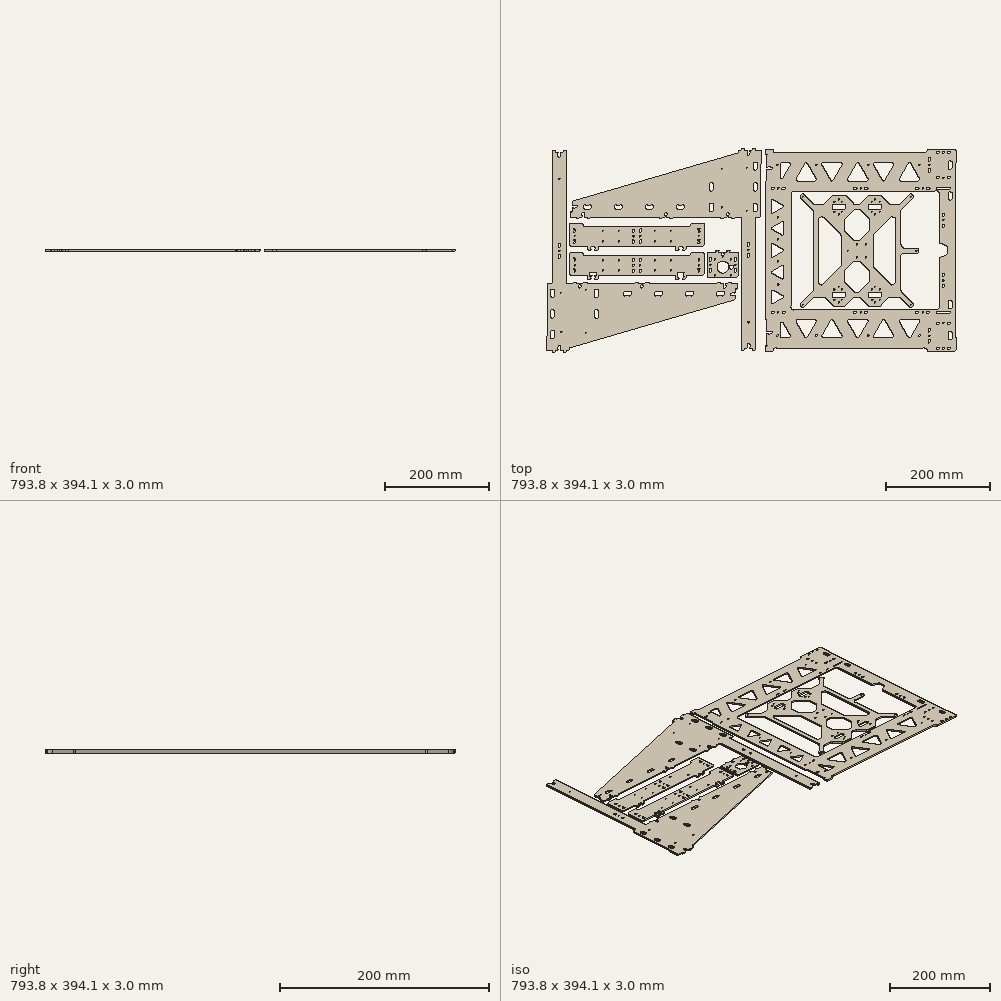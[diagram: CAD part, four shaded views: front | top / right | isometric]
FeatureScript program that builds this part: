
annotation { "Feature Type Name" : "Feature", "Feature Type Description" : "" }
export const myFeature = defineFeature(function(context is Context, id is Id, definition is map)
    precondition{}
    {
        {
            var Q0;
            Q0=qCreatedBy(makeId("Top.planeOp"),FACE);
            var sketch = newSketch(context, id + "F0", { "sketchPlane" : qUnion([Q0])});
            skFitSpline(sketch, "E0", {"points": [v(-205.76, 143.1) * mm, v(-205.54, 143.1) * mm, v(-205.33, 143.16) * mm, v(-205.16, 143.3) * mm]});
            skFitSpline(sketch, "E1", {"points": [v(-211.3, 181.1) * mm, v(-211.08, 181.1) * mm, v(-210.87, 181.16) * mm, v(-210.7, 181.3) * mm]});
            skFitSpline(sketch, "E2", {"points": [v(-203.99, 186.1) * mm, v(-204.2, 186.1) * mm, v(-204.41, 186.02) * mm, v(-204.59, 185.89) * mm]});
            skLineSegment(sketch, "E3", {"start": v(-205.16, 143.3) * mm, "end": v(-198.78, 148.1) * mm});
            skLineSegment(sketch, "E4", {"start": v(-210.7, 181.3) * mm, "end": v(-204.59, 185.89) * mm});
            skLineSegment(sketch, "E5", {"start": v(-213.3, 181.1) * mm, "end": v(-211.3, 181.1) * mm});
            skFitSpline(sketch, "E6", {"points": [v(-141.15, -185.58) * mm, v(-140.94, -185.58) * mm, v(-140.72, -185.5) * mm, v(-140.55, -185.38) * mm]});
            skFitSpline(sketch, "E7", {"points": [v(-146.69, -147.58) * mm, v(-146.47, -147.58) * mm, v(-146.26, -147.5) * mm, v(-146.09, -147.38) * mm]});
            skFitSpline(sketch, "E8", {"points": [v(-139.38, -142.58) * mm, v(-139.6, -142.58) * mm, v(-139.8, -142.65) * mm, v(-139.98, -142.78) * mm]});
            skLineSegment(sketch, "E9", {"start": v(-207.76, 143.1) * mm, "end": v(-205.9, 143.1) * mm});
            skLineSegment(sketch, "E10", {"start": v(-205.9, 143.1) * mm, "end": v(-205.76, 143.1) * mm});
            skLineSegment(sketch, "E11", {"start": v(-205.76, 143.1) * mm, "end": v(-205.76, 143.1) * mm});
            skLineSegment(sketch, "E12", {"start": v(-140.55, -185.38) * mm, "end": v(-134.18, -180.58) * mm});
            skLineSegment(sketch, "E13", {"start": v(-146.09, -147.38) * mm, "end": v(-139.98, -142.78) * mm});
            skLineSegment(sketch, "E14", {"start": v(-148.69, -147.58) * mm, "end": v(-146.68, -147.58) * mm});
            skFitSpline(sketch, "E15", {"points": [v(-352, -188.94) * mm, v(-352.22, -189) * mm, v(-352.36, -189.2) * mm, v(-352.36, -189.42) * mm]});
            skLineSegment(sketch, "E16", {"start": v(-143.15, -185.58) * mm, "end": v(-141.3, -185.58) * mm});
            skLineSegment(sketch, "E17", {"start": v(-141.3, -185.58) * mm, "end": v(-141.16, -185.58) * mm});
            skLineSegment(sketch, "E18", {"start": v(-141.16, -185.58) * mm, "end": v(-141.15, -185.58) * mm});
            skLineSegment(sketch, "E19", {"start": v(-396.81, -189.04) * mm, "end": v(-396.81, -194.04) * mm});
            skFitSpline(sketch, "E20", {"points": [v(-25.17, 188.94) * mm, v(-24.96, 189) * mm, v(-24.81, 189.2) * mm, v(-24.81, 189.42) * mm]});
            skLineSegment(sketch, "E21", {"start": v(-352.36, -189.42) * mm, "end": v(-352.36, -194.04) * mm});
            skFitSpline(sketch, "E22", {"points": [v(396.81, 190.1) * mm, v(396.81, 192.86) * mm, v(394.57, 195.1) * mm, v(391.81, 195.1) * mm]});
            skLineSegment(sketch, "E23", {"start": v(19.64, 194.04) * mm, "end": v(19.64, 189.04) * mm});
            skFitSpline(sketch, "E24", {"points": [v(332.72, 189.1) * mm, v(336.37, 189.1) * mm, v(339.55, 191.56) * mm, v(340.46, 195.1) * mm]});
            skLineSegment(sketch, "E25", {"start": v(-24.81, 194.04) * mm, "end": v(-24.81, 189.42) * mm});
            skFitSpline(sketch, "E26", {"points": [v(41.82, 195.1) * mm, v(42.73, 191.56) * mm, v(45.91, 189.1) * mm, v(49.56, 189.1) * mm]});
            skLineSegment(sketch, "E27", {"start": v(394.81, 168.1) * mm, "end": v(396.81, 170.1) * mm});
            skLineSegment(sketch, "E28", {"start": v(396.81, 170.1) * mm, "end": v(396.81, 190.1) * mm});
            skFitSpline(sketch, "E29", {"points": [v(29.05, 185.1) * mm, v(29.23, 185.1) * mm, v(29.4, 185.2) * mm, v(29.48, 185.35) * mm]});
            skFitSpline(sketch, "E30", {"points": [v(30.17, 184.66) * mm, v(30.35, 184.77) * mm, v(30.45, 184.98) * mm, v(30.4, 185.18) * mm]});
            skFitSpline(sketch, "E31", {"points": [v(30.4, 185.18) * mm, v(30.37, 185.4) * mm, v(30.21, 185.55) * mm, v(30, 185.59) * mm]});
            skFitSpline(sketch, "E32", {"points": [v(30, 185.59) * mm, v(29.8, 185.63) * mm, v(29.59, 185.53) * mm, v(29.48, 185.35) * mm]});
            skFitSpline(sketch, "E33", {"points": [v(30.17, 184.66) * mm, v(30.01, 184.57) * mm, v(29.92, 184.4) * mm, v(29.92, 184.23) * mm]});
            skLineSegment(sketch, "E34", {"start": v(391.81, 195.1) * mm, "end": v(340.46, 195.1) * mm});
            skFitSpline(sketch, "E35", {"points": [v(29.92, 134.31) * mm, v(29.92, 134.13) * mm, v(30.01, 133.97) * mm, v(30.17, 133.88) * mm]});
            skFitSpline(sketch, "E36", {"points": [v(29.48, 133.2) * mm, v(29.59, 133.01) * mm, v(29.8, 132.92) * mm, v(30, 132.95) * mm]});
            skFitSpline(sketch, "E37", {"points": [v(30, 132.95) * mm, v(30.21, 133) * mm, v(30.37, 133.15) * mm, v(30.4, 133.36) * mm]});
            skFitSpline(sketch, "E38", {"points": [v(30.4, 133.36) * mm, v(30.45, 133.57) * mm, v(30.35, 133.77) * mm, v(30.17, 133.88) * mm]});
            skFitSpline(sketch, "E39", {"points": [v(29.48, 133.2) * mm, v(29.4, 133.35) * mm, v(29.23, 133.45) * mm, v(29.05, 133.45) * mm]});
            skLineSegment(sketch, "E40", {"start": v(332.72, 189.1) * mm, "end": v(49.56, 189.1) * mm});
            skFitSpline(sketch, "E41", {"points": [v(29.05, -133.25) * mm, v(29.23, -133.25) * mm, v(29.4, -133.16) * mm, v(29.48, -133) * mm]});
            skFitSpline(sketch, "E42", {"points": [v(30.17, -133.68) * mm, v(30.35, -133.58) * mm, v(30.45, -133.37) * mm, v(30.4, -133.16) * mm]});
            skFitSpline(sketch, "E43", {"points": [v(30.4, -133.16) * mm, v(30.37, -132.96) * mm, v(30.21, -132.8) * mm, v(30, -132.76) * mm]});
            skFitSpline(sketch, "E44", {"points": [v(30, -132.76) * mm, v(29.8, -132.72) * mm, v(29.59, -132.82) * mm, v(29.48, -133) * mm]});
            skFitSpline(sketch, "E45", {"points": [v(30.17, -133.68) * mm, v(30.01, -133.77) * mm, v(29.92, -133.94) * mm, v(29.92, -134.12) * mm]});
            skLineSegment(sketch, "E46", {"start": v(41.82, 195.1) * mm, "end": v(26.82, 195.1) * mm});
            skLineSegment(sketch, "E47", {"start": v(26.82, 195.1) * mm, "end": v(26.82, 185.1) * mm});
            skLineSegment(sketch, "E48", {"start": v(26.82, 185.1) * mm, "end": v(29.05, 185.1) * mm});
            skFitSpline(sketch, "E49", {"points": [v(29.92, -184.03) * mm, v(29.92, -184.21) * mm, v(30.01, -184.38) * mm, v(30.17, -184.47) * mm]});
            skFitSpline(sketch, "E50", {"points": [v(29.48, -185.15) * mm, v(29.59, -185.33) * mm, v(29.8, -185.43) * mm, v(30, -185.4) * mm]});
            skFitSpline(sketch, "E51", {"points": [v(30, -185.4) * mm, v(30.21, -185.36) * mm, v(30.37, -185.2) * mm, v(30.4, -184.99) * mm]});
            skFitSpline(sketch, "E52", {"points": [v(30.4, -184.99) * mm, v(30.45, -184.78) * mm, v(30.35, -184.57) * mm, v(30.17, -184.47) * mm]});
            skFitSpline(sketch, "E53", {"points": [v(29.48, -185.15) * mm, v(29.4, -185) * mm, v(29.23, -184.9) * mm, v(29.05, -184.9) * mm]});
            skLineSegment(sketch, "E54", {"start": v(29.92, 184.23) * mm, "end": v(29.92, 160.87) * mm});
            skLineSegment(sketch, "E55", {"start": v(29.92, 160.87) * mm, "end": v(32.92, 160.87) * mm});
            skLineSegment(sketch, "E56", {"start": v(32.92, 160.87) * mm, "end": v(32.92, 162.15) * mm});
            skLineSegment(sketch, "E57", {"start": v(32.92, 162.15) * mm, "end": v(36.92, 162.15) * mm});
            skLineSegment(sketch, "E58", {"start": v(36.92, 162.15) * mm, "end": v(36.92, 160.87) * mm});
            skLineSegment(sketch, "E59", {"start": v(36.92, 160.87) * mm, "end": v(39.92, 160.87) * mm});
            skLineSegment(sketch, "E60", {"start": v(39.92, 160.87) * mm, "end": v(39.92, 157.67) * mm});
            skLineSegment(sketch, "E61", {"start": v(39.92, 157.67) * mm, "end": v(36.92, 157.67) * mm});
            skLineSegment(sketch, "E62", {"start": v(36.92, 157.67) * mm, "end": v(36.92, 156.4) * mm});
            skLineSegment(sketch, "E63", {"start": v(36.92, 156.4) * mm, "end": v(32.92, 156.4) * mm});
            skLineSegment(sketch, "E64", {"start": v(32.92, 156.4) * mm, "end": v(32.92, 157.67) * mm});
            skLineSegment(sketch, "E65", {"start": v(32.92, 157.67) * mm, "end": v(29.92, 157.67) * mm});
            skLineSegment(sketch, "E66", {"start": v(29.92, 157.67) * mm, "end": v(29.92, 134.31) * mm});
            skFitSpline(sketch, "E67", {"points": [v(49.56, -188.9) * mm, v(45.91, -188.9) * mm, v(42.73, -191.37) * mm, v(41.82, -194.9) * mm]});
            skLineSegment(sketch, "E68", {"start": v(29.05, 133.45) * mm, "end": v(26.82, 133.45) * mm});
            skLineSegment(sketch, "E69", {"start": v(26.82, 133.45) * mm, "end": v(26.82, -133.25) * mm});
            skLineSegment(sketch, "E70", {"start": v(26.82, -133.25) * mm, "end": v(29.05, -133.25) * mm});
            skFitSpline(sketch, "E71", {"points": [v(340.46, -194.9) * mm, v(339.55, -191.37) * mm, v(336.37, -188.9) * mm, v(332.72, -188.9) * mm]});
            skLineSegment(sketch, "E72", {"start": v(29.92, -134.12) * mm, "end": v(29.92, -157.48) * mm});
            skLineSegment(sketch, "E73", {"start": v(29.92, -157.48) * mm, "end": v(32.92, -157.48) * mm});
            skLineSegment(sketch, "E74", {"start": v(32.92, -157.48) * mm, "end": v(32.92, -156.2) * mm});
            skLineSegment(sketch, "E75", {"start": v(32.92, -156.2) * mm, "end": v(36.92, -156.2) * mm});
            skLineSegment(sketch, "E76", {"start": v(36.92, -156.2) * mm, "end": v(36.92, -157.48) * mm});
            skLineSegment(sketch, "E77", {"start": v(36.92, -157.48) * mm, "end": v(39.92, -157.48) * mm});
            skLineSegment(sketch, "E78", {"start": v(39.92, -157.48) * mm, "end": v(39.92, -160.68) * mm});
            skLineSegment(sketch, "E79", {"start": v(39.92, -160.68) * mm, "end": v(36.92, -160.68) * mm});
            skLineSegment(sketch, "E80", {"start": v(36.92, -160.68) * mm, "end": v(36.92, -161.95) * mm});
            skLineSegment(sketch, "E81", {"start": v(36.92, -161.95) * mm, "end": v(32.92, -161.95) * mm});
            skLineSegment(sketch, "E82", {"start": v(32.92, -161.95) * mm, "end": v(32.92, -160.68) * mm});
            skLineSegment(sketch, "E83", {"start": v(32.92, -160.68) * mm, "end": v(29.92, -160.68) * mm});
            skLineSegment(sketch, "E84", {"start": v(29.92, -160.68) * mm, "end": v(29.92, -184.03) * mm});
            skFitSpline(sketch, "E85", {"points": [v(391.81, -194.9) * mm, v(394.58, -194.9) * mm, v(396.81, -192.66) * mm, v(396.81, -189.9) * mm]});
            skLineSegment(sketch, "E86", {"start": v(29.05, -184.9) * mm, "end": v(26.82, -184.9) * mm});
            skLineSegment(sketch, "E87", {"start": v(26.82, -184.9) * mm, "end": v(26.82, -194.9) * mm});
            skLineSegment(sketch, "E88", {"start": v(26.82, -194.9) * mm, "end": v(41.82, -194.9) * mm});
            skLineSegment(sketch, "E89", {"start": v(49.56, -188.9) * mm, "end": v(332.72, -188.9) * mm});
            skFitSpline(sketch, "E90", {"points": [v(378.81, 6.82) * mm, v(378.81, 7.6) * mm, v(378.36, 8.3) * mm, v(377.66, 8.64) * mm]});
            skLineSegment(sketch, "E91", {"start": v(340.46, -194.9) * mm, "end": v(391.81, -194.9) * mm});
            skFitSpline(sketch, "E92", {"points": [v(363.69, 16.43) * mm, v(363.69, 15.65) * mm, v(364.14, 14.94) * mm, v(364.84, 14.61) * mm]});
            skLineSegment(sketch, "E93", {"start": v(396.81, -189.9) * mm, "end": v(396.81, -169.9) * mm});
            skLineSegment(sketch, "E94", {"start": v(396.81, -169.9) * mm, "end": v(394.81, -167.9) * mm});
            skLineSegment(sketch, "E95", {"start": v(394.81, -167.9) * mm, "end": v(394.81, 168.1) * mm});
            skFitSpline(sketch, "E96", {"points": [v(363.69, 107.1) * mm, v(363.69, 111.5) * mm, v(360.12, 115.09) * mm, v(355.7, 115.1) * mm]});
            skLineSegment(sketch, "E97", {"start": v(378.81, -6.62) * mm, "end": v(378.81, 6.82) * mm});
            skFitSpline(sketch, "E98", {"points": [v(84.82, 115.1) * mm, v(82.7, 115.1) * mm, v(80.66, 114.25) * mm, v(79.16, 112.75) * mm]});
            skFitSpline(sketch, "E99", {"points": [v(79.16, 112.75) * mm, v(77.66, 111.25) * mm, v(76.82, 109.22) * mm, v(76.82, 107.1) * mm]});
            skLineSegment(sketch, "E100", {"start": v(377.66, 8.64) * mm, "end": v(364.84, 14.61) * mm});
            skFitSpline(sketch, "E101", {"points": [v(76.82, -106.9) * mm, v(76.82, -111.32) * mm, v(80.4, -114.9) * mm, v(84.82, -114.9) * mm]});
            skLineSegment(sketch, "E102", {"start": v(363.69, 16.43) * mm, "end": v(363.69, 107.1) * mm});
            skFitSpline(sketch, "E103", {"points": [v(355.7, -114.9) * mm, v(360.12, -114.9) * mm, v(363.69, -111.31) * mm, v(363.69, -106.9) * mm]});
            skLineSegment(sketch, "E104", {"start": v(355.7, 115.1) * mm, "end": v(84.82, 115.1) * mm});
            skFitSpline(sketch, "E105", {"points": [v(364.85, -14.31) * mm, v(364.14, -14.64) * mm, v(363.69, -15.35) * mm, v(363.69, -16.13) * mm]});
            skLineSegment(sketch, "E106", {"start": v(76.82, 107.1) * mm, "end": v(76.82, -106.9) * mm});
            skFitSpline(sketch, "E107", {"points": [v(377.65, -8.44) * mm, v(378.36, -8.11) * mm, v(378.81, -7.4) * mm, v(378.81, -6.62) * mm]});
            skLineSegment(sketch, "E108", {"start": v(84.82, -114.9) * mm, "end": v(355.7, -114.9) * mm});
            skFitSpline(sketch, "E109", {"points": [v(289.45, -134.33) * mm, v(288.38, -134.33) * mm, v(287.39, -134.9) * mm, v(286.85, -135.83) * mm]});
            skFitSpline(sketch, "E110", {"points": [v(286.85, -135.83) * mm, v(286.32, -136.76) * mm, v(286.32, -137.9) * mm, v(286.85, -138.83) * mm]});
            skLineSegment(sketch, "E111", {"start": v(363.69, -106.9) * mm, "end": v(363.69, -16.13) * mm});
            skFitSpline(sketch, "E112", {"points": [v(303.55, -167.76) * mm, v(304.1, -168.68) * mm, v(305.08, -169.26) * mm, v(306.15, -169.26) * mm]});
            skFitSpline(sketch, "E113", {"points": [v(306.15, -169.26) * mm, v(307.22, -169.26) * mm, v(308.21, -168.68) * mm, v(308.75, -167.76) * mm]});
            skLineSegment(sketch, "E114", {"start": v(364.85, -14.31) * mm, "end": v(377.65, -8.44) * mm});
            skFitSpline(sketch, "E115", {"points": [v(325.45, -138.83) * mm, v(325.99, -137.9) * mm, v(325.99, -136.76) * mm, v(325.45, -135.83) * mm]});
            skFitSpline(sketch, "E116", {"points": [v(325.45, -135.83) * mm, v(324.92, -134.9) * mm, v(323.92, -134.33) * mm, v(322.85, -134.33) * mm]});
            skLineSegment(sketch, "E117", {"start": v(322.85, -134.33) * mm, "end": v(289.45, -134.33) * mm});
            skFitSpline(sketch, "E118", {"points": [v(236.85, -164.76) * mm, v(236.32, -165.68) * mm, v(236.32, -166.83) * mm, v(236.85, -167.76) * mm]});
            skFitSpline(sketch, "E119", {"points": [v(236.85, -167.76) * mm, v(237.4, -168.68) * mm, v(238.38, -169.26) * mm, v(239.45, -169.26) * mm]});
            skLineSegment(sketch, "E120", {"start": v(286.85, -138.83) * mm, "end": v(303.55, -167.76) * mm});
            skFitSpline(sketch, "E121", {"points": [v(258.75, -135.83) * mm, v(258.22, -134.9) * mm, v(257.23, -134.33) * mm, v(256.15, -134.33) * mm]});
            skFitSpline(sketch, "E122", {"points": [v(256.15, -134.33) * mm, v(255.08, -134.33) * mm, v(254.1, -134.9) * mm, v(253.56, -135.83) * mm]});
            skLineSegment(sketch, "E123", {"start": v(308.75, -167.76) * mm, "end": v(325.45, -138.83) * mm});
            skFitSpline(sketch, "E124", {"points": [v(272.85, -169.26) * mm, v(273.93, -169.26) * mm, v(274.92, -168.68) * mm, v(275.45, -167.76) * mm]});
            skFitSpline(sketch, "E125", {"points": [v(275.45, -167.76) * mm, v(275.99, -166.83) * mm, v(275.99, -165.68) * mm, v(275.45, -164.76) * mm]});
            skLineSegment(sketch, "E126", {"start": v(272.85, -169.26) * mm, "end": v(239.45, -169.26) * mm});
            skFitSpline(sketch, "E127", {"points": [v(189.45, -134.33) * mm, v(188.38, -134.33) * mm, v(187.4, -134.9) * mm, v(186.85, -135.83) * mm]});
            skFitSpline(sketch, "E128", {"points": [v(186.85, -135.83) * mm, v(186.32, -136.76) * mm, v(186.32, -137.9) * mm, v(186.85, -138.83) * mm]});
            skLineSegment(sketch, "E129", {"start": v(236.85, -164.76) * mm, "end": v(253.56, -135.83) * mm});
            skFitSpline(sketch, "E130", {"points": [v(203.56, -167.76) * mm, v(204.1, -168.68) * mm, v(205.08, -169.26) * mm, v(206.15, -169.26) * mm]});
            skFitSpline(sketch, "E131", {"points": [v(206.15, -169.26) * mm, v(207.23, -169.26) * mm, v(208.22, -168.68) * mm, v(208.75, -167.76) * mm]});
            skLineSegment(sketch, "E132", {"start": v(258.75, -135.83) * mm, "end": v(275.45, -164.76) * mm});
            skFitSpline(sketch, "E133", {"points": [v(225.45, -138.83) * mm, v(225.99, -137.9) * mm, v(225.99, -136.76) * mm, v(225.45, -135.83) * mm]});
            skFitSpline(sketch, "E134", {"points": [v(225.45, -135.83) * mm, v(224.92, -134.9) * mm, v(223.93, -134.33) * mm, v(222.85, -134.33) * mm]});
            skLineSegment(sketch, "E135", {"start": v(222.85, -134.33) * mm, "end": v(189.45, -134.33) * mm});
            skFitSpline(sketch, "E136", {"points": [v(136.86, -164.76) * mm, v(136.32, -165.68) * mm, v(136.32, -166.83) * mm, v(136.86, -167.76) * mm]});
            skFitSpline(sketch, "E137", {"points": [v(136.86, -167.76) * mm, v(137.4, -168.68) * mm, v(138.38, -169.26) * mm, v(139.45, -169.26) * mm]});
            skLineSegment(sketch, "E138", {"start": v(186.85, -138.83) * mm, "end": v(203.56, -167.76) * mm});
            skFitSpline(sketch, "E139", {"points": [v(158.75, -135.83) * mm, v(158.22, -134.9) * mm, v(157.23, -134.33) * mm, v(156.15, -134.33) * mm]});
            skFitSpline(sketch, "E140", {"points": [v(156.15, -134.33) * mm, v(155.08, -134.33) * mm, v(154.1, -134.9) * mm, v(153.56, -135.83) * mm]});
            skLineSegment(sketch, "E141", {"start": v(208.75, -167.76) * mm, "end": v(225.45, -138.83) * mm});
            skFitSpline(sketch, "E142", {"points": [v(172.86, -169.26) * mm, v(173.93, -169.26) * mm, v(174.92, -168.68) * mm, v(175.45, -167.76) * mm]});
            skFitSpline(sketch, "E143", {"points": [v(175.45, -167.76) * mm, v(175.99, -166.83) * mm, v(175.99, -165.68) * mm, v(175.45, -164.76) * mm]});
            skLineSegment(sketch, "E144", {"start": v(172.86, -169.26) * mm, "end": v(139.45, -169.26) * mm});
            skFitSpline(sketch, "E145", {"points": [v(89.45, -134.33) * mm, v(88.38, -134.33) * mm, v(87.4, -134.9) * mm, v(86.86, -135.83) * mm]});
            skFitSpline(sketch, "E146", {"points": [v(86.86, -135.83) * mm, v(86.32, -136.76) * mm, v(86.32, -137.9) * mm, v(86.86, -138.83) * mm]});
            skLineSegment(sketch, "E147", {"start": v(136.86, -164.76) * mm, "end": v(153.56, -135.83) * mm});
            skFitSpline(sketch, "E148", {"points": [v(103.56, -167.76) * mm, v(104.1, -168.68) * mm, v(105.08, -169.26) * mm, v(106.15, -169.26) * mm]});
            skFitSpline(sketch, "E149", {"points": [v(106.15, -169.26) * mm, v(107.23, -169.26) * mm, v(108.22, -168.68) * mm, v(108.75, -167.76) * mm]});
            skLineSegment(sketch, "E150", {"start": v(158.75, -135.83) * mm, "end": v(175.45, -164.76) * mm});
            skFitSpline(sketch, "E151", {"points": [v(125.45, -138.83) * mm, v(125.99, -137.9) * mm, v(125.99, -136.76) * mm, v(125.45, -135.83) * mm]});
            skFitSpline(sketch, "E152", {"points": [v(125.45, -135.83) * mm, v(124.92, -134.9) * mm, v(123.93, -134.33) * mm, v(122.86, -134.33) * mm]});
            skLineSegment(sketch, "E153", {"start": v(122.86, -134.33) * mm, "end": v(89.45, -134.33) * mm});
            skFitSpline(sketch, "E154", {"points": [v(286.85, 139.02) * mm, v(286.32, 138.1) * mm, v(286.32, 136.95) * mm, v(286.85, 136.02) * mm]});
            skFitSpline(sketch, "E155", {"points": [v(286.85, 136.02) * mm, v(287.39, 135.1) * mm, v(288.38, 134.52) * mm, v(289.45, 134.52) * mm]});
            skLineSegment(sketch, "E156", {"start": v(86.86, -138.83) * mm, "end": v(103.56, -167.76) * mm});
            skFitSpline(sketch, "E157", {"points": [v(308.75, 167.95) * mm, v(308.21, 168.88) * mm, v(307.22, 169.45) * mm, v(306.15, 169.45) * mm]});
            skFitSpline(sketch, "E158", {"points": [v(306.15, 169.45) * mm, v(305.08, 169.45) * mm, v(304.1, 168.88) * mm, v(303.55, 167.95) * mm]});
            skLineSegment(sketch, "E159", {"start": v(108.75, -167.76) * mm, "end": v(125.45, -138.83) * mm});
            skFitSpline(sketch, "E160", {"points": [v(322.85, 134.52) * mm, v(323.92, 134.52) * mm, v(324.92, 135.1) * mm, v(325.45, 136.02) * mm]});
            skFitSpline(sketch, "E161", {"points": [v(325.45, 136.02) * mm, v(325.99, 136.95) * mm, v(325.99, 138.1) * mm, v(325.45, 139.02) * mm]});
            skLineSegment(sketch, "E162", {"start": v(322.85, 134.52) * mm, "end": v(289.45, 134.52) * mm});
            skFitSpline(sketch, "E163", {"points": [v(239.45, 169.45) * mm, v(238.38, 169.45) * mm, v(237.4, 168.88) * mm, v(236.85, 167.95) * mm]});
            skFitSpline(sketch, "E164", {"points": [v(236.85, 167.95) * mm, v(236.32, 167.02) * mm, v(236.32, 165.88) * mm, v(236.85, 164.95) * mm]});
            skLineSegment(sketch, "E165", {"start": v(286.85, 139.02) * mm, "end": v(303.55, 167.95) * mm});
            skFitSpline(sketch, "E166", {"points": [v(253.56, 136.02) * mm, v(254.1, 135.1) * mm, v(255.08, 134.52) * mm, v(256.15, 134.52) * mm]});
            skFitSpline(sketch, "E167", {"points": [v(256.15, 134.52) * mm, v(257.23, 134.52) * mm, v(258.22, 135.1) * mm, v(258.75, 136.02) * mm]});
            skLineSegment(sketch, "E168", {"start": v(308.75, 167.95) * mm, "end": v(325.45, 139.02) * mm});
            skFitSpline(sketch, "E169", {"points": [v(275.45, 164.95) * mm, v(275.99, 165.88) * mm, v(275.99, 167.02) * mm, v(275.45, 167.95) * mm]});
            skFitSpline(sketch, "E170", {"points": [v(275.45, 167.95) * mm, v(274.92, 168.88) * mm, v(273.93, 169.45) * mm, v(272.85, 169.45) * mm]});
            skLineSegment(sketch, "E171", {"start": v(272.85, 169.45) * mm, "end": v(239.45, 169.45) * mm});
            skFitSpline(sketch, "E172", {"points": [v(186.85, 139.02) * mm, v(186.32, 138.1) * mm, v(186.32, 136.95) * mm, v(186.85, 136.02) * mm]});
            skFitSpline(sketch, "E173", {"points": [v(186.85, 136.02) * mm, v(187.4, 135.1) * mm, v(188.38, 134.52) * mm, v(189.45, 134.52) * mm]});
            skLineSegment(sketch, "E174", {"start": v(236.85, 164.95) * mm, "end": v(253.56, 136.02) * mm});
            skFitSpline(sketch, "E175", {"points": [v(208.75, 167.95) * mm, v(208.22, 168.88) * mm, v(207.23, 169.45) * mm, v(206.15, 169.45) * mm]});
            skFitSpline(sketch, "E176", {"points": [v(206.15, 169.45) * mm, v(205.08, 169.45) * mm, v(204.1, 168.88) * mm, v(203.56, 167.95) * mm]});
            skLineSegment(sketch, "E177", {"start": v(258.75, 136.02) * mm, "end": v(275.45, 164.95) * mm});
            skFitSpline(sketch, "E178", {"points": [v(222.85, 134.52) * mm, v(223.93, 134.52) * mm, v(224.92, 135.1) * mm, v(225.45, 136.02) * mm]});
            skFitSpline(sketch, "E179", {"points": [v(225.45, 136.02) * mm, v(225.99, 136.95) * mm, v(225.99, 138.1) * mm, v(225.45, 139.02) * mm]});
            skLineSegment(sketch, "E180", {"start": v(222.85, 134.52) * mm, "end": v(189.45, 134.52) * mm});
            skFitSpline(sketch, "E181", {"points": [v(139.45, 169.45) * mm, v(138.38, 169.45) * mm, v(137.4, 168.88) * mm, v(136.86, 167.95) * mm]});
            skFitSpline(sketch, "E182", {"points": [v(136.86, 167.95) * mm, v(136.32, 167.02) * mm, v(136.32, 165.88) * mm, v(136.86, 164.95) * mm]});
            skLineSegment(sketch, "E183", {"start": v(186.85, 139.02) * mm, "end": v(203.56, 167.95) * mm});
            skFitSpline(sketch, "E184", {"points": [v(153.56, 136.02) * mm, v(154.1, 135.1) * mm, v(155.08, 134.52) * mm, v(156.15, 134.52) * mm]});
            skFitSpline(sketch, "E185", {"points": [v(156.15, 134.52) * mm, v(157.23, 134.52) * mm, v(158.22, 135.1) * mm, v(158.75, 136.02) * mm]});
            skLineSegment(sketch, "E186", {"start": v(208.75, 167.95) * mm, "end": v(225.45, 139.02) * mm});
            skFitSpline(sketch, "E187", {"points": [v(175.45, 164.95) * mm, v(175.99, 165.88) * mm, v(175.99, 167.02) * mm, v(175.45, 167.95) * mm]});
            skFitSpline(sketch, "E188", {"points": [v(175.45, 167.95) * mm, v(174.92, 168.88) * mm, v(173.93, 169.45) * mm, v(172.86, 169.45) * mm]});
            skLineSegment(sketch, "E189", {"start": v(172.86, 169.45) * mm, "end": v(139.45, 169.45) * mm});
            skFitSpline(sketch, "E190", {"points": [v(86.86, 139.02) * mm, v(86.32, 138.1) * mm, v(86.32, 136.95) * mm, v(86.86, 136.02) * mm]});
            skFitSpline(sketch, "E191", {"points": [v(86.86, 136.02) * mm, v(87.4, 135.1) * mm, v(88.38, 134.52) * mm, v(89.45, 134.52) * mm]});
            skLineSegment(sketch, "E192", {"start": v(136.86, 164.95) * mm, "end": v(153.56, 136.02) * mm});
            skFitSpline(sketch, "E193", {"points": [v(108.75, 167.95) * mm, v(108.22, 168.88) * mm, v(107.23, 169.45) * mm, v(106.15, 169.45) * mm]});
            skFitSpline(sketch, "E194", {"points": [v(106.15, 169.45) * mm, v(105.08, 169.45) * mm, v(104.1, 168.88) * mm, v(103.56, 167.95) * mm]});
            skLineSegment(sketch, "E195", {"start": v(158.75, 136.02) * mm, "end": v(175.45, 164.95) * mm});
            skFitSpline(sketch, "E196", {"points": [v(122.86, 134.52) * mm, v(123.93, 134.52) * mm, v(124.92, 135.1) * mm, v(125.45, 136.02) * mm]});
            skFitSpline(sketch, "E197", {"points": [v(125.45, 136.02) * mm, v(125.99, 136.95) * mm, v(125.99, 138.1) * mm, v(125.45, 139.02) * mm]});
            skLineSegment(sketch, "E198", {"start": v(122.86, 134.52) * mm, "end": v(89.45, 134.52) * mm});
            skFitSpline(sketch, "E199", {"points": [v(39.12, -101.23) * mm, v(39.12, -101.95) * mm, v(39.51, -102.62) * mm, v(40.14, -102.98) * mm]});
            skFitSpline(sketch, "E200", {"points": [v(40.14, -102.98) * mm, v(40.76, -103.34) * mm, v(41.54, -103.34) * mm, v(42.16, -102.98) * mm]});
            skLineSegment(sketch, "E201", {"start": v(86.86, 139.02) * mm, "end": v(103.56, 167.95) * mm});
            skFitSpline(sketch, "E202", {"points": [v(61.69, -91.7) * mm, v(62.31, -91.35) * mm, v(62.7, -90.68) * mm, v(62.7, -89.96) * mm]});
            skFitSpline(sketch, "E203", {"points": [v(62.7, -89.96) * mm, v(62.7, -89.23) * mm, v(62.31, -88.56) * mm, v(61.69, -88.2) * mm]});
            skLineSegment(sketch, "E204", {"start": v(108.75, 167.95) * mm, "end": v(125.45, 139.02) * mm});
            skFitSpline(sketch, "E205", {"points": [v(42.16, -76.93) * mm, v(41.54, -76.57) * mm, v(40.76, -76.57) * mm, v(40.14, -76.93) * mm]});
            skFitSpline(sketch, "E206", {"points": [v(40.14, -76.93) * mm, v(39.51, -77.3) * mm, v(39.12, -77.96) * mm, v(39.12, -78.68) * mm]});
            skLineSegment(sketch, "E207", {"start": v(39.12, -78.68) * mm, "end": v(39.12, -101.23) * mm});
            skFitSpline(sketch, "E208", {"points": [v(59.66, -55.44) * mm, v(60.29, -55.8) * mm, v(61.06, -55.8) * mm, v(61.69, -55.44) * mm]});
            skFitSpline(sketch, "E209", {"points": [v(61.69, -55.44) * mm, v(62.31, -55.08) * mm, v(62.7, -54.4) * mm, v(62.7, -53.68) * mm]});
            skLineSegment(sketch, "E210", {"start": v(42.16, -102.98) * mm, "end": v(61.69, -91.7) * mm});
            skFitSpline(sketch, "E211", {"points": [v(40.14, -40.66) * mm, v(39.51, -41.02) * mm, v(39.12, -41.69) * mm, v(39.12, -42.41) * mm]});
            skFitSpline(sketch, "E212", {"points": [v(39.12, -42.41) * mm, v(39.12, -43.13) * mm, v(39.51, -43.8) * mm, v(40.14, -44.16) * mm]});
            skLineSegment(sketch, "E213", {"start": v(61.69, -88.2) * mm, "end": v(42.16, -76.93) * mm});
            skFitSpline(sketch, "E214", {"points": [v(62.7, -31.14) * mm, v(62.7, -30.41) * mm, v(62.31, -29.75) * mm, v(61.69, -29.38) * mm]});
            skFitSpline(sketch, "E215", {"points": [v(61.69, -29.38) * mm, v(61.06, -29.02) * mm, v(60.29, -29.02) * mm, v(59.66, -29.38) * mm]});
            skLineSegment(sketch, "E216", {"start": v(62.7, -31.14) * mm, "end": v(62.7, -53.68) * mm});
            skFitSpline(sketch, "E217", {"points": [v(39.12, -11.18) * mm, v(39.12, -11.9) * mm, v(39.51, -12.58) * mm, v(40.14, -12.94) * mm]});
            skFitSpline(sketch, "E218", {"points": [v(40.14, -12.94) * mm, v(40.76, -13.3) * mm, v(41.54, -13.3) * mm, v(42.16, -12.94) * mm]});
            skLineSegment(sketch, "E219", {"start": v(59.66, -55.44) * mm, "end": v(40.14, -44.16) * mm});
            skFitSpline(sketch, "E220", {"points": [v(61.69, -1.66) * mm, v(62.31, -1.3) * mm, v(62.7, -0.63) * mm, v(62.7, 0.09) * mm]});
            skFitSpline(sketch, "E221", {"points": [v(62.7, 0.09) * mm, v(62.7, 0.81) * mm, v(62.31, 1.48) * mm, v(61.69, 1.84) * mm]});
            skLineSegment(sketch, "E222", {"start": v(40.14, -40.66) * mm, "end": v(59.66, -29.38) * mm});
            skFitSpline(sketch, "E223", {"points": [v(42.16, 13.12) * mm, v(41.54, 13.48) * mm, v(40.76, 13.48) * mm, v(40.14, 13.12) * mm]});
            skFitSpline(sketch, "E224", {"points": [v(40.14, 13.12) * mm, v(39.51, 12.75) * mm, v(39.12, 12.09) * mm, v(39.12, 11.36) * mm]});
            skLineSegment(sketch, "E225", {"start": v(39.12, 11.36) * mm, "end": v(39.12, -11.18) * mm});
            skFitSpline(sketch, "E226", {"points": [v(59.66, 29.57) * mm, v(60.29, 29.2) * mm, v(61.06, 29.2) * mm, v(61.69, 29.57) * mm]});
            skFitSpline(sketch, "E227", {"points": [v(61.69, 29.57) * mm, v(62.31, 29.93) * mm, v(62.7, 30.6) * mm, v(62.7, 31.32) * mm]});
            skLineSegment(sketch, "E228", {"start": v(42.16, -12.94) * mm, "end": v(61.69, -1.66) * mm});
            skFitSpline(sketch, "E229", {"points": [v(40.14, 44.35) * mm, v(39.51, 43.99) * mm, v(39.12, 43.32) * mm, v(39.12, 42.6) * mm]});
            skFitSpline(sketch, "E230", {"points": [v(39.12, 42.6) * mm, v(39.12, 41.87) * mm, v(39.51, 41.2) * mm, v(40.14, 40.84) * mm]});
            skLineSegment(sketch, "E231", {"start": v(61.69, 1.84) * mm, "end": v(42.16, 13.12) * mm});
            skFitSpline(sketch, "E232", {"points": [v(62.7, 53.87) * mm, v(62.7, 54.6) * mm, v(62.31, 55.26) * mm, v(61.69, 55.62) * mm]});
            skFitSpline(sketch, "E233", {"points": [v(61.69, 55.62) * mm, v(61.06, 55.99) * mm, v(60.29, 55.99) * mm, v(59.66, 55.62) * mm]});
            skLineSegment(sketch, "E234", {"start": v(62.7, 53.87) * mm, "end": v(62.7, 31.32) * mm});
            skFitSpline(sketch, "E235", {"points": [v(39.12, 73.82) * mm, v(39.12, 73.1) * mm, v(39.51, 72.43) * mm, v(40.14, 72.07) * mm]});
            skFitSpline(sketch, "E236", {"points": [v(40.14, 72.07) * mm, v(40.76, 71.7) * mm, v(41.54, 71.7) * mm, v(42.16, 72.07) * mm]});
            skLineSegment(sketch, "E237", {"start": v(59.66, 29.57) * mm, "end": v(40.14, 40.84) * mm});
            skFitSpline(sketch, "E238", {"points": [v(61.69, 83.34) * mm, v(62.31, 83.7) * mm, v(62.7, 84.37) * mm, v(62.7, 85.1) * mm]});
            skFitSpline(sketch, "E239", {"points": [v(62.7, 85.1) * mm, v(62.7, 85.82) * mm, v(62.31, 86.49) * mm, v(61.69, 86.85) * mm]});
            skLineSegment(sketch, "E240", {"start": v(40.14, 44.35) * mm, "end": v(59.66, 55.62) * mm});
            skFitSpline(sketch, "E241", {"points": [v(42.16, 98.12) * mm, v(41.54, 98.49) * mm, v(40.76, 98.49) * mm, v(40.14, 98.12) * mm]});
            skFitSpline(sketch, "E242", {"points": [v(40.14, 98.12) * mm, v(39.51, 97.76) * mm, v(39.12, 97.1) * mm, v(39.12, 96.37) * mm]});
            skLineSegment(sketch, "E243", {"start": v(39.12, 96.37) * mm, "end": v(39.12, 73.82) * mm});
            skFitSpline(sketch, "E244", {"points": [v(388.81, -160.9) * mm, v(388.81, -159.47) * mm, v(388.05, -158.15) * mm, v(386.81, -157.44) * mm]});
            skFitSpline(sketch, "E245", {"points": [v(386.81, -157.44) * mm, v(385.58, -156.72) * mm, v(384.05, -156.72) * mm, v(382.81, -157.44) * mm]});
            skFitSpline(sketch, "E246", {"points": [v(382.81, -157.44) * mm, v(381.58, -158.15) * mm, v(380.81, -159.47) * mm, v(380.81, -160.9) * mm]});
            skLineSegment(sketch, "E247", {"start": v(42.16, 72.07) * mm, "end": v(61.69, 83.34) * mm});
            skFitSpline(sketch, "E248", {"points": [v(380.81, -168.9) * mm, v(380.81, -170.33) * mm, v(381.58, -171.65) * mm, v(382.81, -172.36) * mm]});
            skFitSpline(sketch, "E249", {"points": [v(382.81, -172.36) * mm, v(384.05, -173.08) * mm, v(385.58, -173.08) * mm, v(386.81, -172.36) * mm]});
            skFitSpline(sketch, "E250", {"points": [v(386.81, -172.36) * mm, v(388.05, -171.65) * mm, v(388.81, -170.33) * mm, v(388.81, -168.9) * mm]});
            skLineSegment(sketch, "E251", {"start": v(61.69, 86.85) * mm, "end": v(42.16, 98.12) * mm});
            skFitSpline(sketch, "E252", {"points": [v(388.81, -100.9) * mm, v(388.81, -99.47) * mm, v(388.05, -98.15) * mm, v(386.81, -97.44) * mm]});
            skFitSpline(sketch, "E253", {"points": [v(386.81, -97.44) * mm, v(385.58, -96.72) * mm, v(384.05, -96.72) * mm, v(382.81, -97.44) * mm]});
            skFitSpline(sketch, "E254", {"points": [v(382.81, -97.44) * mm, v(381.58, -98.15) * mm, v(380.81, -99.47) * mm, v(380.81, -100.9) * mm]});
            skLineSegment(sketch, "E255", {"start": v(388.81, -168.9) * mm, "end": v(388.81, -160.9) * mm});
            skFitSpline(sketch, "E256", {"points": [v(380.81, -108.9) * mm, v(380.81, -110.33) * mm, v(381.58, -111.65) * mm, v(382.81, -112.37) * mm]});
            skFitSpline(sketch, "E257", {"points": [v(382.81, -112.37) * mm, v(384.05, -113.08) * mm, v(385.58, -113.08) * mm, v(386.81, -112.37) * mm]});
            skFitSpline(sketch, "E258", {"points": [v(386.81, -112.37) * mm, v(388.05, -111.65) * mm, v(388.81, -110.33) * mm, v(388.81, -108.9) * mm]});
            skLineSegment(sketch, "E259", {"start": v(380.81, -160.9) * mm, "end": v(380.81, -168.9) * mm});
            skFitSpline(sketch, "E260", {"points": [v(388.81, 109.1) * mm, v(388.81, 110.53) * mm, v(388.05, 111.85) * mm, v(386.81, 112.56) * mm]});
            skFitSpline(sketch, "E261", {"points": [v(386.81, 112.56) * mm, v(385.58, 113.28) * mm, v(384.05, 113.28) * mm, v(382.81, 112.56) * mm]});
            skFitSpline(sketch, "E262", {"points": [v(382.81, 112.56) * mm, v(381.58, 111.85) * mm, v(380.81, 110.53) * mm, v(380.81, 109.1) * mm]});
            skLineSegment(sketch, "E263", {"start": v(388.81, -108.9) * mm, "end": v(388.81, -100.9) * mm});
            skFitSpline(sketch, "E264", {"points": [v(380.81, 101.1) * mm, v(380.81, 99.67) * mm, v(381.58, 98.35) * mm, v(382.81, 97.63) * mm]});
            skFitSpline(sketch, "E265", {"points": [v(382.81, 97.63) * mm, v(384.05, 96.92) * mm, v(385.58, 96.92) * mm, v(386.81, 97.63) * mm]});
            skFitSpline(sketch, "E266", {"points": [v(386.81, 97.63) * mm, v(388.05, 98.35) * mm, v(388.81, 99.67) * mm, v(388.81, 101.1) * mm]});
            skLineSegment(sketch, "E267", {"start": v(380.81, -100.9) * mm, "end": v(380.81, -108.9) * mm});
            skFitSpline(sketch, "E268", {"points": [v(388.81, 169.1) * mm, v(388.81, 170.53) * mm, v(388.05, 171.85) * mm, v(386.81, 172.56) * mm]});
            skFitSpline(sketch, "E269", {"points": [v(386.81, 172.56) * mm, v(385.58, 173.27) * mm, v(384.05, 173.27) * mm, v(382.81, 172.56) * mm]});
            skFitSpline(sketch, "E270", {"points": [v(382.81, 172.56) * mm, v(381.58, 171.85) * mm, v(380.81, 170.53) * mm, v(380.81, 169.1) * mm]});
            skLineSegment(sketch, "E271", {"start": v(388.81, 101.1) * mm, "end": v(388.81, 109.1) * mm});
            skFitSpline(sketch, "E272", {"points": [v(380.81, 161.1) * mm, v(380.81, 159.67) * mm, v(381.58, 158.35) * mm, v(382.81, 157.63) * mm]});
            skFitSpline(sketch, "E273", {"points": [v(382.81, 157.63) * mm, v(384.05, 156.92) * mm, v(385.58, 156.92) * mm, v(386.81, 157.63) * mm]});
            skFitSpline(sketch, "E274", {"points": [v(386.81, 157.63) * mm, v(388.05, 158.35) * mm, v(388.81, 159.67) * mm, v(388.81, 161.1) * mm]});
            skFitSpline(sketch, "E275", {"points": [v(358.11, -119.3) * mm, v(358.11, -119.11) * mm, v(358.02, -118.95) * mm, v(357.86, -118.86) * mm]});
            skFitSpline(sketch, "E276", {"points": [v(358.55, -118.18) * mm, v(358.44, -118) * mm, v(358.23, -117.9) * mm, v(358.03, -117.93) * mm]});
            skFitSpline(sketch, "E277", {"points": [v(358.03, -117.93) * mm, v(357.82, -117.97) * mm, v(357.66, -118.13) * mm, v(357.62, -118.34) * mm]});
            skFitSpline(sketch, "E278", {"points": [v(357.62, -118.34) * mm, v(357.58, -118.55) * mm, v(357.68, -118.75) * mm, v(357.86, -118.86) * mm]});
            skFitSpline(sketch, "E279", {"points": [v(358.55, -118.18) * mm, v(358.64, -118.33) * mm, v(358.8, -118.43) * mm, v(358.98, -118.43) * mm]});
            skLineSegment(sketch, "E280", {"start": v(380.81, 109.1) * mm, "end": v(380.81, 101.1) * mm});
            skFitSpline(sketch, "E281", {"points": [v(384.65, -118.43) * mm, v(384.83, -118.43) * mm, v(385, -118.33) * mm, v(385.08, -118.18) * mm]});
            skFitSpline(sketch, "E282", {"points": [v(385.76, -118.86) * mm, v(385.95, -118.75) * mm, v(386.04, -118.55) * mm, v(386, -118.34) * mm]});
            skFitSpline(sketch, "E283", {"points": [v(386, -118.34) * mm, v(385.97, -118.13) * mm, v(385.8, -117.97) * mm, v(385.6, -117.93) * mm]});
            skFitSpline(sketch, "E284", {"points": [v(385.6, -117.93) * mm, v(385.4, -117.9) * mm, v(385.19, -118) * mm, v(385.08, -118.18) * mm]});
            skFitSpline(sketch, "E285", {"points": [v(385.76, -118.86) * mm, v(385.6, -118.95) * mm, v(385.51, -119.11) * mm, v(385.51, -119.3) * mm]});
            skLineSegment(sketch, "E286", {"start": v(388.81, 161.1) * mm, "end": v(388.81, 169.1) * mm});
            skFitSpline(sketch, "E287", {"points": [v(385.51, -120.86) * mm, v(385.51, -121.04) * mm, v(385.6, -121.2) * mm, v(385.76, -121.3) * mm]});
            skFitSpline(sketch, "E288", {"points": [v(385.08, -121.98) * mm, v(385.19, -122.16) * mm, v(385.4, -122.25) * mm, v(385.6, -122.22) * mm]});
            skFitSpline(sketch, "E289", {"points": [v(385.6, -122.22) * mm, v(385.8, -122.18) * mm, v(385.97, -122.02) * mm, v(386, -121.81) * mm]});
            skFitSpline(sketch, "E290", {"points": [v(386, -121.81) * mm, v(386.04, -121.6) * mm, v(385.95, -121.4) * mm, v(385.76, -121.3) * mm]});
            skFitSpline(sketch, "E291", {"points": [v(385.08, -121.98) * mm, v(385, -121.82) * mm, v(384.83, -121.73) * mm, v(384.65, -121.73) * mm]});
            skLineSegment(sketch, "E292", {"start": v(380.81, 169.1) * mm, "end": v(380.81, 161.1) * mm});
            skFitSpline(sketch, "E293", {"points": [v(358.98, -121.73) * mm, v(358.8, -121.73) * mm, v(358.64, -121.82) * mm, v(358.55, -121.98) * mm]});
            skFitSpline(sketch, "E294", {"points": [v(357.86, -121.3) * mm, v(357.68, -121.4) * mm, v(357.58, -121.6) * mm, v(357.62, -121.81) * mm]});
            skFitSpline(sketch, "E295", {"points": [v(357.62, -121.81) * mm, v(357.66, -122.02) * mm, v(357.82, -122.18) * mm, v(358.03, -122.22) * mm]});
            skFitSpline(sketch, "E296", {"points": [v(358.03, -122.22) * mm, v(358.23, -122.25) * mm, v(358.44, -122.16) * mm, v(358.55, -121.98) * mm]});
            skFitSpline(sketch, "E297", {"points": [v(357.86, -121.3) * mm, v(358.02, -121.2) * mm, v(358.11, -121.04) * mm, v(358.11, -120.86) * mm]});
            skLineSegment(sketch, "E298", {"start": v(358.98, -118.43) * mm, "end": v(384.65, -118.43) * mm});
            skFitSpline(sketch, "E299", {"points": [v(358.11, 121.06) * mm, v(358.11, 121.23) * mm, v(358.02, 121.4) * mm, v(357.86, 121.49) * mm]});
            skFitSpline(sketch, "E300", {"points": [v(358.55, 122.17) * mm, v(358.44, 122.35) * mm, v(358.23, 122.45) * mm, v(358.03, 122.41) * mm]});
            skFitSpline(sketch, "E301", {"points": [v(358.03, 122.41) * mm, v(357.82, 122.38) * mm, v(357.66, 122.22) * mm, v(357.62, 122) * mm]});
            skFitSpline(sketch, "E302", {"points": [v(357.62, 122) * mm, v(357.58, 121.8) * mm, v(357.68, 121.6) * mm, v(357.86, 121.49) * mm]});
            skFitSpline(sketch, "E303", {"points": [v(358.55, 122.17) * mm, v(358.64, 122.02) * mm, v(358.8, 121.92) * mm, v(358.98, 121.92) * mm]});
            skLineSegment(sketch, "E304", {"start": v(385.51, -119.3) * mm, "end": v(385.51, -120.86) * mm});
            skFitSpline(sketch, "E305", {"points": [v(384.65, 121.92) * mm, v(384.83, 121.92) * mm, v(385, 122.02) * mm, v(385.08, 122.17) * mm]});
            skFitSpline(sketch, "E306", {"points": [v(385.76, 121.49) * mm, v(385.95, 121.6) * mm, v(386.04, 121.8) * mm, v(386, 122) * mm]});
            skFitSpline(sketch, "E307", {"points": [v(386, 122) * mm, v(385.97, 122.22) * mm, v(385.8, 122.38) * mm, v(385.6, 122.41) * mm]});
            skFitSpline(sketch, "E308", {"points": [v(385.6, 122.41) * mm, v(385.4, 122.45) * mm, v(385.19, 122.35) * mm, v(385.08, 122.17) * mm]});
            skFitSpline(sketch, "E309", {"points": [v(385.76, 121.49) * mm, v(385.6, 121.4) * mm, v(385.51, 121.23) * mm, v(385.51, 121.06) * mm]});
            skLineSegment(sketch, "E310", {"start": v(384.65, -121.73) * mm, "end": v(358.98, -121.73) * mm});
            skFitSpline(sketch, "E311", {"points": [v(385.51, 119.49) * mm, v(385.51, 119.3) * mm, v(385.6, 119.14) * mm, v(385.76, 119.05) * mm]});
            skFitSpline(sketch, "E312", {"points": [v(385.08, 118.37) * mm, v(385.19, 118.19) * mm, v(385.4, 118.1) * mm, v(385.6, 118.13) * mm]});
            skFitSpline(sketch, "E313", {"points": [v(385.6, 118.13) * mm, v(385.8, 118.17) * mm, v(385.97, 118.33) * mm, v(386, 118.53) * mm]});
            skFitSpline(sketch, "E314", {"points": [v(386, 118.53) * mm, v(386.04, 118.74) * mm, v(385.95, 118.95) * mm, v(385.76, 119.05) * mm]});
            skFitSpline(sketch, "E315", {"points": [v(385.08, 118.37) * mm, v(385, 118.53) * mm, v(384.83, 118.62) * mm, v(384.65, 118.62) * mm]});
            skLineSegment(sketch, "E316", {"start": v(358.11, -120.86) * mm, "end": v(358.11, -119.3) * mm});
            skFitSpline(sketch, "E317", {"points": [v(358.98, 118.62) * mm, v(358.8, 118.62) * mm, v(358.64, 118.53) * mm, v(358.55, 118.37) * mm]});
            skFitSpline(sketch, "E318", {"points": [v(357.86, 119.05) * mm, v(357.68, 118.95) * mm, v(357.58, 118.74) * mm, v(357.62, 118.53) * mm]});
            skFitSpline(sketch, "E319", {"points": [v(357.62, 118.53) * mm, v(357.66, 118.33) * mm, v(357.82, 118.17) * mm, v(358.03, 118.13) * mm]});
            skFitSpline(sketch, "E320", {"points": [v(358.03, 118.13) * mm, v(358.23, 118.1) * mm, v(358.44, 118.19) * mm, v(358.55, 118.37) * mm]});
            skFitSpline(sketch, "E321", {"points": [v(357.86, 119.05) * mm, v(358.02, 119.14) * mm, v(358.11, 119.3) * mm, v(358.11, 119.49) * mm]});
            skLineSegment(sketch, "E322", {"start": v(358.98, 121.92) * mm, "end": v(384.65, 121.92) * mm});
            skFitSpline(sketch, "E323", {"points": [v(379.31, -188.94) * mm, v(379.31, -188.76) * mm, v(379.22, -188.6) * mm, v(379.06, -188.5) * mm]});
            skFitSpline(sketch, "E324", {"points": [v(379.75, -187.82) * mm, v(379.64, -187.64) * mm, v(379.43, -187.54) * mm, v(379.23, -187.58) * mm]});
            skFitSpline(sketch, "E325", {"points": [v(379.23, -187.58) * mm, v(379.02, -187.61) * mm, v(378.86, -187.78) * mm, v(378.82, -187.98) * mm]});
            skFitSpline(sketch, "E326", {"points": [v(378.82, -187.98) * mm, v(378.78, -188.2) * mm, v(378.88, -188.4) * mm, v(379.06, -188.5) * mm]});
            skFitSpline(sketch, "E327", {"points": [v(379.75, -187.82) * mm, v(379.84, -187.98) * mm, v(380, -188.07) * mm, v(380.18, -188.07) * mm]});
            skLineSegment(sketch, "E328", {"start": v(385.51, 121.06) * mm, "end": v(385.51, 119.49) * mm});
            skFitSpline(sketch, "E329", {"points": [v(384.65, -188.07) * mm, v(384.83, -188.07) * mm, v(385, -187.98) * mm, v(385.08, -187.82) * mm]});
            skFitSpline(sketch, "E330", {"points": [v(385.76, -188.5) * mm, v(385.95, -188.4) * mm, v(386.04, -188.2) * mm, v(386, -187.98) * mm]});
            skFitSpline(sketch, "E331", {"points": [v(386, -187.98) * mm, v(385.97, -187.78) * mm, v(385.8, -187.61) * mm, v(385.6, -187.58) * mm]});
            skFitSpline(sketch, "E332", {"points": [v(385.6, -187.58) * mm, v(385.4, -187.54) * mm, v(385.19, -187.64) * mm, v(385.08, -187.82) * mm]});
            skFitSpline(sketch, "E333", {"points": [v(385.76, -188.5) * mm, v(385.6, -188.6) * mm, v(385.51, -188.76) * mm, v(385.51, -188.94) * mm]});
            skLineSegment(sketch, "E334", {"start": v(384.65, 118.62) * mm, "end": v(358.98, 118.62) * mm});
            skFitSpline(sketch, "E335", {"points": [v(385.51, -190.5) * mm, v(385.51, -190.68) * mm, v(385.6, -190.85) * mm, v(385.76, -190.94) * mm]});
            skFitSpline(sketch, "E336", {"points": [v(385.08, -191.62) * mm, v(385.19, -191.8) * mm, v(385.4, -191.9) * mm, v(385.6, -191.86) * mm]});
            skFitSpline(sketch, "E337", {"points": [v(385.6, -191.86) * mm, v(385.8, -191.83) * mm, v(385.97, -191.66) * mm, v(386, -191.46) * mm]});
            skFitSpline(sketch, "E338", {"points": [v(386, -191.46) * mm, v(386.04, -191.25) * mm, v(385.95, -191.04) * mm, v(385.76, -190.94) * mm]});
            skFitSpline(sketch, "E339", {"points": [v(385.08, -191.62) * mm, v(385, -191.47) * mm, v(384.83, -191.37) * mm, v(384.65, -191.37) * mm]});
            skLineSegment(sketch, "E340", {"start": v(358.11, 119.49) * mm, "end": v(358.11, 121.06) * mm});
            skFitSpline(sketch, "E341", {"points": [v(380.18, -191.37) * mm, v(380, -191.37) * mm, v(379.84, -191.47) * mm, v(379.75, -191.62) * mm]});
            skFitSpline(sketch, "E342", {"points": [v(379.06, -190.94) * mm, v(378.88, -191.04) * mm, v(378.78, -191.25) * mm, v(378.82, -191.46) * mm]});
            skFitSpline(sketch, "E343", {"points": [v(378.82, -191.46) * mm, v(378.86, -191.66) * mm, v(379.02, -191.83) * mm, v(379.23, -191.86) * mm]});
            skFitSpline(sketch, "E344", {"points": [v(379.23, -191.86) * mm, v(379.43, -191.9) * mm, v(379.64, -191.8) * mm, v(379.75, -191.62) * mm]});
            skFitSpline(sketch, "E345", {"points": [v(379.06, -190.94) * mm, v(379.22, -190.85) * mm, v(379.31, -190.68) * mm, v(379.31, -190.5) * mm]});
            skLineSegment(sketch, "E346", {"start": v(380.18, -188.07) * mm, "end": v(384.65, -188.07) * mm});
            skFitSpline(sketch, "E347", {"points": [v(358.11, -188.94) * mm, v(358.11, -188.76) * mm, v(358.02, -188.6) * mm, v(357.86, -188.5) * mm]});
            skFitSpline(sketch, "E348", {"points": [v(358.55, -187.82) * mm, v(358.44, -187.64) * mm, v(358.23, -187.54) * mm, v(358.03, -187.58) * mm]});
            skFitSpline(sketch, "E349", {"points": [v(358.03, -187.58) * mm, v(357.82, -187.61) * mm, v(357.66, -187.78) * mm, v(357.62, -187.98) * mm]});
            skFitSpline(sketch, "E350", {"points": [v(357.62, -187.98) * mm, v(357.58, -188.2) * mm, v(357.68, -188.4) * mm, v(357.86, -188.5) * mm]});
            skFitSpline(sketch, "E351", {"points": [v(358.55, -187.82) * mm, v(358.64, -187.98) * mm, v(358.8, -188.07) * mm, v(358.98, -188.07) * mm]});
            skLineSegment(sketch, "E352", {"start": v(385.51, -188.94) * mm, "end": v(385.51, -190.5) * mm});
            skFitSpline(sketch, "E353", {"points": [v(363.45, -188.07) * mm, v(363.63, -188.07) * mm, v(363.8, -187.98) * mm, v(363.88, -187.82) * mm]});
            skFitSpline(sketch, "E354", {"points": [v(364.56, -188.5) * mm, v(364.75, -188.4) * mm, v(364.84, -188.2) * mm, v(364.8, -187.98) * mm]});
            skFitSpline(sketch, "E355", {"points": [v(364.8, -187.98) * mm, v(364.77, -187.78) * mm, v(364.6, -187.61) * mm, v(364.4, -187.58) * mm]});
            skFitSpline(sketch, "E356", {"points": [v(364.4, -187.58) * mm, v(364.2, -187.54) * mm, v(363.99, -187.64) * mm, v(363.88, -187.82) * mm]});
            skFitSpline(sketch, "E357", {"points": [v(364.56, -188.5) * mm, v(364.4, -188.6) * mm, v(364.31, -188.76) * mm, v(364.31, -188.94) * mm]});
            skLineSegment(sketch, "E358", {"start": v(384.65, -191.37) * mm, "end": v(380.18, -191.37) * mm});
            skFitSpline(sketch, "E359", {"points": [v(364.31, -190.5) * mm, v(364.31, -190.68) * mm, v(364.4, -190.85) * mm, v(364.56, -190.94) * mm]});
            skFitSpline(sketch, "E360", {"points": [v(363.88, -191.62) * mm, v(363.99, -191.8) * mm, v(364.2, -191.9) * mm, v(364.4, -191.86) * mm]});
            skFitSpline(sketch, "E361", {"points": [v(364.4, -191.86) * mm, v(364.6, -191.83) * mm, v(364.77, -191.66) * mm, v(364.8, -191.46) * mm]});
            skFitSpline(sketch, "E362", {"points": [v(364.8, -191.46) * mm, v(364.84, -191.25) * mm, v(364.75, -191.04) * mm, v(364.56, -190.94) * mm]});
            skFitSpline(sketch, "E363", {"points": [v(363.88, -191.62) * mm, v(363.8, -191.47) * mm, v(363.63, -191.37) * mm, v(363.45, -191.37) * mm]});
            skLineSegment(sketch, "E364", {"start": v(379.31, -190.5) * mm, "end": v(379.31, -188.94) * mm});
            skFitSpline(sketch, "E365", {"points": [v(358.98, -191.37) * mm, v(358.8, -191.37) * mm, v(358.64, -191.47) * mm, v(358.55, -191.62) * mm]});
            skFitSpline(sketch, "E366", {"points": [v(357.86, -190.94) * mm, v(357.68, -191.04) * mm, v(357.58, -191.25) * mm, v(357.62, -191.46) * mm]});
            skFitSpline(sketch, "E367", {"points": [v(357.62, -191.46) * mm, v(357.66, -191.66) * mm, v(357.82, -191.83) * mm, v(358.03, -191.86) * mm]});
            skFitSpline(sketch, "E368", {"points": [v(358.03, -191.86) * mm, v(358.23, -191.9) * mm, v(358.44, -191.8) * mm, v(358.55, -191.62) * mm]});
            skFitSpline(sketch, "E369", {"points": [v(357.86, -190.94) * mm, v(358.02, -190.85) * mm, v(358.11, -190.68) * mm, v(358.11, -190.5) * mm]});
            skLineSegment(sketch, "E370", {"start": v(358.98, -188.07) * mm, "end": v(363.45, -188.07) * mm});
            skFitSpline(sketch, "E371", {"points": [v(344.39, -178.9) * mm, v(344.2, -178.9) * mm, v(344.04, -179) * mm, v(343.95, -179.15) * mm]});
            skFitSpline(sketch, "E372", {"points": [v(343.27, -178.47) * mm, v(343.09, -178.57) * mm, v(343, -178.78) * mm, v(343.03, -178.99) * mm]});
            skFitSpline(sketch, "E373", {"points": [v(343.03, -178.99) * mm, v(343.06, -179.2) * mm, v(343.23, -179.36) * mm, v(343.43, -179.4) * mm]});
            skFitSpline(sketch, "E374", {"points": [v(343.43, -179.4) * mm, v(343.64, -179.43) * mm, v(343.85, -179.33) * mm, v(343.95, -179.15) * mm]});
            skFitSpline(sketch, "E375", {"points": [v(343.27, -178.47) * mm, v(343.42, -178.38) * mm, v(343.52, -178.21) * mm, v(343.52, -178.03) * mm]});
            skLineSegment(sketch, "E376", {"start": v(364.31, -188.94) * mm, "end": v(364.31, -190.5) * mm});
            skFitSpline(sketch, "E377", {"points": [v(343.52, -173.57) * mm, v(343.52, -173.39) * mm, v(343.42, -173.22) * mm, v(343.27, -173.13) * mm]});
            skFitSpline(sketch, "E378", {"points": [v(343.95, -172.45) * mm, v(343.85, -172.27) * mm, v(343.64, -172.17) * mm, v(343.43, -172.2) * mm]});
            skFitSpline(sketch, "E379", {"points": [v(343.43, -172.2) * mm, v(343.23, -172.24) * mm, v(343.06, -172.4) * mm, v(343.03, -172.61) * mm]});
            skFitSpline(sketch, "E380", {"points": [v(343.03, -172.61) * mm, v(343, -172.82) * mm, v(343.09, -173.03) * mm, v(343.27, -173.13) * mm]});
            skFitSpline(sketch, "E381", {"points": [v(343.95, -172.45) * mm, v(344.04, -172.6) * mm, v(344.2, -172.7) * mm, v(344.39, -172.7) * mm]});
            skLineSegment(sketch, "E382", {"start": v(363.45, -191.37) * mm, "end": v(358.98, -191.37) * mm});
            skFitSpline(sketch, "E383", {"points": [v(345.95, -172.7) * mm, v(346.13, -172.7) * mm, v(346.3, -172.6) * mm, v(346.39, -172.45) * mm]});
            skFitSpline(sketch, "E384", {"points": [v(347.07, -173.13) * mm, v(347.25, -173.03) * mm, v(347.35, -172.82) * mm, v(347.31, -172.61) * mm]});
            skFitSpline(sketch, "E385", {"points": [v(347.31, -172.61) * mm, v(347.27, -172.4) * mm, v(347.11, -172.24) * mm, v(346.9, -172.2) * mm]});
            skFitSpline(sketch, "E386", {"points": [v(346.9, -172.2) * mm, v(346.7, -172.17) * mm, v(346.5, -172.27) * mm, v(346.39, -172.45) * mm]});
            skFitSpline(sketch, "E387", {"points": [v(347.07, -173.13) * mm, v(346.91, -173.22) * mm, v(346.82, -173.39) * mm, v(346.82, -173.57) * mm]});
            skLineSegment(sketch, "E388", {"start": v(358.11, -190.5) * mm, "end": v(358.11, -188.94) * mm});
            skFitSpline(sketch, "E389", {"points": [v(346.82, -178.03) * mm, v(346.82, -178.21) * mm, v(346.91, -178.38) * mm, v(347.07, -178.47) * mm]});
            skFitSpline(sketch, "E390", {"points": [v(346.39, -179.15) * mm, v(346.5, -179.33) * mm, v(346.7, -179.43) * mm, v(346.9, -179.4) * mm]});
            skFitSpline(sketch, "E391", {"points": [v(346.9, -179.4) * mm, v(347.11, -179.36) * mm, v(347.27, -179.2) * mm, v(347.31, -178.99) * mm]});
            skFitSpline(sketch, "E392", {"points": [v(347.31, -178.99) * mm, v(347.35, -178.78) * mm, v(347.25, -178.57) * mm, v(347.07, -178.47) * mm]});
            skFitSpline(sketch, "E393", {"points": [v(346.39, -179.15) * mm, v(346.3, -179) * mm, v(346.13, -178.9) * mm, v(345.95, -178.9) * mm]});
            skLineSegment(sketch, "E394", {"start": v(343.52, -178.03) * mm, "end": v(343.52, -173.57) * mm});
            skFitSpline(sketch, "E395", {"points": [v(344.39, -157.7) * mm, v(344.2, -157.7) * mm, v(344.04, -157.8) * mm, v(343.95, -157.95) * mm]});
            skFitSpline(sketch, "E396", {"points": [v(343.27, -157.27) * mm, v(343.09, -157.37) * mm, v(343, -157.58) * mm, v(343.03, -157.79) * mm]});
            skFitSpline(sketch, "E397", {"points": [v(343.03, -157.79) * mm, v(343.06, -158) * mm, v(343.23, -158.16) * mm, v(343.43, -158.2) * mm]});
            skFitSpline(sketch, "E398", {"points": [v(343.43, -158.2) * mm, v(343.64, -158.23) * mm, v(343.85, -158.13) * mm, v(343.95, -157.95) * mm]});
            skFitSpline(sketch, "E399", {"points": [v(343.27, -157.27) * mm, v(343.42, -157.18) * mm, v(343.52, -157.01) * mm, v(343.52, -156.83) * mm]});
            skLineSegment(sketch, "E400", {"start": v(344.39, -172.7) * mm, "end": v(345.95, -172.7) * mm});
            skFitSpline(sketch, "E401", {"points": [v(343.52, -152.37) * mm, v(343.52, -152.19) * mm, v(343.42, -152.02) * mm, v(343.27, -151.93) * mm]});
            skFitSpline(sketch, "E402", {"points": [v(343.95, -151.25) * mm, v(343.85, -151.07) * mm, v(343.64, -150.97) * mm, v(343.43, -151) * mm]});
            skFitSpline(sketch, "E403", {"points": [v(343.43, -151) * mm, v(343.23, -151.04) * mm, v(343.06, -151.2) * mm, v(343.03, -151.41) * mm]});
            skFitSpline(sketch, "E404", {"points": [v(343.03, -151.41) * mm, v(343, -151.62) * mm, v(343.09, -151.83) * mm, v(343.27, -151.93) * mm]});
            skFitSpline(sketch, "E405", {"points": [v(343.95, -151.25) * mm, v(344.04, -151.4) * mm, v(344.2, -151.5) * mm, v(344.39, -151.5) * mm]});
            skLineSegment(sketch, "E406", {"start": v(346.82, -173.57) * mm, "end": v(346.82, -178.03) * mm});
            skFitSpline(sketch, "E407", {"points": [v(345.95, -151.5) * mm, v(346.13, -151.5) * mm, v(346.3, -151.4) * mm, v(346.39, -151.25) * mm]});
            skFitSpline(sketch, "E408", {"points": [v(347.07, -151.93) * mm, v(347.25, -151.83) * mm, v(347.35, -151.62) * mm, v(347.31, -151.41) * mm]});
            skFitSpline(sketch, "E409", {"points": [v(347.31, -151.41) * mm, v(347.27, -151.2) * mm, v(347.11, -151.04) * mm, v(346.9, -151) * mm]});
            skFitSpline(sketch, "E410", {"points": [v(346.9, -151) * mm, v(346.7, -150.97) * mm, v(346.5, -151.07) * mm, v(346.39, -151.25) * mm]});
            skFitSpline(sketch, "E411", {"points": [v(347.07, -151.93) * mm, v(346.91, -152.02) * mm, v(346.82, -152.19) * mm, v(346.82, -152.37) * mm]});
            skLineSegment(sketch, "E412", {"start": v(345.95, -178.9) * mm, "end": v(344.39, -178.9) * mm});
            skFitSpline(sketch, "E413", {"points": [v(346.82, -156.83) * mm, v(346.82, -157.01) * mm, v(346.91, -157.18) * mm, v(347.07, -157.27) * mm]});
            skFitSpline(sketch, "E414", {"points": [v(346.39, -157.95) * mm, v(346.5, -158.13) * mm, v(346.7, -158.23) * mm, v(346.9, -158.2) * mm]});
            skFitSpline(sketch, "E415", {"points": [v(346.9, -158.2) * mm, v(347.11, -158.16) * mm, v(347.27, -158) * mm, v(347.31, -157.79) * mm]});
            skFitSpline(sketch, "E416", {"points": [v(347.31, -157.79) * mm, v(347.35, -157.58) * mm, v(347.25, -157.37) * mm, v(347.07, -157.27) * mm]});
            skFitSpline(sketch, "E417", {"points": [v(346.39, -157.95) * mm, v(346.3, -157.8) * mm, v(346.13, -157.7) * mm, v(345.95, -157.7) * mm]});
            skLineSegment(sketch, "E418", {"start": v(343.52, -156.83) * mm, "end": v(343.52, -152.37) * mm});
            skFitSpline(sketch, "E419", {"points": [v(379.31, -139.9) * mm, v(379.31, -139.72) * mm, v(379.22, -139.55) * mm, v(379.06, -139.46) * mm]});
            skFitSpline(sketch, "E420", {"points": [v(379.75, -138.78) * mm, v(379.64, -138.6) * mm, v(379.43, -138.5) * mm, v(379.23, -138.54) * mm]});
            skFitSpline(sketch, "E421", {"points": [v(379.23, -138.54) * mm, v(379.02, -138.57) * mm, v(378.86, -138.74) * mm, v(378.82, -138.94) * mm]});
            skFitSpline(sketch, "E422", {"points": [v(378.82, -138.94) * mm, v(378.78, -139.15) * mm, v(378.88, -139.36) * mm, v(379.06, -139.46) * mm]});
            skFitSpline(sketch, "E423", {"points": [v(379.75, -138.78) * mm, v(379.84, -138.94) * mm, v(380, -139.03) * mm, v(380.18, -139.03) * mm]});
            skLineSegment(sketch, "E424", {"start": v(344.39, -151.5) * mm, "end": v(345.95, -151.5) * mm});
            skFitSpline(sketch, "E425", {"points": [v(384.65, -139.03) * mm, v(384.83, -139.03) * mm, v(385, -138.94) * mm, v(385.08, -138.78) * mm]});
            skFitSpline(sketch, "E426", {"points": [v(385.76, -139.46) * mm, v(385.95, -139.36) * mm, v(386.04, -139.15) * mm, v(386, -138.94) * mm]});
            skFitSpline(sketch, "E427", {"points": [v(386, -138.94) * mm, v(385.97, -138.74) * mm, v(385.8, -138.57) * mm, v(385.6, -138.54) * mm]});
            skFitSpline(sketch, "E428", {"points": [v(385.6, -138.54) * mm, v(385.4, -138.5) * mm, v(385.19, -138.6) * mm, v(385.08, -138.78) * mm]});
            skFitSpline(sketch, "E429", {"points": [v(385.76, -139.46) * mm, v(385.6, -139.55) * mm, v(385.51, -139.72) * mm, v(385.51, -139.9) * mm]});
            skLineSegment(sketch, "E430", {"start": v(346.82, -152.37) * mm, "end": v(346.82, -156.83) * mm});
            skFitSpline(sketch, "E431", {"points": [v(385.51, -141.46) * mm, v(385.51, -141.64) * mm, v(385.6, -141.8) * mm, v(385.76, -141.9) * mm]});
            skFitSpline(sketch, "E432", {"points": [v(385.08, -142.58) * mm, v(385.19, -142.76) * mm, v(385.4, -142.86) * mm, v(385.6, -142.82) * mm]});
            skFitSpline(sketch, "E433", {"points": [v(385.6, -142.82) * mm, v(385.8, -142.79) * mm, v(385.97, -142.62) * mm, v(386, -142.42) * mm]});
            skFitSpline(sketch, "E434", {"points": [v(386, -142.42) * mm, v(386.04, -142.21) * mm, v(385.95, -142) * mm, v(385.76, -141.9) * mm]});
            skFitSpline(sketch, "E435", {"points": [v(385.08, -142.58) * mm, v(385, -142.43) * mm, v(384.83, -142.33) * mm, v(384.65, -142.33) * mm]});
            skLineSegment(sketch, "E436", {"start": v(345.95, -157.7) * mm, "end": v(344.39, -157.7) * mm});
            skFitSpline(sketch, "E437", {"points": [v(380.18, -142.33) * mm, v(380, -142.33) * mm, v(379.84, -142.43) * mm, v(379.75, -142.58) * mm]});
            skFitSpline(sketch, "E438", {"points": [v(379.06, -141.9) * mm, v(378.88, -142) * mm, v(378.78, -142.21) * mm, v(378.82, -142.42) * mm]});
            skFitSpline(sketch, "E439", {"points": [v(378.82, -142.42) * mm, v(378.86, -142.62) * mm, v(379.02, -142.79) * mm, v(379.23, -142.82) * mm]});
            skFitSpline(sketch, "E440", {"points": [v(379.23, -142.82) * mm, v(379.43, -142.86) * mm, v(379.64, -142.76) * mm, v(379.75, -142.58) * mm]});
            skFitSpline(sketch, "E441", {"points": [v(379.06, -141.9) * mm, v(379.22, -141.8) * mm, v(379.31, -141.64) * mm, v(379.31, -141.46) * mm]});
            skLineSegment(sketch, "E442", {"start": v(380.18, -139.03) * mm, "end": v(384.65, -139.03) * mm});
            skFitSpline(sketch, "E443", {"points": [v(358.11, -139.9) * mm, v(358.11, -139.72) * mm, v(358.02, -139.55) * mm, v(357.86, -139.46) * mm]});
            skFitSpline(sketch, "E444", {"points": [v(358.55, -138.78) * mm, v(358.44, -138.6) * mm, v(358.23, -138.5) * mm, v(358.03, -138.54) * mm]});
            skFitSpline(sketch, "E445", {"points": [v(358.03, -138.54) * mm, v(357.82, -138.57) * mm, v(357.66, -138.74) * mm, v(357.62, -138.94) * mm]});
            skFitSpline(sketch, "E446", {"points": [v(357.62, -138.94) * mm, v(357.58, -139.15) * mm, v(357.68, -139.36) * mm, v(357.86, -139.46) * mm]});
            skFitSpline(sketch, "E447", {"points": [v(358.55, -138.78) * mm, v(358.64, -138.94) * mm, v(358.8, -139.03) * mm, v(358.98, -139.03) * mm]});
            skLineSegment(sketch, "E448", {"start": v(385.51, -139.9) * mm, "end": v(385.51, -141.46) * mm});
            skFitSpline(sketch, "E449", {"points": [v(363.45, -139.03) * mm, v(363.63, -139.03) * mm, v(363.8, -138.94) * mm, v(363.88, -138.78) * mm]});
            skFitSpline(sketch, "E450", {"points": [v(364.56, -139.46) * mm, v(364.75, -139.36) * mm, v(364.84, -139.15) * mm, v(364.8, -138.94) * mm]});
            skFitSpline(sketch, "E451", {"points": [v(364.8, -138.94) * mm, v(364.77, -138.74) * mm, v(364.6, -138.57) * mm, v(364.4, -138.54) * mm]});
            skFitSpline(sketch, "E452", {"points": [v(364.4, -138.54) * mm, v(364.2, -138.5) * mm, v(363.99, -138.6) * mm, v(363.88, -138.78) * mm]});
            skFitSpline(sketch, "E453", {"points": [v(364.56, -139.46) * mm, v(364.4, -139.55) * mm, v(364.31, -139.72) * mm, v(364.31, -139.9) * mm]});
            skLineSegment(sketch, "E454", {"start": v(384.65, -142.33) * mm, "end": v(380.18, -142.33) * mm});
            skFitSpline(sketch, "E455", {"points": [v(364.31, -141.46) * mm, v(364.31, -141.64) * mm, v(364.4, -141.8) * mm, v(364.56, -141.9) * mm]});
            skFitSpline(sketch, "E456", {"points": [v(363.88, -142.58) * mm, v(363.99, -142.76) * mm, v(364.2, -142.86) * mm, v(364.4, -142.82) * mm]});
            skFitSpline(sketch, "E457", {"points": [v(364.4, -142.82) * mm, v(364.6, -142.79) * mm, v(364.77, -142.62) * mm, v(364.8, -142.42) * mm]});
            skFitSpline(sketch, "E458", {"points": [v(364.8, -142.42) * mm, v(364.84, -142.21) * mm, v(364.75, -142) * mm, v(364.56, -141.9) * mm]});
            skFitSpline(sketch, "E459", {"points": [v(363.88, -142.58) * mm, v(363.8, -142.43) * mm, v(363.63, -142.33) * mm, v(363.45, -142.33) * mm]});
            skLineSegment(sketch, "E460", {"start": v(379.31, -141.46) * mm, "end": v(379.31, -139.9) * mm});
            skFitSpline(sketch, "E461", {"points": [v(358.98, -142.33) * mm, v(358.8, -142.33) * mm, v(358.64, -142.43) * mm, v(358.55, -142.58) * mm]});
            skFitSpline(sketch, "E462", {"points": [v(357.86, -141.9) * mm, v(357.68, -142) * mm, v(357.58, -142.21) * mm, v(357.62, -142.42) * mm]});
            skFitSpline(sketch, "E463", {"points": [v(357.62, -142.42) * mm, v(357.66, -142.62) * mm, v(357.82, -142.79) * mm, v(358.03, -142.82) * mm]});
            skFitSpline(sketch, "E464", {"points": [v(358.03, -142.82) * mm, v(358.23, -142.86) * mm, v(358.44, -142.76) * mm, v(358.55, -142.58) * mm]});
            skFitSpline(sketch, "E465", {"points": [v(357.86, -141.9) * mm, v(358.02, -141.8) * mm, v(358.11, -141.64) * mm, v(358.11, -141.46) * mm]});
            skLineSegment(sketch, "E466", {"start": v(358.98, -139.03) * mm, "end": v(363.45, -139.03) * mm});
            skFitSpline(sketch, "E467", {"points": [v(339.06, -121.3) * mm, v(339.22, -121.2) * mm, v(339.31, -121.04) * mm, v(339.31, -120.86) * mm]});
            skFitSpline(sketch, "E468", {"points": [v(339.06, -121.3) * mm, v(338.88, -121.4) * mm, v(338.79, -121.6) * mm, v(338.82, -121.81) * mm]});
            skFitSpline(sketch, "E469", {"points": [v(338.82, -121.81) * mm, v(338.86, -122.02) * mm, v(339.02, -122.18) * mm, v(339.23, -122.22) * mm]});
            skFitSpline(sketch, "E470", {"points": [v(339.23, -122.22) * mm, v(339.43, -122.25) * mm, v(339.64, -122.16) * mm, v(339.75, -121.98) * mm]});
            skFitSpline(sketch, "E471", {"points": [v(340.18, -121.73) * mm, v(340, -121.73) * mm, v(339.84, -121.82) * mm, v(339.75, -121.98) * mm]});
            skLineSegment(sketch, "E472", {"start": v(364.31, -139.9) * mm, "end": v(364.31, -141.46) * mm});
            skFitSpline(sketch, "E473", {"points": [v(345.08, -121.98) * mm, v(345, -121.82) * mm, v(344.83, -121.73) * mm, v(344.65, -121.73) * mm]});
            skFitSpline(sketch, "E474", {"points": [v(345.08, -121.98) * mm, v(345.19, -122.16) * mm, v(345.4, -122.25) * mm, v(345.6, -122.22) * mm]});
            skFitSpline(sketch, "E475", {"points": [v(345.6, -122.22) * mm, v(345.8, -122.18) * mm, v(345.97, -122.02) * mm, v(346, -121.81) * mm]});
            skFitSpline(sketch, "E476", {"points": [v(346, -121.81) * mm, v(346.04, -121.6) * mm, v(345.95, -121.4) * mm, v(345.76, -121.3) * mm]});
            skFitSpline(sketch, "E477", {"points": [v(345.51, -120.86) * mm, v(345.51, -121.04) * mm, v(345.6, -121.2) * mm, v(345.76, -121.3) * mm]});
            skLineSegment(sketch, "E478", {"start": v(363.45, -142.33) * mm, "end": v(358.98, -142.33) * mm});
            skFitSpline(sketch, "E479", {"points": [v(345.76, -118.86) * mm, v(345.6, -118.95) * mm, v(345.51, -119.11) * mm, v(345.51, -119.3) * mm]});
            skFitSpline(sketch, "E480", {"points": [v(345.76, -118.86) * mm, v(345.95, -118.75) * mm, v(346.04, -118.55) * mm, v(346, -118.34) * mm]});
            skFitSpline(sketch, "E481", {"points": [v(346, -118.34) * mm, v(345.97, -118.13) * mm, v(345.8, -117.97) * mm, v(345.6, -117.93) * mm]});
            skFitSpline(sketch, "E482", {"points": [v(345.6, -117.93) * mm, v(345.4, -117.9) * mm, v(345.19, -118) * mm, v(345.08, -118.18) * mm]});
            skFitSpline(sketch, "E483", {"points": [v(344.65, -118.43) * mm, v(344.83, -118.43) * mm, v(345, -118.33) * mm, v(345.08, -118.18) * mm]});
            skLineSegment(sketch, "E484", {"start": v(358.11, -141.46) * mm, "end": v(358.11, -139.9) * mm});
            skFitSpline(sketch, "E485", {"points": [v(339.75, -118.18) * mm, v(339.84, -118.33) * mm, v(340, -118.43) * mm, v(340.18, -118.43) * mm]});
            skFitSpline(sketch, "E486", {"points": [v(339.75, -118.18) * mm, v(339.64, -118) * mm, v(339.43, -117.9) * mm, v(339.23, -117.93) * mm]});
            skFitSpline(sketch, "E487", {"points": [v(339.23, -117.93) * mm, v(339.02, -117.97) * mm, v(338.86, -118.13) * mm, v(338.82, -118.34) * mm]});
            skFitSpline(sketch, "E488", {"points": [v(338.82, -118.34) * mm, v(338.79, -118.55) * mm, v(338.88, -118.75) * mm, v(339.06, -118.86) * mm]});
            skFitSpline(sketch, "E489", {"points": [v(339.31, -119.3) * mm, v(339.31, -119.11) * mm, v(339.22, -118.95) * mm, v(339.06, -118.86) * mm]});
            skLineSegment(sketch, "E490", {"start": v(340.18, -121.73) * mm, "end": v(344.65, -121.73) * mm});
            skFitSpline(sketch, "E491", {"points": [v(317.86, -121.3) * mm, v(318.02, -121.2) * mm, v(318.11, -121.04) * mm, v(318.11, -120.86) * mm]});
            skFitSpline(sketch, "E492", {"points": [v(317.86, -121.3) * mm, v(317.68, -121.4) * mm, v(317.59, -121.6) * mm, v(317.62, -121.81) * mm]});
            skFitSpline(sketch, "E493", {"points": [v(317.62, -121.81) * mm, v(317.66, -122.02) * mm, v(317.82, -122.18) * mm, v(318.03, -122.22) * mm]});
            skFitSpline(sketch, "E494", {"points": [v(318.03, -122.22) * mm, v(318.23, -122.25) * mm, v(318.44, -122.16) * mm, v(318.55, -121.98) * mm]});
            skFitSpline(sketch, "E495", {"points": [v(318.98, -121.73) * mm, v(318.8, -121.73) * mm, v(318.64, -121.82) * mm, v(318.55, -121.98) * mm]});
            skLineSegment(sketch, "E496", {"start": v(345.51, -120.86) * mm, "end": v(345.51, -119.3) * mm});
            skFitSpline(sketch, "E497", {"points": [v(323.88, -121.98) * mm, v(323.8, -121.82) * mm, v(323.63, -121.73) * mm, v(323.45, -121.73) * mm]});
            skFitSpline(sketch, "E498", {"points": [v(323.88, -121.98) * mm, v(323.99, -122.16) * mm, v(324.2, -122.25) * mm, v(324.4, -122.22) * mm]});
            skFitSpline(sketch, "E499", {"points": [v(324.4, -122.22) * mm, v(324.6, -122.18) * mm, v(324.77, -122.02) * mm, v(324.8, -121.81) * mm]});
            skFitSpline(sketch, "E500", {"points": [v(324.8, -121.81) * mm, v(324.84, -121.6) * mm, v(324.75, -121.4) * mm, v(324.56, -121.3) * mm]});
            skFitSpline(sketch, "E501", {"points": [v(324.31, -120.86) * mm, v(324.31, -121.04) * mm, v(324.4, -121.2) * mm, v(324.56, -121.3) * mm]});
            skLineSegment(sketch, "E502", {"start": v(344.65, -118.43) * mm, "end": v(340.18, -118.43) * mm});
            skFitSpline(sketch, "E503", {"points": [v(324.56, -118.86) * mm, v(324.4, -118.95) * mm, v(324.31, -119.11) * mm, v(324.31, -119.3) * mm]});
            skFitSpline(sketch, "E504", {"points": [v(324.56, -118.86) * mm, v(324.75, -118.75) * mm, v(324.84, -118.55) * mm, v(324.8, -118.34) * mm]});
            skFitSpline(sketch, "E505", {"points": [v(324.8, -118.34) * mm, v(324.77, -118.13) * mm, v(324.6, -117.97) * mm, v(324.4, -117.93) * mm]});
            skFitSpline(sketch, "E506", {"points": [v(324.4, -117.93) * mm, v(324.2, -117.9) * mm, v(323.99, -118) * mm, v(323.88, -118.18) * mm]});
            skFitSpline(sketch, "E507", {"points": [v(323.45, -118.43) * mm, v(323.63, -118.43) * mm, v(323.8, -118.33) * mm, v(323.88, -118.18) * mm]});
            skLineSegment(sketch, "E508", {"start": v(339.31, -119.3) * mm, "end": v(339.31, -120.86) * mm});
            skFitSpline(sketch, "E509", {"points": [v(318.55, -118.18) * mm, v(318.64, -118.33) * mm, v(318.8, -118.43) * mm, v(318.98, -118.43) * mm]});
            skFitSpline(sketch, "E510", {"points": [v(318.55, -118.18) * mm, v(318.44, -118) * mm, v(318.23, -117.9) * mm, v(318.03, -117.93) * mm]});
            skFitSpline(sketch, "E511", {"points": [v(318.03, -117.93) * mm, v(317.82, -117.97) * mm, v(317.66, -118.13) * mm, v(317.62, -118.34) * mm]});
            skFitSpline(sketch, "E512", {"points": [v(317.62, -118.34) * mm, v(317.59, -118.55) * mm, v(317.68, -118.75) * mm, v(317.86, -118.86) * mm]});
            skFitSpline(sketch, "E513", {"points": [v(318.11, -119.3) * mm, v(318.11, -119.11) * mm, v(318.02, -118.95) * mm, v(317.86, -118.86) * mm]});
            skLineSegment(sketch, "E514", {"start": v(318.98, -121.73) * mm, "end": v(323.45, -121.73) * mm});
            skFitSpline(sketch, "E515", {"points": [v(219.32, -119.3) * mm, v(219.32, -119.11) * mm, v(219.22, -118.95) * mm, v(219.07, -118.86) * mm]});
            skFitSpline(sketch, "E516", {"points": [v(219.75, -118.18) * mm, v(219.64, -118) * mm, v(219.44, -117.9) * mm, v(219.23, -117.93) * mm]});
            skFitSpline(sketch, "E517", {"points": [v(219.23, -117.93) * mm, v(219.02, -117.97) * mm, v(218.86, -118.13) * mm, v(218.82, -118.34) * mm]});
            skFitSpline(sketch, "E518", {"points": [v(218.82, -118.34) * mm, v(218.79, -118.55) * mm, v(218.88, -118.75) * mm, v(219.07, -118.86) * mm]});
            skFitSpline(sketch, "E519", {"points": [v(219.75, -118.18) * mm, v(219.84, -118.33) * mm, v(220, -118.43) * mm, v(220.18, -118.43) * mm]});
            skLineSegment(sketch, "E520", {"start": v(324.31, -120.86) * mm, "end": v(324.31, -119.3) * mm});
            skFitSpline(sketch, "E521", {"points": [v(224.65, -118.43) * mm, v(224.83, -118.43) * mm, v(225, -118.33) * mm, v(225.08, -118.18) * mm]});
            skFitSpline(sketch, "E522", {"points": [v(225.77, -118.86) * mm, v(225.95, -118.75) * mm, v(226.04, -118.55) * mm, v(226, -118.34) * mm]});
            skFitSpline(sketch, "E523", {"points": [v(226, -118.34) * mm, v(225.97, -118.13) * mm, v(225.8, -117.97) * mm, v(225.6, -117.93) * mm]});
            skFitSpline(sketch, "E524", {"points": [v(225.6, -117.93) * mm, v(225.4, -117.9) * mm, v(225.19, -118) * mm, v(225.08, -118.18) * mm]});
            skFitSpline(sketch, "E525", {"points": [v(225.77, -118.86) * mm, v(225.61, -118.95) * mm, v(225.52, -119.11) * mm, v(225.52, -119.3) * mm]});
            skLineSegment(sketch, "E526", {"start": v(323.45, -118.43) * mm, "end": v(318.98, -118.43) * mm});
            skFitSpline(sketch, "E527", {"points": [v(225.52, -120.86) * mm, v(225.52, -121.04) * mm, v(225.61, -121.2) * mm, v(225.77, -121.3) * mm]});
            skFitSpline(sketch, "E528", {"points": [v(225.08, -121.98) * mm, v(225.19, -122.16) * mm, v(225.4, -122.25) * mm, v(225.6, -122.22) * mm]});
            skFitSpline(sketch, "E529", {"points": [v(225.6, -122.22) * mm, v(225.8, -122.18) * mm, v(225.97, -122.02) * mm, v(226, -121.81) * mm]});
            skFitSpline(sketch, "E530", {"points": [v(226, -121.81) * mm, v(226.04, -121.6) * mm, v(225.95, -121.4) * mm, v(225.77, -121.3) * mm]});
            skFitSpline(sketch, "E531", {"points": [v(225.08, -121.98) * mm, v(225, -121.82) * mm, v(224.83, -121.73) * mm, v(224.65, -121.73) * mm]});
            skLineSegment(sketch, "E532", {"start": v(318.11, -119.3) * mm, "end": v(318.11, -120.86) * mm});
            skFitSpline(sketch, "E533", {"points": [v(220.18, -121.73) * mm, v(220, -121.73) * mm, v(219.84, -121.82) * mm, v(219.75, -121.98) * mm]});
            skFitSpline(sketch, "E534", {"points": [v(219.07, -121.3) * mm, v(218.88, -121.4) * mm, v(218.79, -121.6) * mm, v(218.82, -121.81) * mm]});
            skFitSpline(sketch, "E535", {"points": [v(218.82, -121.81) * mm, v(218.86, -122.02) * mm, v(219.02, -122.18) * mm, v(219.23, -122.22) * mm]});
            skFitSpline(sketch, "E536", {"points": [v(219.23, -122.22) * mm, v(219.44, -122.25) * mm, v(219.64, -122.16) * mm, v(219.75, -121.98) * mm]});
            skFitSpline(sketch, "E537", {"points": [v(219.07, -121.3) * mm, v(219.22, -121.2) * mm, v(219.32, -121.04) * mm, v(219.32, -120.86) * mm]});
            skLineSegment(sketch, "E538", {"start": v(220.18, -118.43) * mm, "end": v(224.65, -118.43) * mm});
            skFitSpline(sketch, "E539", {"points": [v(198.12, -119.3) * mm, v(198.12, -119.11) * mm, v(198.02, -118.95) * mm, v(197.87, -118.86) * mm]});
            skFitSpline(sketch, "E540", {"points": [v(198.55, -118.18) * mm, v(198.44, -118) * mm, v(198.24, -117.9) * mm, v(198.03, -117.93) * mm]});
            skFitSpline(sketch, "E541", {"points": [v(198.03, -117.93) * mm, v(197.82, -117.97) * mm, v(197.66, -118.13) * mm, v(197.62, -118.34) * mm]});
            skFitSpline(sketch, "E542", {"points": [v(197.62, -118.34) * mm, v(197.59, -118.55) * mm, v(197.68, -118.75) * mm, v(197.87, -118.86) * mm]});
            skFitSpline(sketch, "E543", {"points": [v(198.55, -118.18) * mm, v(198.64, -118.33) * mm, v(198.8, -118.43) * mm, v(198.98, -118.43) * mm]});
            skLineSegment(sketch, "E544", {"start": v(225.52, -119.3) * mm, "end": v(225.52, -120.86) * mm});
            skFitSpline(sketch, "E545", {"points": [v(203.45, -118.43) * mm, v(203.63, -118.43) * mm, v(203.8, -118.33) * mm, v(203.88, -118.18) * mm]});
            skFitSpline(sketch, "E546", {"points": [v(204.57, -118.86) * mm, v(204.75, -118.75) * mm, v(204.84, -118.55) * mm, v(204.8, -118.34) * mm]});
            skFitSpline(sketch, "E547", {"points": [v(204.8, -118.34) * mm, v(204.77, -118.13) * mm, v(204.6, -117.97) * mm, v(204.4, -117.93) * mm]});
            skFitSpline(sketch, "E548", {"points": [v(204.4, -117.93) * mm, v(204.2, -117.9) * mm, v(203.99, -118) * mm, v(203.88, -118.18) * mm]});
            skFitSpline(sketch, "E549", {"points": [v(204.57, -118.86) * mm, v(204.41, -118.95) * mm, v(204.32, -119.11) * mm, v(204.32, -119.3) * mm]});
            skLineSegment(sketch, "E550", {"start": v(224.65, -121.73) * mm, "end": v(220.18, -121.73) * mm});
            skFitSpline(sketch, "E551", {"points": [v(204.32, -120.86) * mm, v(204.32, -121.04) * mm, v(204.41, -121.2) * mm, v(204.57, -121.3) * mm]});
            skFitSpline(sketch, "E552", {"points": [v(203.88, -121.98) * mm, v(203.99, -122.16) * mm, v(204.2, -122.25) * mm, v(204.4, -122.22) * mm]});
            skFitSpline(sketch, "E553", {"points": [v(204.4, -122.22) * mm, v(204.6, -122.18) * mm, v(204.77, -122.02) * mm, v(204.8, -121.81) * mm]});
            skFitSpline(sketch, "E554", {"points": [v(204.8, -121.81) * mm, v(204.84, -121.6) * mm, v(204.75, -121.4) * mm, v(204.57, -121.3) * mm]});
            skFitSpline(sketch, "E555", {"points": [v(203.88, -121.98) * mm, v(203.8, -121.82) * mm, v(203.63, -121.73) * mm, v(203.45, -121.73) * mm]});
            skLineSegment(sketch, "E556", {"start": v(219.32, -120.86) * mm, "end": v(219.32, -119.3) * mm});
            skFitSpline(sketch, "E557", {"points": [v(198.98, -121.73) * mm, v(198.8, -121.73) * mm, v(198.64, -121.82) * mm, v(198.55, -121.98) * mm]});
            skFitSpline(sketch, "E558", {"points": [v(197.87, -121.3) * mm, v(197.68, -121.4) * mm, v(197.59, -121.6) * mm, v(197.62, -121.81) * mm]});
            skFitSpline(sketch, "E559", {"points": [v(197.62, -121.81) * mm, v(197.66, -122.02) * mm, v(197.82, -122.18) * mm, v(198.03, -122.22) * mm]});
            skFitSpline(sketch, "E560", {"points": [v(198.03, -122.22) * mm, v(198.24, -122.25) * mm, v(198.44, -122.16) * mm, v(198.55, -121.98) * mm]});
            skFitSpline(sketch, "E561", {"points": [v(197.87, -121.3) * mm, v(198.02, -121.2) * mm, v(198.12, -121.04) * mm, v(198.12, -120.86) * mm]});
            skLineSegment(sketch, "E562", {"start": v(198.98, -118.43) * mm, "end": v(203.45, -118.43) * mm});
            skFitSpline(sketch, "E563", {"points": [v(59.32, -119.3) * mm, v(59.32, -119.11) * mm, v(59.22, -118.95) * mm, v(59.07, -118.86) * mm]});
            skFitSpline(sketch, "E564", {"points": [v(59.75, -118.18) * mm, v(59.64, -118) * mm, v(59.44, -117.9) * mm, v(59.23, -117.93) * mm]});
            skFitSpline(sketch, "E565", {"points": [v(59.23, -117.93) * mm, v(59.02, -117.97) * mm, v(58.86, -118.13) * mm, v(58.82, -118.34) * mm]});
            skFitSpline(sketch, "E566", {"points": [v(58.82, -118.34) * mm, v(58.79, -118.55) * mm, v(58.88, -118.75) * mm, v(59.07, -118.86) * mm]});
            skFitSpline(sketch, "E567", {"points": [v(59.75, -118.18) * mm, v(59.84, -118.33) * mm, v(60, -118.43) * mm, v(60.18, -118.43) * mm]});
            skLineSegment(sketch, "E568", {"start": v(204.32, -119.3) * mm, "end": v(204.32, -120.86) * mm});
            skFitSpline(sketch, "E569", {"points": [v(64.65, -118.43) * mm, v(64.83, -118.43) * mm, v(65, -118.33) * mm, v(65.08, -118.18) * mm]});
            skFitSpline(sketch, "E570", {"points": [v(65.77, -118.86) * mm, v(65.95, -118.75) * mm, v(66.05, -118.55) * mm, v(66, -118.34) * mm]});
            skFitSpline(sketch, "E571", {"points": [v(66, -118.34) * mm, v(65.97, -118.13) * mm, v(65.81, -117.97) * mm, v(65.6, -117.93) * mm]});
            skFitSpline(sketch, "E572", {"points": [v(65.6, -117.93) * mm, v(65.4, -117.9) * mm, v(65.19, -118) * mm, v(65.08, -118.18) * mm]});
            skFitSpline(sketch, "E573", {"points": [v(65.77, -118.86) * mm, v(65.61, -118.95) * mm, v(65.52, -119.11) * mm, v(65.52, -119.3) * mm]});
            skLineSegment(sketch, "E574", {"start": v(203.45, -121.73) * mm, "end": v(198.98, -121.73) * mm});
            skFitSpline(sketch, "E575", {"points": [v(65.52, -120.86) * mm, v(65.52, -121.04) * mm, v(65.61, -121.2) * mm, v(65.77, -121.3) * mm]});
            skFitSpline(sketch, "E576", {"points": [v(65.08, -121.98) * mm, v(65.19, -122.16) * mm, v(65.4, -122.25) * mm, v(65.6, -122.22) * mm]});
            skFitSpline(sketch, "E577", {"points": [v(65.6, -122.22) * mm, v(65.81, -122.18) * mm, v(65.97, -122.02) * mm, v(66, -121.81) * mm]});
            skFitSpline(sketch, "E578", {"points": [v(66, -121.81) * mm, v(66.05, -121.6) * mm, v(65.95, -121.4) * mm, v(65.77, -121.3) * mm]});
            skFitSpline(sketch, "E579", {"points": [v(65.08, -121.98) * mm, v(65, -121.82) * mm, v(64.83, -121.73) * mm, v(64.65, -121.73) * mm]});
            skLineSegment(sketch, "E580", {"start": v(198.12, -120.86) * mm, "end": v(198.12, -119.3) * mm});
            skFitSpline(sketch, "E581", {"points": [v(60.18, -121.73) * mm, v(60, -121.73) * mm, v(59.84, -121.82) * mm, v(59.75, -121.98) * mm]});
            skFitSpline(sketch, "E582", {"points": [v(59.07, -121.3) * mm, v(58.88, -121.4) * mm, v(58.79, -121.6) * mm, v(58.82, -121.81) * mm]});
            skFitSpline(sketch, "E583", {"points": [v(58.82, -121.81) * mm, v(58.86, -122.02) * mm, v(59.02, -122.18) * mm, v(59.23, -122.22) * mm]});
            skFitSpline(sketch, "E584", {"points": [v(59.23, -122.22) * mm, v(59.44, -122.25) * mm, v(59.64, -122.16) * mm, v(59.75, -121.98) * mm]});
            skFitSpline(sketch, "E585", {"points": [v(59.07, -121.3) * mm, v(59.22, -121.2) * mm, v(59.32, -121.04) * mm, v(59.32, -120.86) * mm]});
            skLineSegment(sketch, "E586", {"start": v(60.18, -118.43) * mm, "end": v(64.65, -118.43) * mm});
            skFitSpline(sketch, "E587", {"points": [v(38.12, -119.3) * mm, v(38.12, -119.11) * mm, v(38.02, -118.95) * mm, v(37.87, -118.86) * mm]});
            skFitSpline(sketch, "E588", {"points": [v(38.55, -118.18) * mm, v(38.44, -118) * mm, v(38.24, -117.9) * mm, v(38.03, -117.93) * mm]});
            skFitSpline(sketch, "E589", {"points": [v(38.03, -117.93) * mm, v(37.82, -117.97) * mm, v(37.66, -118.13) * mm, v(37.62, -118.34) * mm]});
            skFitSpline(sketch, "E590", {"points": [v(37.62, -118.34) * mm, v(37.59, -118.55) * mm, v(37.68, -118.75) * mm, v(37.87, -118.86) * mm]});
            skFitSpline(sketch, "E591", {"points": [v(38.55, -118.18) * mm, v(38.64, -118.33) * mm, v(38.8, -118.43) * mm, v(38.98, -118.43) * mm]});
            skLineSegment(sketch, "E592", {"start": v(65.52, -119.3) * mm, "end": v(65.52, -120.86) * mm});
            skFitSpline(sketch, "E593", {"points": [v(43.45, -118.43) * mm, v(43.63, -118.43) * mm, v(43.8, -118.33) * mm, v(43.88, -118.18) * mm]});
            skFitSpline(sketch, "E594", {"points": [v(44.57, -118.86) * mm, v(44.75, -118.75) * mm, v(44.85, -118.55) * mm, v(44.8, -118.34) * mm]});
            skFitSpline(sketch, "E595", {"points": [v(44.8, -118.34) * mm, v(44.77, -118.13) * mm, v(44.61, -117.97) * mm, v(44.4, -117.93) * mm]});
            skFitSpline(sketch, "E596", {"points": [v(44.4, -117.93) * mm, v(44.2, -117.9) * mm, v(43.99, -118) * mm, v(43.88, -118.18) * mm]});
            skFitSpline(sketch, "E597", {"points": [v(44.57, -118.86) * mm, v(44.41, -118.95) * mm, v(44.32, -119.11) * mm, v(44.32, -119.3) * mm]});
            skLineSegment(sketch, "E598", {"start": v(64.65, -121.73) * mm, "end": v(60.18, -121.73) * mm});
            skFitSpline(sketch, "E599", {"points": [v(44.32, -120.86) * mm, v(44.32, -121.04) * mm, v(44.41, -121.2) * mm, v(44.57, -121.3) * mm]});
            skFitSpline(sketch, "E600", {"points": [v(43.88, -121.98) * mm, v(43.99, -122.16) * mm, v(44.2, -122.25) * mm, v(44.4, -122.22) * mm]});
            skFitSpline(sketch, "E601", {"points": [v(44.4, -122.22) * mm, v(44.61, -122.18) * mm, v(44.77, -122.02) * mm, v(44.8, -121.81) * mm]});
            skFitSpline(sketch, "E602", {"points": [v(44.8, -121.81) * mm, v(44.85, -121.6) * mm, v(44.75, -121.4) * mm, v(44.57, -121.3) * mm]});
            skFitSpline(sketch, "E603", {"points": [v(43.88, -121.98) * mm, v(43.8, -121.82) * mm, v(43.63, -121.73) * mm, v(43.45, -121.73) * mm]});
            skLineSegment(sketch, "E604", {"start": v(59.32, -120.86) * mm, "end": v(59.32, -119.3) * mm});
            skFitSpline(sketch, "E605", {"points": [v(38.98, -121.73) * mm, v(38.8, -121.73) * mm, v(38.64, -121.82) * mm, v(38.55, -121.98) * mm]});
            skFitSpline(sketch, "E606", {"points": [v(37.87, -121.3) * mm, v(37.68, -121.4) * mm, v(37.59, -121.6) * mm, v(37.62, -121.81) * mm]});
            skFitSpline(sketch, "E607", {"points": [v(37.62, -121.81) * mm, v(37.66, -122.02) * mm, v(37.82, -122.18) * mm, v(38.03, -122.22) * mm]});
            skFitSpline(sketch, "E608", {"points": [v(38.03, -122.22) * mm, v(38.24, -122.25) * mm, v(38.44, -122.16) * mm, v(38.55, -121.98) * mm]});
            skFitSpline(sketch, "E609", {"points": [v(37.87, -121.3) * mm, v(38.02, -121.2) * mm, v(38.12, -121.04) * mm, v(38.12, -120.86) * mm]});
            skLineSegment(sketch, "E610", {"start": v(38.98, -118.43) * mm, "end": v(43.45, -118.43) * mm});
            skFitSpline(sketch, "E611", {"points": [v(339.06, 119.05) * mm, v(339.22, 119.14) * mm, v(339.31, 119.3) * mm, v(339.31, 119.49) * mm]});
            skFitSpline(sketch, "E612", {"points": [v(339.06, 119.05) * mm, v(338.88, 118.95) * mm, v(338.79, 118.74) * mm, v(338.82, 118.54) * mm]});
            skFitSpline(sketch, "E613", {"points": [v(338.82, 118.54) * mm, v(338.86, 118.33) * mm, v(339.02, 118.17) * mm, v(339.23, 118.13) * mm]});
            skFitSpline(sketch, "E614", {"points": [v(339.23, 118.13) * mm, v(339.43, 118.1) * mm, v(339.64, 118.19) * mm, v(339.75, 118.37) * mm]});
            skFitSpline(sketch, "E615", {"points": [v(340.18, 118.62) * mm, v(340, 118.62) * mm, v(339.84, 118.53) * mm, v(339.75, 118.37) * mm]});
            skLineSegment(sketch, "E616", {"start": v(44.32, -119.3) * mm, "end": v(44.32, -120.86) * mm});
            skFitSpline(sketch, "E617", {"points": [v(345.08, 118.37) * mm, v(345, 118.53) * mm, v(344.83, 118.62) * mm, v(344.65, 118.62) * mm]});
            skFitSpline(sketch, "E618", {"points": [v(345.08, 118.37) * mm, v(345.19, 118.19) * mm, v(345.4, 118.1) * mm, v(345.6, 118.13) * mm]});
            skFitSpline(sketch, "E619", {"points": [v(345.6, 118.13) * mm, v(345.8, 118.17) * mm, v(345.97, 118.33) * mm, v(346, 118.54) * mm]});
            skFitSpline(sketch, "E620", {"points": [v(346, 118.54) * mm, v(346.04, 118.74) * mm, v(345.95, 118.95) * mm, v(345.76, 119.05) * mm]});
            skFitSpline(sketch, "E621", {"points": [v(345.51, 119.49) * mm, v(345.51, 119.3) * mm, v(345.6, 119.14) * mm, v(345.76, 119.05) * mm]});
            skLineSegment(sketch, "E622", {"start": v(43.45, -121.73) * mm, "end": v(38.98, -121.73) * mm});
            skFitSpline(sketch, "E623", {"points": [v(345.76, 121.49) * mm, v(345.6, 121.4) * mm, v(345.51, 121.23) * mm, v(345.51, 121.06) * mm]});
            skFitSpline(sketch, "E624", {"points": [v(345.76, 121.49) * mm, v(345.95, 121.6) * mm, v(346.04, 121.8) * mm, v(346, 122) * mm]});
            skFitSpline(sketch, "E625", {"points": [v(346, 122) * mm, v(345.97, 122.22) * mm, v(345.8, 122.38) * mm, v(345.6, 122.41) * mm]});
            skFitSpline(sketch, "E626", {"points": [v(345.6, 122.41) * mm, v(345.4, 122.45) * mm, v(345.19, 122.35) * mm, v(345.08, 122.17) * mm]});
            skFitSpline(sketch, "E627", {"points": [v(344.65, 121.92) * mm, v(344.83, 121.92) * mm, v(345, 122.02) * mm, v(345.08, 122.17) * mm]});
            skLineSegment(sketch, "E628", {"start": v(38.12, -120.86) * mm, "end": v(38.12, -119.3) * mm});
            skFitSpline(sketch, "E629", {"points": [v(339.75, 122.17) * mm, v(339.84, 122.02) * mm, v(340, 121.92) * mm, v(340.18, 121.92) * mm]});
            skFitSpline(sketch, "E630", {"points": [v(339.75, 122.17) * mm, v(339.64, 122.35) * mm, v(339.43, 122.45) * mm, v(339.23, 122.41) * mm]});
            skFitSpline(sketch, "E631", {"points": [v(339.23, 122.41) * mm, v(339.02, 122.38) * mm, v(338.86, 122.22) * mm, v(338.82, 122) * mm]});
            skFitSpline(sketch, "E632", {"points": [v(338.82, 122) * mm, v(338.79, 121.8) * mm, v(338.88, 121.6) * mm, v(339.06, 121.49) * mm]});
            skFitSpline(sketch, "E633", {"points": [v(339.31, 121.06) * mm, v(339.31, 121.23) * mm, v(339.22, 121.4) * mm, v(339.06, 121.49) * mm]});
            skLineSegment(sketch, "E634", {"start": v(340.18, 118.62) * mm, "end": v(344.65, 118.62) * mm});
            skFitSpline(sketch, "E635", {"points": [v(317.86, 119.05) * mm, v(318.02, 119.14) * mm, v(318.11, 119.3) * mm, v(318.11, 119.49) * mm]});
            skFitSpline(sketch, "E636", {"points": [v(317.86, 119.05) * mm, v(317.68, 118.95) * mm, v(317.59, 118.74) * mm, v(317.62, 118.54) * mm]});
            skFitSpline(sketch, "E637", {"points": [v(317.62, 118.54) * mm, v(317.66, 118.33) * mm, v(317.82, 118.17) * mm, v(318.03, 118.13) * mm]});
            skFitSpline(sketch, "E638", {"points": [v(318.03, 118.13) * mm, v(318.23, 118.1) * mm, v(318.44, 118.19) * mm, v(318.55, 118.37) * mm]});
            skFitSpline(sketch, "E639", {"points": [v(318.98, 118.62) * mm, v(318.8, 118.62) * mm, v(318.64, 118.53) * mm, v(318.55, 118.37) * mm]});
            skLineSegment(sketch, "E640", {"start": v(345.51, 119.49) * mm, "end": v(345.51, 121.06) * mm});
            skFitSpline(sketch, "E641", {"points": [v(323.88, 118.37) * mm, v(323.8, 118.53) * mm, v(323.63, 118.62) * mm, v(323.45, 118.62) * mm]});
            skFitSpline(sketch, "E642", {"points": [v(323.88, 118.37) * mm, v(323.99, 118.19) * mm, v(324.2, 118.1) * mm, v(324.4, 118.13) * mm]});
            skFitSpline(sketch, "E643", {"points": [v(324.4, 118.13) * mm, v(324.6, 118.17) * mm, v(324.77, 118.33) * mm, v(324.8, 118.54) * mm]});
            skFitSpline(sketch, "E644", {"points": [v(324.8, 118.54) * mm, v(324.84, 118.74) * mm, v(324.75, 118.95) * mm, v(324.56, 119.05) * mm]});
            skFitSpline(sketch, "E645", {"points": [v(324.31, 119.49) * mm, v(324.31, 119.3) * mm, v(324.4, 119.14) * mm, v(324.56, 119.05) * mm]});
            skLineSegment(sketch, "E646", {"start": v(344.65, 121.92) * mm, "end": v(340.18, 121.92) * mm});
            skFitSpline(sketch, "E647", {"points": [v(324.56, 121.49) * mm, v(324.4, 121.4) * mm, v(324.31, 121.23) * mm, v(324.31, 121.06) * mm]});
            skFitSpline(sketch, "E648", {"points": [v(324.56, 121.49) * mm, v(324.75, 121.6) * mm, v(324.84, 121.8) * mm, v(324.8, 122) * mm]});
            skFitSpline(sketch, "E649", {"points": [v(324.8, 122) * mm, v(324.77, 122.22) * mm, v(324.6, 122.38) * mm, v(324.4, 122.41) * mm]});
            skFitSpline(sketch, "E650", {"points": [v(324.4, 122.41) * mm, v(324.2, 122.45) * mm, v(323.99, 122.35) * mm, v(323.88, 122.17) * mm]});
            skFitSpline(sketch, "E651", {"points": [v(323.45, 121.92) * mm, v(323.63, 121.92) * mm, v(323.8, 122.02) * mm, v(323.88, 122.17) * mm]});
            skLineSegment(sketch, "E652", {"start": v(339.31, 121.06) * mm, "end": v(339.31, 119.49) * mm});
            skFitSpline(sketch, "E653", {"points": [v(318.55, 122.17) * mm, v(318.64, 122.02) * mm, v(318.8, 121.92) * mm, v(318.98, 121.92) * mm]});
            skFitSpline(sketch, "E654", {"points": [v(318.55, 122.17) * mm, v(318.44, 122.35) * mm, v(318.23, 122.45) * mm, v(318.03, 122.41) * mm]});
            skFitSpline(sketch, "E655", {"points": [v(318.03, 122.41) * mm, v(317.82, 122.38) * mm, v(317.66, 122.22) * mm, v(317.62, 122) * mm]});
            skFitSpline(sketch, "E656", {"points": [v(317.62, 122) * mm, v(317.59, 121.8) * mm, v(317.68, 121.6) * mm, v(317.86, 121.49) * mm]});
            skFitSpline(sketch, "E657", {"points": [v(318.11, 121.06) * mm, v(318.11, 121.23) * mm, v(318.02, 121.4) * mm, v(317.86, 121.49) * mm]});
            skLineSegment(sketch, "E658", {"start": v(318.98, 118.62) * mm, "end": v(323.45, 118.62) * mm});
            skFitSpline(sketch, "E659", {"points": [v(219.32, 121.06) * mm, v(219.32, 121.23) * mm, v(219.22, 121.4) * mm, v(219.07, 121.49) * mm]});
            skFitSpline(sketch, "E660", {"points": [v(219.75, 122.17) * mm, v(219.64, 122.35) * mm, v(219.44, 122.45) * mm, v(219.23, 122.41) * mm]});
            skFitSpline(sketch, "E661", {"points": [v(219.23, 122.41) * mm, v(219.02, 122.38) * mm, v(218.86, 122.22) * mm, v(218.82, 122) * mm]});
            skFitSpline(sketch, "E662", {"points": [v(218.82, 122) * mm, v(218.79, 121.8) * mm, v(218.88, 121.6) * mm, v(219.07, 121.49) * mm]});
            skFitSpline(sketch, "E663", {"points": [v(219.75, 122.17) * mm, v(219.84, 122.02) * mm, v(220, 121.92) * mm, v(220.18, 121.92) * mm]});
            skLineSegment(sketch, "E664", {"start": v(324.31, 119.49) * mm, "end": v(324.31, 121.06) * mm});
            skFitSpline(sketch, "E665", {"points": [v(224.65, 121.92) * mm, v(224.83, 121.92) * mm, v(225, 122.02) * mm, v(225.08, 122.17) * mm]});
            skFitSpline(sketch, "E666", {"points": [v(225.77, 121.49) * mm, v(225.95, 121.6) * mm, v(226.04, 121.8) * mm, v(226, 122) * mm]});
            skFitSpline(sketch, "E667", {"points": [v(226, 122) * mm, v(225.97, 122.22) * mm, v(225.8, 122.38) * mm, v(225.6, 122.41) * mm]});
            skFitSpline(sketch, "E668", {"points": [v(225.6, 122.41) * mm, v(225.4, 122.45) * mm, v(225.19, 122.35) * mm, v(225.08, 122.17) * mm]});
            skFitSpline(sketch, "E669", {"points": [v(225.77, 121.49) * mm, v(225.61, 121.4) * mm, v(225.52, 121.23) * mm, v(225.52, 121.06) * mm]});
            skLineSegment(sketch, "E670", {"start": v(323.45, 121.92) * mm, "end": v(318.98, 121.92) * mm});
            skFitSpline(sketch, "E671", {"points": [v(225.52, 119.49) * mm, v(225.52, 119.3) * mm, v(225.61, 119.14) * mm, v(225.77, 119.05) * mm]});
            skFitSpline(sketch, "E672", {"points": [v(225.08, 118.37) * mm, v(225.19, 118.19) * mm, v(225.4, 118.1) * mm, v(225.6, 118.13) * mm]});
            skFitSpline(sketch, "E673", {"points": [v(225.6, 118.13) * mm, v(225.8, 118.17) * mm, v(225.97, 118.33) * mm, v(226, 118.54) * mm]});
            skFitSpline(sketch, "E674", {"points": [v(226, 118.54) * mm, v(226.04, 118.74) * mm, v(225.95, 118.95) * mm, v(225.77, 119.05) * mm]});
            skFitSpline(sketch, "E675", {"points": [v(225.08, 118.37) * mm, v(225, 118.53) * mm, v(224.83, 118.62) * mm, v(224.65, 118.62) * mm]});
            skLineSegment(sketch, "E676", {"start": v(318.11, 121.06) * mm, "end": v(318.11, 119.49) * mm});
            skFitSpline(sketch, "E677", {"points": [v(220.18, 118.62) * mm, v(220, 118.62) * mm, v(219.84, 118.53) * mm, v(219.75, 118.37) * mm]});
            skFitSpline(sketch, "E678", {"points": [v(219.07, 119.05) * mm, v(218.88, 118.95) * mm, v(218.79, 118.74) * mm, v(218.82, 118.54) * mm]});
            skFitSpline(sketch, "E679", {"points": [v(218.82, 118.54) * mm, v(218.86, 118.33) * mm, v(219.02, 118.17) * mm, v(219.23, 118.13) * mm]});
            skFitSpline(sketch, "E680", {"points": [v(219.23, 118.13) * mm, v(219.44, 118.1) * mm, v(219.64, 118.19) * mm, v(219.75, 118.37) * mm]});
            skFitSpline(sketch, "E681", {"points": [v(219.07, 119.05) * mm, v(219.22, 119.14) * mm, v(219.32, 119.3) * mm, v(219.32, 119.49) * mm]});
            skLineSegment(sketch, "E682", {"start": v(220.18, 121.92) * mm, "end": v(224.65, 121.92) * mm});
            skFitSpline(sketch, "E683", {"points": [v(198.12, 121.06) * mm, v(198.12, 121.23) * mm, v(198.02, 121.4) * mm, v(197.87, 121.49) * mm]});
            skFitSpline(sketch, "E684", {"points": [v(198.55, 122.17) * mm, v(198.44, 122.35) * mm, v(198.24, 122.45) * mm, v(198.03, 122.41) * mm]});
            skFitSpline(sketch, "E685", {"points": [v(198.03, 122.41) * mm, v(197.82, 122.38) * mm, v(197.66, 122.22) * mm, v(197.62, 122) * mm]});
            skFitSpline(sketch, "E686", {"points": [v(197.62, 122) * mm, v(197.59, 121.8) * mm, v(197.68, 121.6) * mm, v(197.87, 121.49) * mm]});
            skFitSpline(sketch, "E687", {"points": [v(198.55, 122.17) * mm, v(198.64, 122.02) * mm, v(198.8, 121.92) * mm, v(198.98, 121.92) * mm]});
            skLineSegment(sketch, "E688", {"start": v(225.52, 121.06) * mm, "end": v(225.52, 119.49) * mm});
            skFitSpline(sketch, "E689", {"points": [v(203.45, 121.92) * mm, v(203.63, 121.92) * mm, v(203.8, 122.02) * mm, v(203.88, 122.17) * mm]});
            skFitSpline(sketch, "E690", {"points": [v(204.57, 121.49) * mm, v(204.75, 121.6) * mm, v(204.84, 121.8) * mm, v(204.8, 122) * mm]});
            skFitSpline(sketch, "E691", {"points": [v(204.8, 122) * mm, v(204.77, 122.22) * mm, v(204.6, 122.38) * mm, v(204.4, 122.41) * mm]});
            skFitSpline(sketch, "E692", {"points": [v(204.4, 122.41) * mm, v(204.2, 122.45) * mm, v(203.99, 122.35) * mm, v(203.88, 122.17) * mm]});
            skFitSpline(sketch, "E693", {"points": [v(204.57, 121.49) * mm, v(204.41, 121.4) * mm, v(204.32, 121.23) * mm, v(204.32, 121.06) * mm]});
            skLineSegment(sketch, "E694", {"start": v(224.65, 118.62) * mm, "end": v(220.18, 118.62) * mm});
            skFitSpline(sketch, "E695", {"points": [v(204.32, 119.49) * mm, v(204.32, 119.3) * mm, v(204.41, 119.14) * mm, v(204.57, 119.05) * mm]});
            skFitSpline(sketch, "E696", {"points": [v(203.88, 118.37) * mm, v(203.99, 118.19) * mm, v(204.2, 118.1) * mm, v(204.4, 118.13) * mm]});
            skFitSpline(sketch, "E697", {"points": [v(204.4, 118.13) * mm, v(204.6, 118.17) * mm, v(204.77, 118.33) * mm, v(204.8, 118.54) * mm]});
            skFitSpline(sketch, "E698", {"points": [v(204.8, 118.54) * mm, v(204.84, 118.74) * mm, v(204.75, 118.95) * mm, v(204.57, 119.05) * mm]});
            skFitSpline(sketch, "E699", {"points": [v(203.88, 118.37) * mm, v(203.8, 118.53) * mm, v(203.63, 118.62) * mm, v(203.45, 118.62) * mm]});
            skLineSegment(sketch, "E700", {"start": v(219.32, 119.49) * mm, "end": v(219.32, 121.06) * mm});
            skFitSpline(sketch, "E701", {"points": [v(198.98, 118.62) * mm, v(198.8, 118.62) * mm, v(198.64, 118.53) * mm, v(198.55, 118.37) * mm]});
            skFitSpline(sketch, "E702", {"points": [v(197.87, 119.05) * mm, v(197.68, 118.95) * mm, v(197.59, 118.74) * mm, v(197.62, 118.54) * mm]});
            skFitSpline(sketch, "E703", {"points": [v(197.62, 118.54) * mm, v(197.66, 118.33) * mm, v(197.82, 118.17) * mm, v(198.03, 118.13) * mm]});
            skFitSpline(sketch, "E704", {"points": [v(198.03, 118.13) * mm, v(198.24, 118.1) * mm, v(198.44, 118.19) * mm, v(198.55, 118.37) * mm]});
            skFitSpline(sketch, "E705", {"points": [v(197.87, 119.05) * mm, v(198.02, 119.14) * mm, v(198.12, 119.3) * mm, v(198.12, 119.49) * mm]});
            skLineSegment(sketch, "E706", {"start": v(198.98, 121.92) * mm, "end": v(203.45, 121.92) * mm});
            skFitSpline(sketch, "E707", {"points": [v(59.32, 121.06) * mm, v(59.32, 121.23) * mm, v(59.22, 121.4) * mm, v(59.07, 121.49) * mm]});
            skFitSpline(sketch, "E708", {"points": [v(59.75, 122.17) * mm, v(59.64, 122.35) * mm, v(59.44, 122.45) * mm, v(59.23, 122.41) * mm]});
            skFitSpline(sketch, "E709", {"points": [v(59.23, 122.41) * mm, v(59.02, 122.38) * mm, v(58.86, 122.22) * mm, v(58.82, 122) * mm]});
            skFitSpline(sketch, "E710", {"points": [v(58.82, 122) * mm, v(58.79, 121.8) * mm, v(58.88, 121.6) * mm, v(59.07, 121.49) * mm]});
            skFitSpline(sketch, "E711", {"points": [v(59.75, 122.17) * mm, v(59.84, 122.02) * mm, v(60, 121.92) * mm, v(60.18, 121.92) * mm]});
            skLineSegment(sketch, "E712", {"start": v(204.32, 121.06) * mm, "end": v(204.32, 119.49) * mm});
            skFitSpline(sketch, "E713", {"points": [v(64.65, 121.92) * mm, v(64.83, 121.92) * mm, v(65, 122.02) * mm, v(65.08, 122.17) * mm]});
            skFitSpline(sketch, "E714", {"points": [v(65.77, 121.49) * mm, v(65.95, 121.6) * mm, v(66.05, 121.8) * mm, v(66, 122) * mm]});
            skFitSpline(sketch, "E715", {"points": [v(66, 122) * mm, v(65.97, 122.22) * mm, v(65.81, 122.38) * mm, v(65.6, 122.41) * mm]});
            skFitSpline(sketch, "E716", {"points": [v(65.6, 122.41) * mm, v(65.4, 122.45) * mm, v(65.19, 122.35) * mm, v(65.08, 122.17) * mm]});
            skFitSpline(sketch, "E717", {"points": [v(65.77, 121.49) * mm, v(65.61, 121.4) * mm, v(65.52, 121.23) * mm, v(65.52, 121.06) * mm]});
            skLineSegment(sketch, "E718", {"start": v(203.45, 118.62) * mm, "end": v(198.98, 118.62) * mm});
            skFitSpline(sketch, "E719", {"points": [v(65.52, 119.49) * mm, v(65.52, 119.3) * mm, v(65.61, 119.14) * mm, v(65.77, 119.05) * mm]});
            skFitSpline(sketch, "E720", {"points": [v(65.08, 118.37) * mm, v(65.19, 118.19) * mm, v(65.4, 118.1) * mm, v(65.6, 118.13) * mm]});
            skFitSpline(sketch, "E721", {"points": [v(65.6, 118.13) * mm, v(65.81, 118.17) * mm, v(65.97, 118.33) * mm, v(66, 118.54) * mm]});
            skFitSpline(sketch, "E722", {"points": [v(66, 118.54) * mm, v(66.05, 118.74) * mm, v(65.95, 118.95) * mm, v(65.77, 119.05) * mm]});
            skFitSpline(sketch, "E723", {"points": [v(65.08, 118.37) * mm, v(65, 118.53) * mm, v(64.83, 118.62) * mm, v(64.65, 118.62) * mm]});
            skLineSegment(sketch, "E724", {"start": v(198.12, 119.49) * mm, "end": v(198.12, 121.06) * mm});
            skFitSpline(sketch, "E725", {"points": [v(60.18, 118.62) * mm, v(60, 118.62) * mm, v(59.84, 118.53) * mm, v(59.75, 118.37) * mm]});
            skFitSpline(sketch, "E726", {"points": [v(59.07, 119.05) * mm, v(58.88, 118.95) * mm, v(58.79, 118.74) * mm, v(58.82, 118.54) * mm]});
            skFitSpline(sketch, "E727", {"points": [v(58.82, 118.54) * mm, v(58.86, 118.33) * mm, v(59.02, 118.17) * mm, v(59.23, 118.13) * mm]});
            skFitSpline(sketch, "E728", {"points": [v(59.23, 118.13) * mm, v(59.44, 118.1) * mm, v(59.64, 118.19) * mm, v(59.75, 118.37) * mm]});
            skFitSpline(sketch, "E729", {"points": [v(59.07, 119.05) * mm, v(59.22, 119.14) * mm, v(59.32, 119.3) * mm, v(59.32, 119.49) * mm]});
            skLineSegment(sketch, "E730", {"start": v(60.18, 121.92) * mm, "end": v(64.65, 121.92) * mm});
            skFitSpline(sketch, "E731", {"points": [v(38.12, 121.06) * mm, v(38.12, 121.23) * mm, v(38.02, 121.4) * mm, v(37.87, 121.49) * mm]});
            skFitSpline(sketch, "E732", {"points": [v(38.55, 122.17) * mm, v(38.44, 122.35) * mm, v(38.24, 122.45) * mm, v(38.03, 122.41) * mm]});
            skFitSpline(sketch, "E733", {"points": [v(38.03, 122.41) * mm, v(37.82, 122.38) * mm, v(37.66, 122.22) * mm, v(37.62, 122) * mm]});
            skFitSpline(sketch, "E734", {"points": [v(37.62, 122) * mm, v(37.59, 121.8) * mm, v(37.68, 121.6) * mm, v(37.87, 121.49) * mm]});
            skFitSpline(sketch, "E735", {"points": [v(38.55, 122.17) * mm, v(38.64, 122.02) * mm, v(38.8, 121.92) * mm, v(38.98, 121.92) * mm]});
            skLineSegment(sketch, "E736", {"start": v(65.52, 121.06) * mm, "end": v(65.52, 119.49) * mm});
            skFitSpline(sketch, "E737", {"points": [v(43.45, 121.92) * mm, v(43.63, 121.92) * mm, v(43.8, 122.02) * mm, v(43.88, 122.17) * mm]});
            skFitSpline(sketch, "E738", {"points": [v(44.57, 121.49) * mm, v(44.75, 121.6) * mm, v(44.85, 121.8) * mm, v(44.8, 122) * mm]});
            skFitSpline(sketch, "E739", {"points": [v(44.8, 122) * mm, v(44.77, 122.22) * mm, v(44.61, 122.38) * mm, v(44.4, 122.41) * mm]});
            skFitSpline(sketch, "E740", {"points": [v(44.4, 122.41) * mm, v(44.2, 122.45) * mm, v(43.99, 122.35) * mm, v(43.88, 122.17) * mm]});
            skFitSpline(sketch, "E741", {"points": [v(44.57, 121.49) * mm, v(44.41, 121.4) * mm, v(44.32, 121.23) * mm, v(44.32, 121.06) * mm]});
            skLineSegment(sketch, "E742", {"start": v(64.65, 118.62) * mm, "end": v(60.18, 118.62) * mm});
            skFitSpline(sketch, "E743", {"points": [v(44.32, 119.49) * mm, v(44.32, 119.3) * mm, v(44.41, 119.14) * mm, v(44.57, 119.05) * mm]});
            skFitSpline(sketch, "E744", {"points": [v(43.88, 118.37) * mm, v(43.99, 118.19) * mm, v(44.2, 118.1) * mm, v(44.4, 118.13) * mm]});
            skFitSpline(sketch, "E745", {"points": [v(44.4, 118.13) * mm, v(44.61, 118.17) * mm, v(44.77, 118.33) * mm, v(44.8, 118.54) * mm]});
            skFitSpline(sketch, "E746", {"points": [v(44.8, 118.54) * mm, v(44.85, 118.74) * mm, v(44.75, 118.95) * mm, v(44.57, 119.05) * mm]});
            skFitSpline(sketch, "E747", {"points": [v(43.88, 118.37) * mm, v(43.8, 118.53) * mm, v(43.63, 118.62) * mm, v(43.45, 118.62) * mm]});
            skLineSegment(sketch, "E748", {"start": v(59.32, 119.49) * mm, "end": v(59.32, 121.06) * mm});
            skFitSpline(sketch, "E749", {"points": [v(38.98, 118.62) * mm, v(38.8, 118.62) * mm, v(38.64, 118.53) * mm, v(38.55, 118.37) * mm]});
            skFitSpline(sketch, "E750", {"points": [v(37.87, 119.05) * mm, v(37.68, 118.95) * mm, v(37.59, 118.74) * mm, v(37.62, 118.54) * mm]});
            skFitSpline(sketch, "E751", {"points": [v(37.62, 118.54) * mm, v(37.66, 118.33) * mm, v(37.82, 118.17) * mm, v(38.03, 118.13) * mm]});
            skFitSpline(sketch, "E752", {"points": [v(38.03, 118.13) * mm, v(38.24, 118.1) * mm, v(38.44, 118.19) * mm, v(38.55, 118.37) * mm]});
            skFitSpline(sketch, "E753", {"points": [v(37.87, 119.05) * mm, v(38.02, 119.14) * mm, v(38.12, 119.3) * mm, v(38.12, 119.49) * mm]});
            skLineSegment(sketch, "E754", {"start": v(38.98, 121.92) * mm, "end": v(43.45, 121.92) * mm});
            skFitSpline(sketch, "E755", {"points": [v(379.06, 139.66) * mm, v(379.22, 139.75) * mm, v(379.31, 139.91) * mm, v(379.31, 140.1) * mm]});
            skFitSpline(sketch, "E756", {"points": [v(379.06, 139.66) * mm, v(378.88, 139.55) * mm, v(378.78, 139.35) * mm, v(378.82, 139.14) * mm]});
            skFitSpline(sketch, "E757", {"points": [v(378.82, 139.14) * mm, v(378.86, 138.93) * mm, v(379.02, 138.77) * mm, v(379.23, 138.73) * mm]});
            skFitSpline(sketch, "E758", {"points": [v(379.23, 138.73) * mm, v(379.43, 138.7) * mm, v(379.64, 138.8) * mm, v(379.75, 138.98) * mm]});
            skFitSpline(sketch, "E759", {"points": [v(380.18, 139.23) * mm, v(380, 139.23) * mm, v(379.84, 139.13) * mm, v(379.75, 138.98) * mm]});
            skLineSegment(sketch, "E760", {"start": v(44.32, 121.06) * mm, "end": v(44.32, 119.49) * mm});
            skFitSpline(sketch, "E761", {"points": [v(385.08, 138.98) * mm, v(385, 139.13) * mm, v(384.83, 139.23) * mm, v(384.65, 139.23) * mm]});
            skFitSpline(sketch, "E762", {"points": [v(385.08, 138.98) * mm, v(385.19, 138.8) * mm, v(385.4, 138.7) * mm, v(385.6, 138.73) * mm]});
            skFitSpline(sketch, "E763", {"points": [v(385.6, 138.73) * mm, v(385.8, 138.77) * mm, v(385.97, 138.93) * mm, v(386, 139.14) * mm]});
            skFitSpline(sketch, "E764", {"points": [v(386, 139.14) * mm, v(386.04, 139.35) * mm, v(385.95, 139.55) * mm, v(385.76, 139.66) * mm]});
            skFitSpline(sketch, "E765", {"points": [v(385.51, 140.1) * mm, v(385.51, 139.91) * mm, v(385.6, 139.75) * mm, v(385.76, 139.66) * mm]});
            skLineSegment(sketch, "E766", {"start": v(43.45, 118.62) * mm, "end": v(38.98, 118.62) * mm});
            skFitSpline(sketch, "E767", {"points": [v(385.76, 142.1) * mm, v(385.6, 142) * mm, v(385.51, 141.84) * mm, v(385.51, 141.66) * mm]});
            skFitSpline(sketch, "E768", {"points": [v(385.76, 142.1) * mm, v(385.95, 142.2) * mm, v(386.04, 142.4) * mm, v(386, 142.61) * mm]});
            skFitSpline(sketch, "E769", {"points": [v(386, 142.61) * mm, v(385.97, 142.82) * mm, v(385.8, 142.98) * mm, v(385.6, 143.02) * mm]});
            skFitSpline(sketch, "E770", {"points": [v(385.6, 143.02) * mm, v(385.4, 143.06) * mm, v(385.19, 142.96) * mm, v(385.08, 142.78) * mm]});
            skFitSpline(sketch, "E771", {"points": [v(384.65, 142.53) * mm, v(384.83, 142.53) * mm, v(385, 142.62) * mm, v(385.08, 142.78) * mm]});
            skLineSegment(sketch, "E772", {"start": v(38.12, 119.49) * mm, "end": v(38.12, 121.06) * mm});
            skFitSpline(sketch, "E773", {"points": [v(379.75, 142.78) * mm, v(379.84, 142.62) * mm, v(380, 142.53) * mm, v(380.18, 142.53) * mm]});
            skFitSpline(sketch, "E774", {"points": [v(379.75, 142.78) * mm, v(379.64, 142.96) * mm, v(379.43, 143.06) * mm, v(379.23, 143.02) * mm]});
            skFitSpline(sketch, "E775", {"points": [v(379.23, 143.02) * mm, v(379.02, 142.98) * mm, v(378.86, 142.82) * mm, v(378.82, 142.61) * mm]});
            skFitSpline(sketch, "E776", {"points": [v(378.82, 142.61) * mm, v(378.78, 142.4) * mm, v(378.88, 142.2) * mm, v(379.06, 142.1) * mm]});
            skFitSpline(sketch, "E777", {"points": [v(379.31, 141.66) * mm, v(379.31, 141.84) * mm, v(379.22, 142) * mm, v(379.06, 142.1) * mm]});
            skLineSegment(sketch, "E778", {"start": v(380.18, 139.23) * mm, "end": v(384.65, 139.23) * mm});
            skFitSpline(sketch, "E779", {"points": [v(357.86, 139.66) * mm, v(358.02, 139.75) * mm, v(358.11, 139.91) * mm, v(358.11, 140.1) * mm]});
            skFitSpline(sketch, "E780", {"points": [v(357.86, 139.66) * mm, v(357.68, 139.55) * mm, v(357.58, 139.35) * mm, v(357.62, 139.14) * mm]});
            skFitSpline(sketch, "E781", {"points": [v(357.62, 139.14) * mm, v(357.66, 138.93) * mm, v(357.82, 138.77) * mm, v(358.03, 138.73) * mm]});
            skFitSpline(sketch, "E782", {"points": [v(358.03, 138.73) * mm, v(358.23, 138.7) * mm, v(358.44, 138.8) * mm, v(358.55, 138.98) * mm]});
            skFitSpline(sketch, "E783", {"points": [v(358.98, 139.23) * mm, v(358.8, 139.23) * mm, v(358.64, 139.13) * mm, v(358.55, 138.98) * mm]});
            skLineSegment(sketch, "E784", {"start": v(385.51, 140.1) * mm, "end": v(385.51, 141.66) * mm});
            skFitSpline(sketch, "E785", {"points": [v(363.88, 138.98) * mm, v(363.8, 139.13) * mm, v(363.63, 139.23) * mm, v(363.45, 139.23) * mm]});
            skFitSpline(sketch, "E786", {"points": [v(363.88, 138.98) * mm, v(363.99, 138.8) * mm, v(364.2, 138.7) * mm, v(364.4, 138.73) * mm]});
            skFitSpline(sketch, "E787", {"points": [v(364.4, 138.73) * mm, v(364.6, 138.77) * mm, v(364.77, 138.93) * mm, v(364.8, 139.14) * mm]});
            skFitSpline(sketch, "E788", {"points": [v(364.8, 139.14) * mm, v(364.84, 139.35) * mm, v(364.75, 139.55) * mm, v(364.56, 139.66) * mm]});
            skFitSpline(sketch, "E789", {"points": [v(364.31, 140.1) * mm, v(364.31, 139.91) * mm, v(364.4, 139.75) * mm, v(364.56, 139.66) * mm]});
            skLineSegment(sketch, "E790", {"start": v(384.65, 142.53) * mm, "end": v(380.18, 142.53) * mm});
            skFitSpline(sketch, "E791", {"points": [v(364.56, 142.1) * mm, v(364.4, 142) * mm, v(364.31, 141.84) * mm, v(364.31, 141.66) * mm]});
            skFitSpline(sketch, "E792", {"points": [v(364.56, 142.1) * mm, v(364.75, 142.2) * mm, v(364.84, 142.4) * mm, v(364.8, 142.61) * mm]});
            skFitSpline(sketch, "E793", {"points": [v(364.8, 142.61) * mm, v(364.77, 142.82) * mm, v(364.6, 142.98) * mm, v(364.4, 143.02) * mm]});
            skFitSpline(sketch, "E794", {"points": [v(364.4, 143.02) * mm, v(364.2, 143.06) * mm, v(363.99, 142.96) * mm, v(363.88, 142.78) * mm]});
            skFitSpline(sketch, "E795", {"points": [v(363.45, 142.53) * mm, v(363.63, 142.53) * mm, v(363.8, 142.62) * mm, v(363.88, 142.78) * mm]});
            skLineSegment(sketch, "E796", {"start": v(379.31, 141.66) * mm, "end": v(379.31, 140.1) * mm});
            skFitSpline(sketch, "E797", {"points": [v(358.55, 142.78) * mm, v(358.64, 142.62) * mm, v(358.8, 142.53) * mm, v(358.98, 142.53) * mm]});
            skFitSpline(sketch, "E798", {"points": [v(358.55, 142.78) * mm, v(358.44, 142.96) * mm, v(358.23, 143.06) * mm, v(358.03, 143.02) * mm]});
            skFitSpline(sketch, "E799", {"points": [v(358.03, 143.02) * mm, v(357.82, 142.98) * mm, v(357.66, 142.82) * mm, v(357.62, 142.61) * mm]});
            skFitSpline(sketch, "E800", {"points": [v(357.62, 142.61) * mm, v(357.58, 142.4) * mm, v(357.68, 142.2) * mm, v(357.86, 142.1) * mm]});
            skFitSpline(sketch, "E801", {"points": [v(358.11, 141.66) * mm, v(358.11, 141.84) * mm, v(358.02, 142) * mm, v(357.86, 142.1) * mm]});
            skLineSegment(sketch, "E802", {"start": v(358.98, 139.23) * mm, "end": v(363.45, 139.23) * mm});
            skFitSpline(sketch, "E803", {"points": [v(343.95, 158.15) * mm, v(344.04, 158) * mm, v(344.2, 157.9) * mm, v(344.39, 157.9) * mm]});
            skFitSpline(sketch, "E804", {"points": [v(343.95, 158.15) * mm, v(343.85, 158.33) * mm, v(343.64, 158.43) * mm, v(343.43, 158.39) * mm]});
            skFitSpline(sketch, "E805", {"points": [v(343.43, 158.39) * mm, v(343.23, 158.35) * mm, v(343.06, 158.2) * mm, v(343.03, 157.98) * mm]});
            skFitSpline(sketch, "E806", {"points": [v(343.03, 157.98) * mm, v(343, 157.78) * mm, v(343.09, 157.57) * mm, v(343.27, 157.46) * mm]});
            skFitSpline(sketch, "E807", {"points": [v(343.52, 157.03) * mm, v(343.52, 157.2) * mm, v(343.42, 157.37) * mm, v(343.27, 157.46) * mm]});
            skLineSegment(sketch, "E808", {"start": v(364.31, 140.1) * mm, "end": v(364.31, 141.66) * mm});
            skFitSpline(sketch, "E809", {"points": [v(343.27, 152.13) * mm, v(343.42, 152.22) * mm, v(343.52, 152.38) * mm, v(343.52, 152.56) * mm]});
            skFitSpline(sketch, "E810", {"points": [v(343.27, 152.13) * mm, v(343.09, 152.02) * mm, v(343, 151.82) * mm, v(343.03, 151.6) * mm]});
            skFitSpline(sketch, "E811", {"points": [v(343.03, 151.6) * mm, v(343.06, 151.4) * mm, v(343.23, 151.24) * mm, v(343.43, 151.2) * mm]});
            skFitSpline(sketch, "E812", {"points": [v(343.43, 151.2) * mm, v(343.64, 151.17) * mm, v(343.85, 151.26) * mm, v(343.95, 151.45) * mm]});
            skFitSpline(sketch, "E813", {"points": [v(344.39, 151.7) * mm, v(344.2, 151.7) * mm, v(344.04, 151.6) * mm, v(343.95, 151.45) * mm]});
            skLineSegment(sketch, "E814", {"start": v(363.45, 142.53) * mm, "end": v(358.98, 142.53) * mm});
            skFitSpline(sketch, "E815", {"points": [v(346.39, 151.45) * mm, v(346.3, 151.6) * mm, v(346.13, 151.7) * mm, v(345.95, 151.7) * mm]});
            skFitSpline(sketch, "E816", {"points": [v(346.39, 151.45) * mm, v(346.5, 151.26) * mm, v(346.7, 151.17) * mm, v(346.9, 151.2) * mm]});
            skFitSpline(sketch, "E817", {"points": [v(346.9, 151.2) * mm, v(347.11, 151.24) * mm, v(347.27, 151.4) * mm, v(347.31, 151.6) * mm]});
            skFitSpline(sketch, "E818", {"points": [v(347.31, 151.6) * mm, v(347.35, 151.82) * mm, v(347.25, 152.02) * mm, v(347.07, 152.13) * mm]});
            skFitSpline(sketch, "E819", {"points": [v(346.82, 152.56) * mm, v(346.82, 152.38) * mm, v(346.91, 152.22) * mm, v(347.07, 152.13) * mm]});
            skLineSegment(sketch, "E820", {"start": v(358.11, 141.66) * mm, "end": v(358.11, 140.1) * mm});
            skFitSpline(sketch, "E821", {"points": [v(347.07, 157.46) * mm, v(346.91, 157.37) * mm, v(346.82, 157.2) * mm, v(346.82, 157.03) * mm]});
            skFitSpline(sketch, "E822", {"points": [v(347.07, 157.46) * mm, v(347.25, 157.57) * mm, v(347.35, 157.78) * mm, v(347.31, 157.98) * mm]});
            skFitSpline(sketch, "E823", {"points": [v(347.31, 157.98) * mm, v(347.27, 158.2) * mm, v(347.11, 158.35) * mm, v(346.9, 158.39) * mm]});
            skFitSpline(sketch, "E824", {"points": [v(346.9, 158.39) * mm, v(346.7, 158.43) * mm, v(346.5, 158.33) * mm, v(346.39, 158.15) * mm]});
            skFitSpline(sketch, "E825", {"points": [v(345.95, 157.9) * mm, v(346.13, 157.9) * mm, v(346.3, 158) * mm, v(346.39, 158.15) * mm]});
            skLineSegment(sketch, "E826", {"start": v(343.52, 157.03) * mm, "end": v(343.52, 152.56) * mm});
            skFitSpline(sketch, "E827", {"points": [v(343.95, 179.35) * mm, v(344.04, 179.2) * mm, v(344.2, 179.1) * mm, v(344.39, 179.1) * mm]});
            skFitSpline(sketch, "E828", {"points": [v(343.95, 179.35) * mm, v(343.85, 179.53) * mm, v(343.64, 179.63) * mm, v(343.43, 179.59) * mm]});
            skFitSpline(sketch, "E829", {"points": [v(343.43, 179.59) * mm, v(343.23, 179.55) * mm, v(343.06, 179.4) * mm, v(343.03, 179.18) * mm]});
            skFitSpline(sketch, "E830", {"points": [v(343.03, 179.18) * mm, v(343, 178.98) * mm, v(343.09, 178.77) * mm, v(343.27, 178.66) * mm]});
            skFitSpline(sketch, "E831", {"points": [v(343.52, 178.23) * mm, v(343.52, 178.4) * mm, v(343.42, 178.57) * mm, v(343.27, 178.66) * mm]});
            skLineSegment(sketch, "E832", {"start": v(344.39, 151.7) * mm, "end": v(345.95, 151.7) * mm});
            skFitSpline(sketch, "E833", {"points": [v(343.27, 173.33) * mm, v(343.42, 173.42) * mm, v(343.52, 173.58) * mm, v(343.52, 173.76) * mm]});
            skFitSpline(sketch, "E834", {"points": [v(343.27, 173.33) * mm, v(343.09, 173.22) * mm, v(343, 173.02) * mm, v(343.03, 172.8) * mm]});
            skFitSpline(sketch, "E835", {"points": [v(343.03, 172.8) * mm, v(343.06, 172.6) * mm, v(343.23, 172.44) * mm, v(343.43, 172.4) * mm]});
            skFitSpline(sketch, "E836", {"points": [v(343.43, 172.4) * mm, v(343.64, 172.37) * mm, v(343.85, 172.46) * mm, v(343.95, 172.65) * mm]});
            skFitSpline(sketch, "E837", {"points": [v(344.39, 172.9) * mm, v(344.2, 172.9) * mm, v(344.04, 172.8) * mm, v(343.95, 172.65) * mm]});
            skLineSegment(sketch, "E838", {"start": v(346.82, 152.56) * mm, "end": v(346.82, 157.03) * mm});
            skFitSpline(sketch, "E839", {"points": [v(346.39, 172.65) * mm, v(346.3, 172.8) * mm, v(346.13, 172.9) * mm, v(345.95, 172.9) * mm]});
            skFitSpline(sketch, "E840", {"points": [v(346.39, 172.65) * mm, v(346.5, 172.46) * mm, v(346.7, 172.37) * mm, v(346.9, 172.4) * mm]});
            skFitSpline(sketch, "E841", {"points": [v(346.9, 172.4) * mm, v(347.11, 172.44) * mm, v(347.27, 172.6) * mm, v(347.31, 172.8) * mm]});
            skFitSpline(sketch, "E842", {"points": [v(347.31, 172.8) * mm, v(347.35, 173.02) * mm, v(347.25, 173.22) * mm, v(347.07, 173.33) * mm]});
            skFitSpline(sketch, "E843", {"points": [v(346.82, 173.76) * mm, v(346.82, 173.58) * mm, v(346.91, 173.42) * mm, v(347.07, 173.33) * mm]});
            skLineSegment(sketch, "E844", {"start": v(345.95, 157.9) * mm, "end": v(344.39, 157.9) * mm});
            skFitSpline(sketch, "E845", {"points": [v(347.07, 178.66) * mm, v(346.91, 178.57) * mm, v(346.82, 178.4) * mm, v(346.82, 178.23) * mm]});
            skFitSpline(sketch, "E846", {"points": [v(347.07, 178.66) * mm, v(347.25, 178.77) * mm, v(347.35, 178.98) * mm, v(347.31, 179.18) * mm]});
            skFitSpline(sketch, "E847", {"points": [v(347.31, 179.18) * mm, v(347.27, 179.4) * mm, v(347.11, 179.55) * mm, v(346.9, 179.59) * mm]});
            skFitSpline(sketch, "E848", {"points": [v(346.9, 179.59) * mm, v(346.7, 179.63) * mm, v(346.5, 179.53) * mm, v(346.39, 179.35) * mm]});
            skFitSpline(sketch, "E849", {"points": [v(345.95, 179.1) * mm, v(346.13, 179.1) * mm, v(346.3, 179.2) * mm, v(346.39, 179.35) * mm]});
            skLineSegment(sketch, "E850", {"start": v(343.52, 178.23) * mm, "end": v(343.52, 173.76) * mm});
            skFitSpline(sketch, "E851", {"points": [v(379.06, 188.7) * mm, v(379.22, 188.79) * mm, v(379.31, 188.95) * mm, v(379.31, 189.13) * mm]});
            skFitSpline(sketch, "E852", {"points": [v(379.06, 188.7) * mm, v(378.88, 188.6) * mm, v(378.78, 188.39) * mm, v(378.82, 188.18) * mm]});
            skFitSpline(sketch, "E853", {"points": [v(378.82, 188.18) * mm, v(378.86, 187.97) * mm, v(379.02, 187.81) * mm, v(379.23, 187.77) * mm]});
            skFitSpline(sketch, "E854", {"points": [v(379.23, 187.77) * mm, v(379.43, 187.74) * mm, v(379.64, 187.83) * mm, v(379.75, 188.02) * mm]});
            skFitSpline(sketch, "E855", {"points": [v(380.18, 188.27) * mm, v(380, 188.27) * mm, v(379.84, 188.17) * mm, v(379.75, 188.02) * mm]});
            skLineSegment(sketch, "E856", {"start": v(344.39, 172.9) * mm, "end": v(345.95, 172.9) * mm});
            skFitSpline(sketch, "E857", {"points": [v(385.08, 188.02) * mm, v(385, 188.17) * mm, v(384.83, 188.27) * mm, v(384.65, 188.27) * mm]});
            skFitSpline(sketch, "E858", {"points": [v(385.08, 188.02) * mm, v(385.19, 187.83) * mm, v(385.4, 187.74) * mm, v(385.6, 187.77) * mm]});
            skFitSpline(sketch, "E859", {"points": [v(385.6, 187.77) * mm, v(385.8, 187.81) * mm, v(385.97, 187.97) * mm, v(386, 188.18) * mm]});
            skFitSpline(sketch, "E860", {"points": [v(386, 188.18) * mm, v(386.04, 188.39) * mm, v(385.95, 188.6) * mm, v(385.76, 188.7) * mm]});
            skFitSpline(sketch, "E861", {"points": [v(385.51, 189.13) * mm, v(385.51, 188.95) * mm, v(385.6, 188.79) * mm, v(385.76, 188.7) * mm]});
            skLineSegment(sketch, "E862", {"start": v(346.82, 173.76) * mm, "end": v(346.82, 178.23) * mm});
            skFitSpline(sketch, "E863", {"points": [v(385.76, 191.13) * mm, v(385.6, 191.04) * mm, v(385.51, 190.88) * mm, v(385.51, 190.7) * mm]});
            skFitSpline(sketch, "E864", {"points": [v(385.76, 191.13) * mm, v(385.95, 191.24) * mm, v(386.04, 191.45) * mm, v(386, 191.65) * mm]});
            skFitSpline(sketch, "E865", {"points": [v(386, 191.65) * mm, v(385.97, 191.86) * mm, v(385.8, 192.02) * mm, v(385.6, 192.06) * mm]});
            skFitSpline(sketch, "E866", {"points": [v(385.6, 192.06) * mm, v(385.4, 192.1) * mm, v(385.19, 192) * mm, v(385.08, 191.82) * mm]});
            skFitSpline(sketch, "E867", {"points": [v(384.65, 191.57) * mm, v(384.83, 191.57) * mm, v(385, 191.66) * mm, v(385.08, 191.82) * mm]});
            skLineSegment(sketch, "E868", {"start": v(345.95, 179.1) * mm, "end": v(344.39, 179.1) * mm});
            skFitSpline(sketch, "E869", {"points": [v(379.75, 191.82) * mm, v(379.84, 191.66) * mm, v(380, 191.57) * mm, v(380.18, 191.57) * mm]});
            skFitSpline(sketch, "E870", {"points": [v(379.75, 191.82) * mm, v(379.64, 192) * mm, v(379.43, 192.1) * mm, v(379.23, 192.06) * mm]});
            skFitSpline(sketch, "E871", {"points": [v(379.23, 192.06) * mm, v(379.02, 192.02) * mm, v(378.86, 191.86) * mm, v(378.82, 191.65) * mm]});
            skFitSpline(sketch, "E872", {"points": [v(378.82, 191.65) * mm, v(378.78, 191.45) * mm, v(378.88, 191.24) * mm, v(379.06, 191.13) * mm]});
            skFitSpline(sketch, "E873", {"points": [v(379.31, 190.7) * mm, v(379.31, 190.88) * mm, v(379.22, 191.04) * mm, v(379.06, 191.13) * mm]});
            skLineSegment(sketch, "E874", {"start": v(380.18, 188.27) * mm, "end": v(384.65, 188.27) * mm});
            skFitSpline(sketch, "E875", {"points": [v(357.86, 188.7) * mm, v(358.02, 188.79) * mm, v(358.11, 188.95) * mm, v(358.11, 189.13) * mm]});
            skFitSpline(sketch, "E876", {"points": [v(357.86, 188.7) * mm, v(357.68, 188.6) * mm, v(357.58, 188.39) * mm, v(357.62, 188.18) * mm]});
            skFitSpline(sketch, "E877", {"points": [v(357.62, 188.18) * mm, v(357.66, 187.97) * mm, v(357.82, 187.81) * mm, v(358.03, 187.77) * mm]});
            skFitSpline(sketch, "E878", {"points": [v(358.03, 187.77) * mm, v(358.23, 187.74) * mm, v(358.44, 187.83) * mm, v(358.55, 188.02) * mm]});
            skFitSpline(sketch, "E879", {"points": [v(358.98, 188.27) * mm, v(358.8, 188.27) * mm, v(358.64, 188.17) * mm, v(358.55, 188.02) * mm]});
            skLineSegment(sketch, "E880", {"start": v(385.51, 189.13) * mm, "end": v(385.51, 190.7) * mm});
            skFitSpline(sketch, "E881", {"points": [v(363.88, 188.02) * mm, v(363.8, 188.17) * mm, v(363.63, 188.27) * mm, v(363.45, 188.27) * mm]});
            skFitSpline(sketch, "E882", {"points": [v(363.88, 188.02) * mm, v(363.99, 187.83) * mm, v(364.2, 187.74) * mm, v(364.4, 187.77) * mm]});
            skFitSpline(sketch, "E883", {"points": [v(364.4, 187.77) * mm, v(364.6, 187.81) * mm, v(364.77, 187.97) * mm, v(364.8, 188.18) * mm]});
            skFitSpline(sketch, "E884", {"points": [v(364.8, 188.18) * mm, v(364.84, 188.39) * mm, v(364.75, 188.6) * mm, v(364.56, 188.7) * mm]});
            skFitSpline(sketch, "E885", {"points": [v(364.31, 189.13) * mm, v(364.31, 188.95) * mm, v(364.4, 188.79) * mm, v(364.56, 188.7) * mm]});
            skLineSegment(sketch, "E886", {"start": v(384.65, 191.57) * mm, "end": v(380.18, 191.57) * mm});
            skFitSpline(sketch, "E887", {"points": [v(364.56, 191.13) * mm, v(364.4, 191.04) * mm, v(364.31, 190.88) * mm, v(364.31, 190.7) * mm]});
            skFitSpline(sketch, "E888", {"points": [v(364.56, 191.13) * mm, v(364.75, 191.24) * mm, v(364.84, 191.45) * mm, v(364.8, 191.65) * mm]});
            skFitSpline(sketch, "E889", {"points": [v(364.8, 191.65) * mm, v(364.77, 191.86) * mm, v(364.6, 192.02) * mm, v(364.4, 192.06) * mm]});
            skFitSpline(sketch, "E890", {"points": [v(364.4, 192.06) * mm, v(364.2, 192.1) * mm, v(363.99, 192) * mm, v(363.88, 191.82) * mm]});
            skFitSpline(sketch, "E891", {"points": [v(363.45, 191.57) * mm, v(363.63, 191.57) * mm, v(363.8, 191.66) * mm, v(363.88, 191.82) * mm]});
            skLineSegment(sketch, "E892", {"start": v(379.31, 190.7) * mm, "end": v(379.31, 189.13) * mm});
            skFitSpline(sketch, "E893", {"points": [v(358.55, 191.82) * mm, v(358.64, 191.66) * mm, v(358.8, 191.57) * mm, v(358.98, 191.57) * mm]});
            skFitSpline(sketch, "E894", {"points": [v(358.55, 191.82) * mm, v(358.44, 192) * mm, v(358.23, 192.1) * mm, v(358.03, 192.06) * mm]});
            skFitSpline(sketch, "E895", {"points": [v(358.03, 192.06) * mm, v(357.82, 192.02) * mm, v(357.66, 191.86) * mm, v(357.62, 191.65) * mm]});
            skFitSpline(sketch, "E896", {"points": [v(357.62, 191.65) * mm, v(357.58, 191.45) * mm, v(357.68, 191.24) * mm, v(357.86, 191.13) * mm]});
            skFitSpline(sketch, "E897", {"points": [v(358.11, 190.7) * mm, v(358.11, 190.88) * mm, v(358.02, 191.04) * mm, v(357.86, 191.13) * mm]});
            skLineSegment(sketch, "E898", {"start": v(358.98, 188.27) * mm, "end": v(363.45, 188.27) * mm});
            skFitSpline(sketch, "E899", {"points": [v(373.41, -189.72) * mm, v(373.41, -189.15) * mm, v(373.1, -188.62) * mm, v(372.61, -188.33) * mm]});
            skFitSpline(sketch, "E900", {"points": [v(372.61, -188.33) * mm, v(372.12, -188.05) * mm, v(371.5, -188.05) * mm, v(371.01, -188.33) * mm]});
            skFitSpline(sketch, "E901", {"points": [v(371.01, -188.33) * mm, v(370.52, -188.62) * mm, v(370.21, -189.15) * mm, v(370.21, -189.72) * mm]});
            skFitSpline(sketch, "E902", {"points": [v(370.21, -189.72) * mm, v(370.21, -190.3) * mm, v(370.52, -190.82) * mm, v(371.01, -191.1) * mm]});
            skFitSpline(sketch, "E903", {"points": [v(371.01, -191.1) * mm, v(371.5, -191.4) * mm, v(372.12, -191.4) * mm, v(372.61, -191.1) * mm]});
            skFitSpline(sketch, "E904", {"points": [v(372.61, -191.1) * mm, v(373.1, -190.82) * mm, v(373.41, -190.3) * mm, v(373.41, -189.72) * mm]});
            skLineSegment(sketch, "E905", {"start": v(364.31, 189.13) * mm, "end": v(364.31, 190.7) * mm});
            skFitSpline(sketch, "E906", {"points": [v(346.77, -165.2) * mm, v(346.77, -164.63) * mm, v(346.46, -164.1) * mm, v(345.97, -163.81) * mm]});
            skFitSpline(sketch, "E907", {"points": [v(345.97, -163.81) * mm, v(345.47, -163.53) * mm, v(344.86, -163.53) * mm, v(344.37, -163.81) * mm]});
            skFitSpline(sketch, "E908", {"points": [v(344.37, -163.81) * mm, v(343.87, -164.1) * mm, v(343.57, -164.63) * mm, v(343.57, -165.2) * mm]});
            skFitSpline(sketch, "E909", {"points": [v(343.57, -165.2) * mm, v(343.57, -165.77) * mm, v(343.87, -166.3) * mm, v(344.37, -166.59) * mm]});
            skFitSpline(sketch, "E910", {"points": [v(344.37, -166.59) * mm, v(344.86, -166.87) * mm, v(345.47, -166.87) * mm, v(345.97, -166.59) * mm]});
            skFitSpline(sketch, "E911", {"points": [v(345.97, -166.59) * mm, v(346.46, -166.3) * mm, v(346.77, -165.77) * mm, v(346.77, -165.2) * mm]});
            skLineSegment(sketch, "E912", {"start": v(363.45, 191.57) * mm, "end": v(358.98, 191.57) * mm});
            skFitSpline(sketch, "E913", {"points": [v(373.41, -140.68) * mm, v(373.41, -140.1) * mm, v(373.1, -139.58) * mm, v(372.61, -139.3) * mm]});
            skFitSpline(sketch, "E914", {"points": [v(372.61, -139.3) * mm, v(372.12, -139) * mm, v(371.5, -139) * mm, v(371.01, -139.3) * mm]});
            skFitSpline(sketch, "E915", {"points": [v(371.01, -139.3) * mm, v(370.52, -139.58) * mm, v(370.21, -140.1) * mm, v(370.21, -140.68) * mm]});
            skFitSpline(sketch, "E916", {"points": [v(370.21, -140.68) * mm, v(370.21, -141.25) * mm, v(370.52, -141.78) * mm, v(371.01, -142.07) * mm]});
            skFitSpline(sketch, "E917", {"points": [v(371.01, -142.07) * mm, v(371.5, -142.35) * mm, v(372.12, -142.35) * mm, v(372.61, -142.07) * mm]});
            skFitSpline(sketch, "E918", {"points": [v(372.61, -142.07) * mm, v(373.1, -141.78) * mm, v(373.41, -141.25) * mm, v(373.41, -140.68) * mm]});
            skLineSegment(sketch, "E919", {"start": v(358.11, 190.7) * mm, "end": v(358.11, 189.13) * mm});
            skFitSpline(sketch, "E920", {"points": [v(333.41, -120.08) * mm, v(333.41, -119.5) * mm, v(333.1, -118.98) * mm, v(332.61, -118.7) * mm]});
            skFitSpline(sketch, "E921", {"points": [v(332.61, -118.7) * mm, v(332.12, -118.4) * mm, v(331.5, -118.4) * mm, v(331.01, -118.7) * mm]});
            skFitSpline(sketch, "E922", {"points": [v(331.01, -118.7) * mm, v(330.52, -118.98) * mm, v(330.21, -119.5) * mm, v(330.21, -120.08) * mm]});
            skFitSpline(sketch, "E923", {"points": [v(330.21, -120.08) * mm, v(330.21, -120.96) * mm, v(330.93, -121.68) * mm, v(331.81, -121.68) * mm]});
            skFitSpline(sketch, "E924", {"points": [v(331.81, -121.68) * mm, v(332.7, -121.68) * mm, v(333.41, -120.96) * mm, v(333.41, -120.08) * mm]});
            skFitSpline(sketch, "E925", {"points": [v(213.42, -120.08) * mm, v(213.42, -119.5) * mm, v(213.11, -118.98) * mm, v(212.62, -118.7) * mm]});
            skFitSpline(sketch, "E926", {"points": [v(212.62, -118.7) * mm, v(212.12, -118.4) * mm, v(211.51, -118.4) * mm, v(211.02, -118.7) * mm]});
            skFitSpline(sketch, "E927", {"points": [v(211.02, -118.7) * mm, v(210.52, -118.98) * mm, v(210.22, -119.5) * mm, v(210.22, -120.08) * mm]});
            skFitSpline(sketch, "E928", {"points": [v(210.22, -120.08) * mm, v(210.22, -120.65) * mm, v(210.52, -121.18) * mm, v(211.02, -121.46) * mm]});
            skFitSpline(sketch, "E929", {"points": [v(211.02, -121.46) * mm, v(211.51, -121.75) * mm, v(212.12, -121.75) * mm, v(212.62, -121.46) * mm]});
            skFitSpline(sketch, "E930", {"points": [v(212.62, -121.46) * mm, v(213.11, -121.18) * mm, v(213.42, -120.65) * mm, v(213.42, -120.08) * mm]});
            skFitSpline(sketch, "E931", {"points": [v(53.42, -120.08) * mm, v(53.42, -119.5) * mm, v(53.11, -118.97) * mm, v(52.62, -118.69) * mm]});
            skFitSpline(sketch, "E932", {"points": [v(52.62, -118.69) * mm, v(52.12, -118.4) * mm, v(51.51, -118.4) * mm, v(51.02, -118.69) * mm]});
            skFitSpline(sketch, "E933", {"points": [v(51.02, -118.69) * mm, v(50.52, -118.97) * mm, v(50.21, -119.5) * mm, v(50.22, -120.08) * mm]});
            skFitSpline(sketch, "E934", {"points": [v(50.22, -120.08) * mm, v(50.21, -120.65) * mm, v(50.52, -121.18) * mm, v(51.02, -121.47) * mm]});
            skFitSpline(sketch, "E935", {"points": [v(51.02, -121.47) * mm, v(51.51, -121.75) * mm, v(52.12, -121.75) * mm, v(52.62, -121.47) * mm]});
            skFitSpline(sketch, "E936", {"points": [v(52.62, -121.47) * mm, v(53.11, -121.18) * mm, v(53.42, -120.65) * mm, v(53.42, -120.08) * mm]});
            skFitSpline(sketch, "E937", {"points": [v(333.41, 120.27) * mm, v(333.41, 120.84) * mm, v(333.1, 121.37) * mm, v(332.61, 121.66) * mm]});
            skFitSpline(sketch, "E938", {"points": [v(332.61, 121.66) * mm, v(332.12, 121.94) * mm, v(331.5, 121.94) * mm, v(331.01, 121.66) * mm]});
            skFitSpline(sketch, "E939", {"points": [v(331.01, 121.66) * mm, v(330.52, 121.37) * mm, v(330.21, 120.84) * mm, v(330.21, 120.27) * mm]});
            skFitSpline(sketch, "E940", {"points": [v(330.21, 120.27) * mm, v(330.21, 119.39) * mm, v(330.93, 118.67) * mm, v(331.81, 118.67) * mm]});
            skFitSpline(sketch, "E941", {"points": [v(331.81, 118.67) * mm, v(332.7, 118.67) * mm, v(333.41, 119.39) * mm, v(333.41, 120.27) * mm]});
            skFitSpline(sketch, "E942", {"points": [v(213.42, 120.27) * mm, v(213.42, 120.84) * mm, v(213.11, 121.37) * mm, v(212.62, 121.66) * mm]});
            skFitSpline(sketch, "E943", {"points": [v(212.62, 121.66) * mm, v(212.12, 121.94) * mm, v(211.51, 121.94) * mm, v(211.02, 121.66) * mm]});
            skFitSpline(sketch, "E944", {"points": [v(211.02, 121.66) * mm, v(210.52, 121.37) * mm, v(210.22, 120.84) * mm, v(210.22, 120.27) * mm]});
            skFitSpline(sketch, "E945", {"points": [v(210.22, 120.27) * mm, v(210.22, 119.7) * mm, v(210.52, 119.17) * mm, v(211.02, 118.89) * mm]});
            skFitSpline(sketch, "E946", {"points": [v(211.02, 118.89) * mm, v(211.51, 118.6) * mm, v(212.12, 118.6) * mm, v(212.62, 118.89) * mm]});
            skFitSpline(sketch, "E947", {"points": [v(212.62, 118.89) * mm, v(213.11, 119.17) * mm, v(213.42, 119.7) * mm, v(213.42, 120.27) * mm]});
            skFitSpline(sketch, "E948", {"points": [v(53.42, 120.27) * mm, v(53.42, 120.84) * mm, v(53.11, 121.38) * mm, v(52.62, 121.66) * mm]});
            skFitSpline(sketch, "E949", {"points": [v(52.62, 121.66) * mm, v(52.12, 121.95) * mm, v(51.51, 121.95) * mm, v(51.02, 121.66) * mm]});
            skFitSpline(sketch, "E950", {"points": [v(51.02, 121.66) * mm, v(50.52, 121.38) * mm, v(50.21, 120.84) * mm, v(50.22, 120.27) * mm]});
            skFitSpline(sketch, "E951", {"points": [v(50.22, 120.27) * mm, v(50.21, 119.7) * mm, v(50.52, 119.17) * mm, v(51.02, 118.88) * mm]});
            skFitSpline(sketch, "E952", {"points": [v(51.02, 118.88) * mm, v(51.51, 118.6) * mm, v(52.12, 118.6) * mm, v(52.62, 118.88) * mm]});
            skFitSpline(sketch, "E953", {"points": [v(52.62, 118.88) * mm, v(53.11, 119.17) * mm, v(53.42, 119.7) * mm, v(53.42, 120.27) * mm]});
            skFitSpline(sketch, "E954", {"points": [v(373.41, 140.88) * mm, v(373.41, 141.45) * mm, v(373.1, 141.98) * mm, v(372.61, 142.26) * mm]});
            skFitSpline(sketch, "E955", {"points": [v(372.61, 142.26) * mm, v(372.12, 142.55) * mm, v(371.5, 142.55) * mm, v(371.01, 142.26) * mm]});
            skFitSpline(sketch, "E956", {"points": [v(371.01, 142.26) * mm, v(370.52, 141.98) * mm, v(370.21, 141.45) * mm, v(370.21, 140.88) * mm]});
            skFitSpline(sketch, "E957", {"points": [v(370.21, 140.88) * mm, v(370.21, 140.3) * mm, v(370.52, 139.78) * mm, v(371.01, 139.5) * mm]});
            skFitSpline(sketch, "E958", {"points": [v(371.01, 139.5) * mm, v(371.5, 139.2) * mm, v(372.12, 139.2) * mm, v(372.61, 139.5) * mm]});
            skFitSpline(sketch, "E959", {"points": [v(372.61, 139.5) * mm, v(373.1, 139.78) * mm, v(373.41, 140.3) * mm, v(373.41, 140.88) * mm]});
            skFitSpline(sketch, "E960", {"points": [v(346.77, 165.4) * mm, v(346.77, 165.97) * mm, v(346.46, 166.5) * mm, v(345.97, 166.78) * mm]});
            skFitSpline(sketch, "E961", {"points": [v(345.97, 166.78) * mm, v(345.47, 167.07) * mm, v(344.86, 167.07) * mm, v(344.37, 166.78) * mm]});
            skFitSpline(sketch, "E962", {"points": [v(344.37, 166.78) * mm, v(343.87, 166.5) * mm, v(343.57, 165.97) * mm, v(343.57, 165.4) * mm]});
            skFitSpline(sketch, "E963", {"points": [v(343.57, 165.4) * mm, v(343.57, 164.82) * mm, v(343.87, 164.3) * mm, v(344.37, 164.01) * mm]});
            skFitSpline(sketch, "E964", {"points": [v(344.37, 164.01) * mm, v(344.86, 163.72) * mm, v(345.47, 163.72) * mm, v(345.97, 164.01) * mm]});
            skFitSpline(sketch, "E965", {"points": [v(345.97, 164.01) * mm, v(346.46, 164.3) * mm, v(346.77, 164.82) * mm, v(346.77, 165.4) * mm]});
            skFitSpline(sketch, "E966", {"points": [v(373.41, 189.92) * mm, v(373.41, 190.49) * mm, v(373.1, 191.02) * mm, v(372.61, 191.3) * mm]});
            skFitSpline(sketch, "E967", {"points": [v(372.61, 191.3) * mm, v(372.12, 191.59) * mm, v(371.5, 191.59) * mm, v(371.01, 191.3) * mm]});
            skFitSpline(sketch, "E968", {"points": [v(371.01, 191.3) * mm, v(370.52, 191.02) * mm, v(370.21, 190.49) * mm, v(370.21, 189.92) * mm]});
            skFitSpline(sketch, "E969", {"points": [v(370.21, 189.92) * mm, v(370.21, 189.34) * mm, v(370.52, 188.82) * mm, v(371.01, 188.53) * mm]});
            skFitSpline(sketch, "E970", {"points": [v(371.01, 188.53) * mm, v(371.5, 188.24) * mm, v(372.12, 188.24) * mm, v(372.61, 188.53) * mm]});
            skFitSpline(sketch, "E971", {"points": [v(372.61, 188.53) * mm, v(373.1, 188.82) * mm, v(373.41, 189.34) * mm, v(373.41, 189.92) * mm]});
            skFitSpline(sketch, "E972", {"points": [v(-357.78, -193.8) * mm, v(-357.7, -193.95) * mm, v(-357.53, -194.04) * mm, v(-357.35, -194.04) * mm]});
            skFitSpline(sketch, "E973", {"points": [v(-357.78, -193.8) * mm, v(-357.89, -193.61) * mm, v(-358.1, -193.52) * mm, v(-358.3, -193.55) * mm]});
            skFitSpline(sketch, "E974", {"points": [v(-358.3, -193.55) * mm, v(-358.5, -193.59) * mm, v(-358.67, -193.75) * mm, v(-358.7, -193.96) * mm]});
            skFitSpline(sketch, "E975", {"points": [v(-358.7, -193.96) * mm, v(-358.74, -194.16) * mm, v(-358.65, -194.37) * mm, v(-358.46, -194.48) * mm]});
            skFitSpline(sketch, "E976", {"points": [v(-358.21, -194.91) * mm, v(-358.21, -194.73) * mm, v(-358.3, -194.57) * mm, v(-358.46, -194.48) * mm]});
            skFitSpline(sketch, "E977", {"points": [v(-358.71, -197.04) * mm, v(-358.44, -197.04) * mm, v(-358.21, -196.82) * mm, v(-358.21, -196.54) * mm]});
            skFitSpline(sketch, "E978", {"points": [v(-364.21, -196.54) * mm, v(-364.21, -196.82) * mm, v(-363.99, -197.04) * mm, v(-363.71, -197.04) * mm]});
            skFitSpline(sketch, "E979", {"points": [v(-363.96, -194.48) * mm, v(-364.12, -194.57) * mm, v(-364.21, -194.73) * mm, v(-364.21, -194.91) * mm]});
            skFitSpline(sketch, "E980", {"points": [v(-363.96, -194.48) * mm, v(-363.78, -194.37) * mm, v(-363.68, -194.16) * mm, v(-363.72, -193.96) * mm]});
            skFitSpline(sketch, "E981", {"points": [v(-363.72, -193.96) * mm, v(-363.76, -193.75) * mm, v(-363.92, -193.59) * mm, v(-364.13, -193.55) * mm]});
            skFitSpline(sketch, "E982", {"points": [v(-364.13, -193.55) * mm, v(-364.33, -193.52) * mm, v(-364.54, -193.61) * mm, v(-364.65, -193.8) * mm]});
            skFitSpline(sketch, "E983", {"points": [v(-365.08, -194.04) * mm, v(-364.9, -194.04) * mm, v(-364.74, -193.95) * mm, v(-364.65, -193.8) * mm]});
            skLineSegment(sketch, "E984", {"start": v(-358.21, -194.91) * mm, "end": v(-358.21, -196.54) * mm});
            skFitSpline(sketch, "E985", {"points": [v(-378.98, -193.8) * mm, v(-378.9, -193.95) * mm, v(-378.73, -194.04) * mm, v(-378.55, -194.04) * mm]});
            skFitSpline(sketch, "E986", {"points": [v(-378.98, -193.8) * mm, v(-379.09, -193.61) * mm, v(-379.3, -193.52) * mm, v(-379.5, -193.55) * mm]});
            skFitSpline(sketch, "E987", {"points": [v(-379.5, -193.55) * mm, v(-379.7, -193.59) * mm, v(-379.87, -193.75) * mm, v(-379.9, -193.96) * mm]});
            skFitSpline(sketch, "E988", {"points": [v(-379.9, -193.96) * mm, v(-379.94, -194.16) * mm, v(-379.85, -194.37) * mm, v(-379.66, -194.48) * mm]});
            skFitSpline(sketch, "E989", {"points": [v(-379.41, -194.91) * mm, v(-379.41, -194.73) * mm, v(-379.5, -194.57) * mm, v(-379.66, -194.48) * mm]});
            skLineSegment(sketch, "E990", {"start": v(-358.71, -197.04) * mm, "end": v(-363.71, -197.04) * mm});
            skFitSpline(sketch, "E991", {"points": [v(-379.91, -197.04) * mm, v(-379.78, -197.04) * mm, v(-379.65, -197) * mm, v(-379.56, -196.9) * mm]});
            skFitSpline(sketch, "E992", {"points": [v(-379.56, -196.9) * mm, v(-379.47, -196.8) * mm, v(-379.41, -196.68) * mm, v(-379.41, -196.54) * mm]});
            skLineSegment(sketch, "E993", {"start": v(-364.21, -196.54) * mm, "end": v(-364.21, -194.91) * mm});
            skFitSpline(sketch, "E994", {"points": [v(-385.41, -196.54) * mm, v(-385.41, -196.82) * mm, v(-385.19, -197.04) * mm, v(-384.91, -197.04) * mm]});
            skLineSegment(sketch, "E995", {"start": v(-365.08, -194.04) * mm, "end": v(-370.21, -194.04) * mm});
            skLineSegment(sketch, "E996", {"start": v(-370.21, -194.04) * mm, "end": v(-370.21, -191.04) * mm});
            skLineSegment(sketch, "E997", {"start": v(-370.21, -191.04) * mm, "end": v(-368.94, -191.04) * mm});
            skLineSegment(sketch, "E998", {"start": v(-368.94, -191.04) * mm, "end": v(-368.94, -187.04) * mm});
            skLineSegment(sketch, "E999", {"start": v(-368.94, -187.04) * mm, "end": v(-370.21, -187.04) * mm});
            skLineSegment(sketch, "E1000", {"start": v(-370.21, -187.04) * mm, "end": v(-370.21, -184.04) * mm});
            skLineSegment(sketch, "E1001", {"start": v(-370.21, -184.04) * mm, "end": v(-373.41, -184.04) * mm});
            skLineSegment(sketch, "E1002", {"start": v(-373.41, -184.04) * mm, "end": v(-373.41, -187.04) * mm});
            skLineSegment(sketch, "E1003", {"start": v(-373.41, -187.04) * mm, "end": v(-374.69, -187.04) * mm});
            skLineSegment(sketch, "E1004", {"start": v(-374.69, -187.04) * mm, "end": v(-374.69, -191.04) * mm});
            skLineSegment(sketch, "E1005", {"start": v(-374.69, -191.04) * mm, "end": v(-373.41, -191.04) * mm});
            skLineSegment(sketch, "E1006", {"start": v(-373.41, -191.04) * mm, "end": v(-373.41, -194.04) * mm});
            skLineSegment(sketch, "E1007", {"start": v(-373.41, -194.04) * mm, "end": v(-378.55, -194.04) * mm});
            skFitSpline(sketch, "E1008", {"points": [v(-385.16, -194.48) * mm, v(-385.32, -194.57) * mm, v(-385.41, -194.73) * mm, v(-385.41, -194.91) * mm]});
            skFitSpline(sketch, "E1009", {"points": [v(-385.16, -194.48) * mm, v(-384.98, -194.37) * mm, v(-384.88, -194.16) * mm, v(-384.92, -193.96) * mm]});
            skFitSpline(sketch, "E1010", {"points": [v(-384.92, -193.96) * mm, v(-384.96, -193.75) * mm, v(-385.12, -193.59) * mm, v(-385.33, -193.55) * mm]});
            skFitSpline(sketch, "E1011", {"points": [v(-385.33, -193.55) * mm, v(-385.53, -193.52) * mm, v(-385.74, -193.61) * mm, v(-385.85, -193.8) * mm]});
            skFitSpline(sketch, "E1012", {"points": [v(-386.28, -194.04) * mm, v(-386.1, -194.04) * mm, v(-385.94, -193.95) * mm, v(-385.85, -193.8) * mm]});
            skLineSegment(sketch, "E1013", {"start": v(-379.41, -194.91) * mm, "end": v(-379.41, -196.54) * mm});
            skLineSegment(sketch, "E1014", {"start": v(-379.91, -197.04) * mm, "end": v(-384.91, -197.04) * mm});
            skFitSpline(sketch, "E1015", {"points": [v(-385.85, -64.3) * mm, v(-385.94, -64.14) * mm, v(-386.1, -64.05) * mm, v(-386.28, -64.05) * mm]});
            skFitSpline(sketch, "E1016", {"points": [v(-385.85, -64.3) * mm, v(-385.74, -64.48) * mm, v(-385.53, -64.57) * mm, v(-385.33, -64.54) * mm]});
            skFitSpline(sketch, "E1017", {"points": [v(-385.33, -64.54) * mm, v(-385.12, -64.5) * mm, v(-384.96, -64.34) * mm, v(-384.92, -64.13) * mm]});
            skFitSpline(sketch, "E1018", {"points": [v(-384.92, -64.13) * mm, v(-384.88, -63.93) * mm, v(-384.98, -63.72) * mm, v(-385.16, -63.61) * mm]});
            skFitSpline(sketch, "E1019", {"points": [v(-385.41, -63.18) * mm, v(-385.41, -63.36) * mm, v(-385.32, -63.52) * mm, v(-385.16, -63.61) * mm]});
            skLineSegment(sketch, "E1020", {"start": v(-385.41, -196.54) * mm, "end": v(-385.41, -194.91) * mm});
            skLineSegment(sketch, "E1021", {"start": v(-386.28, -194.04) * mm, "end": v(-396.81, -194.04) * mm});
            skFitSpline(sketch, "E1022", {"points": [v(-358.46, -63.61) * mm, v(-358.3, -63.52) * mm, v(-358.21, -63.36) * mm, v(-358.21, -63.18) * mm]});
            skFitSpline(sketch, "E1023", {"points": [v(-358.46, -63.61) * mm, v(-358.65, -63.72) * mm, v(-358.74, -63.93) * mm, v(-358.7, -64.13) * mm]});
            skFitSpline(sketch, "E1024", {"points": [v(-358.7, -64.13) * mm, v(-358.67, -64.34) * mm, v(-358.5, -64.5) * mm, v(-358.3, -64.54) * mm]});
            skFitSpline(sketch, "E1025", {"points": [v(-358.3, -64.54) * mm, v(-358.1, -64.57) * mm, v(-357.89, -64.48) * mm, v(-357.78, -64.3) * mm]});
            skFitSpline(sketch, "E1026", {"points": [v(-357.35, -64.05) * mm, v(-357.53, -64.05) * mm, v(-357.7, -64.14) * mm, v(-357.78, -64.3) * mm]});
            skLineSegment(sketch, "E1027", {"start": v(-396.81, -189.04) * mm, "end": v(-396.81, -168.04) * mm});
            skLineSegment(sketch, "E1028", {"start": v(-396.81, -168.04) * mm, "end": v(-394.81, -166.04) * mm});
            skLineSegment(sketch, "E1029", {"start": v(-394.81, -166.04) * mm, "end": v(-394.81, -64.05) * mm});
            skLineSegment(sketch, "E1030", {"start": v(-394.81, -64.05) * mm, "end": v(-386.28, -64.05) * mm});
            skFitSpline(sketch, "E1031", {"points": [v(-345.85, -64.3) * mm, v(-345.94, -64.14) * mm, v(-346.1, -64.05) * mm, v(-346.28, -64.05) * mm]});
            skFitSpline(sketch, "E1032", {"points": [v(-345.85, -64.3) * mm, v(-345.74, -64.48) * mm, v(-345.53, -64.57) * mm, v(-345.33, -64.54) * mm]});
            skFitSpline(sketch, "E1033", {"points": [v(-345.33, -64.54) * mm, v(-345.12, -64.5) * mm, v(-344.96, -64.34) * mm, v(-344.92, -64.13) * mm]});
            skFitSpline(sketch, "E1034", {"points": [v(-344.92, -64.13) * mm, v(-344.89, -63.93) * mm, v(-344.98, -63.72) * mm, v(-345.16, -63.61) * mm]});
            skFitSpline(sketch, "E1035", {"points": [v(-345.41, -63.18) * mm, v(-345.41, -63.36) * mm, v(-345.32, -63.52) * mm, v(-345.16, -63.61) * mm]});
            skFitSpline(sketch, "E1036", {"points": [v(-344.91, -61.05) * mm, v(-345.2, -61.05) * mm, v(-345.41, -61.27) * mm, v(-345.41, -61.55) * mm]});
            skLineSegment(sketch, "E1037", {"start": v(-385.41, -63.18) * mm, "end": v(-385.41, 188.45) * mm});
            skLineSegment(sketch, "E1038", {"start": v(-385.41, 188.45) * mm, "end": v(-385.41, 192.46) * mm});
            skFitSpline(sketch, "E1039", {"points": [v(-339.41, -61.55) * mm, v(-339.41, -61.27) * mm, v(-339.64, -61.05) * mm, v(-339.91, -61.05) * mm]});
            skLineSegment(sketch, "E1040", {"start": v(-357.35, -64.05) * mm, "end": v(-346.28, -64.05) * mm});
            skFitSpline(sketch, "E1041", {"points": [v(-339.66, -63.61) * mm, v(-339.5, -63.52) * mm, v(-339.41, -63.36) * mm, v(-339.41, -63.18) * mm]});
            skFitSpline(sketch, "E1042", {"points": [v(-339.66, -63.61) * mm, v(-339.85, -63.72) * mm, v(-339.94, -63.93) * mm, v(-339.9, -64.13) * mm]});
            skFitSpline(sketch, "E1043", {"points": [v(-339.9, -64.13) * mm, v(-339.87, -64.34) * mm, v(-339.7, -64.5) * mm, v(-339.5, -64.54) * mm]});
            skFitSpline(sketch, "E1044", {"points": [v(-339.5, -64.54) * mm, v(-339.3, -64.57) * mm, v(-339.09, -64.48) * mm, v(-338.98, -64.3) * mm]});
            skFitSpline(sketch, "E1045", {"points": [v(-338.55, -64.05) * mm, v(-338.73, -64.05) * mm, v(-338.9, -64.14) * mm, v(-338.98, -64.3) * mm]});
            skLineSegment(sketch, "E1046", {"start": v(-345.41, -63.18) * mm, "end": v(-345.41, -61.55) * mm});
            skFitSpline(sketch, "E1047", {"points": [v(-324.65, -64.3) * mm, v(-324.74, -64.14) * mm, v(-324.9, -64.05) * mm, v(-325.08, -64.05) * mm]});
            skFitSpline(sketch, "E1048", {"points": [v(-324.65, -64.3) * mm, v(-324.54, -64.48) * mm, v(-324.33, -64.57) * mm, v(-324.13, -64.54) * mm]});
            skFitSpline(sketch, "E1049", {"points": [v(-324.13, -64.54) * mm, v(-323.92, -64.5) * mm, v(-323.76, -64.34) * mm, v(-323.72, -64.13) * mm]});
            skFitSpline(sketch, "E1050", {"points": [v(-323.72, -64.13) * mm, v(-323.69, -63.93) * mm, v(-323.78, -63.72) * mm, v(-323.96, -63.61) * mm]});
            skFitSpline(sketch, "E1051", {"points": [v(-324.21, -63.18) * mm, v(-324.21, -63.36) * mm, v(-324.12, -63.52) * mm, v(-323.96, -63.61) * mm]});
            skLineSegment(sketch, "E1052", {"start": v(-344.91, -61.05) * mm, "end": v(-339.91, -61.05) * mm});
            skFitSpline(sketch, "E1053", {"points": [v(-323.71, -61.05) * mm, v(-324, -61.05) * mm, v(-324.21, -61.27) * mm, v(-324.21, -61.55) * mm]});
            skLineSegment(sketch, "E1054", {"start": v(-339.41, -61.55) * mm, "end": v(-339.41, -63.18) * mm});
            skFitSpline(sketch, "E1055", {"points": [v(-318.21, -61.55) * mm, v(-318.21, -61.27) * mm, v(-318.44, -61.05) * mm, v(-318.71, -61.05) * mm]});
            skLineSegment(sketch, "E1056", {"start": v(-338.55, -64.05) * mm, "end": v(-333.41, -64.05) * mm});
            skLineSegment(sketch, "E1057", {"start": v(-333.41, -64.05) * mm, "end": v(-333.41, -67.05) * mm});
            skLineSegment(sketch, "E1058", {"start": v(-333.41, -67.05) * mm, "end": v(-334.69, -67.05) * mm});
            skLineSegment(sketch, "E1059", {"start": v(-334.69, -67.05) * mm, "end": v(-334.69, -71.05) * mm});
            skLineSegment(sketch, "E1060", {"start": v(-334.69, -71.05) * mm, "end": v(-333.41, -71.05) * mm});
            skLineSegment(sketch, "E1061", {"start": v(-333.41, -71.05) * mm, "end": v(-333.41, -74.05) * mm});
            skLineSegment(sketch, "E1062", {"start": v(-333.41, -74.05) * mm, "end": v(-330.21, -74.05) * mm});
            skLineSegment(sketch, "E1063", {"start": v(-330.21, -74.05) * mm, "end": v(-330.21, -71.05) * mm});
            skLineSegment(sketch, "E1064", {"start": v(-330.21, -71.05) * mm, "end": v(-328.94, -71.05) * mm});
            skLineSegment(sketch, "E1065", {"start": v(-328.94, -71.05) * mm, "end": v(-328.94, -67.05) * mm});
            skLineSegment(sketch, "E1066", {"start": v(-328.94, -67.05) * mm, "end": v(-330.21, -67.05) * mm});
            skLineSegment(sketch, "E1067", {"start": v(-330.21, -67.05) * mm, "end": v(-330.21, -64.05) * mm});
            skLineSegment(sketch, "E1068", {"start": v(-330.21, -64.05) * mm, "end": v(-325.08, -64.05) * mm});
            skFitSpline(sketch, "E1069", {"points": [v(-318.46, -63.61) * mm, v(-318.3, -63.52) * mm, v(-318.21, -63.36) * mm, v(-318.21, -63.18) * mm]});
            skFitSpline(sketch, "E1070", {"points": [v(-318.46, -63.61) * mm, v(-318.65, -63.72) * mm, v(-318.74, -63.93) * mm, v(-318.7, -64.13) * mm]});
            skFitSpline(sketch, "E1071", {"points": [v(-318.7, -64.13) * mm, v(-318.67, -64.34) * mm, v(-318.5, -64.5) * mm, v(-318.3, -64.54) * mm]});
            skFitSpline(sketch, "E1072", {"points": [v(-318.3, -64.54) * mm, v(-318.1, -64.57) * mm, v(-317.89, -64.48) * mm, v(-317.78, -64.3) * mm]});
            skFitSpline(sketch, "E1073", {"points": [v(-317.35, -64.05) * mm, v(-317.53, -64.05) * mm, v(-317.7, -64.14) * mm, v(-317.78, -64.3) * mm]});
            skLineSegment(sketch, "E1074", {"start": v(-324.21, -63.18) * mm, "end": v(-324.21, -61.55) * mm});
            skFitSpline(sketch, "E1075", {"points": [v(-225.85, -64.3) * mm, v(-225.94, -64.14) * mm, v(-226.1, -64.05) * mm, v(-226.28, -64.05) * mm]});
            skFitSpline(sketch, "E1076", {"points": [v(-225.85, -64.3) * mm, v(-225.74, -64.48) * mm, v(-225.54, -64.57) * mm, v(-225.33, -64.54) * mm]});
            skFitSpline(sketch, "E1077", {"points": [v(-225.33, -64.54) * mm, v(-225.12, -64.5) * mm, v(-224.96, -64.34) * mm, v(-224.92, -64.13) * mm]});
            skFitSpline(sketch, "E1078", {"points": [v(-224.92, -64.13) * mm, v(-224.89, -63.93) * mm, v(-224.98, -63.72) * mm, v(-225.17, -63.61) * mm]});
            skFitSpline(sketch, "E1079", {"points": [v(-225.42, -63.18) * mm, v(-225.42, -63.36) * mm, v(-225.32, -63.52) * mm, v(-225.17, -63.61) * mm]});
            skLineSegment(sketch, "E1080", {"start": v(-323.71, -61.05) * mm, "end": v(-318.71, -61.05) * mm});
            skFitSpline(sketch, "E1081", {"points": [v(-224.92, -61.05) * mm, v(-225.2, -61.05) * mm, v(-225.42, -61.27) * mm, v(-225.42, -61.55) * mm]});
            skLineSegment(sketch, "E1082", {"start": v(-318.21, -61.55) * mm, "end": v(-318.21, -63.18) * mm});
            skFitSpline(sketch, "E1083", {"points": [v(-219.42, -61.55) * mm, v(-219.42, -61.27) * mm, v(-219.64, -61.05) * mm, v(-219.92, -61.05) * mm]});
            skLineSegment(sketch, "E1084", {"start": v(-317.35, -64.05) * mm, "end": v(-226.28, -64.05) * mm});
            skFitSpline(sketch, "E1085", {"points": [v(-219.67, -63.61) * mm, v(-219.51, -63.52) * mm, v(-219.42, -63.36) * mm, v(-219.42, -63.18) * mm]});
            skFitSpline(sketch, "E1086", {"points": [v(-219.67, -63.61) * mm, v(-219.85, -63.72) * mm, v(-219.94, -63.93) * mm, v(-219.9, -64.13) * mm]});
            skFitSpline(sketch, "E1087", {"points": [v(-219.9, -64.13) * mm, v(-219.87, -64.34) * mm, v(-219.7, -64.5) * mm, v(-219.5, -64.54) * mm]});
            skFitSpline(sketch, "E1088", {"points": [v(-219.5, -64.54) * mm, v(-219.3, -64.57) * mm, v(-219.09, -64.48) * mm, v(-218.98, -64.3) * mm]});
            skFitSpline(sketch, "E1089", {"points": [v(-218.55, -64.05) * mm, v(-218.73, -64.05) * mm, v(-218.9, -64.14) * mm, v(-218.98, -64.3) * mm]});
            skLineSegment(sketch, "E1090", {"start": v(-225.42, -63.18) * mm, "end": v(-225.42, -61.55) * mm});
            skFitSpline(sketch, "E1091", {"points": [v(-204.65, -64.3) * mm, v(-204.74, -64.14) * mm, v(-204.9, -64.05) * mm, v(-205.08, -64.05) * mm]});
            skFitSpline(sketch, "E1092", {"points": [v(-204.65, -64.3) * mm, v(-204.54, -64.48) * mm, v(-204.34, -64.57) * mm, v(-204.13, -64.54) * mm]});
            skFitSpline(sketch, "E1093", {"points": [v(-204.13, -64.54) * mm, v(-203.92, -64.5) * mm, v(-203.76, -64.34) * mm, v(-203.72, -64.13) * mm]});
            skFitSpline(sketch, "E1094", {"points": [v(-203.72, -64.13) * mm, v(-203.69, -63.93) * mm, v(-203.78, -63.72) * mm, v(-203.97, -63.61) * mm]});
            skFitSpline(sketch, "E1095", {"points": [v(-204.22, -63.18) * mm, v(-204.22, -63.36) * mm, v(-204.12, -63.52) * mm, v(-203.97, -63.61) * mm]});
            skLineSegment(sketch, "E1096", {"start": v(-224.92, -61.05) * mm, "end": v(-219.92, -61.05) * mm});
            skFitSpline(sketch, "E1097", {"points": [v(-203.72, -61.05) * mm, v(-204, -61.05) * mm, v(-204.22, -61.27) * mm, v(-204.22, -61.55) * mm]});
            skLineSegment(sketch, "E1098", {"start": v(-219.42, -61.55) * mm, "end": v(-219.42, -63.18) * mm});
            skFitSpline(sketch, "E1099", {"points": [v(-198.22, -61.55) * mm, v(-198.22, -61.41) * mm, v(-198.27, -61.29) * mm, v(-198.36, -61.2) * mm]});
            skFitSpline(sketch, "E1100", {"points": [v(-198.36, -61.2) * mm, v(-198.46, -61.1) * mm, v(-198.58, -61.05) * mm, v(-198.72, -61.05) * mm]});
            skLineSegment(sketch, "E1101", {"start": v(-218.55, -64.05) * mm, "end": v(-213.42, -64.05) * mm});
            skLineSegment(sketch, "E1102", {"start": v(-213.42, -64.05) * mm, "end": v(-213.42, -67.05) * mm});
            skLineSegment(sketch, "E1103", {"start": v(-213.42, -67.05) * mm, "end": v(-214.7, -67.05) * mm});
            skLineSegment(sketch, "E1104", {"start": v(-214.7, -67.05) * mm, "end": v(-214.7, -71.05) * mm});
            skLineSegment(sketch, "E1105", {"start": v(-214.7, -71.05) * mm, "end": v(-213.42, -71.05) * mm});
            skLineSegment(sketch, "E1106", {"start": v(-213.42, -71.05) * mm, "end": v(-213.42, -74.05) * mm});
            skLineSegment(sketch, "E1107", {"start": v(-213.42, -74.05) * mm, "end": v(-210.22, -74.05) * mm});
            skLineSegment(sketch, "E1108", {"start": v(-210.22, -74.05) * mm, "end": v(-210.22, -71.05) * mm});
            skLineSegment(sketch, "E1109", {"start": v(-210.22, -71.05) * mm, "end": v(-208.94, -71.05) * mm});
            skLineSegment(sketch, "E1110", {"start": v(-208.94, -71.05) * mm, "end": v(-208.94, -67.05) * mm});
            skLineSegment(sketch, "E1111", {"start": v(-208.94, -67.05) * mm, "end": v(-210.22, -67.05) * mm});
            skLineSegment(sketch, "E1112", {"start": v(-210.22, -67.05) * mm, "end": v(-210.22, -64.05) * mm});
            skLineSegment(sketch, "E1113", {"start": v(-210.22, -64.05) * mm, "end": v(-205.08, -64.05) * mm});
            skFitSpline(sketch, "E1114", {"points": [v(-198.47, -63.61) * mm, v(-198.31, -63.52) * mm, v(-198.22, -63.36) * mm, v(-198.22, -63.18) * mm]});
            skFitSpline(sketch, "E1115", {"points": [v(-198.47, -63.61) * mm, v(-198.65, -63.72) * mm, v(-198.74, -63.93) * mm, v(-198.7, -64.13) * mm]});
            skFitSpline(sketch, "E1116", {"points": [v(-198.7, -64.13) * mm, v(-198.67, -64.34) * mm, v(-198.5, -64.5) * mm, v(-198.3, -64.54) * mm]});
            skFitSpline(sketch, "E1117", {"points": [v(-198.3, -64.54) * mm, v(-198.1, -64.57) * mm, v(-197.89, -64.48) * mm, v(-197.78, -64.3) * mm]});
            skFitSpline(sketch, "E1118", {"points": [v(-197.35, -64.05) * mm, v(-197.53, -64.05) * mm, v(-197.7, -64.14) * mm, v(-197.78, -64.3) * mm]});
            skLineSegment(sketch, "E1119", {"start": v(-204.22, -63.18) * mm, "end": v(-204.22, -61.55) * mm});
            skFitSpline(sketch, "E1120", {"points": [v(-65.85, -64.3) * mm, v(-65.94, -64.14) * mm, v(-66.1, -64.05) * mm, v(-66.28, -64.05) * mm]});
            skFitSpline(sketch, "E1121", {"points": [v(-65.85, -64.3) * mm, v(-65.74, -64.48) * mm, v(-65.54, -64.57) * mm, v(-65.33, -64.54) * mm]});
            skFitSpline(sketch, "E1122", {"points": [v(-65.33, -64.54) * mm, v(-65.12, -64.5) * mm, v(-64.96, -64.34) * mm, v(-64.92, -64.13) * mm]});
            skFitSpline(sketch, "E1123", {"points": [v(-64.92, -64.13) * mm, v(-64.89, -63.93) * mm, v(-64.98, -63.72) * mm, v(-65.17, -63.61) * mm]});
            skFitSpline(sketch, "E1124", {"points": [v(-65.42, -63.18) * mm, v(-65.42, -63.36) * mm, v(-65.32, -63.52) * mm, v(-65.17, -63.61) * mm]});
            skLineSegment(sketch, "E1125", {"start": v(-203.72, -61.05) * mm, "end": v(-198.72, -61.05) * mm});
            skFitSpline(sketch, "E1126", {"points": [v(-64.92, -61.05) * mm, v(-65.05, -61.05) * mm, v(-65.18, -61.1) * mm, v(-65.27, -61.2) * mm]});
            skFitSpline(sketch, "E1127", {"points": [v(-65.27, -61.2) * mm, v(-65.36, -61.29) * mm, v(-65.42, -61.41) * mm, v(-65.42, -61.55) * mm]});
            skLineSegment(sketch, "E1128", {"start": v(-198.22, -61.55) * mm, "end": v(-198.22, -63.18) * mm});
            skFitSpline(sketch, "E1129", {"points": [v(-59.42, -61.55) * mm, v(-59.42, -61.27) * mm, v(-59.64, -61.05) * mm, v(-59.92, -61.05) * mm]});
            skLineSegment(sketch, "E1130", {"start": v(-197.35, -64.05) * mm, "end": v(-66.28, -64.05) * mm});
            skFitSpline(sketch, "E1131", {"points": [v(-59.67, -63.61) * mm, v(-59.51, -63.52) * mm, v(-59.42, -63.36) * mm, v(-59.42, -63.18) * mm]});
            skFitSpline(sketch, "E1132", {"points": [v(-59.67, -63.61) * mm, v(-59.85, -63.72) * mm, v(-59.95, -63.93) * mm, v(-59.9, -64.13) * mm]});
            skFitSpline(sketch, "E1133", {"points": [v(-59.9, -64.13) * mm, v(-59.87, -64.34) * mm, v(-59.71, -64.5) * mm, v(-59.5, -64.54) * mm]});
            skFitSpline(sketch, "E1134", {"points": [v(-59.5, -64.54) * mm, v(-59.3, -64.57) * mm, v(-59.09, -64.48) * mm, v(-58.98, -64.3) * mm]});
            skFitSpline(sketch, "E1135", {"points": [v(-58.55, -64.05) * mm, v(-58.73, -64.05) * mm, v(-58.9, -64.14) * mm, v(-58.98, -64.3) * mm]});
            skLineSegment(sketch, "E1136", {"start": v(-65.42, -63.18) * mm, "end": v(-65.42, -61.55) * mm});
            skFitSpline(sketch, "E1137", {"points": [v(-44.65, -64.3) * mm, v(-44.74, -64.14) * mm, v(-44.9, -64.05) * mm, v(-45.08, -64.05) * mm]});
            skFitSpline(sketch, "E1138", {"points": [v(-44.65, -64.3) * mm, v(-44.54, -64.48) * mm, v(-44.34, -64.57) * mm, v(-44.13, -64.54) * mm]});
            skFitSpline(sketch, "E1139", {"points": [v(-44.13, -64.54) * mm, v(-43.92, -64.5) * mm, v(-43.76, -64.34) * mm, v(-43.72, -64.13) * mm]});
            skFitSpline(sketch, "E1140", {"points": [v(-43.72, -64.13) * mm, v(-43.69, -63.93) * mm, v(-43.78, -63.72) * mm, v(-43.97, -63.61) * mm]});
            skFitSpline(sketch, "E1141", {"points": [v(-44.22, -63.18) * mm, v(-44.22, -63.36) * mm, v(-44.12, -63.52) * mm, v(-43.97, -63.61) * mm]});
            skLineSegment(sketch, "E1142", {"start": v(-64.92, -61.05) * mm, "end": v(-59.92, -61.05) * mm});
            skFitSpline(sketch, "E1143", {"points": [v(-43.72, -61.05) * mm, v(-44, -61.05) * mm, v(-44.22, -61.27) * mm, v(-44.22, -61.55) * mm]});
            skLineSegment(sketch, "E1144", {"start": v(-59.42, -61.55) * mm, "end": v(-59.42, -63.18) * mm});
            skFitSpline(sketch, "E1145", {"points": [v(-38.22, -61.55) * mm, v(-38.22, -61.27) * mm, v(-38.44, -61.05) * mm, v(-38.72, -61.05) * mm]});
            skLineSegment(sketch, "E1146", {"start": v(-58.55, -64.05) * mm, "end": v(-53.42, -64.05) * mm});
            skLineSegment(sketch, "E1147", {"start": v(-53.42, -64.05) * mm, "end": v(-53.42, -67.05) * mm});
            skLineSegment(sketch, "E1148", {"start": v(-53.42, -67.05) * mm, "end": v(-54.7, -67.05) * mm});
            skLineSegment(sketch, "E1149", {"start": v(-54.7, -67.05) * mm, "end": v(-54.7, -71.05) * mm});
            skLineSegment(sketch, "E1150", {"start": v(-54.7, -71.05) * mm, "end": v(-53.42, -71.05) * mm});
            skLineSegment(sketch, "E1151", {"start": v(-53.42, -71.05) * mm, "end": v(-53.42, -74.05) * mm});
            skLineSegment(sketch, "E1152", {"start": v(-53.42, -74.05) * mm, "end": v(-50.22, -74.05) * mm});
            skLineSegment(sketch, "E1153", {"start": v(-50.22, -74.05) * mm, "end": v(-50.22, -71.05) * mm});
            skLineSegment(sketch, "E1154", {"start": v(-50.22, -71.05) * mm, "end": v(-48.94, -71.05) * mm});
            skLineSegment(sketch, "E1155", {"start": v(-48.94, -71.05) * mm, "end": v(-48.94, -67.05) * mm});
            skLineSegment(sketch, "E1156", {"start": v(-48.94, -67.05) * mm, "end": v(-50.22, -67.05) * mm});
            skLineSegment(sketch, "E1157", {"start": v(-50.22, -67.05) * mm, "end": v(-50.22, -64.05) * mm});
            skLineSegment(sketch, "E1158", {"start": v(-50.22, -64.05) * mm, "end": v(-45.08, -64.05) * mm});
            skFitSpline(sketch, "E1159", {"points": [v(-38.47, -63.61) * mm, v(-38.31, -63.52) * mm, v(-38.22, -63.36) * mm, v(-38.22, -63.18) * mm]});
            skFitSpline(sketch, "E1160", {"points": [v(-38.47, -63.61) * mm, v(-38.65, -63.72) * mm, v(-38.75, -63.93) * mm, v(-38.7, -64.13) * mm]});
            skFitSpline(sketch, "E1161", {"points": [v(-38.7, -64.13) * mm, v(-38.67, -64.34) * mm, v(-38.51, -64.5) * mm, v(-38.3, -64.54) * mm]});
            skFitSpline(sketch, "E1162", {"points": [v(-38.3, -64.54) * mm, v(-38.1, -64.57) * mm, v(-37.89, -64.48) * mm, v(-37.78, -64.3) * mm]});
            skFitSpline(sketch, "E1163", {"points": [v(-37.35, -64.05) * mm, v(-37.53, -64.05) * mm, v(-37.7, -64.14) * mm, v(-37.78, -64.3) * mm]});
            skLineSegment(sketch, "E1164", {"start": v(-44.22, -63.18) * mm, "end": v(-44.22, -61.55) * mm});
            skFitSpline(sketch, "E1165", {"points": [v(-29.48, -74.45) * mm, v(-29.4, -74.6) * mm, v(-29.23, -74.7) * mm, v(-29.05, -74.7) * mm]});
            skFitSpline(sketch, "E1166", {"points": [v(-29.48, -74.45) * mm, v(-29.59, -74.26) * mm, v(-29.8, -74.17) * mm, v(-30, -74.2) * mm]});
            skFitSpline(sketch, "E1167", {"points": [v(-30, -74.2) * mm, v(-30.21, -74.24) * mm, v(-30.37, -74.4) * mm, v(-30.4, -74.6) * mm]});
            skFitSpline(sketch, "E1168", {"points": [v(-30.4, -74.6) * mm, v(-30.45, -74.82) * mm, v(-30.35, -75.02) * mm, v(-30.17, -75.13) * mm]});
            skFitSpline(sketch, "E1169", {"points": [v(-29.92, -75.56) * mm, v(-29.92, -75.38) * mm, v(-30.01, -75.22) * mm, v(-30.17, -75.13) * mm]});
            skLineSegment(sketch, "E1170", {"start": v(-43.72, -61.05) * mm, "end": v(-38.72, -61.05) * mm});
            skLineSegment(sketch, "E1171", {"start": v(-38.22, -61.55) * mm, "end": v(-38.22, -63.18) * mm});
            skLineSegment(sketch, "E1172", {"start": v(-37.35, -64.05) * mm, "end": v(-26.82, -64.05) * mm});
            skLineSegment(sketch, "E1173", {"start": v(-26.82, -64.05) * mm, "end": v(-26.82, -74.7) * mm});
            skLineSegment(sketch, "E1174", {"start": v(-26.82, -74.7) * mm, "end": v(-29.05, -74.7) * mm});
            skFitSpline(sketch, "E1175", {"points": [v(-55.82, -88.05) * mm, v(-53.6, -88.05) * mm, v(-51.82, -86.25) * mm, v(-51.82, -84.05) * mm]});
            skFitSpline(sketch, "E1176", {"points": [v(-51.82, -84.05) * mm, v(-51.82, -81.84) * mm, v(-53.6, -80.05) * mm, v(-55.82, -80.05) * mm]});
            skLineSegment(sketch, "E1177", {"start": v(-29.92, -75.56) * mm, "end": v(-29.92, -83.1) * mm});
            skLineSegment(sketch, "E1178", {"start": v(-29.92, -83.1) * mm, "end": v(-32.92, -83.1) * mm});
            skLineSegment(sketch, "E1179", {"start": v(-32.92, -83.1) * mm, "end": v(-32.92, -81.82) * mm});
            skLineSegment(sketch, "E1180", {"start": v(-32.92, -81.82) * mm, "end": v(-36.92, -81.82) * mm});
            skLineSegment(sketch, "E1181", {"start": v(-36.92, -81.82) * mm, "end": v(-36.92, -83.1) * mm});
            skLineSegment(sketch, "E1182", {"start": v(-36.92, -83.1) * mm, "end": v(-39.92, -83.1) * mm});
            skLineSegment(sketch, "E1183", {"start": v(-39.92, -83.1) * mm, "end": v(-39.92, -86.3) * mm});
            skLineSegment(sketch, "E1184", {"start": v(-39.92, -86.3) * mm, "end": v(-36.92, -86.3) * mm});
            skLineSegment(sketch, "E1185", {"start": v(-36.92, -86.3) * mm, "end": v(-36.92, -87.57) * mm});
            skLineSegment(sketch, "E1186", {"start": v(-36.92, -87.57) * mm, "end": v(-32.92, -87.57) * mm});
            skLineSegment(sketch, "E1187", {"start": v(-32.92, -87.57) * mm, "end": v(-32.92, -86.3) * mm});
            skLineSegment(sketch, "E1188", {"start": v(-32.92, -86.3) * mm, "end": v(-29.92, -86.3) * mm});
            skLineSegment(sketch, "E1189", {"start": v(-29.92, -86.3) * mm, "end": v(-29.92, -95.04) * mm});
            skLineSegment(sketch, "E1190", {"start": v(-29.92, -95.04) * mm, "end": v(-352, -188.94) * mm});
            skFitSpline(sketch, "E1191", {"points": [v(-63.82, -80.05) * mm, v(-66.03, -80.05) * mm, v(-67.82, -81.84) * mm, v(-67.82, -84.05) * mm]});
            skFitSpline(sketch, "E1192", {"points": [v(-67.82, -84.05) * mm, v(-67.82, -86.25) * mm, v(-66.03, -88.05) * mm, v(-63.82, -88.05) * mm]});
            skLineSegment(sketch, "E1193", {"start": v(-352.36, -194.04) * mm, "end": v(-357.35, -194.04) * mm});
            skFitSpline(sketch, "E1194", {"points": [v(-115.82, -88.05) * mm, v(-113.6, -88.05) * mm, v(-111.82, -86.25) * mm, v(-111.82, -84.05) * mm]});
            skFitSpline(sketch, "E1195", {"points": [v(-111.82, -84.05) * mm, v(-111.82, -81.84) * mm, v(-113.6, -80.05) * mm, v(-115.82, -80.05) * mm]});
            skLineSegment(sketch, "E1196", {"start": v(-63.82, -88.05) * mm, "end": v(-55.82, -88.05) * mm});
            skFitSpline(sketch, "E1197", {"points": [v(-123.82, -80.05) * mm, v(-126.03, -80.05) * mm, v(-127.82, -81.84) * mm, v(-127.82, -84.05) * mm]});
            skFitSpline(sketch, "E1198", {"points": [v(-127.82, -84.05) * mm, v(-127.82, -86.25) * mm, v(-126.03, -88.05) * mm, v(-123.82, -88.05) * mm]});
            skLineSegment(sketch, "E1199", {"start": v(-55.82, -80.05) * mm, "end": v(-63.82, -80.05) * mm});
            skFitSpline(sketch, "E1200", {"points": [v(-175.82, -88.05) * mm, v(-173.6, -88.05) * mm, v(-171.82, -86.25) * mm, v(-171.82, -84.05) * mm]});
            skFitSpline(sketch, "E1201", {"points": [v(-171.82, -84.05) * mm, v(-171.82, -81.84) * mm, v(-173.6, -80.05) * mm, v(-175.82, -80.05) * mm]});
            skLineSegment(sketch, "E1202", {"start": v(-123.82, -88.05) * mm, "end": v(-115.82, -88.05) * mm});
            skFitSpline(sketch, "E1203", {"points": [v(-183.82, -80.05) * mm, v(-186.02, -80.05) * mm, v(-187.82, -81.84) * mm, v(-187.82, -84.05) * mm]});
            skFitSpline(sketch, "E1204", {"points": [v(-187.82, -84.05) * mm, v(-187.82, -86.25) * mm, v(-186.02, -88.05) * mm, v(-183.82, -88.05) * mm]});
            skLineSegment(sketch, "E1205", {"start": v(-115.82, -80.05) * mm, "end": v(-123.82, -80.05) * mm});
            skFitSpline(sketch, "E1206", {"points": [v(-235.82, -88.05) * mm, v(-233.6, -88.05) * mm, v(-231.82, -86.25) * mm, v(-231.82, -84.05) * mm]});
            skFitSpline(sketch, "E1207", {"points": [v(-231.82, -84.05) * mm, v(-231.82, -81.84) * mm, v(-233.6, -80.05) * mm, v(-235.82, -80.05) * mm]});
            skLineSegment(sketch, "E1208", {"start": v(-183.82, -88.05) * mm, "end": v(-175.82, -88.05) * mm});
            skFitSpline(sketch, "E1209", {"points": [v(-243.82, -80.05) * mm, v(-246.02, -80.05) * mm, v(-247.81, -81.84) * mm, v(-247.81, -84.05) * mm]});
            skFitSpline(sketch, "E1210", {"points": [v(-247.81, -84.05) * mm, v(-247.81, -86.25) * mm, v(-246.02, -88.05) * mm, v(-243.82, -88.05) * mm]});
            skLineSegment(sketch, "E1211", {"start": v(-175.82, -80.05) * mm, "end": v(-183.82, -80.05) * mm});
            skFitSpline(sketch, "E1212", {"points": [v(-303.81, -87.05) * mm, v(-303.81, -89.25) * mm, v(-302.02, -91.04) * mm, v(-299.81, -91.04) * mm]});
            skFitSpline(sketch, "E1213", {"points": [v(-299.81, -91.04) * mm, v(-297.6, -91.04) * mm, v(-295.82, -89.25) * mm, v(-295.81, -87.05) * mm]});
            skLineSegment(sketch, "E1214", {"start": v(-243.82, -88.05) * mm, "end": v(-235.82, -88.05) * mm});
            skFitSpline(sketch, "E1215", {"points": [v(-295.81, -79.05) * mm, v(-295.82, -76.84) * mm, v(-297.6, -75.05) * mm, v(-299.81, -75.05) * mm]});
            skFitSpline(sketch, "E1216", {"points": [v(-299.81, -75.05) * mm, v(-302.02, -75.05) * mm, v(-303.81, -76.84) * mm, v(-303.81, -79.05) * mm]});
            skLineSegment(sketch, "E1217", {"start": v(-235.82, -80.05) * mm, "end": v(-243.82, -80.05) * mm});
            skFitSpline(sketch, "E1218", {"points": [v(-303.81, -127.05) * mm, v(-303.81, -129.25) * mm, v(-302.02, -131.04) * mm, v(-299.81, -131.04) * mm]});
            skFitSpline(sketch, "E1219", {"points": [v(-299.81, -131.04) * mm, v(-297.6, -131.04) * mm, v(-295.82, -129.25) * mm, v(-295.81, -127.05) * mm]});
            skLineSegment(sketch, "E1220", {"start": v(-303.81, -79.05) * mm, "end": v(-303.81, -87.05) * mm});
            skFitSpline(sketch, "E1221", {"points": [v(-295.81, -119.05) * mm, v(-295.82, -116.84) * mm, v(-297.6, -115.05) * mm, v(-299.81, -115.05) * mm]});
            skFitSpline(sketch, "E1222", {"points": [v(-299.81, -115.05) * mm, v(-302.02, -115.05) * mm, v(-303.81, -116.84) * mm, v(-303.81, -119.05) * mm]});
            skLineSegment(sketch, "E1223", {"start": v(-295.81, -87.05) * mm, "end": v(-295.81, -79.05) * mm});
            skFitSpline(sketch, "E1224", {"points": [v(-388.81, -87.05) * mm, v(-388.81, -88.47) * mm, v(-388.05, -89.8) * mm, v(-386.81, -90.5) * mm]});
            skFitSpline(sketch, "E1225", {"points": [v(-386.81, -90.5) * mm, v(-385.58, -91.22) * mm, v(-384.05, -91.22) * mm, v(-382.81, -90.5) * mm]});
            skFitSpline(sketch, "E1226", {"points": [v(-382.81, -90.5) * mm, v(-381.58, -89.8) * mm, v(-380.81, -88.47) * mm, v(-380.81, -87.05) * mm]});
            skLineSegment(sketch, "E1227", {"start": v(-303.81, -119.05) * mm, "end": v(-303.81, -127.05) * mm});
            skFitSpline(sketch, "E1228", {"points": [v(-380.81, -79.05) * mm, v(-380.81, -77.62) * mm, v(-381.58, -76.3) * mm, v(-382.81, -75.58) * mm]});
            skFitSpline(sketch, "E1229", {"points": [v(-382.81, -75.58) * mm, v(-384.05, -74.87) * mm, v(-385.58, -74.87) * mm, v(-386.81, -75.58) * mm]});
            skFitSpline(sketch, "E1230", {"points": [v(-386.81, -75.58) * mm, v(-388.05, -76.3) * mm, v(-388.81, -77.62) * mm, v(-388.81, -79.05) * mm]});
            skLineSegment(sketch, "E1231", {"start": v(-295.81, -127.05) * mm, "end": v(-295.81, -119.05) * mm});
            skFitSpline(sketch, "E1232", {"points": [v(-388.81, -127.05) * mm, v(-388.81, -128.47) * mm, v(-388.05, -129.8) * mm, v(-386.81, -130.5) * mm]});
            skFitSpline(sketch, "E1233", {"points": [v(-386.81, -130.5) * mm, v(-385.58, -131.22) * mm, v(-384.05, -131.22) * mm, v(-382.81, -130.5) * mm]});
            skFitSpline(sketch, "E1234", {"points": [v(-382.81, -130.5) * mm, v(-381.58, -129.8) * mm, v(-380.81, -128.47) * mm, v(-380.81, -127.05) * mm]});
            skLineSegment(sketch, "E1235", {"start": v(-388.81, -79.05) * mm, "end": v(-388.81, -87.05) * mm});
            skFitSpline(sketch, "E1236", {"points": [v(-380.81, -119.05) * mm, v(-380.81, -117.62) * mm, v(-381.58, -116.3) * mm, v(-382.81, -115.58) * mm]});
            skFitSpline(sketch, "E1237", {"points": [v(-382.81, -115.58) * mm, v(-384.05, -114.87) * mm, v(-385.58, -114.87) * mm, v(-386.81, -115.58) * mm]});
            skFitSpline(sketch, "E1238", {"points": [v(-386.81, -115.58) * mm, v(-388.05, -116.3) * mm, v(-388.81, -117.62) * mm, v(-388.81, -119.05) * mm]});
            skLineSegment(sketch, "E1239", {"start": v(-380.81, -87.05) * mm, "end": v(-380.81, -79.05) * mm});
            skFitSpline(sketch, "E1240", {"points": [v(-388.81, -167.04) * mm, v(-388.81, -168.47) * mm, v(-388.05, -169.8) * mm, v(-386.81, -170.5) * mm]});
            skFitSpline(sketch, "E1241", {"points": [v(-386.81, -170.5) * mm, v(-385.58, -171.22) * mm, v(-384.05, -171.22) * mm, v(-382.81, -170.5) * mm]});
            skFitSpline(sketch, "E1242", {"points": [v(-382.81, -170.5) * mm, v(-381.58, -169.8) * mm, v(-380.81, -168.47) * mm, v(-380.81, -167.04) * mm]});
            skLineSegment(sketch, "E1243", {"start": v(-388.81, -119.05) * mm, "end": v(-388.81, -127.05) * mm});
            skFitSpline(sketch, "E1244", {"points": [v(-380.81, -159.04) * mm, v(-380.81, -157.62) * mm, v(-381.58, -156.3) * mm, v(-382.81, -155.58) * mm]});
            skFitSpline(sketch, "E1245", {"points": [v(-382.81, -155.58) * mm, v(-384.05, -154.87) * mm, v(-385.58, -154.87) * mm, v(-386.81, -155.58) * mm]});
            skFitSpline(sketch, "E1246", {"points": [v(-386.81, -155.58) * mm, v(-388.05, -156.3) * mm, v(-388.81, -157.62) * mm, v(-388.81, -159.04) * mm]});
            skFitSpline(sketch, "E1247", {"points": [v(-318.48, -76.85) * mm, v(-318.48, -76.38) * mm, v(-318.73, -75.95) * mm, v(-319.13, -75.72) * mm]});
            skFitSpline(sketch, "E1248", {"points": [v(-319.13, -75.72) * mm, v(-319.53, -75.49) * mm, v(-320.03, -75.49) * mm, v(-320.43, -75.72) * mm]});
            skFitSpline(sketch, "E1249", {"points": [v(-320.43, -75.72) * mm, v(-320.83, -75.95) * mm, v(-321.08, -76.38) * mm, v(-321.08, -76.85) * mm]});
            skFitSpline(sketch, "E1250", {"points": [v(-321.08, -76.85) * mm, v(-321.08, -77.31) * mm, v(-320.83, -77.74) * mm, v(-320.43, -77.97) * mm]});
            skFitSpline(sketch, "E1251", {"points": [v(-320.43, -77.97) * mm, v(-320.03, -78.2) * mm, v(-319.53, -78.2) * mm, v(-319.13, -77.97) * mm]});
            skFitSpline(sketch, "E1252", {"points": [v(-319.13, -77.97) * mm, v(-318.73, -77.74) * mm, v(-318.48, -77.31) * mm, v(-318.48, -76.85) * mm]});
            skLineSegment(sketch, "E1253", {"start": v(-380.81, -127.05) * mm, "end": v(-380.81, -119.05) * mm});
            skFitSpline(sketch, "E1254", {"points": [v(-318.5, -160.04) * mm, v(-318.5, -159.58) * mm, v(-318.75, -159.15) * mm, v(-319.15, -158.92) * mm]});
            skFitSpline(sketch, "E1255", {"points": [v(-319.15, -158.92) * mm, v(-319.55, -158.69) * mm, v(-320.05, -158.69) * mm, v(-320.45, -158.92) * mm]});
            skFitSpline(sketch, "E1256", {"points": [v(-320.45, -158.92) * mm, v(-320.85, -159.15) * mm, v(-321.1, -159.58) * mm, v(-321.1, -160.04) * mm]});
            skFitSpline(sketch, "E1257", {"points": [v(-321.1, -160.04) * mm, v(-321.1, -160.5) * mm, v(-320.85, -160.94) * mm, v(-320.45, -161.17) * mm]});
            skFitSpline(sketch, "E1258", {"points": [v(-320.45, -161.17) * mm, v(-320.05, -161.4) * mm, v(-319.55, -161.4) * mm, v(-319.15, -161.17) * mm]});
            skFitSpline(sketch, "E1259", {"points": [v(-319.15, -161.17) * mm, v(-318.75, -160.94) * mm, v(-318.5, -160.5) * mm, v(-318.5, -160.04) * mm]});
            skLineSegment(sketch, "E1260", {"start": v(-388.81, -159.04) * mm, "end": v(-388.81, -167.04) * mm});
            skFitSpline(sketch, "E1261", {"points": [v(-366.68, -83.05) * mm, v(-366.68, -82.58) * mm, v(-366.92, -82.15) * mm, v(-367.33, -81.92) * mm]});
            skFitSpline(sketch, "E1262", {"points": [v(-367.33, -81.92) * mm, v(-367.73, -81.69) * mm, v(-368.22, -81.69) * mm, v(-368.63, -81.92) * mm]});
            skFitSpline(sketch, "E1263", {"points": [v(-368.63, -81.92) * mm, v(-369.03, -82.15) * mm, v(-369.28, -82.58) * mm, v(-369.28, -83.05) * mm]});
            skFitSpline(sketch, "E1264", {"points": [v(-369.28, -83.05) * mm, v(-369.28, -83.51) * mm, v(-369.03, -83.94) * mm, v(-368.63, -84.17) * mm]});
            skFitSpline(sketch, "E1265", {"points": [v(-368.63, -84.17) * mm, v(-368.22, -84.4) * mm, v(-367.73, -84.4) * mm, v(-367.33, -84.17) * mm]});
            skFitSpline(sketch, "E1266", {"points": [v(-367.33, -84.17) * mm, v(-366.92, -83.94) * mm, v(-366.68, -83.51) * mm, v(-366.68, -83.05) * mm]});
            skLineSegment(sketch, "E1267", {"start": v(-380.81, -167.04) * mm, "end": v(-380.81, -159.04) * mm});
            skFitSpline(sketch, "E1268", {"points": [v(-366.7, -157.54) * mm, v(-366.7, -157.08) * mm, v(-366.94, -156.65) * mm, v(-367.35, -156.42) * mm]});
            skFitSpline(sketch, "E1269", {"points": [v(-367.35, -156.42) * mm, v(-367.75, -156.19) * mm, v(-368.24, -156.19) * mm, v(-368.65, -156.42) * mm]});
            skFitSpline(sketch, "E1270", {"points": [v(-368.65, -156.42) * mm, v(-369.05, -156.65) * mm, v(-369.3, -157.08) * mm, v(-369.3, -157.54) * mm]});
            skFitSpline(sketch, "E1271", {"points": [v(-369.3, -157.54) * mm, v(-369.3, -158) * mm, v(-369.05, -158.44) * mm, v(-368.65, -158.67) * mm]});
            skFitSpline(sketch, "E1272", {"points": [v(-368.65, -158.67) * mm, v(-368.24, -158.9) * mm, v(-367.75, -158.9) * mm, v(-367.35, -158.67) * mm]});
            skFitSpline(sketch, "E1273", {"points": [v(-367.35, -158.67) * mm, v(-366.94, -158.44) * mm, v(-366.7, -158) * mm, v(-366.7, -157.54) * mm]});
            skFitSpline(sketch, "E1274", {"points": [v(-221.98, -164.76) * mm, v(-222.16, -164.76) * mm, v(-222.32, -164.85) * mm, v(-222.4, -165) * mm]});
            skFitSpline(sketch, "E1275", {"points": [v(-223.1, -164.33) * mm, v(-223.27, -164.43) * mm, v(-223.37, -164.64) * mm, v(-223.33, -164.85) * mm]});
            skFitSpline(sketch, "E1276", {"points": [v(-223.33, -164.85) * mm, v(-223.3, -165.05) * mm, v(-223.14, -165.22) * mm, v(-222.93, -165.25) * mm]});
            skFitSpline(sketch, "E1277", {"points": [v(-222.93, -165.25) * mm, v(-222.72, -165.29) * mm, v(-222.51, -165.2) * mm, v(-222.4, -165) * mm]});
            skFitSpline(sketch, "E1278", {"points": [v(-223.1, -164.33) * mm, v(-222.94, -164.24) * mm, v(-222.84, -164.07) * mm, v(-222.84, -163.9) * mm]});
            skFitSpline(sketch, "E1279", {"points": [v(-222.84, -162.26) * mm, v(-222.84, -162.13) * mm, v(-222.9, -162) * mm, v(-222.99, -161.9) * mm]});
            skFitSpline(sketch, "E1280", {"points": [v(-222.99, -161.9) * mm, v(-223.08, -161.81) * mm, v(-223.2, -161.76) * mm, v(-223.34, -161.76) * mm]});
            skFitSpline(sketch, "E1281", {"points": [v(-228.34, -161.76) * mm, v(-228.47, -161.76) * mm, v(-228.6, -161.81) * mm, v(-228.7, -161.9) * mm]});
            skFitSpline(sketch, "E1282", {"points": [v(-228.7, -161.9) * mm, v(-228.79, -162) * mm, v(-228.84, -162.13) * mm, v(-228.84, -162.26) * mm]});
            skFitSpline(sketch, "E1283", {"points": [v(-228.84, -163.9) * mm, v(-228.84, -164.07) * mm, v(-228.75, -164.24) * mm, v(-228.6, -164.33) * mm]});
            skFitSpline(sketch, "E1284", {"points": [v(-229.28, -165) * mm, v(-229.17, -165.2) * mm, v(-228.96, -165.29) * mm, v(-228.76, -165.25) * mm]});
            skFitSpline(sketch, "E1285", {"points": [v(-228.76, -165.25) * mm, v(-228.55, -165.22) * mm, v(-228.39, -165.05) * mm, v(-228.35, -164.85) * mm]});
            skFitSpline(sketch, "E1286", {"points": [v(-228.35, -164.85) * mm, v(-228.31, -164.64) * mm, v(-228.41, -164.43) * mm, v(-228.6, -164.33) * mm]});
            skFitSpline(sketch, "E1287", {"points": [v(-229.28, -165) * mm, v(-229.36, -164.85) * mm, v(-229.53, -164.76) * mm, v(-229.7, -164.76) * mm]});
            skLineSegment(sketch, "E1288", {"start": v(-222.84, -163.9) * mm, "end": v(-222.84, -162.26) * mm});
            skFitSpline(sketch, "E1289", {"points": [v(-234.24, -178.17) * mm, v(-234.24, -179.1) * mm, v(-233.6, -179.9) * mm, v(-232.7, -180.12) * mm]});
            skLineSegment(sketch, "E1290", {"start": v(-223.34, -161.76) * mm, "end": v(-228.34, -161.76) * mm});
            skFitSpline(sketch, "E1291", {"points": [v(-204.82, -186.58) * mm, v(-202.74, -187.06) * mm, v(-200.56, -186.57) * mm, v(-198.89, -185.24) * mm]});
            skFitSpline(sketch, "E1292", {"points": [v(-198.89, -185.24) * mm, v(-197.22, -183.91) * mm, v(-196.24, -181.9) * mm, v(-196.24, -179.76) * mm]});
            skLineSegment(sketch, "E1293", {"start": v(-228.84, -162.26) * mm, "end": v(-228.84, -163.9) * mm});
            skFitSpline(sketch, "E1294", {"points": [v(-200.78, -164.76) * mm, v(-200.96, -164.76) * mm, v(-201.12, -164.85) * mm, v(-201.2, -165) * mm]});
            skFitSpline(sketch, "E1295", {"points": [v(-201.9, -164.33) * mm, v(-202.07, -164.43) * mm, v(-202.17, -164.64) * mm, v(-202.14, -164.85) * mm]});
            skFitSpline(sketch, "E1296", {"points": [v(-202.14, -164.85) * mm, v(-202.1, -165.05) * mm, v(-201.94, -165.22) * mm, v(-201.73, -165.25) * mm]});
            skFitSpline(sketch, "E1297", {"points": [v(-201.73, -165.25) * mm, v(-201.52, -165.29) * mm, v(-201.31, -165.2) * mm, v(-201.2, -165) * mm]});
            skFitSpline(sketch, "E1298", {"points": [v(-201.9, -164.33) * mm, v(-201.74, -164.24) * mm, v(-201.64, -164.07) * mm, v(-201.64, -163.9) * mm]});
            skLineSegment(sketch, "E1299", {"start": v(-229.7, -164.76) * mm, "end": v(-234.24, -164.76) * mm});
            skLineSegment(sketch, "E1300", {"start": v(-234.24, -164.76) * mm, "end": v(-234.24, -178.17) * mm});
            skFitSpline(sketch, "E1301", {"points": [v(-201.64, -162.26) * mm, v(-201.64, -162.13) * mm, v(-201.7, -162) * mm, v(-201.79, -161.9) * mm]});
            skFitSpline(sketch, "E1302", {"points": [v(-201.79, -161.9) * mm, v(-201.88, -161.81) * mm, v(-202.01, -161.76) * mm, v(-202.14, -161.76) * mm]});
            skLineSegment(sketch, "E1303", {"start": v(-232.7, -180.12) * mm, "end": v(-204.82, -186.58) * mm});
            skFitSpline(sketch, "E1304", {"points": [v(-207.14, -161.76) * mm, v(-207.42, -161.76) * mm, v(-207.64, -161.98) * mm, v(-207.64, -162.26) * mm]});
            skLineSegment(sketch, "E1305", {"start": v(-196.24, -179.76) * mm, "end": v(-196.24, -164.76) * mm});
            skLineSegment(sketch, "E1306", {"start": v(-196.24, -164.76) * mm, "end": v(-200.78, -164.76) * mm});
            skFitSpline(sketch, "E1307", {"points": [v(-207.64, -163.9) * mm, v(-207.64, -164.07) * mm, v(-207.55, -164.24) * mm, v(-207.4, -164.33) * mm]});
            skFitSpline(sketch, "E1308", {"points": [v(-208.08, -165) * mm, v(-207.97, -165.2) * mm, v(-207.76, -165.29) * mm, v(-207.56, -165.25) * mm]});
            skFitSpline(sketch, "E1309", {"points": [v(-207.56, -165.25) * mm, v(-207.35, -165.22) * mm, v(-207.19, -165.05) * mm, v(-207.15, -164.85) * mm]});
            skFitSpline(sketch, "E1310", {"points": [v(-207.15, -164.85) * mm, v(-207.11, -164.64) * mm, v(-207.21, -164.43) * mm, v(-207.4, -164.33) * mm]});
            skFitSpline(sketch, "E1311", {"points": [v(-208.08, -165) * mm, v(-208.16, -164.85) * mm, v(-208.33, -164.76) * mm, v(-208.5, -164.76) * mm]});
            skLineSegment(sketch, "E1312", {"start": v(-201.64, -163.9) * mm, "end": v(-201.64, -162.26) * mm});
            skFitSpline(sketch, "E1313", {"points": [v(-199.24, -179.76) * mm, v(-199.24, -178.33) * mm, v(-200, -177) * mm, v(-201.24, -176.29) * mm]});
            skFitSpline(sketch, "E1314", {"points": [v(-201.24, -176.29) * mm, v(-202.48, -175.57) * mm, v(-204, -175.57) * mm, v(-205.24, -176.29) * mm]});
            skFitSpline(sketch, "E1315", {"points": [v(-205.24, -176.29) * mm, v(-206.48, -177) * mm, v(-207.24, -178.33) * mm, v(-207.24, -179.76) * mm]});
            skFitSpline(sketch, "E1316", {"points": [v(-207.24, -179.76) * mm, v(-207.24, -181.2) * mm, v(-206.48, -182.51) * mm, v(-205.24, -183.23) * mm]});
            skFitSpline(sketch, "E1317", {"points": [v(-205.24, -183.23) * mm, v(-204, -183.95) * mm, v(-202.48, -183.95) * mm, v(-201.24, -183.23) * mm]});
            skFitSpline(sketch, "E1318", {"points": [v(-201.24, -183.23) * mm, v(-200, -182.51) * mm, v(-199.24, -181.2) * mm, v(-199.24, -179.76) * mm]});
            skLineSegment(sketch, "E1319", {"start": v(-202.14, -161.76) * mm, "end": v(-207.14, -161.76) * mm});
            skFitSpline(sketch, "E1320", {"points": [v(-174.3, 181.89) * mm, v(-174.49, 181.89) * mm, v(-174.65, 181.8) * mm, v(-174.74, 181.64) * mm]});
            skFitSpline(sketch, "E1321", {"points": [v(-175.42, 182.32) * mm, v(-175.6, 182.22) * mm, v(-175.7, 182) * mm, v(-175.67, 181.8) * mm]});
            skFitSpline(sketch, "E1322", {"points": [v(-175.67, 181.8) * mm, v(-175.63, 181.6) * mm, v(-175.47, 181.43) * mm, v(-175.26, 181.4) * mm]});
            skFitSpline(sketch, "E1323", {"points": [v(-175.26, 181.4) * mm, v(-175.05, 181.36) * mm, v(-174.85, 181.46) * mm, v(-174.74, 181.64) * mm]});
            skFitSpline(sketch, "E1324", {"points": [v(-175.42, 182.32) * mm, v(-175.27, 182.41) * mm, v(-175.17, 182.58) * mm, v(-175.17, 182.75) * mm]});
            skLineSegment(sketch, "E1325", {"start": v(-207.64, -162.26) * mm, "end": v(-207.64, -163.9) * mm});
            skFitSpline(sketch, "E1326", {"points": [v(-175.17, 184.39) * mm, v(-175.17, 184.52) * mm, v(-175.23, 184.65) * mm, v(-175.32, 184.74) * mm]});
            skFitSpline(sketch, "E1327", {"points": [v(-175.32, 184.74) * mm, v(-175.41, 184.84) * mm, v(-175.54, 184.89) * mm, v(-175.67, 184.89) * mm]});
            skLineSegment(sketch, "E1328", {"start": v(-208.5, -164.76) * mm, "end": v(-213.64, -164.76) * mm});
            skLineSegment(sketch, "E1329", {"start": v(-213.64, -164.76) * mm, "end": v(-213.64, -167.76) * mm});
            skLineSegment(sketch, "E1330", {"start": v(-213.64, -167.76) * mm, "end": v(-212.37, -167.76) * mm});
            skLineSegment(sketch, "E1331", {"start": v(-212.37, -167.76) * mm, "end": v(-212.37, -171.76) * mm});
            skLineSegment(sketch, "E1332", {"start": v(-212.37, -171.76) * mm, "end": v(-213.64, -171.76) * mm});
            skLineSegment(sketch, "E1333", {"start": v(-213.64, -171.76) * mm, "end": v(-213.64, -174.76) * mm});
            skLineSegment(sketch, "E1334", {"start": v(-213.64, -174.76) * mm, "end": v(-216.84, -174.76) * mm});
            skLineSegment(sketch, "E1335", {"start": v(-216.84, -174.76) * mm, "end": v(-216.84, -171.76) * mm});
            skLineSegment(sketch, "E1336", {"start": v(-216.84, -171.76) * mm, "end": v(-218.12, -171.76) * mm});
            skLineSegment(sketch, "E1337", {"start": v(-218.12, -171.76) * mm, "end": v(-218.12, -167.76) * mm});
            skLineSegment(sketch, "E1338", {"start": v(-218.12, -167.76) * mm, "end": v(-216.84, -167.76) * mm});
            skLineSegment(sketch, "E1339", {"start": v(-216.84, -167.76) * mm, "end": v(-216.84, -164.76) * mm});
            skLineSegment(sketch, "E1340", {"start": v(-216.84, -164.76) * mm, "end": v(-221.98, -164.76) * mm});
            skFitSpline(sketch, "E1341", {"points": [v(-180.67, 184.89) * mm, v(-180.8, 184.89) * mm, v(-180.93, 184.84) * mm, v(-181.03, 184.74) * mm]});
            skFitSpline(sketch, "E1342", {"points": [v(-181.03, 184.74) * mm, v(-181.12, 184.65) * mm, v(-181.17, 184.52) * mm, v(-181.17, 184.39) * mm]});
            skFitSpline(sketch, "E1343", {"points": [v(-181.17, 182.75) * mm, v(-181.17, 182.58) * mm, v(-181.08, 182.41) * mm, v(-180.92, 182.32) * mm]});
            skFitSpline(sketch, "E1344", {"points": [v(-181.6, 181.64) * mm, v(-181.5, 181.46) * mm, v(-181.3, 181.36) * mm, v(-181.09, 181.4) * mm]});
            skFitSpline(sketch, "E1345", {"points": [v(-181.09, 181.4) * mm, v(-180.88, 181.43) * mm, v(-180.72, 181.6) * mm, v(-180.68, 181.8) * mm]});
            skFitSpline(sketch, "E1346", {"points": [v(-180.68, 181.8) * mm, v(-180.64, 182) * mm, v(-180.74, 182.22) * mm, v(-180.92, 182.32) * mm]});
            skFitSpline(sketch, "E1347", {"points": [v(-181.6, 181.64) * mm, v(-181.7, 181.8) * mm, v(-181.86, 181.89) * mm, v(-182.04, 181.89) * mm]});
            skLineSegment(sketch, "E1348", {"start": v(-175.17, 182.75) * mm, "end": v(-175.17, 184.39) * mm});
            skFitSpline(sketch, "E1349", {"points": [v(-186.57, 168.48) * mm, v(-186.57, 167.55) * mm, v(-185.93, 166.74) * mm, v(-185.03, 166.53) * mm]});
            skLineSegment(sketch, "E1350", {"start": v(-175.67, 184.89) * mm, "end": v(-180.67, 184.89) * mm});
            skFitSpline(sketch, "E1351", {"points": [v(-157.15, 160.07) * mm, v(-155.07, 159.59) * mm, v(-152.89, 160.08) * mm, v(-151.22, 161.41) * mm]});
            skFitSpline(sketch, "E1352", {"points": [v(-151.22, 161.41) * mm, v(-149.55, 162.74) * mm, v(-148.57, 164.75) * mm, v(-148.57, 166.89) * mm]});
            skLineSegment(sketch, "E1353", {"start": v(-181.17, 184.39) * mm, "end": v(-181.17, 182.75) * mm});
            skFitSpline(sketch, "E1354", {"points": [v(-153.1, 181.89) * mm, v(-153.29, 181.89) * mm, v(-153.45, 181.8) * mm, v(-153.54, 181.64) * mm]});
            skFitSpline(sketch, "E1355", {"points": [v(-154.22, 182.32) * mm, v(-154.4, 182.22) * mm, v(-154.5, 182) * mm, v(-154.47, 181.8) * mm]});
            skFitSpline(sketch, "E1356", {"points": [v(-154.47, 181.8) * mm, v(-154.43, 181.6) * mm, v(-154.27, 181.43) * mm, v(-154.06, 181.4) * mm]});
            skFitSpline(sketch, "E1357", {"points": [v(-154.06, 181.4) * mm, v(-153.85, 181.36) * mm, v(-153.65, 181.46) * mm, v(-153.54, 181.64) * mm]});
            skFitSpline(sketch, "E1358", {"points": [v(-154.22, 182.32) * mm, v(-154.07, 182.41) * mm, v(-153.97, 182.58) * mm, v(-153.97, 182.75) * mm]});
            skLineSegment(sketch, "E1359", {"start": v(-182.04, 181.89) * mm, "end": v(-186.57, 181.89) * mm});
            skLineSegment(sketch, "E1360", {"start": v(-186.57, 181.89) * mm, "end": v(-186.57, 168.48) * mm});
            skFitSpline(sketch, "E1361", {"points": [v(-153.97, 184.39) * mm, v(-153.97, 184.52) * mm, v(-154.03, 184.65) * mm, v(-154.12, 184.74) * mm]});
            skFitSpline(sketch, "E1362", {"points": [v(-154.12, 184.74) * mm, v(-154.21, 184.84) * mm, v(-154.34, 184.89) * mm, v(-154.47, 184.89) * mm]});
            skLineSegment(sketch, "E1363", {"start": v(-185.03, 166.53) * mm, "end": v(-157.15, 160.07) * mm});
            skFitSpline(sketch, "E1364", {"points": [v(-159.47, 184.89) * mm, v(-159.75, 184.89) * mm, v(-159.97, 184.66) * mm, v(-159.97, 184.39) * mm]});
            skLineSegment(sketch, "E1365", {"start": v(-148.57, 166.89) * mm, "end": v(-148.57, 181.89) * mm});
            skLineSegment(sketch, "E1366", {"start": v(-148.57, 181.89) * mm, "end": v(-153.1, 181.89) * mm});
            skFitSpline(sketch, "E1367", {"points": [v(-159.97, 182.75) * mm, v(-159.97, 182.58) * mm, v(-159.88, 182.41) * mm, v(-159.72, 182.32) * mm]});
            skFitSpline(sketch, "E1368", {"points": [v(-160.4, 181.64) * mm, v(-160.3, 181.46) * mm, v(-160.1, 181.36) * mm, v(-159.89, 181.4) * mm]});
            skFitSpline(sketch, "E1369", {"points": [v(-159.89, 181.4) * mm, v(-159.68, 181.43) * mm, v(-159.52, 181.6) * mm, v(-159.48, 181.8) * mm]});
            skFitSpline(sketch, "E1370", {"points": [v(-159.48, 181.8) * mm, v(-159.45, 182) * mm, v(-159.54, 182.22) * mm, v(-159.72, 182.32) * mm]});
            skFitSpline(sketch, "E1371", {"points": [v(-160.4, 181.64) * mm, v(-160.5, 181.8) * mm, v(-160.66, 181.89) * mm, v(-160.84, 181.89) * mm]});
            skLineSegment(sketch, "E1372", {"start": v(-153.97, 182.75) * mm, "end": v(-153.97, 184.39) * mm});
            skFitSpline(sketch, "E1373", {"points": [v(-151.57, 166.89) * mm, v(-151.57, 168.32) * mm, v(-152.33, 169.64) * mm, v(-153.57, 170.36) * mm]});
            skFitSpline(sketch, "E1374", {"points": [v(-153.57, 170.36) * mm, v(-154.8, 171.08) * mm, v(-156.34, 171.08) * mm, v(-157.57, 170.36) * mm]});
            skFitSpline(sketch, "E1375", {"points": [v(-157.57, 170.36) * mm, v(-158.81, 169.64) * mm, v(-159.58, 168.32) * mm, v(-159.57, 166.89) * mm]});
            skFitSpline(sketch, "E1376", {"points": [v(-159.57, 166.89) * mm, v(-159.58, 165.46) * mm, v(-158.81, 164.13) * mm, v(-157.57, 163.42) * mm]});
            skFitSpline(sketch, "E1377", {"points": [v(-157.57, 163.42) * mm, v(-156.34, 162.7) * mm, v(-154.8, 162.7) * mm, v(-153.57, 163.42) * mm]});
            skFitSpline(sketch, "E1378", {"points": [v(-153.57, 163.42) * mm, v(-152.33, 164.13) * mm, v(-151.57, 165.46) * mm, v(-151.57, 166.89) * mm]});
            skLineSegment(sketch, "E1379", {"start": v(-154.47, 184.89) * mm, "end": v(-159.47, 184.89) * mm});
            skLineSegment(sketch, "E1380", {"start": v(-159.97, 184.39) * mm, "end": v(-159.97, 182.75) * mm});
            skFitSpline(sketch, "E1381", {"points": [v(61.75, -141.03) * mm, v(61.07, -139.85) * mm, v(59.7, -139.28) * mm, v(58.38, -139.63) * mm]});
            skFitSpline(sketch, "E1382", {"points": [v(58.38, -139.63) * mm, v(57.07, -139.98) * mm, v(56.16, -141.17) * mm, v(56.16, -142.53) * mm]});
            skLineSegment(sketch, "E1383", {"start": v(-160.84, 181.89) * mm, "end": v(-165.97, 181.89) * mm});
            skLineSegment(sketch, "E1384", {"start": v(-165.97, 181.89) * mm, "end": v(-165.97, 178.89) * mm});
            skLineSegment(sketch, "E1385", {"start": v(-165.97, 178.89) * mm, "end": v(-164.7, 178.89) * mm});
            skLineSegment(sketch, "E1386", {"start": v(-164.7, 178.89) * mm, "end": v(-164.7, 174.89) * mm});
            skLineSegment(sketch, "E1387", {"start": v(-164.7, 174.89) * mm, "end": v(-165.97, 174.89) * mm});
            skLineSegment(sketch, "E1388", {"start": v(-165.97, 174.89) * mm, "end": v(-165.97, 171.89) * mm});
            skLineSegment(sketch, "E1389", {"start": v(-165.97, 171.89) * mm, "end": v(-169.17, 171.89) * mm});
            skLineSegment(sketch, "E1390", {"start": v(-169.17, 171.89) * mm, "end": v(-169.17, 174.89) * mm});
            skLineSegment(sketch, "E1391", {"start": v(-169.17, 174.89) * mm, "end": v(-170.45, 174.89) * mm});
            skLineSegment(sketch, "E1392", {"start": v(-170.45, 174.89) * mm, "end": v(-170.45, 178.89) * mm});
            skLineSegment(sketch, "E1393", {"start": v(-170.45, 178.89) * mm, "end": v(-169.17, 178.89) * mm});
            skLineSegment(sketch, "E1394", {"start": v(-169.17, 178.89) * mm, "end": v(-169.17, 181.89) * mm});
            skLineSegment(sketch, "E1395", {"start": v(-169.17, 181.89) * mm, "end": v(-174.3, 181.89) * mm});
            skFitSpline(sketch, "E1396", {"points": [v(56.16, -166.26) * mm, v(56.16, -167.91) * mm, v(57.5, -169.26) * mm, v(59.16, -169.26) * mm]});
            skFitSpline(sketch, "E1397", {"points": [v(72.86, -169.26) * mm, v(73.93, -169.26) * mm, v(74.92, -168.68) * mm, v(75.45, -167.76) * mm]});
            skFitSpline(sketch, "E1398", {"points": [v(75.45, -167.76) * mm, v(76, -166.83) * mm, v(76, -165.68) * mm, v(75.45, -164.76) * mm]});
            skLineSegment(sketch, "E1399", {"start": v(56.16, -166.26) * mm, "end": v(56.16, -142.53) * mm});
            skFitSpline(sketch, "E1400", {"points": [v(56.16, 142.72) * mm, v(56.16, 141.36) * mm, v(57.07, 140.17) * mm, v(58.38, 139.82) * mm]});
            skFitSpline(sketch, "E1401", {"points": [v(58.38, 139.82) * mm, v(59.7, 139.47) * mm, v(61.07, 140.05) * mm, v(61.75, 141.22) * mm]});
            skLineSegment(sketch, "E1402", {"start": v(59.16, -169.26) * mm, "end": v(72.86, -169.26) * mm});
            skFitSpline(sketch, "E1403", {"points": [v(59.16, 169.45) * mm, v(57.5, 169.45) * mm, v(56.16, 168.1) * mm, v(56.16, 166.45) * mm]});
            skLineSegment(sketch, "E1404", {"start": v(61.75, -141.03) * mm, "end": v(75.45, -164.76) * mm});
            skFitSpline(sketch, "E1405", {"points": [v(75.45, 164.95) * mm, v(76, 165.88) * mm, v(76, 167.02) * mm, v(75.45, 167.95) * mm]});
            skFitSpline(sketch, "E1406", {"points": [v(75.45, 167.95) * mm, v(74.92, 168.88) * mm, v(73.93, 169.45) * mm, v(72.86, 169.45) * mm]});
            skFitSpline(sketch, "E1407", {"points": [v(53.42, -21.16) * mm, v(53.42, -20.59) * mm, v(53.11, -20.06) * mm, v(52.62, -19.77) * mm]});
            skFitSpline(sketch, "E1408", {"points": [v(52.62, -19.77) * mm, v(52.12, -19.48) * mm, v(51.51, -19.48) * mm, v(51.02, -19.77) * mm]});
            skFitSpline(sketch, "E1409", {"points": [v(51.02, -19.77) * mm, v(50.52, -20.06) * mm, v(50.21, -20.59) * mm, v(50.22, -21.16) * mm]});
            skFitSpline(sketch, "E1410", {"points": [v(50.22, -21.16) * mm, v(50.21, -21.73) * mm, v(50.52, -22.26) * mm, v(51.02, -22.55) * mm]});
            skFitSpline(sketch, "E1411", {"points": [v(51.02, -22.55) * mm, v(51.51, -22.84) * mm, v(52.12, -22.84) * mm, v(52.62, -22.55) * mm]});
            skFitSpline(sketch, "E1412", {"points": [v(52.62, -22.55) * mm, v(53.11, -22.26) * mm, v(53.42, -21.73) * mm, v(53.42, -21.16) * mm]});
            skLineSegment(sketch, "E1413", {"start": v(56.16, 166.45) * mm, "end": v(56.16, 142.72) * mm});
            skFitSpline(sketch, "E1414", {"points": [v(53.42, 21.34) * mm, v(53.42, 21.92) * mm, v(53.11, 22.45) * mm, v(52.62, 22.73) * mm]});
            skFitSpline(sketch, "E1415", {"points": [v(52.62, 22.73) * mm, v(52.12, 23.02) * mm, v(51.51, 23.02) * mm, v(51.02, 22.73) * mm]});
            skFitSpline(sketch, "E1416", {"points": [v(51.02, 22.73) * mm, v(50.52, 22.45) * mm, v(50.21, 21.92) * mm, v(50.22, 21.34) * mm]});
            skFitSpline(sketch, "E1417", {"points": [v(50.22, 21.34) * mm, v(50.21, 20.77) * mm, v(50.52, 20.24) * mm, v(51.02, 19.95) * mm]});
            skFitSpline(sketch, "E1418", {"points": [v(51.02, 19.95) * mm, v(51.51, 19.67) * mm, v(52.12, 19.67) * mm, v(52.62, 19.95) * mm]});
            skFitSpline(sketch, "E1419", {"points": [v(52.62, 19.95) * mm, v(53.11, 20.24) * mm, v(53.42, 20.77) * mm, v(53.42, 21.34) * mm]});
            skLineSegment(sketch, "E1420", {"start": v(59.16, 169.45) * mm, "end": v(72.86, 169.45) * mm});
            skFitSpline(sketch, "E1421", {"points": [v(53.42, 63.85) * mm, v(53.42, 64.42) * mm, v(53.11, 64.95) * mm, v(52.62, 65.24) * mm]});
            skFitSpline(sketch, "E1422", {"points": [v(52.62, 65.24) * mm, v(52.12, 65.53) * mm, v(51.51, 65.53) * mm, v(51.02, 65.24) * mm]});
            skFitSpline(sketch, "E1423", {"points": [v(51.02, 65.24) * mm, v(50.52, 64.95) * mm, v(50.21, 64.42) * mm, v(50.22, 63.85) * mm]});
            skFitSpline(sketch, "E1424", {"points": [v(50.22, 63.85) * mm, v(50.21, 63.27) * mm, v(50.52, 62.74) * mm, v(51.02, 62.46) * mm]});
            skFitSpline(sketch, "E1425", {"points": [v(51.02, 62.46) * mm, v(51.51, 62.17) * mm, v(52.12, 62.17) * mm, v(52.62, 62.46) * mm]});
            skFitSpline(sketch, "E1426", {"points": [v(52.62, 62.46) * mm, v(53.11, 62.74) * mm, v(53.42, 63.27) * mm, v(53.42, 63.85) * mm]});
            skLineSegment(sketch, "E1427", {"start": v(61.75, 141.22) * mm, "end": v(75.45, 164.95) * mm});
            skFitSpline(sketch, "E1428", {"points": [v(53.42, -21.16) * mm, v(53.42, -20.59) * mm, v(53.11, -20.06) * mm, v(52.62, -19.77) * mm]});
            skFitSpline(sketch, "E1429", {"points": [v(52.62, -19.77) * mm, v(52.12, -19.48) * mm, v(51.51, -19.48) * mm, v(51.02, -19.77) * mm]});
            skFitSpline(sketch, "E1430", {"points": [v(51.02, -19.77) * mm, v(50.52, -20.06) * mm, v(50.21, -20.59) * mm, v(50.22, -21.16) * mm]});
            skFitSpline(sketch, "E1431", {"points": [v(50.22, -21.16) * mm, v(50.21, -21.73) * mm, v(50.52, -22.26) * mm, v(51.02, -22.55) * mm]});
            skFitSpline(sketch, "E1432", {"points": [v(51.02, -22.55) * mm, v(51.51, -22.84) * mm, v(52.12, -22.84) * mm, v(52.62, -22.55) * mm]});
            skFitSpline(sketch, "E1433", {"points": [v(52.62, -22.55) * mm, v(53.11, -22.26) * mm, v(53.42, -21.73) * mm, v(53.42, -21.16) * mm]});
            skFitSpline(sketch, "E1434", {"points": [v(53.42, -21.16) * mm, v(53.42, -20.59) * mm, v(53.11, -20.06) * mm, v(52.62, -19.77) * mm]});
            skFitSpline(sketch, "E1435", {"points": [v(52.62, -19.77) * mm, v(52.12, -19.48) * mm, v(51.51, -19.48) * mm, v(51.02, -19.77) * mm]});
            skFitSpline(sketch, "E1436", {"points": [v(51.02, -19.77) * mm, v(50.52, -20.06) * mm, v(50.21, -20.59) * mm, v(50.22, -21.16) * mm]});
            skFitSpline(sketch, "E1437", {"points": [v(50.22, -21.16) * mm, v(50.21, -21.73) * mm, v(50.52, -22.26) * mm, v(51.02, -22.55) * mm]});
            skFitSpline(sketch, "E1438", {"points": [v(51.02, -22.55) * mm, v(51.51, -22.84) * mm, v(52.12, -22.84) * mm, v(52.62, -22.55) * mm]});
            skFitSpline(sketch, "E1439", {"points": [v(52.62, -22.55) * mm, v(53.11, -22.26) * mm, v(53.42, -21.73) * mm, v(53.42, -21.16) * mm]});
            skFitSpline(sketch, "E1440", {"points": [v(53.42, -66.18) * mm, v(53.42, -65.61) * mm, v(53.11, -65.08) * mm, v(52.62, -64.8) * mm]});
            skFitSpline(sketch, "E1441", {"points": [v(52.62, -64.8) * mm, v(52.12, -64.5) * mm, v(51.51, -64.5) * mm, v(51.02, -64.8) * mm]});
            skFitSpline(sketch, "E1442", {"points": [v(51.02, -64.8) * mm, v(50.52, -65.08) * mm, v(50.21, -65.61) * mm, v(50.22, -66.18) * mm]});
            skFitSpline(sketch, "E1443", {"points": [v(50.22, -66.18) * mm, v(50.21, -66.76) * mm, v(50.52, -67.29) * mm, v(51.02, -67.57) * mm]});
            skFitSpline(sketch, "E1444", {"points": [v(51.02, -67.57) * mm, v(51.51, -67.86) * mm, v(52.12, -67.86) * mm, v(52.62, -67.57) * mm]});
            skFitSpline(sketch, "E1445", {"points": [v(52.62, -67.57) * mm, v(53.11, -67.29) * mm, v(53.42, -66.76) * mm, v(53.42, -66.18) * mm]});
            skFitSpline(sketch, "E1446", {"points": [v(371.03, -72.13) * mm, v(370.85, -72.13) * mm, v(370.69, -72.22) * mm, v(370.6, -72.38) * mm]});
            skFitSpline(sketch, "E1447", {"points": [v(369.91, -71.7) * mm, v(369.73, -71.8) * mm, v(369.63, -72) * mm, v(369.67, -72.21) * mm]});
            skFitSpline(sketch, "E1448", {"points": [v(369.67, -72.21) * mm, v(369.7, -72.42) * mm, v(369.87, -72.58) * mm, v(370.08, -72.62) * mm]});
            skFitSpline(sketch, "E1449", {"points": [v(370.08, -72.62) * mm, v(370.28, -72.66) * mm, v(370.5, -72.56) * mm, v(370.6, -72.38) * mm]});
            skFitSpline(sketch, "E1450", {"points": [v(369.91, -71.7) * mm, v(370.07, -71.6) * mm, v(370.16, -71.44) * mm, v(370.16, -71.26) * mm]});
            skFitSpline(sketch, "E1451", {"points": [v(370.16, -66.8) * mm, v(370.16, -66.61) * mm, v(370.07, -66.45) * mm, v(369.91, -66.36) * mm]});
            skFitSpline(sketch, "E1452", {"points": [v(370.6, -65.68) * mm, v(370.5, -65.5) * mm, v(370.28, -65.4) * mm, v(370.08, -65.43) * mm]});
            skFitSpline(sketch, "E1453", {"points": [v(370.08, -65.43) * mm, v(369.87, -65.47) * mm, v(369.7, -65.63) * mm, v(369.67, -65.84) * mm]});
            skFitSpline(sketch, "E1454", {"points": [v(369.67, -65.84) * mm, v(369.63, -66.05) * mm, v(369.73, -66.25) * mm, v(369.91, -66.36) * mm]});
            skFitSpline(sketch, "E1455", {"points": [v(370.6, -65.68) * mm, v(370.69, -65.83) * mm, v(370.85, -65.93) * mm, v(371.03, -65.93) * mm]});
            skFitSpline(sketch, "E1456", {"points": [v(372.6, -65.93) * mm, v(372.78, -65.93) * mm, v(372.94, -65.83) * mm, v(373.03, -65.68) * mm]});
            skFitSpline(sketch, "E1457", {"points": [v(373.71, -66.36) * mm, v(373.9, -66.25) * mm, v(374, -66.05) * mm, v(373.96, -65.84) * mm]});
            skFitSpline(sketch, "E1458", {"points": [v(373.96, -65.84) * mm, v(373.92, -65.63) * mm, v(373.76, -65.47) * mm, v(373.55, -65.43) * mm]});
            skFitSpline(sketch, "E1459", {"points": [v(373.55, -65.43) * mm, v(373.34, -65.4) * mm, v(373.14, -65.5) * mm, v(373.03, -65.68) * mm]});
            skFitSpline(sketch, "E1460", {"points": [v(373.71, -66.36) * mm, v(373.56, -66.45) * mm, v(373.46, -66.61) * mm, v(373.46, -66.8) * mm]});
            skFitSpline(sketch, "E1461", {"points": [v(373.46, -71.26) * mm, v(373.46, -71.44) * mm, v(373.56, -71.6) * mm, v(373.71, -71.7) * mm]});
            skFitSpline(sketch, "E1462", {"points": [v(373.03, -72.38) * mm, v(373.14, -72.56) * mm, v(373.34, -72.66) * mm, v(373.55, -72.62) * mm]});
            skFitSpline(sketch, "E1463", {"points": [v(373.55, -72.62) * mm, v(373.76, -72.58) * mm, v(373.92, -72.42) * mm, v(373.96, -72.21) * mm]});
            skFitSpline(sketch, "E1464", {"points": [v(373.96, -72.21) * mm, v(374, -72) * mm, v(373.9, -71.8) * mm, v(373.71, -71.7) * mm]});
            skFitSpline(sketch, "E1465", {"points": [v(373.03, -72.38) * mm, v(372.94, -72.22) * mm, v(372.78, -72.13) * mm, v(372.6, -72.13) * mm]});
            skLineSegment(sketch, "E1466", {"start": v(370.16, -71.26) * mm, "end": v(370.16, -66.8) * mm});
            skFitSpline(sketch, "E1467", {"points": [v(371.03, -50.93) * mm, v(370.85, -50.93) * mm, v(370.69, -51.02) * mm, v(370.6, -51.18) * mm]});
            skFitSpline(sketch, "E1468", {"points": [v(369.91, -50.5) * mm, v(369.73, -50.6) * mm, v(369.63, -50.8) * mm, v(369.67, -51.01) * mm]});
            skFitSpline(sketch, "E1469", {"points": [v(369.67, -51.01) * mm, v(369.7, -51.22) * mm, v(369.87, -51.38) * mm, v(370.08, -51.42) * mm]});
            skFitSpline(sketch, "E1470", {"points": [v(370.08, -51.42) * mm, v(370.28, -51.46) * mm, v(370.5, -51.36) * mm, v(370.6, -51.18) * mm]});
            skFitSpline(sketch, "E1471", {"points": [v(369.91, -50.5) * mm, v(370.07, -50.4) * mm, v(370.16, -50.24) * mm, v(370.16, -50.06) * mm]});
            skLineSegment(sketch, "E1472", {"start": v(371.03, -65.93) * mm, "end": v(372.6, -65.93) * mm});
            skFitSpline(sketch, "E1473", {"points": [v(370.16, -45.6) * mm, v(370.16, -45.41) * mm, v(370.07, -45.25) * mm, v(369.91, -45.16) * mm]});
            skFitSpline(sketch, "E1474", {"points": [v(370.6, -44.48) * mm, v(370.5, -44.3) * mm, v(370.28, -44.2) * mm, v(370.08, -44.23) * mm]});
            skFitSpline(sketch, "E1475", {"points": [v(370.08, -44.23) * mm, v(369.87, -44.27) * mm, v(369.7, -44.43) * mm, v(369.67, -44.64) * mm]});
            skFitSpline(sketch, "E1476", {"points": [v(369.67, -44.64) * mm, v(369.63, -44.85) * mm, v(369.73, -45.05) * mm, v(369.91, -45.16) * mm]});
            skFitSpline(sketch, "E1477", {"points": [v(370.6, -44.48) * mm, v(370.69, -44.63) * mm, v(370.85, -44.73) * mm, v(371.03, -44.73) * mm]});
            skLineSegment(sketch, "E1478", {"start": v(373.46, -66.8) * mm, "end": v(373.46, -71.26) * mm});
            skFitSpline(sketch, "E1479", {"points": [v(372.6, -44.73) * mm, v(372.78, -44.73) * mm, v(372.94, -44.63) * mm, v(373.03, -44.48) * mm]});
            skFitSpline(sketch, "E1480", {"points": [v(373.71, -45.16) * mm, v(373.9, -45.05) * mm, v(374, -44.85) * mm, v(373.96, -44.64) * mm]});
            skFitSpline(sketch, "E1481", {"points": [v(373.96, -44.64) * mm, v(373.92, -44.43) * mm, v(373.76, -44.27) * mm, v(373.55, -44.23) * mm]});
            skFitSpline(sketch, "E1482", {"points": [v(373.55, -44.23) * mm, v(373.34, -44.2) * mm, v(373.14, -44.3) * mm, v(373.03, -44.48) * mm]});
            skFitSpline(sketch, "E1483", {"points": [v(373.71, -45.16) * mm, v(373.56, -45.25) * mm, v(373.46, -45.41) * mm, v(373.46, -45.6) * mm]});
            skLineSegment(sketch, "E1484", {"start": v(372.6, -72.13) * mm, "end": v(371.03, -72.13) * mm});
            skFitSpline(sketch, "E1485", {"points": [v(373.46, -50.06) * mm, v(373.46, -50.24) * mm, v(373.56, -50.4) * mm, v(373.71, -50.5) * mm]});
            skFitSpline(sketch, "E1486", {"points": [v(373.03, -51.18) * mm, v(373.14, -51.36) * mm, v(373.34, -51.46) * mm, v(373.55, -51.42) * mm]});
            skFitSpline(sketch, "E1487", {"points": [v(373.55, -51.42) * mm, v(373.76, -51.38) * mm, v(373.92, -51.22) * mm, v(373.96, -51.01) * mm]});
            skFitSpline(sketch, "E1488", {"points": [v(373.96, -51.01) * mm, v(374, -50.8) * mm, v(373.9, -50.6) * mm, v(373.71, -50.5) * mm]});
            skFitSpline(sketch, "E1489", {"points": [v(373.03, -51.18) * mm, v(372.94, -51.02) * mm, v(372.78, -50.93) * mm, v(372.6, -50.93) * mm]});
            skLineSegment(sketch, "E1490", {"start": v(370.16, -50.06) * mm, "end": v(370.16, -45.6) * mm});
            skFitSpline(sketch, "E1491", {"points": [v(373.41, -58.43) * mm, v(373.41, -57.85) * mm, v(373.1, -57.33) * mm, v(372.61, -57.04) * mm]});
            skFitSpline(sketch, "E1492", {"points": [v(372.61, -57.04) * mm, v(372.12, -56.76) * mm, v(371.5, -56.76) * mm, v(371.01, -57.04) * mm]});
            skFitSpline(sketch, "E1493", {"points": [v(371.01, -57.04) * mm, v(370.52, -57.33) * mm, v(370.21, -57.85) * mm, v(370.21, -58.43) * mm]});
            skFitSpline(sketch, "E1494", {"points": [v(370.21, -58.43) * mm, v(370.21, -59) * mm, v(370.52, -59.53) * mm, v(371.01, -59.81) * mm]});
            skFitSpline(sketch, "E1495", {"points": [v(371.01, -59.81) * mm, v(371.5, -60.1) * mm, v(372.12, -60.1) * mm, v(372.61, -59.81) * mm]});
            skFitSpline(sketch, "E1496", {"points": [v(372.61, -59.81) * mm, v(373.1, -59.53) * mm, v(373.41, -59) * mm, v(373.41, -58.43) * mm]});
            skLineSegment(sketch, "E1497", {"start": v(371.03, -44.73) * mm, "end": v(372.6, -44.73) * mm});
            skFitSpline(sketch, "E1498", {"points": [v(-372.6, 6.45) * mm, v(-372.78, 6.45) * mm, v(-372.94, 6.36) * mm, v(-373.03, 6.2) * mm]});
            skFitSpline(sketch, "E1499", {"points": [v(-373.71, 6.89) * mm, v(-373.9, 6.78) * mm, v(-374, 6.57) * mm, v(-373.96, 6.37) * mm]});
            skFitSpline(sketch, "E1500", {"points": [v(-373.96, 6.37) * mm, v(-373.92, 6.16) * mm, v(-373.76, 6) * mm, v(-373.55, 5.96) * mm]});
            skFitSpline(sketch, "E1501", {"points": [v(-373.55, 5.96) * mm, v(-373.34, 5.92) * mm, v(-373.14, 6.02) * mm, v(-373.03, 6.2) * mm]});
            skFitSpline(sketch, "E1502", {"points": [v(-373.71, 6.89) * mm, v(-373.56, 6.98) * mm, v(-373.46, 7.14) * mm, v(-373.46, 7.32) * mm]});
            skLineSegment(sketch, "E1503", {"start": v(373.46, -45.6) * mm, "end": v(373.46, -50.06) * mm});
            skFitSpline(sketch, "E1504", {"points": [v(-373.46, 11.79) * mm, v(-373.46, 11.97) * mm, v(-373.56, 12.13) * mm, v(-373.71, 12.22) * mm]});
            skFitSpline(sketch, "E1505", {"points": [v(-373.03, 12.9) * mm, v(-373.14, 13.09) * mm, v(-373.34, 13.18) * mm, v(-373.55, 13.15) * mm]});
            skFitSpline(sketch, "E1506", {"points": [v(-373.55, 13.15) * mm, v(-373.76, 13.1) * mm, v(-373.92, 12.95) * mm, v(-373.96, 12.74) * mm]});
            skFitSpline(sketch, "E1507", {"points": [v(-373.96, 12.74) * mm, v(-374, 12.53) * mm, v(-373.9, 12.33) * mm, v(-373.71, 12.22) * mm]});
            skFitSpline(sketch, "E1508", {"points": [v(-373.03, 12.9) * mm, v(-372.94, 12.75) * mm, v(-372.78, 12.65) * mm, v(-372.6, 12.65) * mm]});
            skLineSegment(sketch, "E1509", {"start": v(372.6, -50.93) * mm, "end": v(371.03, -50.93) * mm});
            skFitSpline(sketch, "E1510", {"points": [v(-371.03, 12.65) * mm, v(-370.85, 12.65) * mm, v(-370.69, 12.75) * mm, v(-370.6, 12.9) * mm]});
            skFitSpline(sketch, "E1511", {"points": [v(-369.91, 12.22) * mm, v(-369.73, 12.33) * mm, v(-369.63, 12.53) * mm, v(-369.67, 12.74) * mm]});
            skFitSpline(sketch, "E1512", {"points": [v(-369.67, 12.74) * mm, v(-369.7, 12.95) * mm, v(-369.87, 13.1) * mm, v(-370.08, 13.15) * mm]});
            skFitSpline(sketch, "E1513", {"points": [v(-370.08, 13.15) * mm, v(-370.28, 13.18) * mm, v(-370.5, 13.09) * mm, v(-370.6, 12.9) * mm]});
            skFitSpline(sketch, "E1514", {"points": [v(-369.91, 12.22) * mm, v(-370.07, 12.13) * mm, v(-370.16, 11.97) * mm, v(-370.16, 11.79) * mm]});
            skFitSpline(sketch, "E1515", {"points": [v(-370.16, 7.32) * mm, v(-370.16, 7.14) * mm, v(-370.07, 6.98) * mm, v(-369.91, 6.89) * mm]});
            skFitSpline(sketch, "E1516", {"points": [v(-370.6, 6.2) * mm, v(-370.5, 6.02) * mm, v(-370.28, 5.92) * mm, v(-370.08, 5.96) * mm]});
            skFitSpline(sketch, "E1517", {"points": [v(-370.08, 5.96) * mm, v(-369.87, 6) * mm, v(-369.7, 6.16) * mm, v(-369.67, 6.37) * mm]});
            skFitSpline(sketch, "E1518", {"points": [v(-369.67, 6.37) * mm, v(-369.63, 6.57) * mm, v(-369.73, 6.78) * mm, v(-369.91, 6.89) * mm]});
            skFitSpline(sketch, "E1519", {"points": [v(-370.6, 6.2) * mm, v(-370.69, 6.36) * mm, v(-370.85, 6.45) * mm, v(-371.03, 6.45) * mm]});
            skLineSegment(sketch, "E1520", {"start": v(-373.46, 7.32) * mm, "end": v(-373.46, 11.79) * mm});
            skFitSpline(sketch, "E1521", {"points": [v(-372.6, -14.75) * mm, v(-372.78, -14.75) * mm, v(-372.94, -14.84) * mm, v(-373.03, -15) * mm]});
            skFitSpline(sketch, "E1522", {"points": [v(-373.71, -14.31) * mm, v(-373.9, -14.42) * mm, v(-374, -14.63) * mm, v(-373.96, -14.83) * mm]});
            skFitSpline(sketch, "E1523", {"points": [v(-373.96, -14.83) * mm, v(-373.92, -15.04) * mm, v(-373.76, -15.2) * mm, v(-373.55, -15.24) * mm]});
            skFitSpline(sketch, "E1524", {"points": [v(-373.55, -15.24) * mm, v(-373.34, -15.28) * mm, v(-373.14, -15.18) * mm, v(-373.03, -15) * mm]});
            skFitSpline(sketch, "E1525", {"points": [v(-373.71, -14.31) * mm, v(-373.56, -14.22) * mm, v(-373.46, -14.06) * mm, v(-373.46, -13.88) * mm]});
            skLineSegment(sketch, "E1526", {"start": v(-372.6, 12.65) * mm, "end": v(-371.03, 12.65) * mm});
            skFitSpline(sketch, "E1527", {"points": [v(-373.46, -9.41) * mm, v(-373.46, -9.23) * mm, v(-373.56, -9.07) * mm, v(-373.71, -8.98) * mm]});
            skFitSpline(sketch, "E1528", {"points": [v(-373.03, -8.3) * mm, v(-373.14, -8.11) * mm, v(-373.34, -8.02) * mm, v(-373.55, -8.05) * mm]});
            skFitSpline(sketch, "E1529", {"points": [v(-373.55, -8.05) * mm, v(-373.76, -8.1) * mm, v(-373.92, -8.25) * mm, v(-373.96, -8.46) * mm]});
            skFitSpline(sketch, "E1530", {"points": [v(-373.96, -8.46) * mm, v(-374, -8.67) * mm, v(-373.9, -8.87) * mm, v(-373.71, -8.98) * mm]});
            skFitSpline(sketch, "E1531", {"points": [v(-373.03, -8.3) * mm, v(-372.94, -8.45) * mm, v(-372.78, -8.55) * mm, v(-372.6, -8.55) * mm]});
            skLineSegment(sketch, "E1532", {"start": v(-370.16, 11.79) * mm, "end": v(-370.16, 7.32) * mm});
            skFitSpline(sketch, "E1533", {"points": [v(-371.03, -8.55) * mm, v(-370.85, -8.55) * mm, v(-370.69, -8.45) * mm, v(-370.6, -8.3) * mm]});
            skFitSpline(sketch, "E1534", {"points": [v(-369.91, -8.98) * mm, v(-369.73, -8.87) * mm, v(-369.63, -8.67) * mm, v(-369.67, -8.46) * mm]});
            skFitSpline(sketch, "E1535", {"points": [v(-369.67, -8.46) * mm, v(-369.7, -8.25) * mm, v(-369.87, -8.1) * mm, v(-370.08, -8.05) * mm]});
            skFitSpline(sketch, "E1536", {"points": [v(-370.08, -8.05) * mm, v(-370.28, -8.02) * mm, v(-370.5, -8.11) * mm, v(-370.6, -8.3) * mm]});
            skFitSpline(sketch, "E1537", {"points": [v(-369.91, -8.98) * mm, v(-370.07, -9.07) * mm, v(-370.16, -9.23) * mm, v(-370.16, -9.41) * mm]});
            skLineSegment(sketch, "E1538", {"start": v(-371.03, 6.45) * mm, "end": v(-372.6, 6.45) * mm});
            skFitSpline(sketch, "E1539", {"points": [v(-370.16, -13.88) * mm, v(-370.16, -14.06) * mm, v(-370.07, -14.22) * mm, v(-369.91, -14.31) * mm]});
            skFitSpline(sketch, "E1540", {"points": [v(-370.6, -15) * mm, v(-370.5, -15.18) * mm, v(-370.28, -15.28) * mm, v(-370.08, -15.24) * mm]});
            skFitSpline(sketch, "E1541", {"points": [v(-370.08, -15.24) * mm, v(-369.87, -15.2) * mm, v(-369.7, -15.04) * mm, v(-369.67, -14.83) * mm]});
            skFitSpline(sketch, "E1542", {"points": [v(-369.67, -14.83) * mm, v(-369.63, -14.63) * mm, v(-369.73, -14.42) * mm, v(-369.91, -14.31) * mm]});
            skFitSpline(sketch, "E1543", {"points": [v(-370.6, -15) * mm, v(-370.69, -14.84) * mm, v(-370.85, -14.75) * mm, v(-371.03, -14.75) * mm]});
            skLineSegment(sketch, "E1544", {"start": v(-373.46, -13.88) * mm, "end": v(-373.46, -9.41) * mm});
            skFitSpline(sketch, "E1545", {"points": [v(-370.21, -1.05) * mm, v(-370.21, -0.47) * mm, v(-370.52, 0.05) * mm, v(-371.01, 0.34) * mm]});
            skFitSpline(sketch, "E1546", {"points": [v(-371.01, 0.34) * mm, v(-371.5, 0.63) * mm, v(-372.12, 0.63) * mm, v(-372.61, 0.34) * mm]});
            skFitSpline(sketch, "E1547", {"points": [v(-372.61, 0.34) * mm, v(-373.1, 0.05) * mm, v(-373.41, -0.47) * mm, v(-373.41, -1.05) * mm]});
            skFitSpline(sketch, "E1548", {"points": [v(-373.41, -1.05) * mm, v(-373.41, -1.62) * mm, v(-373.1, -2.15) * mm, v(-372.61, -2.43) * mm]});
            skFitSpline(sketch, "E1549", {"points": [v(-372.61, -2.43) * mm, v(-372.12, -2.72) * mm, v(-371.5, -2.72) * mm, v(-371.01, -2.43) * mm]});
            skFitSpline(sketch, "E1550", {"points": [v(-371.01, -2.43) * mm, v(-370.52, -2.15) * mm, v(-370.21, -1.62) * mm, v(-370.21, -1.05) * mm]});
            skLineSegment(sketch, "E1551", {"start": v(-372.6, -8.55) * mm, "end": v(-371.03, -8.55) * mm});
            skFitSpline(sketch, "E1552", {"points": [v(371.03, 44.92) * mm, v(370.85, 44.92) * mm, v(370.69, 44.83) * mm, v(370.6, 44.67) * mm]});
            skFitSpline(sketch, "E1553", {"points": [v(369.91, 45.36) * mm, v(369.73, 45.25) * mm, v(369.63, 45.04) * mm, v(369.67, 44.84) * mm]});
            skFitSpline(sketch, "E1554", {"points": [v(369.67, 44.84) * mm, v(369.7, 44.63) * mm, v(369.87, 44.47) * mm, v(370.08, 44.43) * mm]});
            skFitSpline(sketch, "E1555", {"points": [v(370.08, 44.43) * mm, v(370.28, 44.4) * mm, v(370.5, 44.5) * mm, v(370.6, 44.67) * mm]});
            skFitSpline(sketch, "E1556", {"points": [v(369.91, 45.36) * mm, v(370.07, 45.44) * mm, v(370.16, 45.6) * mm, v(370.16, 45.79) * mm]});
            skLineSegment(sketch, "E1557", {"start": v(-370.16, -9.41) * mm, "end": v(-370.16, -13.88) * mm});
            skFitSpline(sketch, "E1558", {"points": [v(370.16, 50.26) * mm, v(370.16, 50.44) * mm, v(370.07, 50.6) * mm, v(369.91, 50.69) * mm]});
            skFitSpline(sketch, "E1559", {"points": [v(370.6, 51.37) * mm, v(370.5, 51.55) * mm, v(370.28, 51.65) * mm, v(370.08, 51.61) * mm]});
            skFitSpline(sketch, "E1560", {"points": [v(370.08, 51.61) * mm, v(369.87, 51.58) * mm, v(369.7, 51.42) * mm, v(369.67, 51.2) * mm]});
            skFitSpline(sketch, "E1561", {"points": [v(369.67, 51.2) * mm, v(369.63, 51) * mm, v(369.73, 50.8) * mm, v(369.91, 50.69) * mm]});
            skFitSpline(sketch, "E1562", {"points": [v(370.6, 51.37) * mm, v(370.69, 51.22) * mm, v(370.85, 51.12) * mm, v(371.03, 51.12) * mm]});
            skLineSegment(sketch, "E1563", {"start": v(-371.03, -14.75) * mm, "end": v(-372.6, -14.75) * mm});
            skFitSpline(sketch, "E1564", {"points": [v(372.6, 51.12) * mm, v(372.78, 51.12) * mm, v(372.94, 51.22) * mm, v(373.03, 51.37) * mm]});
            skFitSpline(sketch, "E1565", {"points": [v(373.71, 50.69) * mm, v(373.9, 50.8) * mm, v(374, 51) * mm, v(373.96, 51.2) * mm]});
            skFitSpline(sketch, "E1566", {"points": [v(373.96, 51.2) * mm, v(373.92, 51.42) * mm, v(373.76, 51.58) * mm, v(373.55, 51.61) * mm]});
            skFitSpline(sketch, "E1567", {"points": [v(373.55, 51.61) * mm, v(373.34, 51.65) * mm, v(373.14, 51.55) * mm, v(373.03, 51.37) * mm]});
            skFitSpline(sketch, "E1568", {"points": [v(373.71, 50.69) * mm, v(373.56, 50.6) * mm, v(373.46, 50.44) * mm, v(373.46, 50.26) * mm]});
            skFitSpline(sketch, "E1569", {"points": [v(373.46, 45.79) * mm, v(373.46, 45.6) * mm, v(373.56, 45.44) * mm, v(373.71, 45.36) * mm]});
            skFitSpline(sketch, "E1570", {"points": [v(373.03, 44.67) * mm, v(373.14, 44.5) * mm, v(373.34, 44.4) * mm, v(373.55, 44.43) * mm]});
            skFitSpline(sketch, "E1571", {"points": [v(373.55, 44.43) * mm, v(373.76, 44.47) * mm, v(373.92, 44.63) * mm, v(373.96, 44.84) * mm]});
            skFitSpline(sketch, "E1572", {"points": [v(373.96, 44.84) * mm, v(374, 45.04) * mm, v(373.9, 45.25) * mm, v(373.71, 45.36) * mm]});
            skFitSpline(sketch, "E1573", {"points": [v(373.03, 44.67) * mm, v(372.94, 44.83) * mm, v(372.78, 44.92) * mm, v(372.6, 44.92) * mm]});
            skLineSegment(sketch, "E1574", {"start": v(370.16, 45.79) * mm, "end": v(370.16, 50.26) * mm});
            skFitSpline(sketch, "E1575", {"points": [v(371.03, 66.12) * mm, v(370.85, 66.12) * mm, v(370.69, 66.03) * mm, v(370.6, 65.87) * mm]});
            skFitSpline(sketch, "E1576", {"points": [v(369.91, 66.56) * mm, v(369.73, 66.45) * mm, v(369.63, 66.24) * mm, v(369.67, 66.04) * mm]});
            skFitSpline(sketch, "E1577", {"points": [v(369.67, 66.04) * mm, v(369.7, 65.83) * mm, v(369.87, 65.67) * mm, v(370.08, 65.63) * mm]});
            skFitSpline(sketch, "E1578", {"points": [v(370.08, 65.63) * mm, v(370.28, 65.6) * mm, v(370.5, 65.7) * mm, v(370.6, 65.87) * mm]});
            skFitSpline(sketch, "E1579", {"points": [v(369.91, 66.56) * mm, v(370.07, 66.64) * mm, v(370.16, 66.8) * mm, v(370.16, 66.99) * mm]});
            skLineSegment(sketch, "E1580", {"start": v(371.03, 51.12) * mm, "end": v(372.6, 51.12) * mm});
            skFitSpline(sketch, "E1581", {"points": [v(370.16, 71.46) * mm, v(370.16, 71.63) * mm, v(370.07, 71.8) * mm, v(369.91, 71.89) * mm]});
            skFitSpline(sketch, "E1582", {"points": [v(370.6, 72.57) * mm, v(370.5, 72.75) * mm, v(370.28, 72.85) * mm, v(370.08, 72.81) * mm]});
            skFitSpline(sketch, "E1583", {"points": [v(370.08, 72.81) * mm, v(369.87, 72.78) * mm, v(369.7, 72.62) * mm, v(369.67, 72.4) * mm]});
            skFitSpline(sketch, "E1584", {"points": [v(369.67, 72.4) * mm, v(369.63, 72.2) * mm, v(369.73, 72) * mm, v(369.91, 71.89) * mm]});
            skFitSpline(sketch, "E1585", {"points": [v(370.6, 72.57) * mm, v(370.69, 72.42) * mm, v(370.85, 72.32) * mm, v(371.03, 72.32) * mm]});
            skLineSegment(sketch, "E1586", {"start": v(373.46, 50.26) * mm, "end": v(373.46, 45.79) * mm});
            skFitSpline(sketch, "E1587", {"points": [v(372.6, 72.32) * mm, v(372.78, 72.32) * mm, v(372.94, 72.42) * mm, v(373.03, 72.57) * mm]});
            skFitSpline(sketch, "E1588", {"points": [v(373.71, 71.89) * mm, v(373.9, 72) * mm, v(374, 72.2) * mm, v(373.96, 72.4) * mm]});
            skFitSpline(sketch, "E1589", {"points": [v(373.96, 72.4) * mm, v(373.92, 72.62) * mm, v(373.76, 72.78) * mm, v(373.55, 72.81) * mm]});
            skFitSpline(sketch, "E1590", {"points": [v(373.55, 72.81) * mm, v(373.34, 72.85) * mm, v(373.14, 72.75) * mm, v(373.03, 72.57) * mm]});
            skFitSpline(sketch, "E1591", {"points": [v(373.71, 71.89) * mm, v(373.56, 71.8) * mm, v(373.46, 71.63) * mm, v(373.46, 71.46) * mm]});
            skLineSegment(sketch, "E1592", {"start": v(372.6, 44.92) * mm, "end": v(371.03, 44.92) * mm});
            skFitSpline(sketch, "E1593", {"points": [v(373.46, 66.99) * mm, v(373.46, 66.8) * mm, v(373.56, 66.64) * mm, v(373.71, 66.56) * mm]});
            skFitSpline(sketch, "E1594", {"points": [v(373.03, 65.87) * mm, v(373.14, 65.7) * mm, v(373.34, 65.6) * mm, v(373.55, 65.63) * mm]});
            skFitSpline(sketch, "E1595", {"points": [v(373.55, 65.63) * mm, v(373.76, 65.67) * mm, v(373.92, 65.83) * mm, v(373.96, 66.04) * mm]});
            skFitSpline(sketch, "E1596", {"points": [v(373.96, 66.04) * mm, v(374, 66.24) * mm, v(373.9, 66.45) * mm, v(373.71, 66.56) * mm]});
            skFitSpline(sketch, "E1597", {"points": [v(373.03, 65.87) * mm, v(372.94, 66.03) * mm, v(372.78, 66.12) * mm, v(372.6, 66.12) * mm]});
            skLineSegment(sketch, "E1598", {"start": v(370.16, 66.99) * mm, "end": v(370.16, 71.46) * mm});
            skFitSpline(sketch, "E1599", {"points": [v(373.41, 58.62) * mm, v(373.41, 59.2) * mm, v(373.1, 59.72) * mm, v(372.61, 60) * mm]});
            skFitSpline(sketch, "E1600", {"points": [v(372.61, 60) * mm, v(372.12, 60.3) * mm, v(371.5, 60.3) * mm, v(371.01, 60) * mm]});
            skFitSpline(sketch, "E1601", {"points": [v(371.01, 60) * mm, v(370.52, 59.72) * mm, v(370.21, 59.2) * mm, v(370.21, 58.62) * mm]});
            skFitSpline(sketch, "E1602", {"points": [v(370.21, 58.62) * mm, v(370.21, 58.05) * mm, v(370.52, 57.52) * mm, v(371.01, 57.24) * mm]});
            skFitSpline(sketch, "E1603", {"points": [v(371.01, 57.24) * mm, v(371.5, 56.95) * mm, v(372.12, 56.95) * mm, v(372.61, 57.24) * mm]});
            skFitSpline(sketch, "E1604", {"points": [v(372.61, 57.24) * mm, v(373.1, 57.52) * mm, v(373.41, 58.05) * mm, v(373.41, 58.62) * mm]});
            skLineSegment(sketch, "E1605", {"start": v(371.03, 72.32) * mm, "end": v(372.6, 72.32) * mm});
            skFitSpline(sketch, "E1606", {"points": [v(-19.4, 193.8) * mm, v(-19.48, 193.95) * mm, v(-19.65, 194.04) * mm, v(-19.83, 194.04) * mm]});
            skFitSpline(sketch, "E1607", {"points": [v(-19.4, 193.8) * mm, v(-19.29, 193.61) * mm, v(-19.08, 193.52) * mm, v(-18.87, 193.55) * mm]});
            skFitSpline(sketch, "E1608", {"points": [v(-18.87, 193.55) * mm, v(-18.67, 193.59) * mm, v(-18.5, 193.75) * mm, v(-18.47, 193.96) * mm]});
            skFitSpline(sketch, "E1609", {"points": [v(-18.47, 193.96) * mm, v(-18.43, 194.16) * mm, v(-18.53, 194.37) * mm, v(-18.71, 194.48) * mm]});
            skFitSpline(sketch, "E1610", {"points": [v(-18.96, 194.91) * mm, v(-18.96, 194.73) * mm, v(-18.87, 194.57) * mm, v(-18.71, 194.48) * mm]});
            skLineSegment(sketch, "E1611", {"start": v(373.46, 71.46) * mm, "end": v(373.46, 66.99) * mm});
            skFitSpline(sketch, "E1612", {"points": [v(-18.46, 197.04) * mm, v(-18.74, 197.04) * mm, v(-18.96, 196.82) * mm, v(-18.96, 196.54) * mm]});
            skLineSegment(sketch, "E1613", {"start": v(372.6, 66.12) * mm, "end": v(371.03, 66.12) * mm});
            skFitSpline(sketch, "E1614", {"points": [v(-12.96, 196.54) * mm, v(-12.96, 196.82) * mm, v(-13.18, 197.04) * mm, v(-13.46, 197.04) * mm]});
            skFitSpline(sketch, "E1615", {"points": [v(-13.21, 194.48) * mm, v(-13.06, 194.57) * mm, v(-12.96, 194.73) * mm, v(-12.96, 194.91) * mm]});
            skFitSpline(sketch, "E1616", {"points": [v(-13.21, 194.48) * mm, v(-13.4, 194.37) * mm, v(-13.49, 194.16) * mm, v(-13.45, 193.96) * mm]});
            skFitSpline(sketch, "E1617", {"points": [v(-13.45, 193.96) * mm, v(-13.42, 193.75) * mm, v(-13.25, 193.59) * mm, v(-13.05, 193.55) * mm]});
            skFitSpline(sketch, "E1618", {"points": [v(-13.05, 193.55) * mm, v(-12.84, 193.52) * mm, v(-12.63, 193.61) * mm, v(-12.53, 193.8) * mm]});
            skFitSpline(sketch, "E1619", {"points": [v(-12.1, 194.04) * mm, v(-12.27, 194.04) * mm, v(-12.44, 193.95) * mm, v(-12.53, 193.8) * mm]});
            skLineSegment(sketch, "E1620", {"start": v(-18.96, 194.91) * mm, "end": v(-18.96, 196.54) * mm});
            skFitSpline(sketch, "E1621", {"points": [v(1.8, 193.8) * mm, v(1.72, 193.95) * mm, v(1.55, 194.04) * mm, v(1.37, 194.04) * mm]});
            skFitSpline(sketch, "E1622", {"points": [v(1.8, 193.8) * mm, v(1.91, 193.61) * mm, v(2.12, 193.52) * mm, v(2.33, 193.55) * mm]});
            skFitSpline(sketch, "E1623", {"points": [v(2.33, 193.55) * mm, v(2.53, 193.59) * mm, v(2.7, 193.75) * mm, v(2.73, 193.96) * mm]});
            skFitSpline(sketch, "E1624", {"points": [v(2.73, 193.96) * mm, v(2.77, 194.16) * mm, v(2.67, 194.37) * mm, v(2.49, 194.48) * mm]});
            skFitSpline(sketch, "E1625", {"points": [v(2.24, 194.91) * mm, v(2.24, 194.73) * mm, v(2.33, 194.57) * mm, v(2.49, 194.48) * mm]});
            skLineSegment(sketch, "E1626", {"start": v(-18.46, 197.04) * mm, "end": v(-13.46, 197.04) * mm});
            skFitSpline(sketch, "E1627", {"points": [v(2.74, 197.04) * mm, v(2.46, 197.04) * mm, v(2.24, 196.82) * mm, v(2.24, 196.54) * mm]});
            skLineSegment(sketch, "E1628", {"start": v(-12.96, 196.54) * mm, "end": v(-12.96, 194.91) * mm});
            skFitSpline(sketch, "E1629", {"points": [v(8.24, 196.54) * mm, v(8.24, 196.82) * mm, v(8.01, 197.04) * mm, v(7.74, 197.04) * mm]});
            skLineSegment(sketch, "E1630", {"start": v(-12.1, 194.04) * mm, "end": v(-6.96, 194.04) * mm});
            skLineSegment(sketch, "E1631", {"start": v(-6.96, 194.04) * mm, "end": v(-6.96, 191.04) * mm});
            skLineSegment(sketch, "E1632", {"start": v(-6.96, 191.04) * mm, "end": v(-8.24, 191.04) * mm});
            skLineSegment(sketch, "E1633", {"start": v(-8.24, 191.04) * mm, "end": v(-8.24, 187.04) * mm});
            skLineSegment(sketch, "E1634", {"start": v(-8.24, 187.04) * mm, "end": v(-6.96, 187.04) * mm});
            skLineSegment(sketch, "E1635", {"start": v(-6.96, 187.04) * mm, "end": v(-6.96, 184.04) * mm});
            skLineSegment(sketch, "E1636", {"start": v(-6.96, 184.04) * mm, "end": v(-3.76, 184.04) * mm});
            skLineSegment(sketch, "E1637", {"start": v(-3.76, 184.04) * mm, "end": v(-3.76, 187.04) * mm});
            skLineSegment(sketch, "E1638", {"start": v(-3.76, 187.04) * mm, "end": v(-2.49, 187.04) * mm});
            skLineSegment(sketch, "E1639", {"start": v(-2.49, 187.04) * mm, "end": v(-2.49, 191.04) * mm});
            skLineSegment(sketch, "E1640", {"start": v(-2.49, 191.04) * mm, "end": v(-3.76, 191.04) * mm});
            skLineSegment(sketch, "E1641", {"start": v(-3.76, 191.04) * mm, "end": v(-3.76, 194.04) * mm});
            skLineSegment(sketch, "E1642", {"start": v(-3.76, 194.04) * mm, "end": v(1.37, 194.04) * mm});
            skFitSpline(sketch, "E1643", {"points": [v(7.99, 194.48) * mm, v(8.14, 194.57) * mm, v(8.24, 194.73) * mm, v(8.24, 194.91) * mm]});
            skFitSpline(sketch, "E1644", {"points": [v(7.99, 194.48) * mm, v(7.8, 194.37) * mm, v(7.7, 194.16) * mm, v(7.75, 193.96) * mm]});
            skFitSpline(sketch, "E1645", {"points": [v(7.75, 193.96) * mm, v(7.78, 193.75) * mm, v(7.94, 193.59) * mm, v(8.15, 193.55) * mm]});
            skFitSpline(sketch, "E1646", {"points": [v(8.15, 193.55) * mm, v(8.36, 193.52) * mm, v(8.57, 193.61) * mm, v(8.67, 193.8) * mm]});
            skFitSpline(sketch, "E1647", {"points": [v(9.1, 194.04) * mm, v(8.93, 194.04) * mm, v(8.76, 193.95) * mm, v(8.67, 193.8) * mm]});
            skLineSegment(sketch, "E1648", {"start": v(2.24, 194.91) * mm, "end": v(2.24, 196.54) * mm});
            skLineSegment(sketch, "E1649", {"start": v(2.74, 197.04) * mm, "end": v(7.74, 197.04) * mm});
            skFitSpline(sketch, "E1650", {"points": [v(8.67, 64.3) * mm, v(8.76, 64.14) * mm, v(8.93, 64.05) * mm, v(9.1, 64.05) * mm]});
            skFitSpline(sketch, "E1651", {"points": [v(8.67, 64.3) * mm, v(8.57, 64.48) * mm, v(8.36, 64.57) * mm, v(8.15, 64.54) * mm]});
            skFitSpline(sketch, "E1652", {"points": [v(8.15, 64.54) * mm, v(7.94, 64.5) * mm, v(7.78, 64.34) * mm, v(7.75, 64.13) * mm]});
            skFitSpline(sketch, "E1653", {"points": [v(7.75, 64.13) * mm, v(7.7, 63.93) * mm, v(7.8, 63.72) * mm, v(7.99, 63.61) * mm]});
            skFitSpline(sketch, "E1654", {"points": [v(8.22, 63.17) * mm, v(8.23, 63.35) * mm, v(8.14, 63.52) * mm, v(7.99, 63.61) * mm]});
            skFitSpline(sketch, "E1655", {"points": [v(-18.71, 63.61) * mm, v(-18.87, 63.52) * mm, v(-18.96, 63.36) * mm, v(-18.96, 63.18) * mm]});
            skFitSpline(sketch, "E1656", {"points": [v(-18.71, 63.61) * mm, v(-18.53, 63.72) * mm, v(-18.43, 63.93) * mm, v(-18.47, 64.13) * mm]});
            skFitSpline(sketch, "E1657", {"points": [v(-18.47, 64.13) * mm, v(-18.5, 64.34) * mm, v(-18.67, 64.5) * mm, v(-18.87, 64.54) * mm]});
            skFitSpline(sketch, "E1658", {"points": [v(-18.87, 64.54) * mm, v(-19.08, 64.57) * mm, v(-19.29, 64.48) * mm, v(-19.4, 64.3) * mm]});
            skFitSpline(sketch, "E1659", {"points": [v(-19.83, 64.05) * mm, v(-19.65, 64.05) * mm, v(-19.48, 64.14) * mm, v(-19.4, 64.3) * mm]});
            skLineSegment(sketch, "E1660", {"start": v(8.24, 196.54) * mm, "end": v(8.24, 194.91) * mm});
            skFitSpline(sketch, "E1661", {"points": [v(-31.33, 64.3) * mm, v(-31.24, 64.14) * mm, v(-31.07, 64.05) * mm, v(-30.9, 64.05) * mm]});
            skFitSpline(sketch, "E1662", {"points": [v(-31.33, 64.3) * mm, v(-31.43, 64.48) * mm, v(-31.64, 64.57) * mm, v(-31.85, 64.54) * mm]});
            skFitSpline(sketch, "E1663", {"points": [v(-31.85, 64.54) * mm, v(-32.05, 64.5) * mm, v(-32.22, 64.34) * mm, v(-32.25, 64.13) * mm]});
            skFitSpline(sketch, "E1664", {"points": [v(-32.25, 64.13) * mm, v(-32.29, 63.93) * mm, v(-32.2, 63.72) * mm, v(-32.01, 63.61) * mm]});
            skFitSpline(sketch, "E1665", {"points": [v(-31.76, 63.18) * mm, v(-31.76, 63.36) * mm, v(-31.86, 63.52) * mm, v(-32.01, 63.61) * mm]});
            skLineSegment(sketch, "E1666", {"start": v(9.1, 194.04) * mm, "end": v(19.64, 194.04) * mm});
            skFitSpline(sketch, "E1667", {"points": [v(-32.26, 61.05) * mm, v(-31.98, 61.05) * mm, v(-31.76, 61.27) * mm, v(-31.76, 61.55) * mm]});
            skLineSegment(sketch, "E1668", {"start": v(19.64, 189.04) * mm, "end": v(19.64, 168.04) * mm});
            skLineSegment(sketch, "E1669", {"start": v(19.64, 168.04) * mm, "end": v(17.64, 166.04) * mm});
            skLineSegment(sketch, "E1670", {"start": v(17.64, 166.04) * mm, "end": v(17.64, 64.05) * mm});
            skLineSegment(sketch, "E1671", {"start": v(17.64, 64.05) * mm, "end": v(9.1, 64.05) * mm});
            skFitSpline(sketch, "E1672", {"points": [v(-37.76, 61.55) * mm, v(-37.76, 61.27) * mm, v(-37.54, 61.05) * mm, v(-37.26, 61.05) * mm]});
            skLineSegment(sketch, "E1673", {"start": v(-19.83, 64.05) * mm, "end": v(-30.9, 64.05) * mm});
            skFitSpline(sketch, "E1674", {"points": [v(-37.51, 63.61) * mm, v(-37.67, 63.52) * mm, v(-37.76, 63.36) * mm, v(-37.76, 63.18) * mm]});
            skFitSpline(sketch, "E1675", {"points": [v(-37.51, 63.61) * mm, v(-37.33, 63.72) * mm, v(-37.23, 63.93) * mm, v(-37.27, 64.13) * mm]});
            skFitSpline(sketch, "E1676", {"points": [v(-37.27, 64.13) * mm, v(-37.3, 64.34) * mm, v(-37.47, 64.5) * mm, v(-37.67, 64.54) * mm]});
            skFitSpline(sketch, "E1677", {"points": [v(-37.67, 64.54) * mm, v(-37.88, 64.57) * mm, v(-38.09, 64.48) * mm, v(-38.2, 64.3) * mm]});
            skFitSpline(sketch, "E1678", {"points": [v(-38.63, 64.05) * mm, v(-38.45, 64.05) * mm, v(-38.28, 64.14) * mm, v(-38.2, 64.3) * mm]});
            skLineSegment(sketch, "E1679", {"start": v(-31.76, 63.18) * mm, "end": v(-31.76, 61.55) * mm});
            skFitSpline(sketch, "E1680", {"points": [v(-52.53, 64.3) * mm, v(-52.44, 64.14) * mm, v(-52.27, 64.05) * mm, v(-52.1, 64.05) * mm]});
            skFitSpline(sketch, "E1681", {"points": [v(-52.53, 64.3) * mm, v(-52.63, 64.48) * mm, v(-52.84, 64.57) * mm, v(-53.05, 64.54) * mm]});
            skFitSpline(sketch, "E1682", {"points": [v(-53.05, 64.54) * mm, v(-53.25, 64.5) * mm, v(-53.42, 64.34) * mm, v(-53.45, 64.13) * mm]});
            skFitSpline(sketch, "E1683", {"points": [v(-53.45, 64.13) * mm, v(-53.49, 63.93) * mm, v(-53.4, 63.72) * mm, v(-53.21, 63.61) * mm]});
            skFitSpline(sketch, "E1684", {"points": [v(-52.96, 63.18) * mm, v(-52.96, 63.36) * mm, v(-53.06, 63.52) * mm, v(-53.21, 63.61) * mm]});
            skLineSegment(sketch, "E1685", {"start": v(-32.26, 61.05) * mm, "end": v(-37.26, 61.05) * mm});
            skFitSpline(sketch, "E1686", {"points": [v(-53.46, 61.05) * mm, v(-53.18, 61.05) * mm, v(-52.96, 61.27) * mm, v(-52.96, 61.55) * mm]});
            skLineSegment(sketch, "E1687", {"start": v(-37.76, 61.55) * mm, "end": v(-37.76, 63.18) * mm});
            skFitSpline(sketch, "E1688", {"points": [v(-58.96, 61.55) * mm, v(-58.96, 61.41) * mm, v(-58.9, 61.29) * mm, v(-58.81, 61.2) * mm]});
            skFitSpline(sketch, "E1689", {"points": [v(-58.81, 61.2) * mm, v(-58.72, 61.1) * mm, v(-58.6, 61.05) * mm, v(-58.46, 61.05) * mm]});
            skLineSegment(sketch, "E1690", {"start": v(-38.63, 64.05) * mm, "end": v(-43.76, 64.05) * mm});
            skLineSegment(sketch, "E1691", {"start": v(-43.76, 64.05) * mm, "end": v(-43.76, 67.05) * mm});
            skLineSegment(sketch, "E1692", {"start": v(-43.76, 67.05) * mm, "end": v(-42.49, 67.05) * mm});
            skLineSegment(sketch, "E1693", {"start": v(-42.49, 67.05) * mm, "end": v(-42.49, 71.05) * mm});
            skLineSegment(sketch, "E1694", {"start": v(-42.49, 71.05) * mm, "end": v(-43.76, 71.05) * mm});
            skLineSegment(sketch, "E1695", {"start": v(-43.76, 71.05) * mm, "end": v(-43.76, 74.05) * mm});
            skLineSegment(sketch, "E1696", {"start": v(-43.76, 74.05) * mm, "end": v(-46.96, 74.05) * mm});
            skLineSegment(sketch, "E1697", {"start": v(-46.96, 74.05) * mm, "end": v(-46.96, 71.05) * mm});
            skLineSegment(sketch, "E1698", {"start": v(-46.96, 71.05) * mm, "end": v(-48.24, 71.05) * mm});
            skLineSegment(sketch, "E1699", {"start": v(-48.24, 71.05) * mm, "end": v(-48.24, 67.05) * mm});
            skLineSegment(sketch, "E1700", {"start": v(-48.24, 67.05) * mm, "end": v(-46.96, 67.05) * mm});
            skLineSegment(sketch, "E1701", {"start": v(-46.96, 67.05) * mm, "end": v(-46.96, 64.05) * mm});
            skLineSegment(sketch, "E1702", {"start": v(-46.96, 64.05) * mm, "end": v(-52.1, 64.05) * mm});
            skFitSpline(sketch, "E1703", {"points": [v(-58.71, 63.61) * mm, v(-58.87, 63.52) * mm, v(-58.96, 63.36) * mm, v(-58.96, 63.18) * mm]});
            skFitSpline(sketch, "E1704", {"points": [v(-58.71, 63.61) * mm, v(-58.53, 63.72) * mm, v(-58.43, 63.93) * mm, v(-58.47, 64.13) * mm]});
            skFitSpline(sketch, "E1705", {"points": [v(-58.47, 64.13) * mm, v(-58.5, 64.34) * mm, v(-58.67, 64.5) * mm, v(-58.87, 64.54) * mm]});
            skFitSpline(sketch, "E1706", {"points": [v(-58.87, 64.54) * mm, v(-59.08, 64.57) * mm, v(-59.29, 64.48) * mm, v(-59.4, 64.3) * mm]});
            skFitSpline(sketch, "E1707", {"points": [v(-59.83, 64.05) * mm, v(-59.65, 64.05) * mm, v(-59.48, 64.14) * mm, v(-59.4, 64.3) * mm]});
            skLineSegment(sketch, "E1708", {"start": v(-52.96, 63.18) * mm, "end": v(-52.96, 61.55) * mm});
            skFitSpline(sketch, "E1709", {"points": [v(-151.33, 64.3) * mm, v(-151.24, 64.14) * mm, v(-151.07, 64.05) * mm, v(-150.9, 64.05) * mm]});
            skFitSpline(sketch, "E1710", {"points": [v(-151.33, 64.3) * mm, v(-151.43, 64.48) * mm, v(-151.64, 64.57) * mm, v(-151.85, 64.54) * mm]});
            skFitSpline(sketch, "E1711", {"points": [v(-151.85, 64.54) * mm, v(-152.05, 64.5) * mm, v(-152.22, 64.34) * mm, v(-152.25, 64.13) * mm]});
            skFitSpline(sketch, "E1712", {"points": [v(-152.25, 64.13) * mm, v(-152.29, 63.93) * mm, v(-152.2, 63.72) * mm, v(-152, 63.61) * mm]});
            skFitSpline(sketch, "E1713", {"points": [v(-151.76, 63.18) * mm, v(-151.76, 63.36) * mm, v(-151.86, 63.52) * mm, v(-152, 63.61) * mm]});
            skLineSegment(sketch, "E1714", {"start": v(-53.46, 61.05) * mm, "end": v(-58.46, 61.05) * mm});
            skFitSpline(sketch, "E1715", {"points": [v(-152.26, 61.05) * mm, v(-151.98, 61.05) * mm, v(-151.76, 61.27) * mm, v(-151.76, 61.55) * mm]});
            skLineSegment(sketch, "E1716", {"start": v(-58.96, 61.55) * mm, "end": v(-58.96, 63.18) * mm});
            skFitSpline(sketch, "E1717", {"points": [v(-157.76, 61.55) * mm, v(-157.76, 61.41) * mm, v(-157.7, 61.29) * mm, v(-157.61, 61.2) * mm]});
            skFitSpline(sketch, "E1718", {"points": [v(-157.61, 61.2) * mm, v(-157.52, 61.1) * mm, v(-157.4, 61.05) * mm, v(-157.26, 61.05) * mm]});
            skLineSegment(sketch, "E1719", {"start": v(-59.83, 64.05) * mm, "end": v(-150.9, 64.05) * mm});
            skFitSpline(sketch, "E1720", {"points": [v(-157.5, 63.61) * mm, v(-157.66, 63.52) * mm, v(-157.76, 63.36) * mm, v(-157.76, 63.18) * mm]});
            skFitSpline(sketch, "E1721", {"points": [v(-157.5, 63.61) * mm, v(-157.33, 63.72) * mm, v(-157.23, 63.93) * mm, v(-157.27, 64.13) * mm]});
            skFitSpline(sketch, "E1722", {"points": [v(-157.27, 64.13) * mm, v(-157.3, 64.34) * mm, v(-157.47, 64.5) * mm, v(-157.67, 64.54) * mm]});
            skFitSpline(sketch, "E1723", {"points": [v(-157.67, 64.54) * mm, v(-157.88, 64.57) * mm, v(-158.09, 64.48) * mm, v(-158.2, 64.3) * mm]});
            skFitSpline(sketch, "E1724", {"points": [v(-158.63, 64.05) * mm, v(-158.45, 64.05) * mm, v(-158.28, 64.14) * mm, v(-158.2, 64.3) * mm]});
            skLineSegment(sketch, "E1725", {"start": v(-151.76, 63.18) * mm, "end": v(-151.76, 61.55) * mm});
            skFitSpline(sketch, "E1726", {"points": [v(-172.53, 64.3) * mm, v(-172.44, 64.14) * mm, v(-172.27, 64.05) * mm, v(-172.1, 64.05) * mm]});
            skFitSpline(sketch, "E1727", {"points": [v(-172.53, 64.3) * mm, v(-172.63, 64.48) * mm, v(-172.84, 64.57) * mm, v(-173.05, 64.54) * mm]});
            skFitSpline(sketch, "E1728", {"points": [v(-173.05, 64.54) * mm, v(-173.25, 64.5) * mm, v(-173.42, 64.34) * mm, v(-173.45, 64.13) * mm]});
            skFitSpline(sketch, "E1729", {"points": [v(-173.45, 64.13) * mm, v(-173.49, 63.93) * mm, v(-173.4, 63.72) * mm, v(-173.2, 63.61) * mm]});
            skFitSpline(sketch, "E1730", {"points": [v(-172.96, 63.18) * mm, v(-172.96, 63.36) * mm, v(-173.05, 63.52) * mm, v(-173.2, 63.61) * mm]});
            skLineSegment(sketch, "E1731", {"start": v(-152.26, 61.05) * mm, "end": v(-157.26, 61.05) * mm});
            skFitSpline(sketch, "E1732", {"points": [v(-173.46, 61.05) * mm, v(-173.33, 61.05) * mm, v(-173.2, 61.1) * mm, v(-173.1, 61.2) * mm]});
            skFitSpline(sketch, "E1733", {"points": [v(-173.1, 61.2) * mm, v(-173.01, 61.29) * mm, v(-172.96, 61.41) * mm, v(-172.96, 61.55) * mm]});
            skLineSegment(sketch, "E1734", {"start": v(-157.76, 61.55) * mm, "end": v(-157.76, 63.18) * mm});
            skFitSpline(sketch, "E1735", {"points": [v(-178.96, 61.55) * mm, v(-178.96, 61.41) * mm, v(-178.9, 61.29) * mm, v(-178.81, 61.2) * mm]});
            skFitSpline(sketch, "E1736", {"points": [v(-178.81, 61.2) * mm, v(-178.72, 61.1) * mm, v(-178.6, 61.05) * mm, v(-178.46, 61.05) * mm]});
            skLineSegment(sketch, "E1737", {"start": v(-158.63, 64.05) * mm, "end": v(-163.76, 64.05) * mm});
            skLineSegment(sketch, "E1738", {"start": v(-163.76, 64.05) * mm, "end": v(-163.76, 67.05) * mm});
            skLineSegment(sketch, "E1739", {"start": v(-163.76, 67.05) * mm, "end": v(-162.48, 67.05) * mm});
            skLineSegment(sketch, "E1740", {"start": v(-162.48, 67.05) * mm, "end": v(-162.48, 71.05) * mm});
            skLineSegment(sketch, "E1741", {"start": v(-162.48, 71.05) * mm, "end": v(-163.76, 71.05) * mm});
            skLineSegment(sketch, "E1742", {"start": v(-163.76, 71.05) * mm, "end": v(-163.76, 74.05) * mm});
            skLineSegment(sketch, "E1743", {"start": v(-163.76, 74.05) * mm, "end": v(-166.96, 74.05) * mm});
            skLineSegment(sketch, "E1744", {"start": v(-166.96, 74.05) * mm, "end": v(-166.96, 71.05) * mm});
            skLineSegment(sketch, "E1745", {"start": v(-166.96, 71.05) * mm, "end": v(-168.23, 71.05) * mm});
            skLineSegment(sketch, "E1746", {"start": v(-168.23, 71.05) * mm, "end": v(-168.23, 67.05) * mm});
            skLineSegment(sketch, "E1747", {"start": v(-168.23, 67.05) * mm, "end": v(-166.96, 67.05) * mm});
            skLineSegment(sketch, "E1748", {"start": v(-166.96, 67.05) * mm, "end": v(-166.96, 64.05) * mm});
            skLineSegment(sketch, "E1749", {"start": v(-166.96, 64.05) * mm, "end": v(-172.1, 64.05) * mm});
            skFitSpline(sketch, "E1750", {"points": [v(-178.7, 63.61) * mm, v(-178.86, 63.52) * mm, v(-178.96, 63.36) * mm, v(-178.96, 63.18) * mm]});
            skFitSpline(sketch, "E1751", {"points": [v(-178.7, 63.61) * mm, v(-178.53, 63.72) * mm, v(-178.43, 63.93) * mm, v(-178.47, 64.13) * mm]});
            skFitSpline(sketch, "E1752", {"points": [v(-178.47, 64.13) * mm, v(-178.5, 64.34) * mm, v(-178.67, 64.5) * mm, v(-178.87, 64.54) * mm]});
            skFitSpline(sketch, "E1753", {"points": [v(-178.87, 64.54) * mm, v(-179.08, 64.57) * mm, v(-179.29, 64.48) * mm, v(-179.4, 64.3) * mm]});
            skFitSpline(sketch, "E1754", {"points": [v(-179.83, 64.05) * mm, v(-179.65, 64.05) * mm, v(-179.48, 64.14) * mm, v(-179.4, 64.3) * mm]});
            skLineSegment(sketch, "E1755", {"start": v(-172.96, 63.18) * mm, "end": v(-172.96, 61.55) * mm});
            skFitSpline(sketch, "E1756", {"points": [v(-311.33, 64.3) * mm, v(-311.24, 64.14) * mm, v(-311.07, 64.05) * mm, v(-310.9, 64.05) * mm]});
            skFitSpline(sketch, "E1757", {"points": [v(-311.33, 64.3) * mm, v(-311.43, 64.48) * mm, v(-311.64, 64.57) * mm, v(-311.84, 64.54) * mm]});
            skFitSpline(sketch, "E1758", {"points": [v(-311.84, 64.54) * mm, v(-312.05, 64.5) * mm, v(-312.21, 64.34) * mm, v(-312.25, 64.13) * mm]});
            skFitSpline(sketch, "E1759", {"points": [v(-312.25, 64.13) * mm, v(-312.29, 63.93) * mm, v(-312.2, 63.72) * mm, v(-312, 63.61) * mm]});
            skFitSpline(sketch, "E1760", {"points": [v(-311.76, 63.18) * mm, v(-311.76, 63.36) * mm, v(-311.85, 63.52) * mm, v(-312, 63.61) * mm]});
            skLineSegment(sketch, "E1761", {"start": v(-173.46, 61.05) * mm, "end": v(-178.46, 61.05) * mm});
            skFitSpline(sketch, "E1762", {"points": [v(-312.26, 61.05) * mm, v(-311.98, 61.05) * mm, v(-311.76, 61.27) * mm, v(-311.76, 61.55) * mm]});
            skLineSegment(sketch, "E1763", {"start": v(-178.96, 61.55) * mm, "end": v(-178.96, 63.18) * mm});
            skFitSpline(sketch, "E1764", {"points": [v(-317.76, 61.55) * mm, v(-317.76, 61.27) * mm, v(-317.53, 61.05) * mm, v(-317.26, 61.05) * mm]});
            skLineSegment(sketch, "E1765", {"start": v(-179.83, 64.05) * mm, "end": v(-310.9, 64.05) * mm});
            skFitSpline(sketch, "E1766", {"points": [v(-317.5, 63.61) * mm, v(-317.66, 63.52) * mm, v(-317.76, 63.36) * mm, v(-317.76, 63.18) * mm]});
            skFitSpline(sketch, "E1767", {"points": [v(-317.5, 63.61) * mm, v(-317.33, 63.72) * mm, v(-317.23, 63.93) * mm, v(-317.27, 64.13) * mm]});
            skFitSpline(sketch, "E1768", {"points": [v(-317.27, 64.13) * mm, v(-317.3, 64.34) * mm, v(-317.46, 64.5) * mm, v(-317.67, 64.54) * mm]});
            skFitSpline(sketch, "E1769", {"points": [v(-317.67, 64.54) * mm, v(-317.88, 64.57) * mm, v(-318.09, 64.48) * mm, v(-318.2, 64.3) * mm]});
            skFitSpline(sketch, "E1770", {"points": [v(-318.62, 64.05) * mm, v(-318.45, 64.05) * mm, v(-318.28, 64.14) * mm, v(-318.2, 64.3) * mm]});
            skLineSegment(sketch, "E1771", {"start": v(-311.76, 63.18) * mm, "end": v(-311.76, 61.55) * mm});
            skFitSpline(sketch, "E1772", {"points": [v(-332.52, 64.3) * mm, v(-332.44, 64.14) * mm, v(-332.27, 64.05) * mm, v(-332.1, 64.05) * mm]});
            skFitSpline(sketch, "E1773", {"points": [v(-332.52, 64.3) * mm, v(-332.63, 64.48) * mm, v(-332.84, 64.57) * mm, v(-333.04, 64.54) * mm]});
            skFitSpline(sketch, "E1774", {"points": [v(-333.04, 64.54) * mm, v(-333.25, 64.5) * mm, v(-333.41, 64.34) * mm, v(-333.45, 64.13) * mm]});
            skFitSpline(sketch, "E1775", {"points": [v(-333.45, 64.13) * mm, v(-333.49, 63.93) * mm, v(-333.4, 63.72) * mm, v(-333.2, 63.61) * mm]});
            skFitSpline(sketch, "E1776", {"points": [v(-332.96, 63.18) * mm, v(-332.96, 63.36) * mm, v(-333.05, 63.52) * mm, v(-333.2, 63.61) * mm]});
            skLineSegment(sketch, "E1777", {"start": v(-312.26, 61.05) * mm, "end": v(-317.26, 61.05) * mm});
            skFitSpline(sketch, "E1778", {"points": [v(-333.46, 61.05) * mm, v(-333.33, 61.05) * mm, v(-333.2, 61.1) * mm, v(-333.1, 61.2) * mm]});
            skFitSpline(sketch, "E1779", {"points": [v(-333.1, 61.2) * mm, v(-333.01, 61.29) * mm, v(-332.96, 61.41) * mm, v(-332.96, 61.55) * mm]});
            skLineSegment(sketch, "E1780", {"start": v(-317.76, 61.55) * mm, "end": v(-317.76, 63.18) * mm});
            skFitSpline(sketch, "E1781", {"points": [v(-338.96, 61.55) * mm, v(-338.96, 61.41) * mm, v(-338.9, 61.29) * mm, v(-338.81, 61.2) * mm]});
            skFitSpline(sketch, "E1782", {"points": [v(-338.81, 61.2) * mm, v(-338.72, 61.1) * mm, v(-338.6, 61.05) * mm, v(-338.46, 61.05) * mm]});
            skLineSegment(sketch, "E1783", {"start": v(-318.62, 64.05) * mm, "end": v(-323.76, 64.05) * mm});
            skLineSegment(sketch, "E1784", {"start": v(-323.76, 64.05) * mm, "end": v(-323.76, 67.05) * mm});
            skLineSegment(sketch, "E1785", {"start": v(-323.76, 67.05) * mm, "end": v(-322.48, 67.05) * mm});
            skLineSegment(sketch, "E1786", {"start": v(-322.48, 67.05) * mm, "end": v(-322.48, 71.05) * mm});
            skLineSegment(sketch, "E1787", {"start": v(-322.48, 71.05) * mm, "end": v(-323.76, 71.05) * mm});
            skLineSegment(sketch, "E1788", {"start": v(-323.76, 71.05) * mm, "end": v(-323.76, 74.05) * mm});
            skLineSegment(sketch, "E1789", {"start": v(-323.76, 74.05) * mm, "end": v(-326.96, 74.05) * mm});
            skLineSegment(sketch, "E1790", {"start": v(-326.96, 74.05) * mm, "end": v(-326.96, 71.05) * mm});
            skLineSegment(sketch, "E1791", {"start": v(-326.96, 71.05) * mm, "end": v(-328.23, 71.05) * mm});
            skLineSegment(sketch, "E1792", {"start": v(-328.23, 71.05) * mm, "end": v(-328.23, 67.05) * mm});
            skLineSegment(sketch, "E1793", {"start": v(-328.23, 67.05) * mm, "end": v(-326.96, 67.05) * mm});
            skLineSegment(sketch, "E1794", {"start": v(-326.96, 67.05) * mm, "end": v(-326.96, 64.05) * mm});
            skLineSegment(sketch, "E1795", {"start": v(-326.96, 64.05) * mm, "end": v(-332.1, 64.05) * mm});
            skFitSpline(sketch, "E1796", {"points": [v(-338.7, 63.61) * mm, v(-338.86, 63.52) * mm, v(-338.96, 63.36) * mm, v(-338.96, 63.18) * mm]});
            skFitSpline(sketch, "E1797", {"points": [v(-338.7, 63.61) * mm, v(-338.53, 63.72) * mm, v(-338.43, 63.93) * mm, v(-338.47, 64.13) * mm]});
            skFitSpline(sketch, "E1798", {"points": [v(-338.47, 64.13) * mm, v(-338.5, 64.34) * mm, v(-338.66, 64.5) * mm, v(-338.87, 64.54) * mm]});
            skFitSpline(sketch, "E1799", {"points": [v(-338.87, 64.54) * mm, v(-339.08, 64.57) * mm, v(-339.29, 64.48) * mm, v(-339.4, 64.3) * mm]});
            skFitSpline(sketch, "E1800", {"points": [v(-339.82, 64.05) * mm, v(-339.65, 64.05) * mm, v(-339.48, 64.14) * mm, v(-339.4, 64.3) * mm]});
            skLineSegment(sketch, "E1801", {"start": v(-332.96, 63.18) * mm, "end": v(-332.96, 61.55) * mm});
            skFitSpline(sketch, "E1802", {"points": [v(-347.7, 74.45) * mm, v(-347.78, 74.6) * mm, v(-347.95, 74.7) * mm, v(-348.12, 74.7) * mm]});
            skFitSpline(sketch, "E1803", {"points": [v(-347.7, 74.45) * mm, v(-347.59, 74.26) * mm, v(-347.38, 74.17) * mm, v(-347.17, 74.2) * mm]});
            skFitSpline(sketch, "E1804", {"points": [v(-347.17, 74.2) * mm, v(-346.96, 74.24) * mm, v(-346.8, 74.4) * mm, v(-346.77, 74.6) * mm]});
            skFitSpline(sketch, "E1805", {"points": [v(-346.77, 74.6) * mm, v(-346.73, 74.82) * mm, v(-346.83, 75.02) * mm, v(-347, 75.13) * mm]});
            skFitSpline(sketch, "E1806", {"points": [v(-347.26, 75.56) * mm, v(-347.26, 75.38) * mm, v(-347.16, 75.22) * mm, v(-347, 75.13) * mm]});
            skLineSegment(sketch, "E1807", {"start": v(-333.46, 61.05) * mm, "end": v(-338.46, 61.05) * mm});
            skLineSegment(sketch, "E1808", {"start": v(-338.96, 61.55) * mm, "end": v(-338.96, 63.18) * mm});
            skLineSegment(sketch, "E1809", {"start": v(-339.82, 64.05) * mm, "end": v(-350.36, 64.05) * mm});
            skLineSegment(sketch, "E1810", {"start": v(-350.36, 64.05) * mm, "end": v(-350.36, 74.7) * mm});
            skLineSegment(sketch, "E1811", {"start": v(-350.36, 74.7) * mm, "end": v(-348.12, 74.7) * mm});
            skFitSpline(sketch, "E1812", {"points": [v(-321.36, 88.05) * mm, v(-322.79, 88.05) * mm, v(-324.1, 87.28) * mm, v(-324.82, 86.05) * mm]});
            skFitSpline(sketch, "E1813", {"points": [v(-324.82, 86.05) * mm, v(-325.54, 84.8) * mm, v(-325.54, 83.28) * mm, v(-324.82, 82.05) * mm]});
            skFitSpline(sketch, "E1814", {"points": [v(-324.82, 82.05) * mm, v(-324.1, 80.8) * mm, v(-322.79, 80.05) * mm, v(-321.36, 80.05) * mm]});
            skLineSegment(sketch, "E1815", {"start": v(-347.26, 75.56) * mm, "end": v(-347.26, 83.1) * mm});
            skLineSegment(sketch, "E1816", {"start": v(-347.26, 83.1) * mm, "end": v(-344.26, 83.1) * mm});
            skLineSegment(sketch, "E1817", {"start": v(-344.26, 83.1) * mm, "end": v(-344.26, 81.82) * mm});
            skLineSegment(sketch, "E1818", {"start": v(-344.26, 81.82) * mm, "end": v(-340.26, 81.82) * mm});
            skLineSegment(sketch, "E1819", {"start": v(-340.26, 81.82) * mm, "end": v(-340.26, 83.1) * mm});
            skLineSegment(sketch, "E1820", {"start": v(-340.26, 83.1) * mm, "end": v(-337.26, 83.1) * mm});
            skLineSegment(sketch, "E1821", {"start": v(-337.26, 83.1) * mm, "end": v(-337.26, 86.3) * mm});
            skLineSegment(sketch, "E1822", {"start": v(-337.26, 86.3) * mm, "end": v(-340.26, 86.3) * mm});
            skLineSegment(sketch, "E1823", {"start": v(-340.26, 86.3) * mm, "end": v(-340.26, 87.57) * mm});
            skLineSegment(sketch, "E1824", {"start": v(-340.26, 87.57) * mm, "end": v(-344.26, 87.57) * mm});
            skLineSegment(sketch, "E1825", {"start": v(-344.26, 87.57) * mm, "end": v(-344.26, 86.3) * mm});
            skLineSegment(sketch, "E1826", {"start": v(-344.26, 86.3) * mm, "end": v(-347.26, 86.3) * mm});
            skLineSegment(sketch, "E1827", {"start": v(-347.26, 86.3) * mm, "end": v(-347.26, 95.04) * mm});
            skLineSegment(sketch, "E1828", {"start": v(-347.26, 95.04) * mm, "end": v(-25.17, 188.94) * mm});
            skFitSpline(sketch, "E1829", {"points": [v(-313.36, 80.05) * mm, v(-311.93, 80.05) * mm, v(-310.6, 80.8) * mm, v(-309.9, 82.05) * mm]});
            skFitSpline(sketch, "E1830", {"points": [v(-309.9, 82.05) * mm, v(-309.18, 83.28) * mm, v(-309.18, 84.8) * mm, v(-309.9, 86.05) * mm]});
            skFitSpline(sketch, "E1831", {"points": [v(-309.9, 86.05) * mm, v(-310.6, 87.28) * mm, v(-311.93, 88.05) * mm, v(-313.36, 88.05) * mm]});
            skLineSegment(sketch, "E1832", {"start": v(-24.81, 194.04) * mm, "end": v(-19.83, 194.04) * mm});
            skFitSpline(sketch, "E1833", {"points": [v(-261.36, 88.05) * mm, v(-262.79, 88.05) * mm, v(-264.1, 87.28) * mm, v(-264.82, 86.05) * mm]});
            skFitSpline(sketch, "E1834", {"points": [v(-264.82, 86.05) * mm, v(-265.54, 84.8) * mm, v(-265.54, 83.28) * mm, v(-264.82, 82.05) * mm]});
            skFitSpline(sketch, "E1835", {"points": [v(-264.82, 82.05) * mm, v(-264.1, 80.8) * mm, v(-262.79, 80.05) * mm, v(-261.36, 80.05) * mm]});
            skLineSegment(sketch, "E1836", {"start": v(-313.36, 88.05) * mm, "end": v(-321.36, 88.05) * mm});
            skFitSpline(sketch, "E1837", {"points": [v(-253.36, 80.05) * mm, v(-251.93, 80.05) * mm, v(-250.6, 80.8) * mm, v(-249.9, 82.05) * mm]});
            skFitSpline(sketch, "E1838", {"points": [v(-249.9, 82.05) * mm, v(-249.18, 83.28) * mm, v(-249.18, 84.8) * mm, v(-249.9, 86.05) * mm]});
            skFitSpline(sketch, "E1839", {"points": [v(-249.9, 86.05) * mm, v(-250.6, 87.28) * mm, v(-251.93, 88.05) * mm, v(-253.36, 88.05) * mm]});
            skLineSegment(sketch, "E1840", {"start": v(-321.36, 80.05) * mm, "end": v(-313.36, 80.05) * mm});
            skFitSpline(sketch, "E1841", {"points": [v(-201.36, 88.05) * mm, v(-202.79, 88.05) * mm, v(-204.1, 87.28) * mm, v(-204.82, 86.05) * mm]});
            skFitSpline(sketch, "E1842", {"points": [v(-204.82, 86.05) * mm, v(-205.54, 84.8) * mm, v(-205.54, 83.28) * mm, v(-204.82, 82.05) * mm]});
            skFitSpline(sketch, "E1843", {"points": [v(-204.82, 82.05) * mm, v(-204.1, 80.8) * mm, v(-202.79, 80.05) * mm, v(-201.36, 80.05) * mm]});
            skLineSegment(sketch, "E1844", {"start": v(-253.36, 88.05) * mm, "end": v(-261.36, 88.05) * mm});
            skFitSpline(sketch, "E1845", {"points": [v(-193.36, 80.05) * mm, v(-191.93, 80.05) * mm, v(-190.6, 80.8) * mm, v(-189.9, 82.05) * mm]});
            skFitSpline(sketch, "E1846", {"points": [v(-189.9, 82.05) * mm, v(-189.18, 83.28) * mm, v(-189.18, 84.8) * mm, v(-189.9, 86.05) * mm]});
            skFitSpline(sketch, "E1847", {"points": [v(-189.9, 86.05) * mm, v(-190.6, 87.28) * mm, v(-191.93, 88.05) * mm, v(-193.36, 88.05) * mm]});
            skLineSegment(sketch, "E1848", {"start": v(-261.36, 80.05) * mm, "end": v(-253.36, 80.05) * mm});
            skFitSpline(sketch, "E1849", {"points": [v(-141.36, 88.05) * mm, v(-142.79, 88.05) * mm, v(-144.1, 87.28) * mm, v(-144.82, 86.05) * mm]});
            skFitSpline(sketch, "E1850", {"points": [v(-144.82, 86.05) * mm, v(-145.54, 84.8) * mm, v(-145.54, 83.28) * mm, v(-144.82, 82.05) * mm]});
            skFitSpline(sketch, "E1851", {"points": [v(-144.82, 82.05) * mm, v(-144.1, 80.8) * mm, v(-142.79, 80.05) * mm, v(-141.36, 80.05) * mm]});
            skLineSegment(sketch, "E1852", {"start": v(-193.36, 88.05) * mm, "end": v(-201.36, 88.05) * mm});
            skFitSpline(sketch, "E1853", {"points": [v(-133.36, 80.05) * mm, v(-131.93, 80.05) * mm, v(-130.61, 80.8) * mm, v(-129.9, 82.05) * mm]});
            skFitSpline(sketch, "E1854", {"points": [v(-129.9, 82.05) * mm, v(-129.18, 83.28) * mm, v(-129.18, 84.8) * mm, v(-129.9, 86.05) * mm]});
            skFitSpline(sketch, "E1855", {"points": [v(-129.9, 86.05) * mm, v(-130.61, 87.28) * mm, v(-131.93, 88.05) * mm, v(-133.36, 88.05) * mm]});
            skLineSegment(sketch, "E1856", {"start": v(-201.36, 80.05) * mm, "end": v(-193.36, 80.05) * mm});
            skFitSpline(sketch, "E1857", {"points": [v(-73.36, 87.05) * mm, v(-73.36, 88.47) * mm, v(-74.12, 89.8) * mm, v(-75.36, 90.5) * mm]});
            skFitSpline(sketch, "E1858", {"points": [v(-75.36, 90.5) * mm, v(-76.6, 91.22) * mm, v(-78.12, 91.22) * mm, v(-79.36, 90.5) * mm]});
            skFitSpline(sketch, "E1859", {"points": [v(-79.36, 90.5) * mm, v(-80.6, 89.8) * mm, v(-81.36, 88.47) * mm, v(-81.36, 87.05) * mm]});
            skLineSegment(sketch, "E1860", {"start": v(-133.36, 88.05) * mm, "end": v(-141.36, 88.05) * mm});
            skFitSpline(sketch, "E1861", {"points": [v(-81.36, 79.05) * mm, v(-81.36, 77.62) * mm, v(-80.6, 76.3) * mm, v(-79.36, 75.58) * mm]});
            skFitSpline(sketch, "E1862", {"points": [v(-79.36, 75.58) * mm, v(-78.12, 74.87) * mm, v(-76.6, 74.87) * mm, v(-75.36, 75.58) * mm]});
            skFitSpline(sketch, "E1863", {"points": [v(-75.36, 75.58) * mm, v(-74.12, 76.3) * mm, v(-73.36, 77.62) * mm, v(-73.36, 79.05) * mm]});
            skLineSegment(sketch, "E1864", {"start": v(-141.36, 80.05) * mm, "end": v(-133.36, 80.05) * mm});
            skFitSpline(sketch, "E1865", {"points": [v(-73.36, 127.05) * mm, v(-73.36, 128.47) * mm, v(-74.12, 129.8) * mm, v(-75.36, 130.5) * mm]});
            skFitSpline(sketch, "E1866", {"points": [v(-75.36, 130.5) * mm, v(-76.6, 131.22) * mm, v(-78.12, 131.22) * mm, v(-79.36, 130.5) * mm]});
            skFitSpline(sketch, "E1867", {"points": [v(-79.36, 130.5) * mm, v(-80.6, 129.8) * mm, v(-81.36, 128.47) * mm, v(-81.36, 127.05) * mm]});
            skLineSegment(sketch, "E1868", {"start": v(-73.36, 79.05) * mm, "end": v(-73.36, 87.05) * mm});
            skFitSpline(sketch, "E1869", {"points": [v(-81.36, 119.05) * mm, v(-81.36, 117.62) * mm, v(-80.6, 116.3) * mm, v(-79.36, 115.58) * mm]});
            skFitSpline(sketch, "E1870", {"points": [v(-79.36, 115.58) * mm, v(-78.12, 114.87) * mm, v(-76.6, 114.87) * mm, v(-75.36, 115.58) * mm]});
            skFitSpline(sketch, "E1871", {"points": [v(-75.36, 115.58) * mm, v(-74.12, 116.3) * mm, v(-73.36, 117.62) * mm, v(-73.36, 119.05) * mm]});
            skLineSegment(sketch, "E1872", {"start": v(-81.36, 87.05) * mm, "end": v(-81.36, 79.05) * mm});
            skFitSpline(sketch, "E1873", {"points": [v(11.64, 87.05) * mm, v(11.64, 88.47) * mm, v(10.88, 89.8) * mm, v(9.64, 90.5) * mm]});
            skFitSpline(sketch, "E1874", {"points": [v(9.64, 90.5) * mm, v(8.4, 91.22) * mm, v(6.88, 91.22) * mm, v(5.64, 90.5) * mm]});
            skFitSpline(sketch, "E1875", {"points": [v(5.64, 90.5) * mm, v(4.4, 89.8) * mm, v(3.64, 88.47) * mm, v(3.64, 87.05) * mm]});
            skLineSegment(sketch, "E1876", {"start": v(-73.36, 119.05) * mm, "end": v(-73.36, 127.05) * mm});
            skFitSpline(sketch, "E1877", {"points": [v(3.64, 79.05) * mm, v(3.64, 77.62) * mm, v(4.4, 76.3) * mm, v(5.64, 75.58) * mm]});
            skFitSpline(sketch, "E1878", {"points": [v(5.64, 75.58) * mm, v(6.88, 74.87) * mm, v(8.4, 74.87) * mm, v(9.64, 75.58) * mm]});
            skFitSpline(sketch, "E1879", {"points": [v(9.64, 75.58) * mm, v(10.88, 76.3) * mm, v(11.64, 77.62) * mm, v(11.64, 79.05) * mm]});
            skLineSegment(sketch, "E1880", {"start": v(-81.36, 127.05) * mm, "end": v(-81.36, 119.05) * mm});
            skFitSpline(sketch, "E1881", {"points": [v(11.64, 127.05) * mm, v(11.64, 128.47) * mm, v(10.88, 129.8) * mm, v(9.64, 130.5) * mm]});
            skFitSpline(sketch, "E1882", {"points": [v(9.64, 130.5) * mm, v(8.4, 131.22) * mm, v(6.88, 131.22) * mm, v(5.64, 130.5) * mm]});
            skFitSpline(sketch, "E1883", {"points": [v(5.64, 130.5) * mm, v(4.4, 129.8) * mm, v(3.64, 128.47) * mm, v(3.64, 127.05) * mm]});
            skLineSegment(sketch, "E1884", {"start": v(11.64, 79.05) * mm, "end": v(11.64, 87.05) * mm});
            skFitSpline(sketch, "E1885", {"points": [v(3.64, 119.05) * mm, v(3.64, 117.62) * mm, v(4.4, 116.3) * mm, v(5.64, 115.58) * mm]});
            skFitSpline(sketch, "E1886", {"points": [v(5.64, 115.58) * mm, v(6.88, 114.87) * mm, v(8.4, 114.87) * mm, v(9.64, 115.58) * mm]});
            skFitSpline(sketch, "E1887", {"points": [v(9.64, 115.58) * mm, v(10.88, 116.3) * mm, v(11.64, 117.62) * mm, v(11.64, 119.05) * mm]});
            skLineSegment(sketch, "E1888", {"start": v(3.64, 87.05) * mm, "end": v(3.64, 79.05) * mm});
            skFitSpline(sketch, "E1889", {"points": [v(11.64, 167.04) * mm, v(11.64, 168.47) * mm, v(10.88, 169.8) * mm, v(9.64, 170.5) * mm]});
            skFitSpline(sketch, "E1890", {"points": [v(9.64, 170.5) * mm, v(8.4, 171.22) * mm, v(6.88, 171.22) * mm, v(5.64, 170.5) * mm]});
            skFitSpline(sketch, "E1891", {"points": [v(5.64, 170.5) * mm, v(4.4, 169.8) * mm, v(3.64, 168.47) * mm, v(3.64, 167.04) * mm]});
            skLineSegment(sketch, "E1892", {"start": v(11.64, 119.05) * mm, "end": v(11.64, 127.05) * mm});
            skFitSpline(sketch, "E1893", {"points": [v(3.64, 159.04) * mm, v(3.64, 157.62) * mm, v(4.4, 156.3) * mm, v(5.64, 155.58) * mm]});
            skFitSpline(sketch, "E1894", {"points": [v(5.64, 155.58) * mm, v(6.88, 154.87) * mm, v(8.4, 154.87) * mm, v(9.64, 155.58) * mm]});
            skFitSpline(sketch, "E1895", {"points": [v(9.64, 155.58) * mm, v(10.88, 156.3) * mm, v(11.64, 157.62) * mm, v(11.64, 159.04) * mm]});
            skFitSpline(sketch, "E1896", {"points": [v(-7.9, 76.83) * mm, v(-7.9, 77.3) * mm, v(-8.15, 77.73) * mm, v(-8.55, 77.96) * mm]});
            skFitSpline(sketch, "E1897", {"points": [v(-8.55, 77.96) * mm, v(-8.95, 78.2) * mm, v(-9.45, 78.2) * mm, v(-9.85, 77.96) * mm]});
            skFitSpline(sketch, "E1898", {"points": [v(-9.85, 77.96) * mm, v(-10.25, 77.73) * mm, v(-10.5, 77.3) * mm, v(-10.5, 76.83) * mm]});
            skFitSpline(sketch, "E1899", {"points": [v(-10.5, 76.83) * mm, v(-10.5, 76.37) * mm, v(-10.25, 75.94) * mm, v(-9.85, 75.7) * mm]});
            skFitSpline(sketch, "E1900", {"points": [v(-9.85, 75.7) * mm, v(-9.45, 75.48) * mm, v(-8.95, 75.48) * mm, v(-8.55, 75.7) * mm]});
            skFitSpline(sketch, "E1901", {"points": [v(-8.55, 75.7) * mm, v(-8.15, 75.94) * mm, v(-7.9, 76.37) * mm, v(-7.9, 76.83) * mm]});
            skLineSegment(sketch, "E1902", {"start": v(3.64, 127.05) * mm, "end": v(3.64, 119.05) * mm});
            skFitSpline(sketch, "E1903", {"points": [v(-7.88, 160.03) * mm, v(-7.88, 160.5) * mm, v(-8.13, 160.93) * mm, v(-8.53, 161.16) * mm]});
            skFitSpline(sketch, "E1904", {"points": [v(-8.53, 161.16) * mm, v(-8.93, 161.4) * mm, v(-9.43, 161.4) * mm, v(-9.83, 161.16) * mm]});
            skFitSpline(sketch, "E1905", {"points": [v(-9.83, 161.16) * mm, v(-10.23, 160.93) * mm, v(-10.48, 160.5) * mm, v(-10.48, 160.03) * mm]});
            skFitSpline(sketch, "E1906", {"points": [v(-10.48, 160.03) * mm, v(-10.48, 159.57) * mm, v(-10.23, 159.14) * mm, v(-9.83, 158.9) * mm]});
            skFitSpline(sketch, "E1907", {"points": [v(-9.83, 158.9) * mm, v(-9.43, 158.68) * mm, v(-8.93, 158.68) * mm, v(-8.53, 158.9) * mm]});
            skFitSpline(sketch, "E1908", {"points": [v(-8.53, 158.9) * mm, v(-8.13, 159.14) * mm, v(-7.88, 159.57) * mm, v(-7.88, 160.03) * mm]});
            skLineSegment(sketch, "E1909", {"start": v(11.64, 159.04) * mm, "end": v(11.64, 167.04) * mm});
            skFitSpline(sketch, "E1910", {"points": [v(-56.1, 83.06) * mm, v(-56.1, 83.52) * mm, v(-56.34, 83.95) * mm, v(-56.74, 84.19) * mm]});
            skFitSpline(sketch, "E1911", {"points": [v(-56.74, 84.19) * mm, v(-57.14, 84.42) * mm, v(-57.64, 84.42) * mm, v(-58.04, 84.19) * mm]});
            skFitSpline(sketch, "E1912", {"points": [v(-58.04, 84.19) * mm, v(-58.45, 83.95) * mm, v(-58.7, 83.52) * mm, v(-58.7, 83.06) * mm]});
            skFitSpline(sketch, "E1913", {"points": [v(-58.7, 83.06) * mm, v(-58.7, 82.6) * mm, v(-58.45, 82.16) * mm, v(-58.04, 81.93) * mm]});
            skFitSpline(sketch, "E1914", {"points": [v(-58.04, 81.93) * mm, v(-57.64, 81.7) * mm, v(-57.14, 81.7) * mm, v(-56.74, 81.93) * mm]});
            skFitSpline(sketch, "E1915", {"points": [v(-56.74, 81.93) * mm, v(-56.34, 82.16) * mm, v(-56.1, 82.6) * mm, v(-56.1, 83.06) * mm]});
            skLineSegment(sketch, "E1916", {"start": v(3.64, 167.04) * mm, "end": v(3.64, 159.04) * mm});
            skFitSpline(sketch, "E1917", {"points": [v(-56.08, 157.56) * mm, v(-56.08, 158.02) * mm, v(-56.32, 158.45) * mm, v(-56.73, 158.68) * mm]});
            skFitSpline(sketch, "E1918", {"points": [v(-56.73, 158.68) * mm, v(-57.13, 158.91) * mm, v(-57.62, 158.91) * mm, v(-58.03, 158.68) * mm]});
            skFitSpline(sketch, "E1919", {"points": [v(-58.03, 158.68) * mm, v(-58.43, 158.45) * mm, v(-58.68, 158.02) * mm, v(-58.68, 157.56) * mm]});
            skFitSpline(sketch, "E1920", {"points": [v(-58.68, 157.56) * mm, v(-58.68, 157.1) * mm, v(-58.43, 156.66) * mm, v(-58.03, 156.43) * mm]});
            skFitSpline(sketch, "E1921", {"points": [v(-58.03, 156.43) * mm, v(-57.62, 156.2) * mm, v(-57.13, 156.2) * mm, v(-56.73, 156.43) * mm]});
            skFitSpline(sketch, "E1922", {"points": [v(-56.73, 156.43) * mm, v(-56.32, 156.66) * mm, v(-56.08, 157.1) * mm, v(-56.08, 157.56) * mm]});
            skFitSpline(sketch, "E1923", {"points": [v(-4.58, -6.45) * mm, v(-4.4, -6.45) * mm, v(-4.23, -6.36) * mm, v(-4.14, -6.2) * mm]});
            skFitSpline(sketch, "E1924", {"points": [v(-3.46, -6.89) * mm, v(-3.28, -6.78) * mm, v(-3.18, -6.57) * mm, v(-3.22, -6.37) * mm]});
            skFitSpline(sketch, "E1925", {"points": [v(-3.22, -6.37) * mm, v(-3.26, -6.16) * mm, v(-3.42, -6) * mm, v(-3.62, -5.96) * mm]});
            skFitSpline(sketch, "E1926", {"points": [v(-3.62, -5.96) * mm, v(-3.83, -5.92) * mm, v(-4.04, -6.02) * mm, v(-4.14, -6.2) * mm]});
            skFitSpline(sketch, "E1927", {"points": [v(-3.46, -6.89) * mm, v(-3.62, -6.98) * mm, v(-3.71, -7.14) * mm, v(-3.71, -7.32) * mm]});
            skFitSpline(sketch, "E1928", {"points": [v(-3.71, -11.79) * mm, v(-3.71, -11.97) * mm, v(-3.62, -12.13) * mm, v(-3.46, -12.22) * mm]});
            skFitSpline(sketch, "E1929", {"points": [v(-4.14, -12.9) * mm, v(-4.04, -13.09) * mm, v(-3.83, -13.18) * mm, v(-3.62, -13.15) * mm]});
            skFitSpline(sketch, "E1930", {"points": [v(-3.62, -13.15) * mm, v(-3.42, -13.1) * mm, v(-3.26, -12.95) * mm, v(-3.22, -12.74) * mm]});
            skFitSpline(sketch, "E1931", {"points": [v(-3.22, -12.74) * mm, v(-3.18, -12.53) * mm, v(-3.28, -12.33) * mm, v(-3.46, -12.22) * mm]});
            skFitSpline(sketch, "E1932", {"points": [v(-4.14, -12.9) * mm, v(-4.23, -12.75) * mm, v(-4.4, -12.65) * mm, v(-4.58, -12.65) * mm]});
            skFitSpline(sketch, "E1933", {"points": [v(-6.15, -12.65) * mm, v(-6.32, -12.65) * mm, v(-6.49, -12.75) * mm, v(-6.58, -12.9) * mm]});
            skFitSpline(sketch, "E1934", {"points": [v(-7.26, -12.22) * mm, v(-7.44, -12.33) * mm, v(-7.54, -12.53) * mm, v(-7.5, -12.74) * mm]});
            skFitSpline(sketch, "E1935", {"points": [v(-7.5, -12.74) * mm, v(-7.47, -12.95) * mm, v(-7.3, -13.1) * mm, v(-7.1, -13.15) * mm]});
            skFitSpline(sketch, "E1936", {"points": [v(-7.1, -13.15) * mm, v(-6.9, -13.18) * mm, v(-6.68, -13.09) * mm, v(-6.58, -12.9) * mm]});
            skFitSpline(sketch, "E1937", {"points": [v(-7.26, -12.22) * mm, v(-7.1, -12.13) * mm, v(-7.01, -11.97) * mm, v(-7.01, -11.79) * mm]});
            skLineSegment(sketch, "E1938", {"start": v(8.22, 63.2) * mm, "end": v(8.22, -188.46) * mm});
            skLineSegment(sketch, "E1939", {"start": v(8.22, -188.46) * mm, "end": v(8.21, -192.45) * mm});
            skFitSpline(sketch, "E1940", {"points": [v(-7.01, -7.32) * mm, v(-7.01, -7.14) * mm, v(-7.1, -6.98) * mm, v(-7.26, -6.89) * mm]});
            skFitSpline(sketch, "E1941", {"points": [v(-6.58, -6.2) * mm, v(-6.68, -6.02) * mm, v(-6.9, -5.92) * mm, v(-7.1, -5.96) * mm]});
            skFitSpline(sketch, "E1942", {"points": [v(-7.1, -5.96) * mm, v(-7.3, -6) * mm, v(-7.47, -6.16) * mm, v(-7.5, -6.37) * mm]});
            skFitSpline(sketch, "E1943", {"points": [v(-7.5, -6.37) * mm, v(-7.54, -6.57) * mm, v(-7.44, -6.78) * mm, v(-7.26, -6.89) * mm]});
            skFitSpline(sketch, "E1944", {"points": [v(-6.58, -6.2) * mm, v(-6.49, -6.36) * mm, v(-6.32, -6.45) * mm, v(-6.15, -6.45) * mm]});
            skLineSegment(sketch, "E1945", {"start": v(-3.71, -7.32) * mm, "end": v(-3.71, -11.79) * mm});
            skFitSpline(sketch, "E1946", {"points": [v(-4.58, 14.75) * mm, v(-4.4, 14.75) * mm, v(-4.23, 14.84) * mm, v(-4.14, 15) * mm]});
            skFitSpline(sketch, "E1947", {"points": [v(-3.46, 14.31) * mm, v(-3.28, 14.42) * mm, v(-3.18, 14.63) * mm, v(-3.22, 14.83) * mm]});
            skFitSpline(sketch, "E1948", {"points": [v(-3.22, 14.83) * mm, v(-3.26, 15.04) * mm, v(-3.42, 15.2) * mm, v(-3.62, 15.24) * mm]});
            skFitSpline(sketch, "E1949", {"points": [v(-3.62, 15.24) * mm, v(-3.83, 15.28) * mm, v(-4.04, 15.18) * mm, v(-4.14, 15) * mm]});
            skFitSpline(sketch, "E1950", {"points": [v(-3.46, 14.31) * mm, v(-3.62, 14.22) * mm, v(-3.71, 14.06) * mm, v(-3.71, 13.88) * mm]});
            skLineSegment(sketch, "E1951", {"start": v(-4.58, -12.65) * mm, "end": v(-6.15, -12.65) * mm});
            skFitSpline(sketch, "E1952", {"points": [v(-3.71, 9.41) * mm, v(-3.71, 9.23) * mm, v(-3.62, 9.07) * mm, v(-3.46, 8.98) * mm]});
            skFitSpline(sketch, "E1953", {"points": [v(-4.14, 8.3) * mm, v(-4.04, 8.11) * mm, v(-3.83, 8.02) * mm, v(-3.62, 8.05) * mm]});
            skFitSpline(sketch, "E1954", {"points": [v(-3.62, 8.05) * mm, v(-3.42, 8.1) * mm, v(-3.26, 8.25) * mm, v(-3.22, 8.46) * mm]});
            skFitSpline(sketch, "E1955", {"points": [v(-3.22, 8.46) * mm, v(-3.18, 8.67) * mm, v(-3.28, 8.87) * mm, v(-3.46, 8.98) * mm]});
            skFitSpline(sketch, "E1956", {"points": [v(-4.14, 8.3) * mm, v(-4.23, 8.45) * mm, v(-4.4, 8.55) * mm, v(-4.58, 8.55) * mm]});
            skLineSegment(sketch, "E1957", {"start": v(-7.01, -11.79) * mm, "end": v(-7.01, -7.32) * mm});
            skFitSpline(sketch, "E1958", {"points": [v(-6.15, 8.55) * mm, v(-6.32, 8.55) * mm, v(-6.49, 8.45) * mm, v(-6.58, 8.3) * mm]});
            skFitSpline(sketch, "E1959", {"points": [v(-7.26, 8.98) * mm, v(-7.44, 8.87) * mm, v(-7.54, 8.67) * mm, v(-7.5, 8.46) * mm]});
            skFitSpline(sketch, "E1960", {"points": [v(-7.5, 8.46) * mm, v(-7.47, 8.25) * mm, v(-7.3, 8.1) * mm, v(-7.1, 8.05) * mm]});
            skFitSpline(sketch, "E1961", {"points": [v(-7.1, 8.05) * mm, v(-6.9, 8.02) * mm, v(-6.68, 8.11) * mm, v(-6.58, 8.3) * mm]});
            skFitSpline(sketch, "E1962", {"points": [v(-7.26, 8.98) * mm, v(-7.1, 9.07) * mm, v(-7.01, 9.23) * mm, v(-7.01, 9.41) * mm]});
            skLineSegment(sketch, "E1963", {"start": v(-6.15, -6.45) * mm, "end": v(-4.58, -6.45) * mm});
            skFitSpline(sketch, "E1964", {"points": [v(-7.01, 13.88) * mm, v(-7.01, 14.06) * mm, v(-7.1, 14.22) * mm, v(-7.26, 14.31) * mm]});
            skFitSpline(sketch, "E1965", {"points": [v(-6.58, 15) * mm, v(-6.68, 15.18) * mm, v(-6.9, 15.28) * mm, v(-7.1, 15.24) * mm]});
            skFitSpline(sketch, "E1966", {"points": [v(-7.1, 15.24) * mm, v(-7.3, 15.2) * mm, v(-7.47, 15.04) * mm, v(-7.5, 14.83) * mm]});
            skFitSpline(sketch, "E1967", {"points": [v(-7.5, 14.83) * mm, v(-7.54, 14.63) * mm, v(-7.44, 14.42) * mm, v(-7.26, 14.31) * mm]});
            skFitSpline(sketch, "E1968", {"points": [v(-6.58, 15) * mm, v(-6.49, 14.84) * mm, v(-6.32, 14.75) * mm, v(-6.15, 14.75) * mm]});
            skLineSegment(sketch, "E1969", {"start": v(-3.71, 13.88) * mm, "end": v(-3.71, 9.41) * mm});
            skFitSpline(sketch, "E1970", {"points": [v(-3.76, 1.05) * mm, v(-3.76, 1.62) * mm, v(-4.07, 2.15) * mm, v(-4.56, 2.43) * mm]});
            skFitSpline(sketch, "E1971", {"points": [v(-4.56, 2.43) * mm, v(-5.06, 2.72) * mm, v(-5.67, 2.72) * mm, v(-6.16, 2.43) * mm]});
            skFitSpline(sketch, "E1972", {"points": [v(-6.16, 2.43) * mm, v(-6.66, 2.15) * mm, v(-6.96, 1.62) * mm, v(-6.96, 1.05) * mm]});
            skFitSpline(sketch, "E1973", {"points": [v(-6.96, 1.05) * mm, v(-6.96, 0.16) * mm, v(-6.24, -0.55) * mm, v(-5.36, -0.55) * mm]});
            skFitSpline(sketch, "E1974", {"points": [v(-5.36, -0.55) * mm, v(-4.48, -0.55) * mm, v(-3.76, 0.16) * mm, v(-3.76, 1.05) * mm]});
            skLineSegment(sketch, "E1975", {"start": v(-4.58, 8.55) * mm, "end": v(-6.15, 8.55) * mm});
            skLineSegment(sketch, "E1976", {"start": v(-7.01, 9.41) * mm, "end": v(-7.01, 13.88) * mm});
            skFitSpline(sketch, "E1977", {"points": [v(-198.78, 173.82) * mm, v(-198.78, 174) * mm, v(-198.88, 174.17) * mm, v(-199.03, 174.26) * mm]});
            skFitSpline(sketch, "E1978", {"points": [v(-198.35, 174.94) * mm, v(-198.46, 175.12) * mm, v(-198.66, 175.22) * mm, v(-198.87, 175.18) * mm]});
            skFitSpline(sketch, "E1979", {"points": [v(-198.87, 175.18) * mm, v(-199.08, 175.15) * mm, v(-199.24, 174.98) * mm, v(-199.28, 174.78) * mm]});
            skFitSpline(sketch, "E1980", {"points": [v(-199.28, 174.78) * mm, v(-199.31, 174.57) * mm, v(-199.22, 174.36) * mm, v(-199.03, 174.26) * mm]});
            skFitSpline(sketch, "E1981", {"points": [v(-198.35, 174.94) * mm, v(-198.26, 174.79) * mm, v(-198.1, 174.7) * mm, v(-197.92, 174.7) * mm]});
            skLineSegment(sketch, "E1982", {"start": v(-6.15, 14.75) * mm, "end": v(-4.58, 14.75) * mm});
            skFitSpline(sketch, "E1983", {"points": [v(-196.28, 174.7) * mm, v(-196, 174.7) * mm, v(-195.78, 174.91) * mm, v(-195.78, 175.2) * mm]});
            skFitSpline(sketch, "E1984", {"points": [v(-195.78, 180.2) * mm, v(-195.78, 180.47) * mm, v(-196, 180.7) * mm, v(-196.28, 180.7) * mm]});
            skLineSegment(sketch, "E1985", {"start": v(-208.78, 165.5) * mm, "end": v(-208.78, 168.7) * mm});
            skLineSegment(sketch, "E1986", {"start": v(-208.78, 168.7) * mm, "end": v(-205.78, 168.7) * mm});
            skLineSegment(sketch, "E1987", {"start": v(-205.78, 168.7) * mm, "end": v(-205.78, 169.97) * mm});
            skLineSegment(sketch, "E1988", {"start": v(-205.78, 169.97) * mm, "end": v(-201.78, 169.97) * mm});
            skLineSegment(sketch, "E1989", {"start": v(-201.78, 169.97) * mm, "end": v(-201.78, 168.7) * mm});
            skLineSegment(sketch, "E1990", {"start": v(-201.78, 168.7) * mm, "end": v(-198.78, 168.7) * mm});
            skLineSegment(sketch, "E1991", {"start": v(-198.78, 168.7) * mm, "end": v(-198.78, 173.82) * mm});
            skFitSpline(sketch, "E1992", {"points": [v(-197.92, 180.7) * mm, v(-198.1, 180.7) * mm, v(-198.26, 180.6) * mm, v(-198.35, 180.44) * mm]});
            skFitSpline(sketch, "E1993", {"points": [v(-199.03, 181.12) * mm, v(-199.22, 181.02) * mm, v(-199.31, 180.81) * mm, v(-199.28, 180.6) * mm]});
            skFitSpline(sketch, "E1994", {"points": [v(-199.28, 180.6) * mm, v(-199.24, 180.4) * mm, v(-199.08, 180.23) * mm, v(-198.87, 180.2) * mm]});
            skFitSpline(sketch, "E1995", {"points": [v(-198.87, 180.2) * mm, v(-198.66, 180.16) * mm, v(-198.46, 180.26) * mm, v(-198.35, 180.44) * mm]});
            skFitSpline(sketch, "E1996", {"points": [v(-199.03, 181.12) * mm, v(-198.88, 181.21) * mm, v(-198.78, 181.38) * mm, v(-198.78, 181.56) * mm]});
            skLineSegment(sketch, "E1997", {"start": v(-197.92, 174.7) * mm, "end": v(-196.28, 174.7) * mm});
            skLineSegment(sketch, "E1998", {"start": v(-195.78, 175.2) * mm, "end": v(-195.78, 180.2) * mm});
            skFitSpline(sketch, "E1999", {"points": [v(-244.78, 181.1) * mm, v(-245.31, 181.1) * mm, v(-245.82, 180.88) * mm, v(-246.2, 180.5) * mm]});
            skFitSpline(sketch, "E2000", {"points": [v(-246.2, 180.5) * mm, v(-246.57, 180.13) * mm, v(-246.78, 179.62) * mm, v(-246.78, 179.1) * mm]});
            skLineSegment(sketch, "E2001", {"start": v(-196.28, 180.7) * mm, "end": v(-197.92, 180.7) * mm});
            skFitSpline(sketch, "E2002", {"points": [v(-246.78, 145.1) * mm, v(-246.78, 144.56) * mm, v(-246.57, 144.05) * mm, v(-246.2, 143.68) * mm]});
            skFitSpline(sketch, "E2003", {"points": [v(-246.2, 143.68) * mm, v(-245.82, 143.3) * mm, v(-245.31, 143.1) * mm, v(-244.78, 143.1) * mm]});
            skLineSegment(sketch, "E2004", {"start": v(-198.78, 181.56) * mm, "end": v(-198.78, 186.1) * mm});
            skLineSegment(sketch, "E2005", {"start": v(-198.78, 186.1) * mm, "end": v(-203.99, 186.1) * mm});
            skFitSpline(sketch, "E2006", {"points": [v(-198.78, 152.62) * mm, v(-198.78, 152.8) * mm, v(-198.88, 152.97) * mm, v(-199.03, 153.06) * mm]});
            skFitSpline(sketch, "E2007", {"points": [v(-198.35, 153.74) * mm, v(-198.46, 153.92) * mm, v(-198.66, 154.02) * mm, v(-198.87, 153.98) * mm]});
            skFitSpline(sketch, "E2008", {"points": [v(-198.87, 153.98) * mm, v(-199.08, 153.95) * mm, v(-199.24, 153.78) * mm, v(-199.28, 153.58) * mm]});
            skFitSpline(sketch, "E2009", {"points": [v(-199.28, 153.58) * mm, v(-199.31, 153.37) * mm, v(-199.22, 153.16) * mm, v(-199.03, 153.06) * mm]});
            skFitSpline(sketch, "E2010", {"points": [v(-198.35, 153.74) * mm, v(-198.26, 153.59) * mm, v(-198.1, 153.5) * mm, v(-197.92, 153.5) * mm]});
            skLineSegment(sketch, "E2011", {"start": v(-213.3, 181.1) * mm, "end": v(-244.78, 181.1) * mm});
            skFitSpline(sketch, "E2012", {"points": [v(-196.28, 153.5) * mm, v(-196, 153.5) * mm, v(-195.78, 153.71) * mm, v(-195.78, 154) * mm]});
            skLineSegment(sketch, "E2013", {"start": v(-246.78, 179.1) * mm, "end": v(-246.78, 145.1) * mm});
            skFitSpline(sketch, "E2014", {"points": [v(-195.78, 159) * mm, v(-195.78, 159.27) * mm, v(-196, 159.5) * mm, v(-196.28, 159.5) * mm]});
            skLineSegment(sketch, "E2015", {"start": v(-244.78, 143.1) * mm, "end": v(-207.76, 143.1) * mm});
            skFitSpline(sketch, "E2016", {"points": [v(-197.92, 159.5) * mm, v(-198.1, 159.5) * mm, v(-198.26, 159.4) * mm, v(-198.35, 159.24) * mm]});
            skFitSpline(sketch, "E2017", {"points": [v(-199.03, 159.92) * mm, v(-199.22, 159.82) * mm, v(-199.31, 159.61) * mm, v(-199.28, 159.4) * mm]});
            skFitSpline(sketch, "E2018", {"points": [v(-199.28, 159.4) * mm, v(-199.24, 159.2) * mm, v(-199.08, 159.03) * mm, v(-198.87, 159) * mm]});
            skFitSpline(sketch, "E2019", {"points": [v(-198.87, 159) * mm, v(-198.66, 158.96) * mm, v(-198.46, 159.06) * mm, v(-198.35, 159.24) * mm]});
            skFitSpline(sketch, "E2020", {"points": [v(-199.03, 159.92) * mm, v(-198.88, 160.01) * mm, v(-198.78, 160.18) * mm, v(-198.78, 160.36) * mm]});
            skLineSegment(sketch, "E2021", {"start": v(-197.92, 153.5) * mm, "end": v(-196.28, 153.5) * mm});
            skFitSpline(sketch, "E2022", {"points": [v(-215.47, 162.1) * mm, v(-215.47, 166.06) * mm, v(-217.58, 169.72) * mm, v(-221.02, 171.7) * mm]});
            skFitSpline(sketch, "E2023", {"points": [v(-221.02, 171.7) * mm, v(-224.45, 173.69) * mm, v(-228.68, 173.69) * mm, v(-232.12, 171.7) * mm]});
            skFitSpline(sketch, "E2024", {"points": [v(-232.12, 171.7) * mm, v(-235.55, 169.72) * mm, v(-237.67, 166.06) * mm, v(-237.67, 162.1) * mm]});
            skFitSpline(sketch, "E2025", {"points": [v(-237.67, 162.1) * mm, v(-237.67, 158.12) * mm, v(-235.55, 154.46) * mm, v(-232.12, 152.48) * mm]});
            skFitSpline(sketch, "E2026", {"points": [v(-232.12, 152.48) * mm, v(-228.68, 150.5) * mm, v(-224.45, 150.5) * mm, v(-221.02, 152.48) * mm]});
            skFitSpline(sketch, "E2027", {"points": [v(-221.02, 152.48) * mm, v(-217.58, 154.46) * mm, v(-215.47, 158.12) * mm, v(-215.47, 162.1) * mm]});
            skLineSegment(sketch, "E2028", {"start": v(-195.78, 154) * mm, "end": v(-195.78, 159) * mm});
            skFitSpline(sketch, "E2029", {"points": [v(-209.47, 146.6) * mm, v(-209.47, 147.16) * mm, v(-209.77, 147.7) * mm, v(-210.27, 147.98) * mm]});
            skFitSpline(sketch, "E2030", {"points": [v(-210.27, 147.98) * mm, v(-210.76, 148.26) * mm, v(-211.37, 148.26) * mm, v(-211.87, 147.98) * mm]});
            skFitSpline(sketch, "E2031", {"points": [v(-211.87, 147.98) * mm, v(-212.36, 147.7) * mm, v(-212.67, 147.16) * mm, v(-212.67, 146.6) * mm]});
            skFitSpline(sketch, "E2032", {"points": [v(-212.67, 146.6) * mm, v(-212.67, 146.02) * mm, v(-212.36, 145.5) * mm, v(-211.87, 145.2) * mm]});
            skFitSpline(sketch, "E2033", {"points": [v(-211.87, 145.2) * mm, v(-211.37, 144.92) * mm, v(-210.76, 144.92) * mm, v(-210.27, 145.2) * mm]});
            skFitSpline(sketch, "E2034", {"points": [v(-210.27, 145.2) * mm, v(-209.77, 145.5) * mm, v(-209.47, 146.02) * mm, v(-209.47, 146.6) * mm]});
            skLineSegment(sketch, "E2035", {"start": v(-196.28, 159.5) * mm, "end": v(-197.92, 159.5) * mm});
            skFitSpline(sketch, "E2036", {"points": [v(-240.47, 146.6) * mm, v(-240.47, 147.16) * mm, v(-240.77, 147.7) * mm, v(-241.27, 147.98) * mm]});
            skFitSpline(sketch, "E2037", {"points": [v(-241.27, 147.98) * mm, v(-241.76, 148.26) * mm, v(-242.37, 148.26) * mm, v(-242.87, 147.98) * mm]});
            skFitSpline(sketch, "E2038", {"points": [v(-242.87, 147.98) * mm, v(-243.36, 147.7) * mm, v(-243.67, 147.16) * mm, v(-243.67, 146.6) * mm]});
            skFitSpline(sketch, "E2039", {"points": [v(-243.67, 146.6) * mm, v(-243.67, 145.7) * mm, v(-242.95, 145) * mm, v(-242.07, 145) * mm]});
            skFitSpline(sketch, "E2040", {"points": [v(-242.07, 145) * mm, v(-241.18, 145) * mm, v(-240.47, 145.7) * mm, v(-240.47, 146.6) * mm]});
            skLineSegment(sketch, "E2041", {"start": v(-198.78, 160.36) * mm, "end": v(-198.78, 165.5) * mm});
            skLineSegment(sketch, "E2042", {"start": v(-198.78, 165.5) * mm, "end": v(-201.78, 165.5) * mm});
            skLineSegment(sketch, "E2043", {"start": v(-201.78, 165.5) * mm, "end": v(-201.78, 164.22) * mm});
            skLineSegment(sketch, "E2044", {"start": v(-201.78, 164.22) * mm, "end": v(-205.78, 164.22) * mm});
            skLineSegment(sketch, "E2045", {"start": v(-205.78, 164.22) * mm, "end": v(-205.78, 165.5) * mm});
            skLineSegment(sketch, "E2046", {"start": v(-205.78, 165.5) * mm, "end": v(-208.78, 165.5) * mm});
            skFitSpline(sketch, "E2047", {"points": [v(-209.47, 177.6) * mm, v(-209.47, 178.16) * mm, v(-209.77, 178.69) * mm, v(-210.27, 178.98) * mm]});
            skFitSpline(sketch, "E2048", {"points": [v(-210.27, 178.98) * mm, v(-210.76, 179.26) * mm, v(-211.37, 179.26) * mm, v(-211.87, 178.98) * mm]});
            skFitSpline(sketch, "E2049", {"points": [v(-211.87, 178.98) * mm, v(-212.36, 178.69) * mm, v(-212.67, 178.16) * mm, v(-212.67, 177.6) * mm]});
            skFitSpline(sketch, "E2050", {"points": [v(-212.67, 177.6) * mm, v(-212.67, 177.02) * mm, v(-212.36, 176.5) * mm, v(-211.87, 176.2) * mm]});
            skFitSpline(sketch, "E2051", {"points": [v(-211.87, 176.2) * mm, v(-211.37, 175.92) * mm, v(-210.76, 175.92) * mm, v(-210.27, 176.2) * mm]});
            skFitSpline(sketch, "E2052", {"points": [v(-210.27, 176.2) * mm, v(-209.77, 176.5) * mm, v(-209.47, 177.02) * mm, v(-209.47, 177.6) * mm]});
            skFitSpline(sketch, "E2053", {"points": [v(-240.47, 177.6) * mm, v(-240.47, 178.16) * mm, v(-240.77, 178.69) * mm, v(-241.27, 178.98) * mm]});
            skFitSpline(sketch, "E2054", {"points": [v(-241.27, 178.98) * mm, v(-241.76, 179.26) * mm, v(-242.37, 179.26) * mm, v(-242.87, 178.98) * mm]});
            skFitSpline(sketch, "E2055", {"points": [v(-242.87, 178.98) * mm, v(-243.36, 178.69) * mm, v(-243.67, 178.16) * mm, v(-243.67, 177.6) * mm]});
            skFitSpline(sketch, "E2056", {"points": [v(-243.67, 177.6) * mm, v(-243.67, 176.7) * mm, v(-242.95, 176) * mm, v(-242.07, 176) * mm]});
            skFitSpline(sketch, "E2057", {"points": [v(-242.07, 176) * mm, v(-241.18, 176) * mm, v(-240.47, 176.7) * mm, v(-240.47, 177.6) * mm]});
            skLineSegment(sketch, "E2058", {"start": v(-198.78, 148.1) * mm, "end": v(-198.78, 152.62) * mm});
            skFitSpline(sketch, "E2059", {"points": [v(-346.88, -3.67) * mm, v(-348.21, -3.67) * mm, v(-349.48, -4.2) * mm, v(-350.42, -5.13) * mm]});
            skFitSpline(sketch, "E2060", {"points": [v(-350.42, -5.13) * mm, v(-351.36, -6.07) * mm, v(-351.88, -7.34) * mm, v(-351.88, -8.67) * mm]});
            skLineSegment(sketch, "E2061", {"start": v(-119.27, -10.05) * mm, "end": v(-324.15, -10.05) * mm});
            skFitSpline(sketch, "E2062", {"points": [v(-351.88, -43.05) * mm, v(-351.88, -45.82) * mm, v(-349.65, -48.05) * mm, v(-346.88, -48.05) * mm]});
            skLineSegment(sketch, "E2063", {"start": v(-325.1, -9.35) * mm, "end": v(-326.67, -4.37) * mm});
            skFitSpline(sketch, "E2064", {"points": [v(-316.71, -48.55) * mm, v(-316.71, -48.28) * mm, v(-316.94, -48.05) * mm, v(-317.21, -48.05) * mm]});
            skFitSpline(sketch, "E2065", {"points": [v(-296.21, -48.05) * mm, v(-296.34, -48.05) * mm, v(-296.47, -48.1) * mm, v(-296.57, -48.2) * mm]});
            skFitSpline(sketch, "E2066", {"points": [v(-296.57, -48.2) * mm, v(-296.66, -48.3) * mm, v(-296.71, -48.42) * mm, v(-296.71, -48.55) * mm]});
            skLineSegment(sketch, "E2067", {"start": v(-327.62, -3.67) * mm, "end": v(-346.88, -3.67) * mm});
            skFitSpline(sketch, "E2068", {"points": [v(-146.7, -48.55) * mm, v(-146.7, -48.28) * mm, v(-146.93, -48.05) * mm, v(-147.2, -48.05) * mm]});
            skLineSegment(sketch, "E2069", {"start": v(-351.88, -8.67) * mm, "end": v(-351.88, -43.05) * mm});
            skFitSpline(sketch, "E2070", {"points": [v(-146.7, -54.05) * mm, v(-146.7, -55.16) * mm, v(-145.81, -56.05) * mm, v(-144.7, -56.05) * mm]});
            skLineSegment(sketch, "E2071", {"start": v(-346.88, -48.05) * mm, "end": v(-317.21, -48.05) * mm});
            skFitSpline(sketch, "E2072", {"points": [v(-133.44, -55.27) * mm, v(-132.32, -53.62) * mm, v(-132.6, -51.4) * mm, v(-134.1, -50.1) * mm]});
            skFitSpline(sketch, "E2073", {"points": [v(-134.1, -50.1) * mm, v(-135.6, -48.78) * mm, v(-137.83, -48.78) * mm, v(-139.32, -50.1) * mm]});
            skFitSpline(sketch, "E2074", {"points": [v(-139.32, -50.1) * mm, v(-140.81, -51.4) * mm, v(-141.1, -53.62) * mm, v(-139.98, -55.27) * mm]});
            skLineSegment(sketch, "E2075", {"start": v(-296.21, -48.05) * mm, "end": v(-147.2, -48.05) * mm});
            skFitSpline(sketch, "E2076", {"points": [v(-128.7, -56.05) * mm, v(-128.18, -56.05) * mm, v(-127.67, -55.84) * mm, v(-127.3, -55.47) * mm]});
            skFitSpline(sketch, "E2077", {"points": [v(-127.3, -55.47) * mm, v(-126.92, -55.1) * mm, v(-126.7, -54.58) * mm, v(-126.7, -54.05) * mm]});
            skLineSegment(sketch, "E2078", {"start": v(-146.7, -48.55) * mm, "end": v(-146.7, -54.05) * mm});
            skFitSpline(sketch, "E2079", {"points": [v(-126.2, -48.05) * mm, v(-126.49, -48.05) * mm, v(-126.7, -48.28) * mm, v(-126.7, -48.55) * mm]});
            skLineSegment(sketch, "E2080", {"start": v(-144.7, -56.05) * mm, "end": v(-140.4, -56.05) * mm});
            skFitSpline(sketch, "E2081", {"points": [v(-96.54, -48.05) * mm, v(-93.78, -48.05) * mm, v(-91.54, -45.82) * mm, v(-91.54, -43.05) * mm]});
            skLineSegment(sketch, "E2082", {"start": v(-133.03, -56.05) * mm, "end": v(-128.7, -56.05) * mm});
            skFitSpline(sketch, "E2083", {"points": [v(-91.54, -8.67) * mm, v(-91.54, -5.9) * mm, v(-93.78, -3.67) * mm, v(-96.54, -3.67) * mm]});
            skLineSegment(sketch, "E2084", {"start": v(-126.7, -54.05) * mm, "end": v(-126.7, -48.55) * mm});
            skLineSegment(sketch, "E2085", {"start": v(-126.2, -48.05) * mm, "end": v(-96.54, -48.05) * mm});
            skFitSpline(sketch, "E2086", {"points": [v(-102.32, -21.17) * mm, v(-102.5, -21.17) * mm, v(-102.66, -21.26) * mm, v(-102.75, -21.42) * mm]});
            skFitSpline(sketch, "E2087", {"points": [v(-103.44, -20.73) * mm, v(-103.62, -20.84) * mm, v(-103.72, -21.05) * mm, v(-103.68, -21.25) * mm]});
            skFitSpline(sketch, "E2088", {"points": [v(-103.68, -21.25) * mm, v(-103.64, -21.46) * mm, v(-103.48, -21.62) * mm, v(-103.27, -21.66) * mm]});
            skFitSpline(sketch, "E2089", {"points": [v(-103.27, -21.66) * mm, v(-103.07, -21.7) * mm, v(-102.86, -21.6) * mm, v(-102.75, -21.42) * mm]});
            skFitSpline(sketch, "E2090", {"points": [v(-103.44, -20.73) * mm, v(-103.28, -20.64) * mm, v(-103.19, -20.48) * mm, v(-103.19, -20.3) * mm]});
            skLineSegment(sketch, "E2091", {"start": v(-91.54, -43.05) * mm, "end": v(-91.54, -8.67) * mm});
            skFitSpline(sketch, "E2092", {"points": [v(-103.19, -15.83) * mm, v(-103.19, -15.65) * mm, v(-103.28, -15.49) * mm, v(-103.44, -15.4) * mm]});
            skFitSpline(sketch, "E2093", {"points": [v(-102.75, -14.72) * mm, v(-102.86, -14.53) * mm, v(-103.07, -14.44) * mm, v(-103.27, -14.47) * mm]});
            skFitSpline(sketch, "E2094", {"points": [v(-103.27, -14.47) * mm, v(-103.48, -14.51) * mm, v(-103.64, -14.67) * mm, v(-103.68, -14.88) * mm]});
            skFitSpline(sketch, "E2095", {"points": [v(-103.68, -14.88) * mm, v(-103.72, -15.09) * mm, v(-103.62, -15.3) * mm, v(-103.44, -15.4) * mm]});
            skFitSpline(sketch, "E2096", {"points": [v(-102.75, -14.72) * mm, v(-102.66, -14.87) * mm, v(-102.5, -14.97) * mm, v(-102.32, -14.97) * mm]});
            skLineSegment(sketch, "E2097", {"start": v(-96.54, -3.67) * mm, "end": v(-115.8, -3.67) * mm});
            skFitSpline(sketch, "E2098", {"points": [v(-100.75, -14.97) * mm, v(-100.57, -14.97) * mm, v(-100.4, -14.87) * mm, v(-100.32, -14.72) * mm]});
            skFitSpline(sketch, "E2099", {"points": [v(-99.64, -15.4) * mm, v(-99.45, -15.3) * mm, v(-99.36, -15.09) * mm, v(-99.4, -14.88) * mm]});
            skFitSpline(sketch, "E2100", {"points": [v(-99.4, -14.88) * mm, v(-99.43, -14.67) * mm, v(-99.6, -14.51) * mm, v(-99.8, -14.47) * mm]});
            skFitSpline(sketch, "E2101", {"points": [v(-99.8, -14.47) * mm, v(-100, -14.44) * mm, v(-100.21, -14.53) * mm, v(-100.32, -14.72) * mm]});
            skFitSpline(sketch, "E2102", {"points": [v(-99.64, -15.4) * mm, v(-99.8, -15.49) * mm, v(-99.89, -15.65) * mm, v(-99.89, -15.83) * mm]});
            skLineSegment(sketch, "E2103", {"start": v(-116.76, -4.37) * mm, "end": v(-118.32, -9.35) * mm});
            skFitSpline(sketch, "E2104", {"points": [v(-99.89, -20.3) * mm, v(-99.89, -20.48) * mm, v(-99.8, -20.64) * mm, v(-99.64, -20.73) * mm]});
            skFitSpline(sketch, "E2105", {"points": [v(-100.32, -21.42) * mm, v(-100.21, -21.6) * mm, v(-100, -21.7) * mm, v(-99.8, -21.66) * mm]});
            skFitSpline(sketch, "E2106", {"points": [v(-99.8, -21.66) * mm, v(-99.6, -21.62) * mm, v(-99.43, -21.46) * mm, v(-99.4, -21.25) * mm]});
            skFitSpline(sketch, "E2107", {"points": [v(-99.4, -21.25) * mm, v(-99.36, -21.05) * mm, v(-99.45, -20.84) * mm, v(-99.64, -20.73) * mm]});
            skFitSpline(sketch, "E2108", {"points": [v(-100.32, -21.42) * mm, v(-100.4, -21.26) * mm, v(-100.57, -21.17) * mm, v(-100.75, -21.17) * mm]});
            skLineSegment(sketch, "E2109", {"start": v(-103.19, -20.3) * mm, "end": v(-103.19, -15.83) * mm});
            skFitSpline(sketch, "E2110", {"points": [v(-102.32, -42.37) * mm, v(-102.5, -42.37) * mm, v(-102.66, -42.46) * mm, v(-102.75, -42.62) * mm]});
            skFitSpline(sketch, "E2111", {"points": [v(-103.44, -41.93) * mm, v(-103.62, -42.04) * mm, v(-103.72, -42.25) * mm, v(-103.68, -42.45) * mm]});
            skFitSpline(sketch, "E2112", {"points": [v(-103.68, -42.45) * mm, v(-103.64, -42.66) * mm, v(-103.48, -42.82) * mm, v(-103.27, -42.86) * mm]});
            skFitSpline(sketch, "E2113", {"points": [v(-103.27, -42.86) * mm, v(-103.07, -42.9) * mm, v(-102.86, -42.8) * mm, v(-102.75, -42.62) * mm]});
            skFitSpline(sketch, "E2114", {"points": [v(-103.44, -41.93) * mm, v(-103.28, -41.84) * mm, v(-103.19, -41.68) * mm, v(-103.19, -41.5) * mm]});
            skLineSegment(sketch, "E2115", {"start": v(-102.32, -14.97) * mm, "end": v(-100.75, -14.97) * mm});
            skFitSpline(sketch, "E2116", {"points": [v(-103.19, -37.03) * mm, v(-103.19, -36.85) * mm, v(-103.28, -36.69) * mm, v(-103.44, -36.6) * mm]});
            skFitSpline(sketch, "E2117", {"points": [v(-102.75, -35.92) * mm, v(-102.86, -35.73) * mm, v(-103.07, -35.64) * mm, v(-103.27, -35.67) * mm]});
            skFitSpline(sketch, "E2118", {"points": [v(-103.27, -35.67) * mm, v(-103.48, -35.71) * mm, v(-103.64, -35.87) * mm, v(-103.68, -36.08) * mm]});
            skFitSpline(sketch, "E2119", {"points": [v(-103.68, -36.08) * mm, v(-103.72, -36.29) * mm, v(-103.62, -36.5) * mm, v(-103.44, -36.6) * mm]});
            skFitSpline(sketch, "E2120", {"points": [v(-102.75, -35.92) * mm, v(-102.66, -36.07) * mm, v(-102.5, -36.17) * mm, v(-102.32, -36.17) * mm]});
            skLineSegment(sketch, "E2121", {"start": v(-99.89, -15.83) * mm, "end": v(-99.89, -20.3) * mm});
            skFitSpline(sketch, "E2122", {"points": [v(-100.75, -36.17) * mm, v(-100.57, -36.17) * mm, v(-100.4, -36.07) * mm, v(-100.32, -35.92) * mm]});
            skFitSpline(sketch, "E2123", {"points": [v(-99.64, -36.6) * mm, v(-99.45, -36.5) * mm, v(-99.36, -36.29) * mm, v(-99.4, -36.08) * mm]});
            skFitSpline(sketch, "E2124", {"points": [v(-99.4, -36.08) * mm, v(-99.43, -35.87) * mm, v(-99.6, -35.71) * mm, v(-99.8, -35.67) * mm]});
            skFitSpline(sketch, "E2125", {"points": [v(-99.8, -35.67) * mm, v(-100, -35.64) * mm, v(-100.21, -35.73) * mm, v(-100.32, -35.92) * mm]});
            skFitSpline(sketch, "E2126", {"points": [v(-99.64, -36.6) * mm, v(-99.8, -36.69) * mm, v(-99.89, -36.85) * mm, v(-99.89, -37.03) * mm]});
            skLineSegment(sketch, "E2127", {"start": v(-100.75, -21.17) * mm, "end": v(-102.32, -21.17) * mm});
            skFitSpline(sketch, "E2128", {"points": [v(-99.89, -41.5) * mm, v(-99.89, -41.68) * mm, v(-99.8, -41.84) * mm, v(-99.64, -41.93) * mm]});
            skFitSpline(sketch, "E2129", {"points": [v(-100.32, -42.62) * mm, v(-100.21, -42.8) * mm, v(-100, -42.9) * mm, v(-99.8, -42.86) * mm]});
            skFitSpline(sketch, "E2130", {"points": [v(-99.8, -42.86) * mm, v(-99.6, -42.82) * mm, v(-99.43, -42.66) * mm, v(-99.4, -42.45) * mm]});
            skFitSpline(sketch, "E2131", {"points": [v(-99.4, -42.45) * mm, v(-99.36, -42.25) * mm, v(-99.45, -42.04) * mm, v(-99.64, -41.93) * mm]});
            skFitSpline(sketch, "E2132", {"points": [v(-100.32, -42.62) * mm, v(-100.4, -42.46) * mm, v(-100.57, -42.37) * mm, v(-100.75, -42.37) * mm]});
            skLineSegment(sketch, "E2133", {"start": v(-103.19, -41.5) * mm, "end": v(-103.19, -37.03) * mm});
            skFitSpline(sketch, "E2134", {"points": [v(-216.2, -21.55) * mm, v(-216.37, -21.55) * mm, v(-216.54, -21.65) * mm, v(-216.63, -21.8) * mm]});
            skFitSpline(sketch, "E2135", {"points": [v(-217.31, -21.12) * mm, v(-217.5, -21.23) * mm, v(-217.59, -21.43) * mm, v(-217.55, -21.64) * mm]});
            skFitSpline(sketch, "E2136", {"points": [v(-217.55, -21.64) * mm, v(-217.52, -21.85) * mm, v(-217.35, -22) * mm, v(-217.15, -22.05) * mm]});
            skFitSpline(sketch, "E2137", {"points": [v(-217.15, -22.05) * mm, v(-216.94, -22.08) * mm, v(-216.73, -21.99) * mm, v(-216.63, -21.8) * mm]});
            skFitSpline(sketch, "E2138", {"points": [v(-217.31, -21.12) * mm, v(-217.16, -21.03) * mm, v(-217.06, -20.87) * mm, v(-217.06, -20.69) * mm]});
            skLineSegment(sketch, "E2139", {"start": v(-102.32, -36.17) * mm, "end": v(-100.75, -36.17) * mm});
            skFitSpline(sketch, "E2140", {"points": [v(-217.06, -16.22) * mm, v(-217.06, -16.04) * mm, v(-217.16, -15.88) * mm, v(-217.31, -15.79) * mm]});
            skFitSpline(sketch, "E2141", {"points": [v(-216.63, -15.1) * mm, v(-216.73, -14.92) * mm, v(-216.94, -14.83) * mm, v(-217.15, -14.86) * mm]});
            skFitSpline(sketch, "E2142", {"points": [v(-217.15, -14.86) * mm, v(-217.35, -14.9) * mm, v(-217.52, -15.06) * mm, v(-217.55, -15.27) * mm]});
            skFitSpline(sketch, "E2143", {"points": [v(-217.55, -15.27) * mm, v(-217.59, -15.47) * mm, v(-217.5, -15.68) * mm, v(-217.31, -15.79) * mm]});
            skFitSpline(sketch, "E2144", {"points": [v(-216.63, -15.1) * mm, v(-216.54, -15.26) * mm, v(-216.37, -15.35) * mm, v(-216.2, -15.35) * mm]});
            skLineSegment(sketch, "E2145", {"start": v(-99.89, -37.03) * mm, "end": v(-99.89, -41.5) * mm});
            skFitSpline(sketch, "E2146", {"points": [v(-214.63, -15.35) * mm, v(-214.45, -15.35) * mm, v(-214.28, -15.26) * mm, v(-214.2, -15.1) * mm]});
            skFitSpline(sketch, "E2147", {"points": [v(-213.51, -15.79) * mm, v(-213.33, -15.68) * mm, v(-213.23, -15.47) * mm, v(-213.27, -15.27) * mm]});
            skFitSpline(sketch, "E2148", {"points": [v(-213.27, -15.27) * mm, v(-213.3, -15.06) * mm, v(-213.47, -14.9) * mm, v(-213.67, -14.86) * mm]});
            skFitSpline(sketch, "E2149", {"points": [v(-213.67, -14.86) * mm, v(-213.88, -14.83) * mm, v(-214.09, -14.92) * mm, v(-214.2, -15.1) * mm]});
            skFitSpline(sketch, "E2150", {"points": [v(-213.51, -15.79) * mm, v(-213.67, -15.88) * mm, v(-213.76, -16.04) * mm, v(-213.76, -16.22) * mm]});
            skLineSegment(sketch, "E2151", {"start": v(-100.75, -42.37) * mm, "end": v(-102.32, -42.37) * mm});
            skFitSpline(sketch, "E2152", {"points": [v(-213.76, -20.69) * mm, v(-213.76, -20.87) * mm, v(-213.67, -21.03) * mm, v(-213.51, -21.12) * mm]});
            skFitSpline(sketch, "E2153", {"points": [v(-214.2, -21.8) * mm, v(-214.09, -21.99) * mm, v(-213.88, -22.08) * mm, v(-213.67, -22.05) * mm]});
            skFitSpline(sketch, "E2154", {"points": [v(-213.67, -22.05) * mm, v(-213.47, -22) * mm, v(-213.3, -21.85) * mm, v(-213.27, -21.64) * mm]});
            skFitSpline(sketch, "E2155", {"points": [v(-213.27, -21.64) * mm, v(-213.23, -21.43) * mm, v(-213.33, -21.23) * mm, v(-213.51, -21.12) * mm]});
            skFitSpline(sketch, "E2156", {"points": [v(-214.2, -21.8) * mm, v(-214.28, -21.65) * mm, v(-214.45, -21.55) * mm, v(-214.63, -21.55) * mm]});
            skLineSegment(sketch, "E2157", {"start": v(-217.06, -20.69) * mm, "end": v(-217.06, -16.22) * mm});
            skFitSpline(sketch, "E2158", {"points": [v(-216.2, -42.75) * mm, v(-216.37, -42.75) * mm, v(-216.54, -42.85) * mm, v(-216.63, -43) * mm]});
            skFitSpline(sketch, "E2159", {"points": [v(-217.31, -42.32) * mm, v(-217.5, -42.43) * mm, v(-217.59, -42.63) * mm, v(-217.55, -42.84) * mm]});
            skFitSpline(sketch, "E2160", {"points": [v(-217.55, -42.84) * mm, v(-217.52, -43.05) * mm, v(-217.35, -43.2) * mm, v(-217.15, -43.25) * mm]});
            skFitSpline(sketch, "E2161", {"points": [v(-217.15, -43.25) * mm, v(-216.94, -43.28) * mm, v(-216.73, -43.19) * mm, v(-216.63, -43) * mm]});
            skFitSpline(sketch, "E2162", {"points": [v(-217.31, -42.32) * mm, v(-217.16, -42.23) * mm, v(-217.06, -42.07) * mm, v(-217.06, -41.89) * mm]});
            skLineSegment(sketch, "E2163", {"start": v(-216.2, -15.35) * mm, "end": v(-214.63, -15.35) * mm});
            skFitSpline(sketch, "E2164", {"points": [v(-217.06, -37.42) * mm, v(-217.06, -37.24) * mm, v(-217.16, -37.08) * mm, v(-217.31, -36.99) * mm]});
            skFitSpline(sketch, "E2165", {"points": [v(-216.63, -36.3) * mm, v(-216.73, -36.12) * mm, v(-216.94, -36.02) * mm, v(-217.15, -36.06) * mm]});
            skFitSpline(sketch, "E2166", {"points": [v(-217.15, -36.06) * mm, v(-217.35, -36.1) * mm, v(-217.52, -36.26) * mm, v(-217.55, -36.47) * mm]});
            skFitSpline(sketch, "E2167", {"points": [v(-217.55, -36.47) * mm, v(-217.59, -36.67) * mm, v(-217.5, -36.88) * mm, v(-217.31, -36.99) * mm]});
            skFitSpline(sketch, "E2168", {"points": [v(-216.63, -36.3) * mm, v(-216.54, -36.46) * mm, v(-216.37, -36.55) * mm, v(-216.2, -36.55) * mm]});
            skLineSegment(sketch, "E2169", {"start": v(-213.76, -16.22) * mm, "end": v(-213.76, -20.69) * mm});
            skFitSpline(sketch, "E2170", {"points": [v(-214.63, -36.55) * mm, v(-214.45, -36.55) * mm, v(-214.28, -36.46) * mm, v(-214.2, -36.3) * mm]});
            skFitSpline(sketch, "E2171", {"points": [v(-213.51, -36.99) * mm, v(-213.33, -36.88) * mm, v(-213.23, -36.67) * mm, v(-213.27, -36.47) * mm]});
            skFitSpline(sketch, "E2172", {"points": [v(-213.27, -36.47) * mm, v(-213.3, -36.26) * mm, v(-213.47, -36.1) * mm, v(-213.67, -36.06) * mm]});
            skFitSpline(sketch, "E2173", {"points": [v(-213.67, -36.06) * mm, v(-213.88, -36.02) * mm, v(-214.09, -36.12) * mm, v(-214.2, -36.3) * mm]});
            skFitSpline(sketch, "E2174", {"points": [v(-213.51, -36.99) * mm, v(-213.67, -37.08) * mm, v(-213.76, -37.24) * mm, v(-213.76, -37.42) * mm]});
            skLineSegment(sketch, "E2175", {"start": v(-214.63, -21.55) * mm, "end": v(-216.2, -21.55) * mm});
            skFitSpline(sketch, "E2176", {"points": [v(-213.76, -41.89) * mm, v(-213.76, -42.07) * mm, v(-213.67, -42.23) * mm, v(-213.51, -42.32) * mm]});
            skFitSpline(sketch, "E2177", {"points": [v(-214.2, -43) * mm, v(-214.09, -43.19) * mm, v(-213.88, -43.28) * mm, v(-213.67, -43.25) * mm]});
            skFitSpline(sketch, "E2178", {"points": [v(-213.67, -43.25) * mm, v(-213.47, -43.2) * mm, v(-213.3, -43.05) * mm, v(-213.27, -42.84) * mm]});
            skFitSpline(sketch, "E2179", {"points": [v(-213.27, -42.84) * mm, v(-213.23, -42.63) * mm, v(-213.33, -42.43) * mm, v(-213.51, -42.32) * mm]});
            skFitSpline(sketch, "E2180", {"points": [v(-214.2, -43) * mm, v(-214.28, -42.85) * mm, v(-214.45, -42.75) * mm, v(-214.63, -42.75) * mm]});
            skLineSegment(sketch, "E2181", {"start": v(-217.06, -41.89) * mm, "end": v(-217.06, -37.42) * mm});
            skFitSpline(sketch, "E2182", {"points": [v(-228.8, -21.55) * mm, v(-228.97, -21.55) * mm, v(-229.14, -21.65) * mm, v(-229.23, -21.8) * mm]});
            skFitSpline(sketch, "E2183", {"points": [v(-229.91, -21.12) * mm, v(-230.1, -21.23) * mm, v(-230.19, -21.43) * mm, v(-230.15, -21.64) * mm]});
            skFitSpline(sketch, "E2184", {"points": [v(-230.15, -21.64) * mm, v(-230.12, -21.85) * mm, v(-229.95, -22) * mm, v(-229.75, -22.05) * mm]});
            skFitSpline(sketch, "E2185", {"points": [v(-229.75, -22.05) * mm, v(-229.54, -22.08) * mm, v(-229.33, -21.99) * mm, v(-229.23, -21.8) * mm]});
            skFitSpline(sketch, "E2186", {"points": [v(-229.91, -21.12) * mm, v(-229.76, -21.03) * mm, v(-229.66, -20.87) * mm, v(-229.66, -20.69) * mm]});
            skLineSegment(sketch, "E2187", {"start": v(-216.2, -36.55) * mm, "end": v(-214.63, -36.55) * mm});
            skFitSpline(sketch, "E2188", {"points": [v(-229.66, -16.22) * mm, v(-229.66, -16.04) * mm, v(-229.76, -15.88) * mm, v(-229.91, -15.79) * mm]});
            skFitSpline(sketch, "E2189", {"points": [v(-229.23, -15.1) * mm, v(-229.33, -14.92) * mm, v(-229.54, -14.83) * mm, v(-229.75, -14.86) * mm]});
            skFitSpline(sketch, "E2190", {"points": [v(-229.75, -14.86) * mm, v(-229.95, -14.9) * mm, v(-230.12, -15.06) * mm, v(-230.15, -15.27) * mm]});
            skFitSpline(sketch, "E2191", {"points": [v(-230.15, -15.27) * mm, v(-230.19, -15.47) * mm, v(-230.1, -15.68) * mm, v(-229.91, -15.79) * mm]});
            skFitSpline(sketch, "E2192", {"points": [v(-229.23, -15.1) * mm, v(-229.14, -15.26) * mm, v(-228.97, -15.35) * mm, v(-228.8, -15.35) * mm]});
            skLineSegment(sketch, "E2193", {"start": v(-213.76, -37.42) * mm, "end": v(-213.76, -41.89) * mm});
            skFitSpline(sketch, "E2194", {"points": [v(-227.23, -15.35) * mm, v(-227.05, -15.35) * mm, v(-226.88, -15.26) * mm, v(-226.8, -15.1) * mm]});
            skFitSpline(sketch, "E2195", {"points": [v(-226.11, -15.79) * mm, v(-225.93, -15.68) * mm, v(-225.83, -15.47) * mm, v(-225.87, -15.27) * mm]});
            skFitSpline(sketch, "E2196", {"points": [v(-225.87, -15.27) * mm, v(-225.9, -15.06) * mm, v(-226.07, -14.9) * mm, v(-226.27, -14.86) * mm]});
            skFitSpline(sketch, "E2197", {"points": [v(-226.27, -14.86) * mm, v(-226.48, -14.83) * mm, v(-226.69, -14.92) * mm, v(-226.8, -15.1) * mm]});
            skFitSpline(sketch, "E2198", {"points": [v(-226.11, -15.79) * mm, v(-226.26, -15.88) * mm, v(-226.36, -16.04) * mm, v(-226.36, -16.22) * mm]});
            skLineSegment(sketch, "E2199", {"start": v(-214.63, -42.75) * mm, "end": v(-216.2, -42.75) * mm});
            skFitSpline(sketch, "E2200", {"points": [v(-226.36, -20.69) * mm, v(-226.36, -20.87) * mm, v(-226.26, -21.03) * mm, v(-226.11, -21.12) * mm]});
            skFitSpline(sketch, "E2201", {"points": [v(-226.8, -21.8) * mm, v(-226.69, -21.99) * mm, v(-226.48, -22.08) * mm, v(-226.27, -22.05) * mm]});
            skFitSpline(sketch, "E2202", {"points": [v(-226.27, -22.05) * mm, v(-226.07, -22) * mm, v(-225.9, -21.85) * mm, v(-225.87, -21.64) * mm]});
            skFitSpline(sketch, "E2203", {"points": [v(-225.87, -21.64) * mm, v(-225.83, -21.43) * mm, v(-225.93, -21.23) * mm, v(-226.11, -21.12) * mm]});
            skFitSpline(sketch, "E2204", {"points": [v(-226.8, -21.8) * mm, v(-226.88, -21.65) * mm, v(-227.05, -21.55) * mm, v(-227.23, -21.55) * mm]});
            skLineSegment(sketch, "E2205", {"start": v(-229.66, -20.69) * mm, "end": v(-229.66, -16.22) * mm});
            skFitSpline(sketch, "E2206", {"points": [v(-228.8, -42.75) * mm, v(-228.97, -42.75) * mm, v(-229.14, -42.85) * mm, v(-229.23, -43) * mm]});
            skFitSpline(sketch, "E2207", {"points": [v(-229.91, -42.32) * mm, v(-230.1, -42.43) * mm, v(-230.19, -42.63) * mm, v(-230.15, -42.84) * mm]});
            skFitSpline(sketch, "E2208", {"points": [v(-230.15, -42.84) * mm, v(-230.12, -43.05) * mm, v(-229.95, -43.2) * mm, v(-229.75, -43.25) * mm]});
            skFitSpline(sketch, "E2209", {"points": [v(-229.75, -43.25) * mm, v(-229.54, -43.28) * mm, v(-229.33, -43.19) * mm, v(-229.23, -43) * mm]});
            skFitSpline(sketch, "E2210", {"points": [v(-229.91, -42.32) * mm, v(-229.76, -42.23) * mm, v(-229.66, -42.07) * mm, v(-229.66, -41.89) * mm]});
            skLineSegment(sketch, "E2211", {"start": v(-228.8, -15.35) * mm, "end": v(-227.23, -15.35) * mm});
            skFitSpline(sketch, "E2212", {"points": [v(-229.66, -37.42) * mm, v(-229.66, -37.24) * mm, v(-229.76, -37.08) * mm, v(-229.91, -36.99) * mm]});
            skFitSpline(sketch, "E2213", {"points": [v(-229.23, -36.3) * mm, v(-229.33, -36.12) * mm, v(-229.54, -36.02) * mm, v(-229.75, -36.06) * mm]});
            skFitSpline(sketch, "E2214", {"points": [v(-229.75, -36.06) * mm, v(-229.95, -36.1) * mm, v(-230.12, -36.26) * mm, v(-230.15, -36.47) * mm]});
            skFitSpline(sketch, "E2215", {"points": [v(-230.15, -36.47) * mm, v(-230.19, -36.67) * mm, v(-230.1, -36.88) * mm, v(-229.91, -36.99) * mm]});
            skFitSpline(sketch, "E2216", {"points": [v(-229.23, -36.3) * mm, v(-229.14, -36.46) * mm, v(-228.97, -36.55) * mm, v(-228.8, -36.55) * mm]});
            skLineSegment(sketch, "E2217", {"start": v(-226.36, -16.22) * mm, "end": v(-226.36, -20.69) * mm});
            skFitSpline(sketch, "E2218", {"points": [v(-227.23, -36.55) * mm, v(-227.05, -36.55) * mm, v(-226.88, -36.46) * mm, v(-226.8, -36.3) * mm]});
            skFitSpline(sketch, "E2219", {"points": [v(-226.11, -36.99) * mm, v(-225.93, -36.88) * mm, v(-225.83, -36.67) * mm, v(-225.87, -36.47) * mm]});
            skFitSpline(sketch, "E2220", {"points": [v(-225.87, -36.47) * mm, v(-225.9, -36.26) * mm, v(-226.07, -36.1) * mm, v(-226.27, -36.06) * mm]});
            skFitSpline(sketch, "E2221", {"points": [v(-226.27, -36.06) * mm, v(-226.48, -36.02) * mm, v(-226.69, -36.12) * mm, v(-226.8, -36.3) * mm]});
            skFitSpline(sketch, "E2222", {"points": [v(-226.11, -36.99) * mm, v(-226.26, -37.08) * mm, v(-226.36, -37.24) * mm, v(-226.36, -37.42) * mm]});
            skLineSegment(sketch, "E2223", {"start": v(-227.23, -21.55) * mm, "end": v(-228.8, -21.55) * mm});
            skFitSpline(sketch, "E2224", {"points": [v(-226.36, -41.89) * mm, v(-226.36, -42.07) * mm, v(-226.26, -42.23) * mm, v(-226.11, -42.32) * mm]});
            skFitSpline(sketch, "E2225", {"points": [v(-226.8, -43) * mm, v(-226.69, -43.19) * mm, v(-226.48, -43.28) * mm, v(-226.27, -43.25) * mm]});
            skFitSpline(sketch, "E2226", {"points": [v(-226.27, -43.25) * mm, v(-226.07, -43.2) * mm, v(-225.9, -43.05) * mm, v(-225.87, -42.84) * mm]});
            skFitSpline(sketch, "E2227", {"points": [v(-225.87, -42.84) * mm, v(-225.83, -42.63) * mm, v(-225.93, -42.43) * mm, v(-226.11, -42.32) * mm]});
            skFitSpline(sketch, "E2228", {"points": [v(-226.8, -43) * mm, v(-226.88, -42.85) * mm, v(-227.05, -42.75) * mm, v(-227.23, -42.75) * mm]});
            skLineSegment(sketch, "E2229", {"start": v(-229.66, -41.89) * mm, "end": v(-229.66, -37.42) * mm});
            skFitSpline(sketch, "E2230", {"points": [v(-340.67, -21.42) * mm, v(-340.76, -21.26) * mm, v(-340.92, -21.17) * mm, v(-341.1, -21.17) * mm]});
            skFitSpline(sketch, "E2231", {"points": [v(-340.67, -21.42) * mm, v(-340.56, -21.6) * mm, v(-340.35, -21.7) * mm, v(-340.15, -21.66) * mm]});
            skFitSpline(sketch, "E2232", {"points": [v(-340.15, -21.66) * mm, v(-339.94, -21.62) * mm, v(-339.78, -21.46) * mm, v(-339.74, -21.25) * mm]});
            skFitSpline(sketch, "E2233", {"points": [v(-339.74, -21.25) * mm, v(-339.7, -21.05) * mm, v(-339.8, -20.84) * mm, v(-339.98, -20.73) * mm]});
            skFitSpline(sketch, "E2234", {"points": [v(-340.23, -20.3) * mm, v(-340.23, -20.48) * mm, v(-340.14, -20.64) * mm, v(-339.98, -20.73) * mm]});
            skLineSegment(sketch, "E2235", {"start": v(-228.8, -36.55) * mm, "end": v(-227.23, -36.55) * mm});
            skFitSpline(sketch, "E2236", {"points": [v(-339.98, -15.4) * mm, v(-340.14, -15.49) * mm, v(-340.23, -15.65) * mm, v(-340.23, -15.83) * mm]});
            skFitSpline(sketch, "E2237", {"points": [v(-339.98, -15.4) * mm, v(-339.8, -15.3) * mm, v(-339.7, -15.09) * mm, v(-339.74, -14.88) * mm]});
            skFitSpline(sketch, "E2238", {"points": [v(-339.74, -14.88) * mm, v(-339.78, -14.67) * mm, v(-339.94, -14.51) * mm, v(-340.15, -14.47) * mm]});
            skFitSpline(sketch, "E2239", {"points": [v(-340.15, -14.47) * mm, v(-340.35, -14.44) * mm, v(-340.56, -14.53) * mm, v(-340.67, -14.72) * mm]});
            skFitSpline(sketch, "E2240", {"points": [v(-341.1, -14.97) * mm, v(-340.92, -14.97) * mm, v(-340.76, -14.87) * mm, v(-340.67, -14.72) * mm]});
            skLineSegment(sketch, "E2241", {"start": v(-226.36, -37.42) * mm, "end": v(-226.36, -41.89) * mm});
            skFitSpline(sketch, "E2242", {"points": [v(-343.1, -14.72) * mm, v(-343.01, -14.87) * mm, v(-342.85, -14.97) * mm, v(-342.67, -14.97) * mm]});
            skFitSpline(sketch, "E2243", {"points": [v(-343.1, -14.72) * mm, v(-343.2, -14.53) * mm, v(-343.41, -14.44) * mm, v(-343.62, -14.47) * mm]});
            skFitSpline(sketch, "E2244", {"points": [v(-343.62, -14.47) * mm, v(-343.83, -14.51) * mm, v(-343.99, -14.67) * mm, v(-344.03, -14.88) * mm]});
            skFitSpline(sketch, "E2245", {"points": [v(-344.03, -14.88) * mm, v(-344.06, -15.09) * mm, v(-343.97, -15.3) * mm, v(-343.78, -15.4) * mm]});
            skFitSpline(sketch, "E2246", {"points": [v(-343.53, -15.83) * mm, v(-343.53, -15.65) * mm, v(-343.63, -15.49) * mm, v(-343.78, -15.4) * mm]});
            skLineSegment(sketch, "E2247", {"start": v(-227.23, -42.75) * mm, "end": v(-228.8, -42.75) * mm});
            skFitSpline(sketch, "E2248", {"points": [v(-343.78, -20.73) * mm, v(-343.63, -20.64) * mm, v(-343.53, -20.48) * mm, v(-343.53, -20.3) * mm]});
            skFitSpline(sketch, "E2249", {"points": [v(-343.78, -20.73) * mm, v(-343.97, -20.84) * mm, v(-344.06, -21.05) * mm, v(-344.03, -21.25) * mm]});
            skFitSpline(sketch, "E2250", {"points": [v(-344.03, -21.25) * mm, v(-343.99, -21.46) * mm, v(-343.83, -21.62) * mm, v(-343.62, -21.66) * mm]});
            skFitSpline(sketch, "E2251", {"points": [v(-343.62, -21.66) * mm, v(-343.41, -21.7) * mm, v(-343.2, -21.6) * mm, v(-343.1, -21.42) * mm]});
            skFitSpline(sketch, "E2252", {"points": [v(-342.67, -21.17) * mm, v(-342.85, -21.17) * mm, v(-343.01, -21.26) * mm, v(-343.1, -21.42) * mm]});
            skLineSegment(sketch, "E2253", {"start": v(-340.23, -20.3) * mm, "end": v(-340.23, -15.83) * mm});
            skFitSpline(sketch, "E2254", {"points": [v(-340.67, -42.62) * mm, v(-340.76, -42.46) * mm, v(-340.92, -42.37) * mm, v(-341.1, -42.37) * mm]});
            skFitSpline(sketch, "E2255", {"points": [v(-340.67, -42.62) * mm, v(-340.56, -42.8) * mm, v(-340.35, -42.9) * mm, v(-340.15, -42.86) * mm]});
            skFitSpline(sketch, "E2256", {"points": [v(-340.15, -42.86) * mm, v(-339.94, -42.82) * mm, v(-339.78, -42.66) * mm, v(-339.74, -42.45) * mm]});
            skFitSpline(sketch, "E2257", {"points": [v(-339.74, -42.45) * mm, v(-339.7, -42.25) * mm, v(-339.8, -42.04) * mm, v(-339.98, -41.93) * mm]});
            skFitSpline(sketch, "E2258", {"points": [v(-340.23, -41.5) * mm, v(-340.23, -41.68) * mm, v(-340.14, -41.84) * mm, v(-339.98, -41.93) * mm]});
            skLineSegment(sketch, "E2259", {"start": v(-341.1, -14.97) * mm, "end": v(-342.67, -14.97) * mm});
            skFitSpline(sketch, "E2260", {"points": [v(-339.98, -36.6) * mm, v(-340.14, -36.69) * mm, v(-340.23, -36.85) * mm, v(-340.23, -37.03) * mm]});
            skFitSpline(sketch, "E2261", {"points": [v(-339.98, -36.6) * mm, v(-339.8, -36.5) * mm, v(-339.7, -36.29) * mm, v(-339.74, -36.08) * mm]});
            skFitSpline(sketch, "E2262", {"points": [v(-339.74, -36.08) * mm, v(-339.78, -35.87) * mm, v(-339.94, -35.71) * mm, v(-340.15, -35.67) * mm]});
            skFitSpline(sketch, "E2263", {"points": [v(-340.15, -35.67) * mm, v(-340.35, -35.64) * mm, v(-340.56, -35.73) * mm, v(-340.67, -35.92) * mm]});
            skFitSpline(sketch, "E2264", {"points": [v(-341.1, -36.17) * mm, v(-340.92, -36.17) * mm, v(-340.76, -36.07) * mm, v(-340.67, -35.92) * mm]});
            skLineSegment(sketch, "E2265", {"start": v(-343.53, -15.83) * mm, "end": v(-343.53, -20.3) * mm});
            skFitSpline(sketch, "E2266", {"points": [v(-343.1, -35.92) * mm, v(-343.01, -36.07) * mm, v(-342.85, -36.17) * mm, v(-342.67, -36.17) * mm]});
            skFitSpline(sketch, "E2267", {"points": [v(-343.1, -35.92) * mm, v(-343.2, -35.73) * mm, v(-343.41, -35.64) * mm, v(-343.62, -35.67) * mm]});
            skFitSpline(sketch, "E2268", {"points": [v(-343.62, -35.67) * mm, v(-343.83, -35.71) * mm, v(-343.99, -35.87) * mm, v(-344.03, -36.08) * mm]});
            skFitSpline(sketch, "E2269", {"points": [v(-344.03, -36.08) * mm, v(-344.06, -36.29) * mm, v(-343.97, -36.5) * mm, v(-343.78, -36.6) * mm]});
            skFitSpline(sketch, "E2270", {"points": [v(-343.53, -37.03) * mm, v(-343.53, -36.85) * mm, v(-343.63, -36.69) * mm, v(-343.78, -36.6) * mm]});
            skLineSegment(sketch, "E2271", {"start": v(-342.67, -21.17) * mm, "end": v(-341.1, -21.17) * mm});
            skFitSpline(sketch, "E2272", {"points": [v(-343.78, -41.93) * mm, v(-343.63, -41.84) * mm, v(-343.53, -41.68) * mm, v(-343.53, -41.5) * mm]});
            skFitSpline(sketch, "E2273", {"points": [v(-343.78, -41.93) * mm, v(-343.97, -42.04) * mm, v(-344.06, -42.25) * mm, v(-344.03, -42.45) * mm]});
            skFitSpline(sketch, "E2274", {"points": [v(-344.03, -42.45) * mm, v(-343.99, -42.66) * mm, v(-343.83, -42.82) * mm, v(-343.62, -42.86) * mm]});
            skFitSpline(sketch, "E2275", {"points": [v(-343.62, -42.86) * mm, v(-343.41, -42.9) * mm, v(-343.2, -42.8) * mm, v(-343.1, -42.62) * mm]});
            skFitSpline(sketch, "E2276", {"points": [v(-342.67, -42.37) * mm, v(-342.85, -42.37) * mm, v(-343.01, -42.46) * mm, v(-343.1, -42.62) * mm]});
            skLineSegment(sketch, "E2277", {"start": v(-340.23, -41.5) * mm, "end": v(-340.23, -37.03) * mm});
            skFitSpline(sketch, "E2278", {"points": [v(-99.94, -28.67) * mm, v(-99.94, -28.1) * mm, v(-100.24, -27.57) * mm, v(-100.74, -27.28) * mm]});
            skFitSpline(sketch, "E2279", {"points": [v(-100.74, -27.28) * mm, v(-101.23, -27) * mm, v(-101.84, -27) * mm, v(-102.34, -27.28) * mm]});
            skFitSpline(sketch, "E2280", {"points": [v(-102.34, -27.28) * mm, v(-102.83, -27.57) * mm, v(-103.14, -28.1) * mm, v(-103.14, -28.67) * mm]});
            skFitSpline(sketch, "E2281", {"points": [v(-103.14, -28.67) * mm, v(-103.14, -29.24) * mm, v(-102.83, -29.77) * mm, v(-102.34, -30.05) * mm]});
            skFitSpline(sketch, "E2282", {"points": [v(-102.34, -30.05) * mm, v(-101.84, -30.34) * mm, v(-101.23, -30.34) * mm, v(-100.74, -30.05) * mm]});
            skFitSpline(sketch, "E2283", {"points": [v(-100.74, -30.05) * mm, v(-100.24, -29.77) * mm, v(-99.94, -29.24) * mm, v(-99.94, -28.67) * mm]});
            skLineSegment(sketch, "E2284", {"start": v(-341.1, -36.17) * mm, "end": v(-342.67, -36.17) * mm});
            skFitSpline(sketch, "E2285", {"points": [v(-154.11, -18.67) * mm, v(-154.11, -18.1) * mm, v(-154.42, -17.57) * mm, v(-154.91, -17.28) * mm]});
            skFitSpline(sketch, "E2286", {"points": [v(-154.91, -17.28) * mm, v(-155.4, -17) * mm, v(-156.02, -17) * mm, v(-156.51, -17.28) * mm]});
            skFitSpline(sketch, "E2287", {"points": [v(-156.51, -17.28) * mm, v(-157, -17.57) * mm, v(-157.31, -18.1) * mm, v(-157.31, -18.67) * mm]});
            skFitSpline(sketch, "E2288", {"points": [v(-157.31, -18.67) * mm, v(-157.31, -19.24) * mm, v(-157, -19.77) * mm, v(-156.51, -20.05) * mm]});
            skFitSpline(sketch, "E2289", {"points": [v(-156.51, -20.05) * mm, v(-156.02, -20.34) * mm, v(-155.4, -20.34) * mm, v(-154.91, -20.05) * mm]});
            skFitSpline(sketch, "E2290", {"points": [v(-154.91, -20.05) * mm, v(-154.42, -19.77) * mm, v(-154.11, -19.24) * mm, v(-154.11, -18.67) * mm]});
            skLineSegment(sketch, "E2291", {"start": v(-343.53, -37.03) * mm, "end": v(-343.53, -41.5) * mm});
            skFitSpline(sketch, "E2292", {"points": [v(-154.11, -38.67) * mm, v(-154.11, -38.1) * mm, v(-154.42, -37.57) * mm, v(-154.91, -37.28) * mm]});
            skFitSpline(sketch, "E2293", {"points": [v(-154.91, -37.28) * mm, v(-155.4, -37) * mm, v(-156.02, -37) * mm, v(-156.51, -37.28) * mm]});
            skFitSpline(sketch, "E2294", {"points": [v(-156.51, -37.28) * mm, v(-157, -37.57) * mm, v(-157.31, -38.1) * mm, v(-157.31, -38.67) * mm]});
            skFitSpline(sketch, "E2295", {"points": [v(-157.31, -38.67) * mm, v(-157.31, -39.24) * mm, v(-157, -39.77) * mm, v(-156.51, -40.05) * mm]});
            skFitSpline(sketch, "E2296", {"points": [v(-156.51, -40.05) * mm, v(-156.02, -40.34) * mm, v(-155.4, -40.34) * mm, v(-154.91, -40.05) * mm]});
            skFitSpline(sketch, "E2297", {"points": [v(-154.91, -40.05) * mm, v(-154.42, -39.77) * mm, v(-154.11, -39.24) * mm, v(-154.11, -38.67) * mm]});
            skLineSegment(sketch, "E2298", {"start": v(-342.67, -42.37) * mm, "end": v(-341.1, -42.37) * mm});
            skFitSpline(sketch, "E2299", {"points": [v(-185.11, -18.67) * mm, v(-185.11, -18.1) * mm, v(-185.42, -17.57) * mm, v(-185.91, -17.28) * mm]});
            skFitSpline(sketch, "E2300", {"points": [v(-185.91, -17.28) * mm, v(-186.4, -17) * mm, v(-187.02, -17) * mm, v(-187.51, -17.28) * mm]});
            skFitSpline(sketch, "E2301", {"points": [v(-187.51, -17.28) * mm, v(-188, -17.57) * mm, v(-188.31, -18.1) * mm, v(-188.31, -18.67) * mm]});
            skFitSpline(sketch, "E2302", {"points": [v(-188.31, -18.67) * mm, v(-188.31, -19.24) * mm, v(-188, -19.77) * mm, v(-187.51, -20.05) * mm]});
            skFitSpline(sketch, "E2303", {"points": [v(-187.51, -20.05) * mm, v(-187.02, -20.34) * mm, v(-186.4, -20.34) * mm, v(-185.91, -20.05) * mm]});
            skFitSpline(sketch, "E2304", {"points": [v(-185.91, -20.05) * mm, v(-185.42, -19.77) * mm, v(-185.11, -19.24) * mm, v(-185.11, -18.67) * mm]});
            skFitSpline(sketch, "E2305", {"points": [v(-185.11, -38.67) * mm, v(-185.11, -38.1) * mm, v(-185.42, -37.57) * mm, v(-185.91, -37.28) * mm]});
            skFitSpline(sketch, "E2306", {"points": [v(-185.91, -37.28) * mm, v(-186.4, -37) * mm, v(-187.02, -37) * mm, v(-187.51, -37.28) * mm]});
            skFitSpline(sketch, "E2307", {"points": [v(-187.51, -37.28) * mm, v(-188, -37.57) * mm, v(-188.31, -38.1) * mm, v(-188.31, -38.67) * mm]});
            skFitSpline(sketch, "E2308", {"points": [v(-188.31, -38.67) * mm, v(-188.31, -39.24) * mm, v(-188, -39.77) * mm, v(-187.51, -40.05) * mm]});
            skFitSpline(sketch, "E2309", {"points": [v(-187.51, -40.05) * mm, v(-187.02, -40.34) * mm, v(-186.4, -40.34) * mm, v(-185.91, -40.05) * mm]});
            skFitSpline(sketch, "E2310", {"points": [v(-185.91, -40.05) * mm, v(-185.42, -39.77) * mm, v(-185.11, -39.24) * mm, v(-185.11, -38.67) * mm]});
            skFitSpline(sketch, "E2311", {"points": [v(-213.81, -29.05) * mm, v(-213.81, -28.48) * mm, v(-214.12, -27.95) * mm, v(-214.61, -27.67) * mm]});
            skFitSpline(sketch, "E2312", {"points": [v(-214.61, -27.67) * mm, v(-215.1, -27.38) * mm, v(-215.72, -27.38) * mm, v(-216.21, -27.67) * mm]});
            skFitSpline(sketch, "E2313", {"points": [v(-216.21, -27.67) * mm, v(-216.7, -27.95) * mm, v(-217.01, -28.48) * mm, v(-217.01, -29.05) * mm]});
            skFitSpline(sketch, "E2314", {"points": [v(-217.01, -29.05) * mm, v(-217.01, -29.63) * mm, v(-216.7, -30.15) * mm, v(-216.21, -30.44) * mm]});
            skFitSpline(sketch, "E2315", {"points": [v(-216.21, -30.44) * mm, v(-215.72, -30.73) * mm, v(-215.1, -30.73) * mm, v(-214.61, -30.44) * mm]});
            skFitSpline(sketch, "E2316", {"points": [v(-214.61, -30.44) * mm, v(-214.12, -30.15) * mm, v(-213.81, -29.63) * mm, v(-213.81, -29.05) * mm]});
            skFitSpline(sketch, "E2317", {"points": [v(-226.41, -29.05) * mm, v(-226.41, -28.48) * mm, v(-226.72, -27.95) * mm, v(-227.21, -27.67) * mm]});
            skFitSpline(sketch, "E2318", {"points": [v(-227.21, -27.67) * mm, v(-227.7, -27.38) * mm, v(-228.32, -27.38) * mm, v(-228.81, -27.67) * mm]});
            skFitSpline(sketch, "E2319", {"points": [v(-228.81, -27.67) * mm, v(-229.3, -27.95) * mm, v(-229.61, -28.48) * mm, v(-229.61, -29.05) * mm]});
            skFitSpline(sketch, "E2320", {"points": [v(-229.61, -29.05) * mm, v(-229.61, -29.94) * mm, v(-228.9, -30.65) * mm, v(-228.01, -30.65) * mm]});
            skFitSpline(sketch, "E2321", {"points": [v(-228.01, -30.65) * mm, v(-227.13, -30.65) * mm, v(-226.41, -29.94) * mm, v(-226.41, -29.05) * mm]});
            skFitSpline(sketch, "E2322", {"points": [v(-255.1, -18.67) * mm, v(-255.1, -18.1) * mm, v(-255.41, -17.57) * mm, v(-255.9, -17.28) * mm]});
            skFitSpline(sketch, "E2323", {"points": [v(-255.9, -17.28) * mm, v(-256.4, -17) * mm, v(-257.01, -17) * mm, v(-257.5, -17.28) * mm]});
            skFitSpline(sketch, "E2324", {"points": [v(-257.5, -17.28) * mm, v(-258, -17.57) * mm, v(-258.3, -18.1) * mm, v(-258.3, -18.67) * mm]});
            skFitSpline(sketch, "E2325", {"points": [v(-258.3, -18.67) * mm, v(-258.3, -19.24) * mm, v(-258, -19.77) * mm, v(-257.5, -20.05) * mm]});
            skFitSpline(sketch, "E2326", {"points": [v(-257.5, -20.05) * mm, v(-257.01, -20.34) * mm, v(-256.4, -20.34) * mm, v(-255.9, -20.05) * mm]});
            skFitSpline(sketch, "E2327", {"points": [v(-255.9, -20.05) * mm, v(-255.41, -19.77) * mm, v(-255.1, -19.24) * mm, v(-255.1, -18.67) * mm]});
            skFitSpline(sketch, "E2328", {"points": [v(-255.1, -38.67) * mm, v(-255.1, -38.1) * mm, v(-255.41, -37.57) * mm, v(-255.9, -37.28) * mm]});
            skFitSpline(sketch, "E2329", {"points": [v(-255.9, -37.28) * mm, v(-256.4, -37) * mm, v(-257.01, -37) * mm, v(-257.5, -37.28) * mm]});
            skFitSpline(sketch, "E2330", {"points": [v(-257.5, -37.28) * mm, v(-258, -37.57) * mm, v(-258.3, -38.1) * mm, v(-258.3, -38.67) * mm]});
            skFitSpline(sketch, "E2331", {"points": [v(-258.3, -38.67) * mm, v(-258.3, -39.24) * mm, v(-258, -39.77) * mm, v(-257.5, -40.05) * mm]});
            skFitSpline(sketch, "E2332", {"points": [v(-257.5, -40.05) * mm, v(-257.01, -40.34) * mm, v(-256.4, -40.34) * mm, v(-255.9, -40.05) * mm]});
            skFitSpline(sketch, "E2333", {"points": [v(-255.9, -40.05) * mm, v(-255.41, -39.77) * mm, v(-255.1, -39.24) * mm, v(-255.1, -38.67) * mm]});
            skFitSpline(sketch, "E2334", {"points": [v(-286.1, -18.67) * mm, v(-286.1, -18.1) * mm, v(-286.41, -17.57) * mm, v(-286.9, -17.28) * mm]});
            skFitSpline(sketch, "E2335", {"points": [v(-286.9, -17.28) * mm, v(-287.4, -17) * mm, v(-288.01, -17) * mm, v(-288.5, -17.28) * mm]});
            skFitSpline(sketch, "E2336", {"points": [v(-288.5, -17.28) * mm, v(-289, -17.57) * mm, v(-289.3, -18.1) * mm, v(-289.3, -18.67) * mm]});
            skFitSpline(sketch, "E2337", {"points": [v(-289.3, -18.67) * mm, v(-289.3, -19.24) * mm, v(-289, -19.77) * mm, v(-288.5, -20.05) * mm]});
            skFitSpline(sketch, "E2338", {"points": [v(-288.5, -20.05) * mm, v(-288.01, -20.34) * mm, v(-287.4, -20.34) * mm, v(-286.9, -20.05) * mm]});
            skFitSpline(sketch, "E2339", {"points": [v(-286.9, -20.05) * mm, v(-286.41, -19.77) * mm, v(-286.1, -19.24) * mm, v(-286.1, -18.67) * mm]});
            skFitSpline(sketch, "E2340", {"points": [v(-286.1, -38.67) * mm, v(-286.1, -38.1) * mm, v(-286.41, -37.57) * mm, v(-286.9, -37.28) * mm]});
            skFitSpline(sketch, "E2341", {"points": [v(-286.9, -37.28) * mm, v(-287.4, -37) * mm, v(-288.01, -37) * mm, v(-288.5, -37.28) * mm]});
            skFitSpline(sketch, "E2342", {"points": [v(-288.5, -37.28) * mm, v(-289, -37.57) * mm, v(-289.3, -38.1) * mm, v(-289.3, -38.67) * mm]});
            skFitSpline(sketch, "E2343", {"points": [v(-289.3, -38.67) * mm, v(-289.3, -39.24) * mm, v(-289, -39.77) * mm, v(-288.5, -40.05) * mm]});
            skFitSpline(sketch, "E2344", {"points": [v(-288.5, -40.05) * mm, v(-288.01, -40.34) * mm, v(-287.4, -40.34) * mm, v(-286.9, -40.05) * mm]});
            skFitSpline(sketch, "E2345", {"points": [v(-286.9, -40.05) * mm, v(-286.41, -39.77) * mm, v(-286.1, -39.24) * mm, v(-286.1, -38.67) * mm]});
            skFitSpline(sketch, "E2346", {"points": [v(-340.28, -28.67) * mm, v(-340.28, -28.1) * mm, v(-340.59, -27.57) * mm, v(-341.08, -27.28) * mm]});
            skFitSpline(sketch, "E2347", {"points": [v(-341.08, -27.28) * mm, v(-341.58, -27) * mm, v(-342.19, -27) * mm, v(-342.68, -27.28) * mm]});
            skFitSpline(sketch, "E2348", {"points": [v(-342.68, -27.28) * mm, v(-343.18, -27.57) * mm, v(-343.48, -28.1) * mm, v(-343.48, -28.67) * mm]});
            skFitSpline(sketch, "E2349", {"points": [v(-343.48, -28.67) * mm, v(-343.48, -29.24) * mm, v(-343.18, -29.77) * mm, v(-342.68, -30.05) * mm]});
            skFitSpline(sketch, "E2350", {"points": [v(-342.68, -30.05) * mm, v(-342.19, -30.34) * mm, v(-341.58, -30.34) * mm, v(-341.08, -30.05) * mm]});
            skFitSpline(sketch, "E2351", {"points": [v(-341.08, -30.05) * mm, v(-340.59, -29.77) * mm, v(-340.28, -29.24) * mm, v(-340.28, -28.67) * mm]});
            skFitSpline(sketch, "E2352", {"points": [v(-325.1, -9.35) * mm, v(-324.97, -9.77) * mm, v(-324.59, -10.05) * mm, v(-324.15, -10.05) * mm]});
            skFitSpline(sketch, "E2353", {"points": [v(-326.67, -4.37) * mm, v(-326.8, -3.95) * mm, v(-327.18, -3.67) * mm, v(-327.62, -3.67) * mm]});
            skFitSpline(sketch, "E2354", {"points": [v(-119.27, -10.05) * mm, v(-118.83, -10.05) * mm, v(-118.45, -9.77) * mm, v(-118.32, -9.35) * mm]});
            skFitSpline(sketch, "E2355", {"points": [v(-115.8, -3.67) * mm, v(-116.24, -3.67) * mm, v(-116.63, -3.95) * mm, v(-116.76, -4.37) * mm]});
            skFitSpline(sketch, "E2356", {"points": [v(-140.4, -56.05) * mm, v(-140.2, -56.05) * mm, v(-140.04, -55.95) * mm, v(-139.95, -55.79) * mm]});
            skFitSpline(sketch, "E2357", {"points": [v(-139.95, -55.79) * mm, v(-139.86, -55.62) * mm, v(-139.87, -55.42) * mm, v(-139.98, -55.27) * mm]});
            skFitSpline(sketch, "E2358", {"points": [v(-133.44, -55.27) * mm, v(-133.54, -55.42) * mm, v(-133.55, -55.62) * mm, v(-133.47, -55.79) * mm]});
            skFitSpline(sketch, "E2359", {"points": [v(-133.47, -55.79) * mm, v(-133.38, -55.95) * mm, v(-133.21, -56.05) * mm, v(-133.03, -56.05) * mm]});
            skFitSpline(sketch, "E2360", {"points": [v(-316.71, -54.05) * mm, v(-316.71, -55.15) * mm, v(-315.82, -56.05) * mm, v(-314.71, -56.05) * mm]});
            skFitSpline(sketch, "E2361", {"points": [v(-298.71, -56.05) * mm, v(-297.6, -56.05) * mm, v(-296.71, -55.16) * mm, v(-296.71, -54.05) * mm]});
            skFitSpline(sketch, "E2362", {"points": [v(-310.4, -56.05) * mm, v(-310.21, -56.05) * mm, v(-310.04, -55.95) * mm, v(-309.95, -55.79) * mm]});
            skFitSpline(sketch, "E2363", {"points": [v(-309.95, -55.79) * mm, v(-309.87, -55.62) * mm, v(-309.88, -55.42) * mm, v(-309.98, -55.27) * mm]});
            skFitSpline(sketch, "E2364", {"points": [v(-303.44, -55.27) * mm, v(-303.55, -55.42) * mm, v(-303.56, -55.62) * mm, v(-303.47, -55.79) * mm]});
            skFitSpline(sketch, "E2365", {"points": [v(-303.47, -55.79) * mm, v(-303.38, -55.95) * mm, v(-303.21, -56.05) * mm, v(-303.03, -56.05) * mm]});
            skFitSpline(sketch, "E2366", {"points": [v(-303.44, -55.27) * mm, v(-302.33, -53.62) * mm, v(-302.6, -51.4) * mm, v(-304.1, -50.1) * mm]});
            skFitSpline(sketch, "E2367", {"points": [v(-304.1, -50.1) * mm, v(-305.6, -48.78) * mm, v(-307.83, -48.78) * mm, v(-309.32, -50.1) * mm]});
            skFitSpline(sketch, "E2368", {"points": [v(-309.32, -50.1) * mm, v(-310.82, -51.4) * mm, v(-311.1, -53.62) * mm, v(-309.98, -55.27) * mm]});
            skLineSegment(sketch, "E2369", {"start": v(-314.71, -56.05) * mm, "end": v(-310.4, -56.05) * mm});
            skLineSegment(sketch, "E2370", {"start": v(-303.03, -56.05) * mm, "end": v(-298.71, -56.05) * mm});
            skLineSegment(sketch, "E2371", {"start": v(-296.71, -54.05) * mm, "end": v(-296.71, -48.55) * mm});
            skLineSegment(sketch, "E2372", {"start": v(-316.71, -48.55) * mm, "end": v(-316.71, -54.05) * mm});
            skFitSpline(sketch, "E2373", {"points": [v(-346.88, 52.9) * mm, v(-349.65, 52.9) * mm, v(-351.88, 50.67) * mm, v(-351.88, 47.9) * mm]});
            skLineSegment(sketch, "E2374", {"start": v(-119.27, 46.52) * mm, "end": v(-324.15, 46.52) * mm});
            skFitSpline(sketch, "E2375", {"points": [v(-351.88, 13.52) * mm, v(-351.88, 10.76) * mm, v(-349.65, 8.52) * mm, v(-346.88, 8.52) * mm]});
            skLineSegment(sketch, "E2376", {"start": v(-325.1, 47.22) * mm, "end": v(-326.66, 52.2) * mm});
            skFitSpline(sketch, "E2377", {"points": [v(-316.71, 8.02) * mm, v(-316.71, 8.3) * mm, v(-316.94, 8.52) * mm, v(-317.21, 8.52) * mm]});
            skFitSpline(sketch, "E2378", {"points": [v(-296.21, 8.52) * mm, v(-296.34, 8.52) * mm, v(-296.47, 8.47) * mm, v(-296.57, 8.37) * mm]});
            skFitSpline(sketch, "E2379", {"points": [v(-296.57, 8.37) * mm, v(-296.66, 8.28) * mm, v(-296.71, 8.15) * mm, v(-296.71, 8.02) * mm]});
            skLineSegment(sketch, "E2380", {"start": v(-327.62, 52.9) * mm, "end": v(-346.88, 52.9) * mm});
            skFitSpline(sketch, "E2381", {"points": [v(-146.7, 8.02) * mm, v(-146.7, 8.3) * mm, v(-146.93, 8.52) * mm, v(-147.2, 8.52) * mm]});
            skLineSegment(sketch, "E2382", {"start": v(-351.88, 47.9) * mm, "end": v(-351.88, 13.52) * mm});
            skFitSpline(sketch, "E2383", {"points": [v(-146.7, 2.52) * mm, v(-146.7, 1.42) * mm, v(-145.81, 0.52) * mm, v(-144.7, 0.52) * mm]});
            skLineSegment(sketch, "E2384", {"start": v(-346.88, 8.52) * mm, "end": v(-317.21, 8.52) * mm});
            skFitSpline(sketch, "E2385", {"points": [v(-133.44, 1.3) * mm, v(-132.32, 2.95) * mm, v(-132.6, 5.17) * mm, v(-134.1, 6.48) * mm]});
            skFitSpline(sketch, "E2386", {"points": [v(-134.1, 6.48) * mm, v(-135.6, 7.8) * mm, v(-137.83, 7.8) * mm, v(-139.32, 6.48) * mm]});
            skFitSpline(sketch, "E2387", {"points": [v(-139.32, 6.48) * mm, v(-140.81, 5.17) * mm, v(-141.1, 2.95) * mm, v(-139.98, 1.3) * mm]});
            skLineSegment(sketch, "E2388", {"start": v(-296.21, 8.52) * mm, "end": v(-147.2, 8.52) * mm});
            skFitSpline(sketch, "E2389", {"points": [v(-128.7, 0.52) * mm, v(-128.18, 0.52) * mm, v(-127.67, 0.73) * mm, v(-127.3, 1.1) * mm]});
            skFitSpline(sketch, "E2390", {"points": [v(-127.3, 1.1) * mm, v(-126.92, 1.48) * mm, v(-126.7, 2) * mm, v(-126.7, 2.52) * mm]});
            skLineSegment(sketch, "E2391", {"start": v(-146.7, 8.02) * mm, "end": v(-146.7, 2.52) * mm});
            skFitSpline(sketch, "E2392", {"points": [v(-126.2, 8.52) * mm, v(-126.48, 8.52) * mm, v(-126.7, 8.3) * mm, v(-126.7, 8.02) * mm]});
            skLineSegment(sketch, "E2393", {"start": v(-144.7, 0.52) * mm, "end": v(-140.4, 0.52) * mm});
            skFitSpline(sketch, "E2394", {"points": [v(-96.54, 8.52) * mm, v(-93.78, 8.52) * mm, v(-91.54, 10.76) * mm, v(-91.54, 13.52) * mm]});
            skLineSegment(sketch, "E2395", {"start": v(-133.02, 0.52) * mm, "end": v(-128.7, 0.52) * mm});
            skFitSpline(sketch, "E2396", {"points": [v(-91.54, 47.9) * mm, v(-91.54, 50.67) * mm, v(-93.78, 52.9) * mm, v(-96.54, 52.9) * mm]});
            skLineSegment(sketch, "E2397", {"start": v(-126.7, 2.52) * mm, "end": v(-126.7, 8.02) * mm});
            skLineSegment(sketch, "E2398", {"start": v(-126.2, 8.52) * mm, "end": v(-96.54, 8.52) * mm});
            skFitSpline(sketch, "E2399", {"points": [v(-102.32, 35.4) * mm, v(-102.5, 35.4) * mm, v(-102.66, 35.31) * mm, v(-102.75, 35.16) * mm]});
            skFitSpline(sketch, "E2400", {"points": [v(-103.44, 35.84) * mm, v(-103.62, 35.74) * mm, v(-103.72, 35.53) * mm, v(-103.68, 35.32) * mm]});
            skFitSpline(sketch, "E2401", {"points": [v(-103.68, 35.32) * mm, v(-103.64, 35.11) * mm, v(-103.48, 34.95) * mm, v(-103.27, 34.91) * mm]});
            skFitSpline(sketch, "E2402", {"points": [v(-103.27, 34.91) * mm, v(-103.07, 34.88) * mm, v(-102.86, 34.98) * mm, v(-102.75, 35.16) * mm]});
            skFitSpline(sketch, "E2403", {"points": [v(-103.44, 35.84) * mm, v(-103.28, 35.93) * mm, v(-103.19, 36.1) * mm, v(-103.19, 36.27) * mm]});
            skLineSegment(sketch, "E2404", {"start": v(-91.54, 13.52) * mm, "end": v(-91.54, 47.9) * mm});
            skFitSpline(sketch, "E2405", {"points": [v(-103.19, 40.74) * mm, v(-103.19, 40.92) * mm, v(-103.28, 41.08) * mm, v(-103.44, 41.17) * mm]});
            skFitSpline(sketch, "E2406", {"points": [v(-102.75, 41.86) * mm, v(-102.86, 42.04) * mm, v(-103.07, 42.14) * mm, v(-103.27, 42.1) * mm]});
            skFitSpline(sketch, "E2407", {"points": [v(-103.27, 42.1) * mm, v(-103.48, 42.06) * mm, v(-103.64, 41.9) * mm, v(-103.68, 41.7) * mm]});
            skFitSpline(sketch, "E2408", {"points": [v(-103.68, 41.7) * mm, v(-103.72, 41.49) * mm, v(-103.62, 41.28) * mm, v(-103.44, 41.17) * mm]});
            skFitSpline(sketch, "E2409", {"points": [v(-102.75, 41.86) * mm, v(-102.66, 41.7) * mm, v(-102.5, 41.6) * mm, v(-102.32, 41.6) * mm]});
            skLineSegment(sketch, "E2410", {"start": v(-96.54, 52.9) * mm, "end": v(-115.8, 52.9) * mm});
            skFitSpline(sketch, "E2411", {"points": [v(-100.75, 41.6) * mm, v(-100.57, 41.6) * mm, v(-100.4, 41.7) * mm, v(-100.32, 41.86) * mm]});
            skFitSpline(sketch, "E2412", {"points": [v(-99.64, 41.17) * mm, v(-99.45, 41.28) * mm, v(-99.36, 41.49) * mm, v(-99.4, 41.7) * mm]});
            skFitSpline(sketch, "E2413", {"points": [v(-99.4, 41.7) * mm, v(-99.43, 41.9) * mm, v(-99.6, 42.06) * mm, v(-99.8, 42.1) * mm]});
            skFitSpline(sketch, "E2414", {"points": [v(-99.8, 42.1) * mm, v(-100, 42.14) * mm, v(-100.21, 42.04) * mm, v(-100.32, 41.86) * mm]});
            skFitSpline(sketch, "E2415", {"points": [v(-99.64, 41.17) * mm, v(-99.8, 41.08) * mm, v(-99.89, 40.92) * mm, v(-99.89, 40.74) * mm]});
            skLineSegment(sketch, "E2416", {"start": v(-116.76, 52.2) * mm, "end": v(-118.32, 47.22) * mm});
            skFitSpline(sketch, "E2417", {"points": [v(-99.89, 36.27) * mm, v(-99.89, 36.1) * mm, v(-99.8, 35.93) * mm, v(-99.64, 35.84) * mm]});
            skFitSpline(sketch, "E2418", {"points": [v(-100.32, 35.16) * mm, v(-100.21, 34.98) * mm, v(-100, 34.88) * mm, v(-99.8, 34.91) * mm]});
            skFitSpline(sketch, "E2419", {"points": [v(-99.8, 34.91) * mm, v(-99.6, 34.95) * mm, v(-99.43, 35.11) * mm, v(-99.4, 35.32) * mm]});
            skFitSpline(sketch, "E2420", {"points": [v(-99.4, 35.32) * mm, v(-99.36, 35.53) * mm, v(-99.45, 35.74) * mm, v(-99.64, 35.84) * mm]});
            skFitSpline(sketch, "E2421", {"points": [v(-100.32, 35.16) * mm, v(-100.4, 35.31) * mm, v(-100.57, 35.4) * mm, v(-100.75, 35.4) * mm]});
            skLineSegment(sketch, "E2422", {"start": v(-103.19, 36.27) * mm, "end": v(-103.19, 40.74) * mm});
            skFitSpline(sketch, "E2423", {"points": [v(-102.32, 14.2) * mm, v(-102.5, 14.2) * mm, v(-102.66, 14.11) * mm, v(-102.75, 13.96) * mm]});
            skFitSpline(sketch, "E2424", {"points": [v(-103.44, 14.64) * mm, v(-103.62, 14.54) * mm, v(-103.72, 14.33) * mm, v(-103.68, 14.12) * mm]});
            skFitSpline(sketch, "E2425", {"points": [v(-103.68, 14.12) * mm, v(-103.64, 13.91) * mm, v(-103.48, 13.75) * mm, v(-103.27, 13.71) * mm]});
            skFitSpline(sketch, "E2426", {"points": [v(-103.27, 13.71) * mm, v(-103.07, 13.68) * mm, v(-102.86, 13.78) * mm, v(-102.75, 13.96) * mm]});
            skFitSpline(sketch, "E2427", {"points": [v(-103.44, 14.64) * mm, v(-103.28, 14.73) * mm, v(-103.19, 14.9) * mm, v(-103.19, 15.07) * mm]});
            skLineSegment(sketch, "E2428", {"start": v(-102.32, 41.6) * mm, "end": v(-100.75, 41.6) * mm});
            skFitSpline(sketch, "E2429", {"points": [v(-103.19, 19.54) * mm, v(-103.19, 19.72) * mm, v(-103.28, 19.88) * mm, v(-103.44, 19.97) * mm]});
            skFitSpline(sketch, "E2430", {"points": [v(-102.75, 20.66) * mm, v(-102.86, 20.84) * mm, v(-103.07, 20.94) * mm, v(-103.27, 20.9) * mm]});
            skFitSpline(sketch, "E2431", {"points": [v(-103.27, 20.9) * mm, v(-103.48, 20.86) * mm, v(-103.64, 20.7) * mm, v(-103.68, 20.5) * mm]});
            skFitSpline(sketch, "E2432", {"points": [v(-103.68, 20.5) * mm, v(-103.72, 20.29) * mm, v(-103.62, 20.08) * mm, v(-103.44, 19.97) * mm]});
            skFitSpline(sketch, "E2433", {"points": [v(-102.75, 20.66) * mm, v(-102.66, 20.5) * mm, v(-102.5, 20.4) * mm, v(-102.32, 20.4) * mm]});
            skLineSegment(sketch, "E2434", {"start": v(-99.89, 40.74) * mm, "end": v(-99.89, 36.27) * mm});
            skFitSpline(sketch, "E2435", {"points": [v(-100.75, 20.4) * mm, v(-100.57, 20.4) * mm, v(-100.4, 20.5) * mm, v(-100.32, 20.66) * mm]});
            skFitSpline(sketch, "E2436", {"points": [v(-99.64, 19.97) * mm, v(-99.45, 20.08) * mm, v(-99.36, 20.29) * mm, v(-99.4, 20.5) * mm]});
            skFitSpline(sketch, "E2437", {"points": [v(-99.4, 20.5) * mm, v(-99.43, 20.7) * mm, v(-99.6, 20.86) * mm, v(-99.8, 20.9) * mm]});
            skFitSpline(sketch, "E2438", {"points": [v(-99.8, 20.9) * mm, v(-100, 20.94) * mm, v(-100.21, 20.84) * mm, v(-100.32, 20.66) * mm]});
            skFitSpline(sketch, "E2439", {"points": [v(-99.64, 19.97) * mm, v(-99.8, 19.88) * mm, v(-99.89, 19.72) * mm, v(-99.89, 19.54) * mm]});
            skLineSegment(sketch, "E2440", {"start": v(-100.75, 35.4) * mm, "end": v(-102.32, 35.4) * mm});
            skFitSpline(sketch, "E2441", {"points": [v(-99.89, 15.07) * mm, v(-99.89, 14.9) * mm, v(-99.8, 14.73) * mm, v(-99.64, 14.64) * mm]});
            skFitSpline(sketch, "E2442", {"points": [v(-100.32, 13.96) * mm, v(-100.21, 13.78) * mm, v(-100, 13.68) * mm, v(-99.8, 13.71) * mm]});
            skFitSpline(sketch, "E2443", {"points": [v(-99.8, 13.71) * mm, v(-99.6, 13.75) * mm, v(-99.43, 13.91) * mm, v(-99.4, 14.12) * mm]});
            skFitSpline(sketch, "E2444", {"points": [v(-99.4, 14.12) * mm, v(-99.36, 14.33) * mm, v(-99.45, 14.54) * mm, v(-99.64, 14.64) * mm]});
            skFitSpline(sketch, "E2445", {"points": [v(-100.32, 13.96) * mm, v(-100.4, 14.11) * mm, v(-100.57, 14.2) * mm, v(-100.75, 14.2) * mm]});
            skLineSegment(sketch, "E2446", {"start": v(-103.19, 15.07) * mm, "end": v(-103.19, 19.54) * mm});
            skFitSpline(sketch, "E2447", {"points": [v(-216.2, 35.02) * mm, v(-216.37, 35.02) * mm, v(-216.54, 34.92) * mm, v(-216.63, 34.77) * mm]});
            skFitSpline(sketch, "E2448", {"points": [v(-217.31, 35.45) * mm, v(-217.5, 35.35) * mm, v(-217.59, 35.14) * mm, v(-217.55, 34.93) * mm]});
            skFitSpline(sketch, "E2449", {"points": [v(-217.55, 34.93) * mm, v(-217.52, 34.73) * mm, v(-217.35, 34.56) * mm, v(-217.15, 34.53) * mm]});
            skFitSpline(sketch, "E2450", {"points": [v(-217.15, 34.53) * mm, v(-216.94, 34.5) * mm, v(-216.73, 34.59) * mm, v(-216.63, 34.77) * mm]});
            skFitSpline(sketch, "E2451", {"points": [v(-217.31, 35.45) * mm, v(-217.16, 35.54) * mm, v(-217.06, 35.7) * mm, v(-217.06, 35.89) * mm]});
            skLineSegment(sketch, "E2452", {"start": v(-102.32, 20.4) * mm, "end": v(-100.75, 20.4) * mm});
            skFitSpline(sketch, "E2453", {"points": [v(-217.06, 40.35) * mm, v(-217.06, 40.53) * mm, v(-217.16, 40.7) * mm, v(-217.31, 40.79) * mm]});
            skFitSpline(sketch, "E2454", {"points": [v(-216.63, 41.47) * mm, v(-216.73, 41.65) * mm, v(-216.94, 41.75) * mm, v(-217.15, 41.71) * mm]});
            skFitSpline(sketch, "E2455", {"points": [v(-217.15, 41.71) * mm, v(-217.35, 41.68) * mm, v(-217.52, 41.51) * mm, v(-217.55, 41.3) * mm]});
            skFitSpline(sketch, "E2456", {"points": [v(-217.55, 41.3) * mm, v(-217.59, 41.1) * mm, v(-217.5, 40.9) * mm, v(-217.31, 40.79) * mm]});
            skFitSpline(sketch, "E2457", {"points": [v(-216.63, 41.47) * mm, v(-216.54, 41.31) * mm, v(-216.37, 41.22) * mm, v(-216.2, 41.22) * mm]});
            skLineSegment(sketch, "E2458", {"start": v(-99.89, 19.54) * mm, "end": v(-99.89, 15.07) * mm});
            skFitSpline(sketch, "E2459", {"points": [v(-214.63, 41.22) * mm, v(-214.45, 41.22) * mm, v(-214.28, 41.31) * mm, v(-214.2, 41.47) * mm]});
            skFitSpline(sketch, "E2460", {"points": [v(-213.51, 40.79) * mm, v(-213.33, 40.9) * mm, v(-213.23, 41.1) * mm, v(-213.27, 41.3) * mm]});
            skFitSpline(sketch, "E2461", {"points": [v(-213.27, 41.3) * mm, v(-213.3, 41.51) * mm, v(-213.47, 41.68) * mm, v(-213.67, 41.71) * mm]});
            skFitSpline(sketch, "E2462", {"points": [v(-213.67, 41.71) * mm, v(-213.88, 41.75) * mm, v(-214.09, 41.65) * mm, v(-214.2, 41.47) * mm]});
            skFitSpline(sketch, "E2463", {"points": [v(-213.51, 40.79) * mm, v(-213.67, 40.7) * mm, v(-213.76, 40.53) * mm, v(-213.76, 40.35) * mm]});
            skLineSegment(sketch, "E2464", {"start": v(-100.75, 14.2) * mm, "end": v(-102.32, 14.2) * mm});
            skFitSpline(sketch, "E2465", {"points": [v(-213.76, 35.89) * mm, v(-213.76, 35.7) * mm, v(-213.67, 35.54) * mm, v(-213.51, 35.45) * mm]});
            skFitSpline(sketch, "E2466", {"points": [v(-214.2, 34.77) * mm, v(-214.09, 34.59) * mm, v(-213.88, 34.5) * mm, v(-213.67, 34.53) * mm]});
            skFitSpline(sketch, "E2467", {"points": [v(-213.67, 34.53) * mm, v(-213.47, 34.56) * mm, v(-213.3, 34.73) * mm, v(-213.27, 34.93) * mm]});
            skFitSpline(sketch, "E2468", {"points": [v(-213.27, 34.93) * mm, v(-213.23, 35.14) * mm, v(-213.33, 35.35) * mm, v(-213.51, 35.45) * mm]});
            skFitSpline(sketch, "E2469", {"points": [v(-214.2, 34.77) * mm, v(-214.28, 34.92) * mm, v(-214.45, 35.02) * mm, v(-214.63, 35.02) * mm]});
            skLineSegment(sketch, "E2470", {"start": v(-217.06, 35.89) * mm, "end": v(-217.06, 40.35) * mm});
            skFitSpline(sketch, "E2471", {"points": [v(-216.2, 13.82) * mm, v(-216.37, 13.82) * mm, v(-216.54, 13.72) * mm, v(-216.63, 13.57) * mm]});
            skFitSpline(sketch, "E2472", {"points": [v(-217.31, 14.25) * mm, v(-217.5, 14.15) * mm, v(-217.59, 13.94) * mm, v(-217.55, 13.73) * mm]});
            skFitSpline(sketch, "E2473", {"points": [v(-217.55, 13.73) * mm, v(-217.52, 13.53) * mm, v(-217.35, 13.36) * mm, v(-217.15, 13.33) * mm]});
            skFitSpline(sketch, "E2474", {"points": [v(-217.15, 13.33) * mm, v(-216.94, 13.3) * mm, v(-216.73, 13.39) * mm, v(-216.63, 13.57) * mm]});
            skFitSpline(sketch, "E2475", {"points": [v(-217.31, 14.25) * mm, v(-217.16, 14.34) * mm, v(-217.06, 14.5) * mm, v(-217.06, 14.69) * mm]});
            skLineSegment(sketch, "E2476", {"start": v(-216.2, 41.22) * mm, "end": v(-214.63, 41.22) * mm});
            skFitSpline(sketch, "E2477", {"points": [v(-217.06, 19.15) * mm, v(-217.06, 19.33) * mm, v(-217.16, 19.5) * mm, v(-217.31, 19.59) * mm]});
            skFitSpline(sketch, "E2478", {"points": [v(-216.63, 20.27) * mm, v(-216.73, 20.45) * mm, v(-216.94, 20.55) * mm, v(-217.15, 20.51) * mm]});
            skFitSpline(sketch, "E2479", {"points": [v(-217.15, 20.51) * mm, v(-217.35, 20.48) * mm, v(-217.52, 20.31) * mm, v(-217.55, 20.1) * mm]});
            skFitSpline(sketch, "E2480", {"points": [v(-217.55, 20.1) * mm, v(-217.59, 19.9) * mm, v(-217.5, 19.7) * mm, v(-217.31, 19.59) * mm]});
            skFitSpline(sketch, "E2481", {"points": [v(-216.63, 20.27) * mm, v(-216.54, 20.11) * mm, v(-216.37, 20.02) * mm, v(-216.2, 20.02) * mm]});
            skLineSegment(sketch, "E2482", {"start": v(-213.76, 40.35) * mm, "end": v(-213.76, 35.89) * mm});
            skFitSpline(sketch, "E2483", {"points": [v(-214.63, 20.02) * mm, v(-214.45, 20.02) * mm, v(-214.28, 20.11) * mm, v(-214.2, 20.27) * mm]});
            skFitSpline(sketch, "E2484", {"points": [v(-213.51, 19.59) * mm, v(-213.33, 19.7) * mm, v(-213.23, 19.9) * mm, v(-213.27, 20.1) * mm]});
            skFitSpline(sketch, "E2485", {"points": [v(-213.27, 20.1) * mm, v(-213.3, 20.31) * mm, v(-213.47, 20.48) * mm, v(-213.67, 20.51) * mm]});
            skFitSpline(sketch, "E2486", {"points": [v(-213.67, 20.51) * mm, v(-213.88, 20.55) * mm, v(-214.09, 20.45) * mm, v(-214.2, 20.27) * mm]});
            skFitSpline(sketch, "E2487", {"points": [v(-213.51, 19.59) * mm, v(-213.67, 19.5) * mm, v(-213.76, 19.33) * mm, v(-213.76, 19.15) * mm]});
            skLineSegment(sketch, "E2488", {"start": v(-214.63, 35.02) * mm, "end": v(-216.2, 35.02) * mm});
            skFitSpline(sketch, "E2489", {"points": [v(-213.76, 14.69) * mm, v(-213.76, 14.5) * mm, v(-213.67, 14.34) * mm, v(-213.51, 14.25) * mm]});
            skFitSpline(sketch, "E2490", {"points": [v(-214.2, 13.57) * mm, v(-214.09, 13.39) * mm, v(-213.88, 13.3) * mm, v(-213.67, 13.33) * mm]});
            skFitSpline(sketch, "E2491", {"points": [v(-213.67, 13.33) * mm, v(-213.47, 13.36) * mm, v(-213.3, 13.53) * mm, v(-213.27, 13.73) * mm]});
            skFitSpline(sketch, "E2492", {"points": [v(-213.27, 13.73) * mm, v(-213.23, 13.94) * mm, v(-213.33, 14.15) * mm, v(-213.51, 14.25) * mm]});
            skFitSpline(sketch, "E2493", {"points": [v(-214.2, 13.57) * mm, v(-214.28, 13.72) * mm, v(-214.45, 13.82) * mm, v(-214.63, 13.82) * mm]});
            skLineSegment(sketch, "E2494", {"start": v(-217.06, 14.69) * mm, "end": v(-217.06, 19.15) * mm});
            skFitSpline(sketch, "E2495", {"points": [v(-228.8, 35.02) * mm, v(-228.97, 35.02) * mm, v(-229.14, 34.92) * mm, v(-229.23, 34.77) * mm]});
            skFitSpline(sketch, "E2496", {"points": [v(-229.91, 35.45) * mm, v(-230.1, 35.35) * mm, v(-230.19, 35.14) * mm, v(-230.15, 34.93) * mm]});
            skFitSpline(sketch, "E2497", {"points": [v(-230.15, 34.93) * mm, v(-230.12, 34.73) * mm, v(-229.95, 34.56) * mm, v(-229.75, 34.53) * mm]});
            skFitSpline(sketch, "E2498", {"points": [v(-229.75, 34.53) * mm, v(-229.54, 34.5) * mm, v(-229.33, 34.59) * mm, v(-229.23, 34.77) * mm]});
            skFitSpline(sketch, "E2499", {"points": [v(-229.91, 35.45) * mm, v(-229.76, 35.54) * mm, v(-229.66, 35.7) * mm, v(-229.66, 35.89) * mm]});
            skLineSegment(sketch, "E2500", {"start": v(-216.2, 20.02) * mm, "end": v(-214.63, 20.02) * mm});
            skFitSpline(sketch, "E2501", {"points": [v(-229.66, 40.35) * mm, v(-229.66, 40.53) * mm, v(-229.76, 40.7) * mm, v(-229.91, 40.79) * mm]});
            skFitSpline(sketch, "E2502", {"points": [v(-229.23, 41.47) * mm, v(-229.33, 41.65) * mm, v(-229.54, 41.75) * mm, v(-229.75, 41.71) * mm]});
            skFitSpline(sketch, "E2503", {"points": [v(-229.75, 41.71) * mm, v(-229.95, 41.68) * mm, v(-230.12, 41.51) * mm, v(-230.15, 41.3) * mm]});
            skFitSpline(sketch, "E2504", {"points": [v(-230.15, 41.3) * mm, v(-230.19, 41.1) * mm, v(-230.1, 40.9) * mm, v(-229.91, 40.79) * mm]});
            skFitSpline(sketch, "E2505", {"points": [v(-229.23, 41.47) * mm, v(-229.14, 41.31) * mm, v(-228.97, 41.22) * mm, v(-228.8, 41.22) * mm]});
            skLineSegment(sketch, "E2506", {"start": v(-213.76, 19.15) * mm, "end": v(-213.76, 14.69) * mm});
            skFitSpline(sketch, "E2507", {"points": [v(-227.23, 41.22) * mm, v(-227.05, 41.22) * mm, v(-226.88, 41.31) * mm, v(-226.8, 41.47) * mm]});
            skFitSpline(sketch, "E2508", {"points": [v(-226.11, 40.79) * mm, v(-225.93, 40.9) * mm, v(-225.83, 41.1) * mm, v(-225.87, 41.3) * mm]});
            skFitSpline(sketch, "E2509", {"points": [v(-225.87, 41.3) * mm, v(-225.9, 41.51) * mm, v(-226.07, 41.68) * mm, v(-226.27, 41.71) * mm]});
            skFitSpline(sketch, "E2510", {"points": [v(-226.27, 41.71) * mm, v(-226.48, 41.75) * mm, v(-226.69, 41.65) * mm, v(-226.8, 41.47) * mm]});
            skFitSpline(sketch, "E2511", {"points": [v(-226.11, 40.79) * mm, v(-226.26, 40.7) * mm, v(-226.36, 40.53) * mm, v(-226.36, 40.35) * mm]});
            skLineSegment(sketch, "E2512", {"start": v(-214.63, 13.82) * mm, "end": v(-216.2, 13.82) * mm});
            skFitSpline(sketch, "E2513", {"points": [v(-226.36, 35.89) * mm, v(-226.36, 35.7) * mm, v(-226.26, 35.54) * mm, v(-226.11, 35.45) * mm]});
            skFitSpline(sketch, "E2514", {"points": [v(-226.8, 34.77) * mm, v(-226.69, 34.59) * mm, v(-226.48, 34.5) * mm, v(-226.27, 34.53) * mm]});
            skFitSpline(sketch, "E2515", {"points": [v(-226.27, 34.53) * mm, v(-226.07, 34.56) * mm, v(-225.9, 34.73) * mm, v(-225.87, 34.93) * mm]});
            skFitSpline(sketch, "E2516", {"points": [v(-225.87, 34.93) * mm, v(-225.83, 35.14) * mm, v(-225.93, 35.35) * mm, v(-226.11, 35.45) * mm]});
            skFitSpline(sketch, "E2517", {"points": [v(-226.8, 34.77) * mm, v(-226.88, 34.92) * mm, v(-227.05, 35.02) * mm, v(-227.23, 35.02) * mm]});
            skLineSegment(sketch, "E2518", {"start": v(-229.66, 35.89) * mm, "end": v(-229.66, 40.35) * mm});
            skFitSpline(sketch, "E2519", {"points": [v(-228.8, 13.82) * mm, v(-228.97, 13.82) * mm, v(-229.14, 13.72) * mm, v(-229.23, 13.57) * mm]});
            skFitSpline(sketch, "E2520", {"points": [v(-229.91, 14.25) * mm, v(-230.1, 14.15) * mm, v(-230.19, 13.94) * mm, v(-230.15, 13.73) * mm]});
            skFitSpline(sketch, "E2521", {"points": [v(-230.15, 13.73) * mm, v(-230.12, 13.53) * mm, v(-229.95, 13.36) * mm, v(-229.75, 13.33) * mm]});
            skFitSpline(sketch, "E2522", {"points": [v(-229.75, 13.33) * mm, v(-229.54, 13.3) * mm, v(-229.33, 13.39) * mm, v(-229.23, 13.57) * mm]});
            skFitSpline(sketch, "E2523", {"points": [v(-229.91, 14.25) * mm, v(-229.76, 14.34) * mm, v(-229.66, 14.5) * mm, v(-229.66, 14.69) * mm]});
            skLineSegment(sketch, "E2524", {"start": v(-228.8, 41.22) * mm, "end": v(-227.23, 41.22) * mm});
            skFitSpline(sketch, "E2525", {"points": [v(-229.66, 19.15) * mm, v(-229.66, 19.33) * mm, v(-229.76, 19.5) * mm, v(-229.91, 19.59) * mm]});
            skFitSpline(sketch, "E2526", {"points": [v(-229.23, 20.27) * mm, v(-229.33, 20.45) * mm, v(-229.54, 20.55) * mm, v(-229.75, 20.51) * mm]});
            skFitSpline(sketch, "E2527", {"points": [v(-229.75, 20.51) * mm, v(-229.95, 20.48) * mm, v(-230.12, 20.31) * mm, v(-230.15, 20.1) * mm]});
            skFitSpline(sketch, "E2528", {"points": [v(-230.15, 20.1) * mm, v(-230.19, 19.9) * mm, v(-230.1, 19.7) * mm, v(-229.91, 19.59) * mm]});
            skFitSpline(sketch, "E2529", {"points": [v(-229.23, 20.27) * mm, v(-229.14, 20.11) * mm, v(-228.97, 20.02) * mm, v(-228.8, 20.02) * mm]});
            skLineSegment(sketch, "E2530", {"start": v(-226.36, 40.35) * mm, "end": v(-226.36, 35.89) * mm});
            skFitSpline(sketch, "E2531", {"points": [v(-227.23, 20.02) * mm, v(-227.05, 20.02) * mm, v(-226.88, 20.11) * mm, v(-226.8, 20.27) * mm]});
            skFitSpline(sketch, "E2532", {"points": [v(-226.11, 19.59) * mm, v(-225.93, 19.7) * mm, v(-225.83, 19.9) * mm, v(-225.87, 20.1) * mm]});
            skFitSpline(sketch, "E2533", {"points": [v(-225.87, 20.1) * mm, v(-225.9, 20.31) * mm, v(-226.07, 20.48) * mm, v(-226.27, 20.51) * mm]});
            skFitSpline(sketch, "E2534", {"points": [v(-226.27, 20.51) * mm, v(-226.48, 20.55) * mm, v(-226.69, 20.45) * mm, v(-226.8, 20.27) * mm]});
            skFitSpline(sketch, "E2535", {"points": [v(-226.11, 19.59) * mm, v(-226.26, 19.5) * mm, v(-226.36, 19.33) * mm, v(-226.36, 19.15) * mm]});
            skLineSegment(sketch, "E2536", {"start": v(-227.23, 35.02) * mm, "end": v(-228.8, 35.02) * mm});
            skFitSpline(sketch, "E2537", {"points": [v(-226.36, 14.69) * mm, v(-226.36, 14.5) * mm, v(-226.26, 14.34) * mm, v(-226.11, 14.25) * mm]});
            skFitSpline(sketch, "E2538", {"points": [v(-226.8, 13.57) * mm, v(-226.69, 13.39) * mm, v(-226.48, 13.3) * mm, v(-226.27, 13.33) * mm]});
            skFitSpline(sketch, "E2539", {"points": [v(-226.27, 13.33) * mm, v(-226.07, 13.36) * mm, v(-225.9, 13.53) * mm, v(-225.87, 13.73) * mm]});
            skFitSpline(sketch, "E2540", {"points": [v(-225.87, 13.73) * mm, v(-225.83, 13.94) * mm, v(-225.93, 14.15) * mm, v(-226.11, 14.25) * mm]});
            skFitSpline(sketch, "E2541", {"points": [v(-226.8, 13.57) * mm, v(-226.88, 13.72) * mm, v(-227.05, 13.82) * mm, v(-227.23, 13.82) * mm]});
            skLineSegment(sketch, "E2542", {"start": v(-229.66, 14.69) * mm, "end": v(-229.66, 19.15) * mm});
            skFitSpline(sketch, "E2543", {"points": [v(-340.67, 35.16) * mm, v(-340.76, 35.31) * mm, v(-340.92, 35.4) * mm, v(-341.1, 35.4) * mm]});
            skFitSpline(sketch, "E2544", {"points": [v(-340.67, 35.16) * mm, v(-340.56, 34.98) * mm, v(-340.35, 34.88) * mm, v(-340.15, 34.91) * mm]});
            skFitSpline(sketch, "E2545", {"points": [v(-340.15, 34.91) * mm, v(-339.94, 34.95) * mm, v(-339.78, 35.11) * mm, v(-339.74, 35.32) * mm]});
            skFitSpline(sketch, "E2546", {"points": [v(-339.74, 35.32) * mm, v(-339.7, 35.53) * mm, v(-339.8, 35.74) * mm, v(-339.98, 35.84) * mm]});
            skFitSpline(sketch, "E2547", {"points": [v(-340.23, 36.27) * mm, v(-340.23, 36.1) * mm, v(-340.14, 35.93) * mm, v(-339.98, 35.84) * mm]});
            skLineSegment(sketch, "E2548", {"start": v(-228.8, 20.02) * mm, "end": v(-227.23, 20.02) * mm});
            skFitSpline(sketch, "E2549", {"points": [v(-339.98, 41.17) * mm, v(-340.14, 41.08) * mm, v(-340.23, 40.92) * mm, v(-340.23, 40.74) * mm]});
            skFitSpline(sketch, "E2550", {"points": [v(-339.98, 41.17) * mm, v(-339.8, 41.28) * mm, v(-339.7, 41.49) * mm, v(-339.74, 41.7) * mm]});
            skFitSpline(sketch, "E2551", {"points": [v(-339.74, 41.7) * mm, v(-339.78, 41.9) * mm, v(-339.94, 42.06) * mm, v(-340.15, 42.1) * mm]});
            skFitSpline(sketch, "E2552", {"points": [v(-340.15, 42.1) * mm, v(-340.35, 42.14) * mm, v(-340.56, 42.04) * mm, v(-340.67, 41.86) * mm]});
            skFitSpline(sketch, "E2553", {"points": [v(-341.1, 41.6) * mm, v(-340.92, 41.6) * mm, v(-340.76, 41.7) * mm, v(-340.67, 41.86) * mm]});
            skLineSegment(sketch, "E2554", {"start": v(-226.36, 19.15) * mm, "end": v(-226.36, 14.69) * mm});
            skFitSpline(sketch, "E2555", {"points": [v(-343.1, 41.86) * mm, v(-343.01, 41.7) * mm, v(-342.85, 41.6) * mm, v(-342.67, 41.6) * mm]});
            skFitSpline(sketch, "E2556", {"points": [v(-343.1, 41.86) * mm, v(-343.2, 42.04) * mm, v(-343.41, 42.14) * mm, v(-343.62, 42.1) * mm]});
            skFitSpline(sketch, "E2557", {"points": [v(-343.62, 42.1) * mm, v(-343.83, 42.06) * mm, v(-343.99, 41.9) * mm, v(-344.03, 41.7) * mm]});
            skFitSpline(sketch, "E2558", {"points": [v(-344.03, 41.7) * mm, v(-344.06, 41.49) * mm, v(-343.97, 41.28) * mm, v(-343.78, 41.17) * mm]});
            skFitSpline(sketch, "E2559", {"points": [v(-343.53, 40.74) * mm, v(-343.53, 40.92) * mm, v(-343.63, 41.08) * mm, v(-343.78, 41.17) * mm]});
            skLineSegment(sketch, "E2560", {"start": v(-227.23, 13.82) * mm, "end": v(-228.8, 13.82) * mm});
            skFitSpline(sketch, "E2561", {"points": [v(-343.78, 35.84) * mm, v(-343.63, 35.93) * mm, v(-343.53, 36.1) * mm, v(-343.53, 36.27) * mm]});
            skFitSpline(sketch, "E2562", {"points": [v(-343.78, 35.84) * mm, v(-343.97, 35.74) * mm, v(-344.06, 35.53) * mm, v(-344.03, 35.32) * mm]});
            skFitSpline(sketch, "E2563", {"points": [v(-344.03, 35.32) * mm, v(-343.99, 35.11) * mm, v(-343.83, 34.95) * mm, v(-343.62, 34.91) * mm]});
            skFitSpline(sketch, "E2564", {"points": [v(-343.62, 34.91) * mm, v(-343.41, 34.88) * mm, v(-343.2, 34.98) * mm, v(-343.1, 35.16) * mm]});
            skFitSpline(sketch, "E2565", {"points": [v(-342.67, 35.4) * mm, v(-342.85, 35.4) * mm, v(-343.01, 35.31) * mm, v(-343.1, 35.16) * mm]});
            skLineSegment(sketch, "E2566", {"start": v(-340.23, 36.27) * mm, "end": v(-340.23, 40.74) * mm});
            skFitSpline(sketch, "E2567", {"points": [v(-340.67, 13.96) * mm, v(-340.76, 14.11) * mm, v(-340.92, 14.2) * mm, v(-341.1, 14.2) * mm]});
            skFitSpline(sketch, "E2568", {"points": [v(-340.67, 13.96) * mm, v(-340.56, 13.78) * mm, v(-340.35, 13.68) * mm, v(-340.15, 13.71) * mm]});
            skFitSpline(sketch, "E2569", {"points": [v(-340.15, 13.71) * mm, v(-339.94, 13.75) * mm, v(-339.78, 13.91) * mm, v(-339.74, 14.12) * mm]});
            skFitSpline(sketch, "E2570", {"points": [v(-339.74, 14.12) * mm, v(-339.7, 14.33) * mm, v(-339.8, 14.54) * mm, v(-339.98, 14.64) * mm]});
            skFitSpline(sketch, "E2571", {"points": [v(-340.23, 15.07) * mm, v(-340.23, 14.9) * mm, v(-340.14, 14.73) * mm, v(-339.98, 14.64) * mm]});
            skLineSegment(sketch, "E2572", {"start": v(-341.1, 41.6) * mm, "end": v(-342.67, 41.6) * mm});
            skFitSpline(sketch, "E2573", {"points": [v(-339.98, 19.97) * mm, v(-340.14, 19.88) * mm, v(-340.23, 19.72) * mm, v(-340.23, 19.54) * mm]});
            skFitSpline(sketch, "E2574", {"points": [v(-339.98, 19.97) * mm, v(-339.8, 20.08) * mm, v(-339.7, 20.29) * mm, v(-339.74, 20.5) * mm]});
            skFitSpline(sketch, "E2575", {"points": [v(-339.74, 20.5) * mm, v(-339.78, 20.7) * mm, v(-339.94, 20.86) * mm, v(-340.15, 20.9) * mm]});
            skFitSpline(sketch, "E2576", {"points": [v(-340.15, 20.9) * mm, v(-340.35, 20.94) * mm, v(-340.56, 20.84) * mm, v(-340.67, 20.66) * mm]});
            skFitSpline(sketch, "E2577", {"points": [v(-341.1, 20.4) * mm, v(-340.92, 20.4) * mm, v(-340.76, 20.5) * mm, v(-340.67, 20.66) * mm]});
            skLineSegment(sketch, "E2578", {"start": v(-343.53, 40.74) * mm, "end": v(-343.53, 36.27) * mm});
            skFitSpline(sketch, "E2579", {"points": [v(-343.1, 20.66) * mm, v(-343.01, 20.5) * mm, v(-342.85, 20.4) * mm, v(-342.67, 20.4) * mm]});
            skFitSpline(sketch, "E2580", {"points": [v(-343.1, 20.66) * mm, v(-343.2, 20.84) * mm, v(-343.41, 20.94) * mm, v(-343.62, 20.9) * mm]});
            skFitSpline(sketch, "E2581", {"points": [v(-343.62, 20.9) * mm, v(-343.83, 20.86) * mm, v(-343.99, 20.7) * mm, v(-344.03, 20.5) * mm]});
            skFitSpline(sketch, "E2582", {"points": [v(-344.03, 20.5) * mm, v(-344.06, 20.29) * mm, v(-343.97, 20.08) * mm, v(-343.78, 19.97) * mm]});
            skFitSpline(sketch, "E2583", {"points": [v(-343.53, 19.54) * mm, v(-343.53, 19.72) * mm, v(-343.63, 19.88) * mm, v(-343.78, 19.97) * mm]});
            skLineSegment(sketch, "E2584", {"start": v(-342.67, 35.4) * mm, "end": v(-341.1, 35.4) * mm});
            skFitSpline(sketch, "E2585", {"points": [v(-343.78, 14.64) * mm, v(-343.63, 14.73) * mm, v(-343.53, 14.9) * mm, v(-343.53, 15.07) * mm]});
            skFitSpline(sketch, "E2586", {"points": [v(-343.78, 14.64) * mm, v(-343.97, 14.54) * mm, v(-344.06, 14.33) * mm, v(-344.03, 14.12) * mm]});
            skFitSpline(sketch, "E2587", {"points": [v(-344.03, 14.12) * mm, v(-343.99, 13.91) * mm, v(-343.83, 13.75) * mm, v(-343.62, 13.71) * mm]});
            skFitSpline(sketch, "E2588", {"points": [v(-343.62, 13.71) * mm, v(-343.41, 13.68) * mm, v(-343.2, 13.78) * mm, v(-343.1, 13.96) * mm]});
            skFitSpline(sketch, "E2589", {"points": [v(-342.67, 14.2) * mm, v(-342.85, 14.2) * mm, v(-343.01, 14.11) * mm, v(-343.1, 13.96) * mm]});
            skLineSegment(sketch, "E2590", {"start": v(-340.23, 15.07) * mm, "end": v(-340.23, 19.54) * mm});
            skFitSpline(sketch, "E2591", {"points": [v(-99.94, 27.9) * mm, v(-99.94, 28.48) * mm, v(-100.24, 29) * mm, v(-100.74, 29.3) * mm]});
            skFitSpline(sketch, "E2592", {"points": [v(-100.74, 29.3) * mm, v(-101.23, 29.58) * mm, v(-101.84, 29.58) * mm, v(-102.34, 29.3) * mm]});
            skFitSpline(sketch, "E2593", {"points": [v(-102.34, 29.3) * mm, v(-102.83, 29) * mm, v(-103.14, 28.48) * mm, v(-103.14, 27.9) * mm]});
            skFitSpline(sketch, "E2594", {"points": [v(-103.14, 27.9) * mm, v(-103.14, 27.34) * mm, v(-102.83, 26.8) * mm, v(-102.34, 26.52) * mm]});
            skFitSpline(sketch, "E2595", {"points": [v(-102.34, 26.52) * mm, v(-101.84, 26.24) * mm, v(-101.23, 26.24) * mm, v(-100.74, 26.52) * mm]});
            skFitSpline(sketch, "E2596", {"points": [v(-100.74, 26.52) * mm, v(-100.24, 26.8) * mm, v(-99.94, 27.34) * mm, v(-99.94, 27.9) * mm]});
            skLineSegment(sketch, "E2597", {"start": v(-341.1, 20.4) * mm, "end": v(-342.67, 20.4) * mm});
            skFitSpline(sketch, "E2598", {"points": [v(-154.11, 37.9) * mm, v(-154.11, 38.48) * mm, v(-154.42, 39) * mm, v(-154.91, 39.3) * mm]});
            skFitSpline(sketch, "E2599", {"points": [v(-154.91, 39.3) * mm, v(-155.4, 39.58) * mm, v(-156.02, 39.58) * mm, v(-156.51, 39.3) * mm]});
            skFitSpline(sketch, "E2600", {"points": [v(-156.51, 39.3) * mm, v(-157, 39) * mm, v(-157.31, 38.48) * mm, v(-157.31, 37.9) * mm]});
            skFitSpline(sketch, "E2601", {"points": [v(-157.31, 37.9) * mm, v(-157.31, 37.34) * mm, v(-157, 36.8) * mm, v(-156.51, 36.52) * mm]});
            skFitSpline(sketch, "E2602", {"points": [v(-156.51, 36.52) * mm, v(-156.02, 36.24) * mm, v(-155.4, 36.24) * mm, v(-154.91, 36.52) * mm]});
            skFitSpline(sketch, "E2603", {"points": [v(-154.91, 36.52) * mm, v(-154.42, 36.8) * mm, v(-154.11, 37.34) * mm, v(-154.11, 37.9) * mm]});
            skLineSegment(sketch, "E2604", {"start": v(-343.53, 19.54) * mm, "end": v(-343.53, 15.07) * mm});
            skFitSpline(sketch, "E2605", {"points": [v(-154.11, 17.9) * mm, v(-154.11, 18.48) * mm, v(-154.42, 19) * mm, v(-154.91, 19.3) * mm]});
            skFitSpline(sketch, "E2606", {"points": [v(-154.91, 19.3) * mm, v(-155.4, 19.58) * mm, v(-156.02, 19.58) * mm, v(-156.51, 19.3) * mm]});
            skFitSpline(sketch, "E2607", {"points": [v(-156.51, 19.3) * mm, v(-157, 19) * mm, v(-157.31, 18.48) * mm, v(-157.31, 17.9) * mm]});
            skFitSpline(sketch, "E2608", {"points": [v(-157.31, 17.9) * mm, v(-157.31, 17.34) * mm, v(-157, 16.8) * mm, v(-156.51, 16.52) * mm]});
            skFitSpline(sketch, "E2609", {"points": [v(-156.51, 16.52) * mm, v(-156.02, 16.24) * mm, v(-155.4, 16.24) * mm, v(-154.91, 16.52) * mm]});
            skFitSpline(sketch, "E2610", {"points": [v(-154.91, 16.52) * mm, v(-154.42, 16.8) * mm, v(-154.11, 17.34) * mm, v(-154.11, 17.9) * mm]});
            skLineSegment(sketch, "E2611", {"start": v(-342.67, 14.2) * mm, "end": v(-341.1, 14.2) * mm});
            skFitSpline(sketch, "E2612", {"points": [v(-185.11, 37.9) * mm, v(-185.11, 38.48) * mm, v(-185.42, 39) * mm, v(-185.91, 39.3) * mm]});
            skFitSpline(sketch, "E2613", {"points": [v(-185.91, 39.3) * mm, v(-186.4, 39.58) * mm, v(-187.02, 39.58) * mm, v(-187.51, 39.3) * mm]});
            skFitSpline(sketch, "E2614", {"points": [v(-187.51, 39.3) * mm, v(-188, 39) * mm, v(-188.31, 38.48) * mm, v(-188.31, 37.9) * mm]});
            skFitSpline(sketch, "E2615", {"points": [v(-188.31, 37.9) * mm, v(-188.31, 37.34) * mm, v(-188, 36.8) * mm, v(-187.51, 36.52) * mm]});
            skFitSpline(sketch, "E2616", {"points": [v(-187.51, 36.52) * mm, v(-187.02, 36.24) * mm, v(-186.4, 36.24) * mm, v(-185.91, 36.52) * mm]});
            skFitSpline(sketch, "E2617", {"points": [v(-185.91, 36.52) * mm, v(-185.42, 36.8) * mm, v(-185.11, 37.34) * mm, v(-185.11, 37.9) * mm]});
            skFitSpline(sketch, "E2618", {"points": [v(-185.11, 17.9) * mm, v(-185.11, 18.48) * mm, v(-185.42, 19) * mm, v(-185.91, 19.3) * mm]});
            skFitSpline(sketch, "E2619", {"points": [v(-185.91, 19.3) * mm, v(-186.4, 19.58) * mm, v(-187.02, 19.58) * mm, v(-187.51, 19.3) * mm]});
            skFitSpline(sketch, "E2620", {"points": [v(-187.51, 19.3) * mm, v(-188, 19) * mm, v(-188.31, 18.48) * mm, v(-188.31, 17.9) * mm]});
            skFitSpline(sketch, "E2621", {"points": [v(-188.31, 17.9) * mm, v(-188.31, 17.34) * mm, v(-188, 16.8) * mm, v(-187.51, 16.52) * mm]});
            skFitSpline(sketch, "E2622", {"points": [v(-187.51, 16.52) * mm, v(-187.02, 16.24) * mm, v(-186.4, 16.24) * mm, v(-185.91, 16.52) * mm]});
            skFitSpline(sketch, "E2623", {"points": [v(-185.91, 16.52) * mm, v(-185.42, 16.8) * mm, v(-185.11, 17.34) * mm, v(-185.11, 17.9) * mm]});
            skFitSpline(sketch, "E2624", {"points": [v(-213.81, 27.52) * mm, v(-213.81, 28.1) * mm, v(-214.12, 28.62) * mm, v(-214.61, 28.9) * mm]});
            skFitSpline(sketch, "E2625", {"points": [v(-214.61, 28.9) * mm, v(-215.1, 29.2) * mm, v(-215.72, 29.2) * mm, v(-216.21, 28.9) * mm]});
            skFitSpline(sketch, "E2626", {"points": [v(-216.21, 28.9) * mm, v(-216.7, 28.62) * mm, v(-217.01, 28.1) * mm, v(-217.01, 27.52) * mm]});
            skFitSpline(sketch, "E2627", {"points": [v(-217.01, 27.52) * mm, v(-217.01, 26.95) * mm, v(-216.7, 26.42) * mm, v(-216.21, 26.13) * mm]});
            skFitSpline(sketch, "E2628", {"points": [v(-216.21, 26.13) * mm, v(-215.72, 25.85) * mm, v(-215.1, 25.85) * mm, v(-214.61, 26.13) * mm]});
            skFitSpline(sketch, "E2629", {"points": [v(-214.61, 26.13) * mm, v(-214.12, 26.42) * mm, v(-213.81, 26.95) * mm, v(-213.81, 27.52) * mm]});
            skFitSpline(sketch, "E2630", {"points": [v(-226.41, 27.52) * mm, v(-226.41, 28.1) * mm, v(-226.72, 28.62) * mm, v(-227.21, 28.9) * mm]});
            skFitSpline(sketch, "E2631", {"points": [v(-227.21, 28.9) * mm, v(-227.7, 29.2) * mm, v(-228.32, 29.2) * mm, v(-228.81, 28.9) * mm]});
            skFitSpline(sketch, "E2632", {"points": [v(-228.81, 28.9) * mm, v(-229.3, 28.62) * mm, v(-229.61, 28.1) * mm, v(-229.61, 27.52) * mm]});
            skFitSpline(sketch, "E2633", {"points": [v(-229.61, 27.52) * mm, v(-229.61, 26.64) * mm, v(-228.9, 25.92) * mm, v(-228.01, 25.92) * mm]});
            skFitSpline(sketch, "E2634", {"points": [v(-228.01, 25.92) * mm, v(-227.13, 25.92) * mm, v(-226.41, 26.64) * mm, v(-226.41, 27.52) * mm]});
            skFitSpline(sketch, "E2635", {"points": [v(-255.1, 37.9) * mm, v(-255.1, 38.48) * mm, v(-255.41, 39) * mm, v(-255.9, 39.3) * mm]});
            skFitSpline(sketch, "E2636", {"points": [v(-255.9, 39.3) * mm, v(-256.4, 39.58) * mm, v(-257.01, 39.58) * mm, v(-257.5, 39.3) * mm]});
            skFitSpline(sketch, "E2637", {"points": [v(-257.5, 39.3) * mm, v(-258, 39) * mm, v(-258.3, 38.48) * mm, v(-258.3, 37.9) * mm]});
            skFitSpline(sketch, "E2638", {"points": [v(-258.3, 37.9) * mm, v(-258.3, 37.34) * mm, v(-258, 36.8) * mm, v(-257.5, 36.52) * mm]});
            skFitSpline(sketch, "E2639", {"points": [v(-257.5, 36.52) * mm, v(-257.01, 36.24) * mm, v(-256.4, 36.24) * mm, v(-255.9, 36.52) * mm]});
            skFitSpline(sketch, "E2640", {"points": [v(-255.9, 36.52) * mm, v(-255.41, 36.8) * mm, v(-255.1, 37.34) * mm, v(-255.1, 37.9) * mm]});
            skFitSpline(sketch, "E2641", {"points": [v(-255.1, 17.9) * mm, v(-255.1, 18.48) * mm, v(-255.41, 19) * mm, v(-255.9, 19.3) * mm]});
            skFitSpline(sketch, "E2642", {"points": [v(-255.9, 19.3) * mm, v(-256.4, 19.58) * mm, v(-257.01, 19.58) * mm, v(-257.5, 19.3) * mm]});
            skFitSpline(sketch, "E2643", {"points": [v(-257.5, 19.3) * mm, v(-258, 19) * mm, v(-258.3, 18.48) * mm, v(-258.3, 17.9) * mm]});
            skFitSpline(sketch, "E2644", {"points": [v(-258.3, 17.9) * mm, v(-258.3, 17.34) * mm, v(-258, 16.8) * mm, v(-257.5, 16.52) * mm]});
            skFitSpline(sketch, "E2645", {"points": [v(-257.5, 16.52) * mm, v(-257.01, 16.24) * mm, v(-256.4, 16.24) * mm, v(-255.9, 16.52) * mm]});
            skFitSpline(sketch, "E2646", {"points": [v(-255.9, 16.52) * mm, v(-255.41, 16.8) * mm, v(-255.1, 17.34) * mm, v(-255.1, 17.9) * mm]});
            skFitSpline(sketch, "E2647", {"points": [v(-286.1, 37.9) * mm, v(-286.1, 38.48) * mm, v(-286.41, 39) * mm, v(-286.9, 39.3) * mm]});
            skFitSpline(sketch, "E2648", {"points": [v(-286.9, 39.3) * mm, v(-287.4, 39.58) * mm, v(-288.01, 39.58) * mm, v(-288.5, 39.3) * mm]});
            skFitSpline(sketch, "E2649", {"points": [v(-288.5, 39.3) * mm, v(-289, 39) * mm, v(-289.3, 38.48) * mm, v(-289.3, 37.9) * mm]});
            skFitSpline(sketch, "E2650", {"points": [v(-289.3, 37.9) * mm, v(-289.3, 37.34) * mm, v(-289, 36.8) * mm, v(-288.5, 36.52) * mm]});
            skFitSpline(sketch, "E2651", {"points": [v(-288.5, 36.52) * mm, v(-288.01, 36.24) * mm, v(-287.4, 36.24) * mm, v(-286.9, 36.52) * mm]});
            skFitSpline(sketch, "E2652", {"points": [v(-286.9, 36.52) * mm, v(-286.41, 36.8) * mm, v(-286.1, 37.34) * mm, v(-286.1, 37.9) * mm]});
            skFitSpline(sketch, "E2653", {"points": [v(-286.1, 17.9) * mm, v(-286.1, 18.48) * mm, v(-286.41, 19) * mm, v(-286.9, 19.3) * mm]});
            skFitSpline(sketch, "E2654", {"points": [v(-286.9, 19.3) * mm, v(-287.4, 19.58) * mm, v(-288.01, 19.58) * mm, v(-288.5, 19.3) * mm]});
            skFitSpline(sketch, "E2655", {"points": [v(-288.5, 19.3) * mm, v(-289, 19) * mm, v(-289.3, 18.48) * mm, v(-289.3, 17.9) * mm]});
            skFitSpline(sketch, "E2656", {"points": [v(-289.3, 17.9) * mm, v(-289.3, 17.34) * mm, v(-289, 16.8) * mm, v(-288.5, 16.52) * mm]});
            skFitSpline(sketch, "E2657", {"points": [v(-288.5, 16.52) * mm, v(-288.01, 16.24) * mm, v(-287.4, 16.24) * mm, v(-286.9, 16.52) * mm]});
            skFitSpline(sketch, "E2658", {"points": [v(-286.9, 16.52) * mm, v(-286.41, 16.8) * mm, v(-286.1, 17.34) * mm, v(-286.1, 17.9) * mm]});
            skFitSpline(sketch, "E2659", {"points": [v(-340.28, 27.9) * mm, v(-340.28, 28.48) * mm, v(-340.59, 29) * mm, v(-341.08, 29.3) * mm]});
            skFitSpline(sketch, "E2660", {"points": [v(-341.08, 29.3) * mm, v(-341.58, 29.58) * mm, v(-342.19, 29.58) * mm, v(-342.68, 29.3) * mm]});
            skFitSpline(sketch, "E2661", {"points": [v(-342.68, 29.3) * mm, v(-343.18, 29) * mm, v(-343.48, 28.48) * mm, v(-343.48, 27.9) * mm]});
            skFitSpline(sketch, "E2662", {"points": [v(-343.48, 27.9) * mm, v(-343.48, 27.34) * mm, v(-343.18, 26.8) * mm, v(-342.68, 26.52) * mm]});
            skFitSpline(sketch, "E2663", {"points": [v(-342.68, 26.52) * mm, v(-342.19, 26.24) * mm, v(-341.58, 26.24) * mm, v(-341.08, 26.52) * mm]});
            skFitSpline(sketch, "E2664", {"points": [v(-341.08, 26.52) * mm, v(-340.59, 26.8) * mm, v(-340.28, 27.34) * mm, v(-340.28, 27.9) * mm]});
            skFitSpline(sketch, "E2665", {"points": [v(-325.1, 47.22) * mm, v(-324.97, 46.8) * mm, v(-324.59, 46.52) * mm, v(-324.15, 46.52) * mm]});
            skFitSpline(sketch, "E2666", {"points": [v(-326.66, 52.2) * mm, v(-326.8, 52.62) * mm, v(-327.18, 52.9) * mm, v(-327.62, 52.9) * mm]});
            skFitSpline(sketch, "E2667", {"points": [v(-119.27, 46.52) * mm, v(-118.83, 46.52) * mm, v(-118.45, 46.8) * mm, v(-118.32, 47.22) * mm]});
            skFitSpline(sketch, "E2668", {"points": [v(-115.8, 52.9) * mm, v(-116.24, 52.9) * mm, v(-116.63, 52.62) * mm, v(-116.76, 52.2) * mm]});
            skFitSpline(sketch, "E2669", {"points": [v(-140.4, 0.52) * mm, v(-140.2, 0.52) * mm, v(-140.04, 0.62) * mm, v(-139.95, 0.79) * mm]});
            skFitSpline(sketch, "E2670", {"points": [v(-139.95, 0.79) * mm, v(-139.86, 0.95) * mm, v(-139.87, 1.15) * mm, v(-139.98, 1.3) * mm]});
            skFitSpline(sketch, "E2671", {"points": [v(-133.44, 1.3) * mm, v(-133.54, 1.15) * mm, v(-133.55, 0.95) * mm, v(-133.47, 0.79) * mm]});
            skFitSpline(sketch, "E2672", {"points": [v(-133.47, 0.79) * mm, v(-133.38, 0.62) * mm, v(-133.2, 0.52) * mm, v(-133.02, 0.52) * mm]});
            skFitSpline(sketch, "E2673", {"points": [v(-316.71, 2.52) * mm, v(-316.71, 1.42) * mm, v(-315.82, 0.52) * mm, v(-314.71, 0.52) * mm]});
            skFitSpline(sketch, "E2674", {"points": [v(-298.71, 0.52) * mm, v(-297.6, 0.52) * mm, v(-296.71, 1.42) * mm, v(-296.71, 2.52) * mm]});
            skFitSpline(sketch, "E2675", {"points": [v(-310.4, 0.52) * mm, v(-310.21, 0.52) * mm, v(-310.04, 0.62) * mm, v(-309.95, 0.79) * mm]});
            skFitSpline(sketch, "E2676", {"points": [v(-309.95, 0.79) * mm, v(-309.87, 0.95) * mm, v(-309.88, 1.15) * mm, v(-309.98, 1.3) * mm]});
            skFitSpline(sketch, "E2677", {"points": [v(-303.44, 1.3) * mm, v(-303.55, 1.15) * mm, v(-303.56, 0.95) * mm, v(-303.47, 0.79) * mm]});
            skFitSpline(sketch, "E2678", {"points": [v(-303.47, 0.79) * mm, v(-303.38, 0.62) * mm, v(-303.21, 0.52) * mm, v(-303.03, 0.52) * mm]});
            skFitSpline(sketch, "E2679", {"points": [v(-303.44, 1.3) * mm, v(-302.33, 2.95) * mm, v(-302.6, 5.17) * mm, v(-304.1, 6.48) * mm]});
            skFitSpline(sketch, "E2680", {"points": [v(-304.1, 6.48) * mm, v(-305.6, 7.8) * mm, v(-307.83, 7.8) * mm, v(-309.32, 6.48) * mm]});
            skFitSpline(sketch, "E2681", {"points": [v(-309.32, 6.48) * mm, v(-310.82, 5.17) * mm, v(-311.1, 2.95) * mm, v(-309.98, 1.3) * mm]});
            skLineSegment(sketch, "E2682", {"start": v(-314.71, 0.52) * mm, "end": v(-310.4, 0.52) * mm});
            skLineSegment(sketch, "E2683", {"start": v(-303.03, 0.52) * mm, "end": v(-298.71, 0.52) * mm});
            skFitSpline(sketch, "E2684", {"points": [v(-30.13, 4.74) * mm, v(-28.8, 4.74) * mm, v(-27.53, 5.27) * mm, v(-26.6, 6.2) * mm]});
            skFitSpline(sketch, "E2685", {"points": [v(-26.6, 6.2) * mm, v(-25.66, 7.15) * mm, v(-25.13, 8.42) * mm, v(-25.13, 9.74) * mm]});
            skLineSegment(sketch, "E2686", {"start": v(-296.71, 2.52) * mm, "end": v(-296.71, 8.02) * mm});
            skFitSpline(sketch, "E2687", {"points": [v(-85.13, 9.74) * mm, v(-85.13, 6.98) * mm, v(-82.9, 4.74) * mm, v(-80.13, 4.74) * mm]});
            skLineSegment(sketch, "E2688", {"start": v(-316.71, 8.02) * mm, "end": v(-316.71, 2.52) * mm});
            skFitSpline(sketch, "E2689", {"points": [v(-69.16, 54.5) * mm, v(-69.25, 54.65) * mm, v(-69.42, 54.74) * mm, v(-69.6, 54.74) * mm]});
            skFitSpline(sketch, "E2690", {"points": [v(-69.16, 54.5) * mm, v(-69.06, 54.31) * mm, v(-68.85, 54.22) * mm, v(-68.64, 54.25) * mm]});
            skFitSpline(sketch, "E2691", {"points": [v(-68.64, 54.25) * mm, v(-68.44, 54.29) * mm, v(-68.27, 54.45) * mm, v(-68.24, 54.66) * mm]});
            skFitSpline(sketch, "E2692", {"points": [v(-68.24, 54.66) * mm, v(-68.2, 54.86) * mm, v(-68.3, 55.07) * mm, v(-68.48, 55.18) * mm]});
            skFitSpline(sketch, "E2693", {"points": [v(-68.73, 55.6) * mm, v(-68.73, 55.43) * mm, v(-68.63, 55.27) * mm, v(-68.48, 55.18) * mm]});
            skLineSegment(sketch, "E2694", {"start": v(-25.13, 54.74) * mm, "end": v(-25.13, 9.74) * mm});
            skFitSpline(sketch, "E2695", {"points": [v(-68.23, 57.74) * mm, v(-68.36, 57.74) * mm, v(-68.49, 57.7) * mm, v(-68.58, 57.6) * mm]});
            skFitSpline(sketch, "E2696", {"points": [v(-68.58, 57.6) * mm, v(-68.68, 57.5) * mm, v(-68.73, 57.38) * mm, v(-68.73, 57.24) * mm]});
            skLineSegment(sketch, "E2697", {"start": v(-30.13, 4.74) * mm, "end": v(-80.13, 4.74) * mm});
            skFitSpline(sketch, "E2698", {"points": [v(-62.73, 57.24) * mm, v(-62.73, 57.52) * mm, v(-62.95, 57.74) * mm, v(-63.23, 57.74) * mm]});
            skLineSegment(sketch, "E2699", {"start": v(-85.13, 9.74) * mm, "end": v(-85.13, 54.74) * mm});
            skLineSegment(sketch, "E2700", {"start": v(-85.13, 54.74) * mm, "end": v(-69.6, 54.74) * mm});
            skFitSpline(sketch, "E2701", {"points": [v(-62.98, 55.18) * mm, v(-62.82, 55.27) * mm, v(-62.73, 55.43) * mm, v(-62.73, 55.6) * mm]});
            skFitSpline(sketch, "E2702", {"points": [v(-62.98, 55.18) * mm, v(-63.16, 55.07) * mm, v(-63.26, 54.86) * mm, v(-63.22, 54.66) * mm]});
            skFitSpline(sketch, "E2703", {"points": [v(-63.22, 54.66) * mm, v(-63.19, 54.45) * mm, v(-63.02, 54.29) * mm, v(-62.82, 54.25) * mm]});
            skFitSpline(sketch, "E2704", {"points": [v(-62.82, 54.25) * mm, v(-62.6, 54.22) * mm, v(-62.4, 54.31) * mm, v(-62.3, 54.5) * mm]});
            skFitSpline(sketch, "E2705", {"points": [v(-61.86, 54.74) * mm, v(-62.04, 54.74) * mm, v(-62.2, 54.65) * mm, v(-62.3, 54.5) * mm]});
            skLineSegment(sketch, "E2706", {"start": v(-68.73, 55.6) * mm, "end": v(-68.73, 57.24) * mm});
            skFitSpline(sketch, "E2707", {"points": [v(-47.96, 54.5) * mm, v(-48.05, 54.65) * mm, v(-48.22, 54.74) * mm, v(-48.4, 54.74) * mm]});
            skFitSpline(sketch, "E2708", {"points": [v(-47.96, 54.5) * mm, v(-47.86, 54.31) * mm, v(-47.65, 54.22) * mm, v(-47.44, 54.25) * mm]});
            skFitSpline(sketch, "E2709", {"points": [v(-47.44, 54.25) * mm, v(-47.24, 54.29) * mm, v(-47.07, 54.45) * mm, v(-47.04, 54.66) * mm]});
            skFitSpline(sketch, "E2710", {"points": [v(-47.04, 54.66) * mm, v(-47, 54.86) * mm, v(-47.1, 55.07) * mm, v(-47.28, 55.18) * mm]});
            skFitSpline(sketch, "E2711", {"points": [v(-47.53, 55.6) * mm, v(-47.53, 55.43) * mm, v(-47.43, 55.27) * mm, v(-47.28, 55.18) * mm]});
            skLineSegment(sketch, "E2712", {"start": v(-68.23, 57.74) * mm, "end": v(-63.23, 57.74) * mm});
            skFitSpline(sketch, "E2713", {"points": [v(-47.03, 57.74) * mm, v(-47.16, 57.74) * mm, v(-47.29, 57.7) * mm, v(-47.38, 57.6) * mm]});
            skFitSpline(sketch, "E2714", {"points": [v(-47.38, 57.6) * mm, v(-47.48, 57.5) * mm, v(-47.53, 57.38) * mm, v(-47.53, 57.24) * mm]});
            skLineSegment(sketch, "E2715", {"start": v(-62.73, 57.24) * mm, "end": v(-62.73, 55.6) * mm});
            skFitSpline(sketch, "E2716", {"points": [v(-41.53, 57.24) * mm, v(-41.53, 57.38) * mm, v(-41.58, 57.5) * mm, v(-41.68, 57.6) * mm]});
            skFitSpline(sketch, "E2717", {"points": [v(-41.68, 57.6) * mm, v(-41.77, 57.7) * mm, v(-41.9, 57.74) * mm, v(-42.03, 57.74) * mm]});
            skLineSegment(sketch, "E2718", {"start": v(-61.86, 54.74) * mm, "end": v(-56.73, 54.74) * mm});
            skLineSegment(sketch, "E2719", {"start": v(-56.73, 54.74) * mm, "end": v(-56.73, 51.74) * mm});
            skLineSegment(sketch, "E2720", {"start": v(-56.73, 51.74) * mm, "end": v(-58, 51.74) * mm});
            skLineSegment(sketch, "E2721", {"start": v(-58, 51.74) * mm, "end": v(-58, 47.74) * mm});
            skLineSegment(sketch, "E2722", {"start": v(-58, 47.74) * mm, "end": v(-56.73, 47.74) * mm});
            skLineSegment(sketch, "E2723", {"start": v(-56.73, 47.74) * mm, "end": v(-56.73, 44.74) * mm});
            skLineSegment(sketch, "E2724", {"start": v(-56.73, 44.74) * mm, "end": v(-53.53, 44.74) * mm});
            skLineSegment(sketch, "E2725", {"start": v(-53.53, 44.74) * mm, "end": v(-53.53, 47.74) * mm});
            skLineSegment(sketch, "E2726", {"start": v(-53.53, 47.74) * mm, "end": v(-52.25, 47.74) * mm});
            skLineSegment(sketch, "E2727", {"start": v(-52.25, 47.74) * mm, "end": v(-52.25, 51.74) * mm});
            skLineSegment(sketch, "E2728", {"start": v(-52.25, 51.74) * mm, "end": v(-53.53, 51.74) * mm});
            skLineSegment(sketch, "E2729", {"start": v(-53.53, 51.74) * mm, "end": v(-53.53, 54.74) * mm});
            skLineSegment(sketch, "E2730", {"start": v(-53.53, 54.74) * mm, "end": v(-48.4, 54.74) * mm});
            skFitSpline(sketch, "E2731", {"points": [v(-41.78, 55.18) * mm, v(-41.63, 55.27) * mm, v(-41.53, 55.43) * mm, v(-41.53, 55.6) * mm]});
            skFitSpline(sketch, "E2732", {"points": [v(-41.78, 55.18) * mm, v(-41.96, 55.07) * mm, v(-42.06, 54.86) * mm, v(-42.02, 54.66) * mm]});
            skFitSpline(sketch, "E2733", {"points": [v(-42.02, 54.66) * mm, v(-41.99, 54.45) * mm, v(-41.82, 54.29) * mm, v(-41.62, 54.25) * mm]});
            skFitSpline(sketch, "E2734", {"points": [v(-41.62, 54.25) * mm, v(-41.4, 54.22) * mm, v(-41.2, 54.31) * mm, v(-41.1, 54.5) * mm]});
            skFitSpline(sketch, "E2735", {"points": [v(-40.66, 54.74) * mm, v(-40.84, 54.74) * mm, v(-41, 54.65) * mm, v(-41.1, 54.5) * mm]});
            skLineSegment(sketch, "E2736", {"start": v(-47.53, 55.6) * mm, "end": v(-47.53, 57.24) * mm});
            skFitSpline(sketch, "E2737", {"points": [v(-44.03, 25.44) * mm, v(-44.03, 29.41) * mm, v(-46.14, 33.08) * mm, v(-49.58, 35.06) * mm]});
            skFitSpline(sketch, "E2738", {"points": [v(-49.58, 35.06) * mm, v(-53.01, 37.05) * mm, v(-57.25, 37.05) * mm, v(-60.68, 35.06) * mm]});
            skFitSpline(sketch, "E2739", {"points": [v(-60.68, 35.06) * mm, v(-64.12, 33.08) * mm, v(-66.23, 29.41) * mm, v(-66.23, 25.44) * mm]});
            skFitSpline(sketch, "E2740", {"points": [v(-66.23, 25.44) * mm, v(-66.23, 21.48) * mm, v(-64.12, 17.8) * mm, v(-60.68, 15.83) * mm]});
            skFitSpline(sketch, "E2741", {"points": [v(-60.68, 15.83) * mm, v(-57.25, 13.84) * mm, v(-53.01, 13.84) * mm, v(-49.58, 15.83) * mm]});
            skFitSpline(sketch, "E2742", {"points": [v(-49.58, 15.83) * mm, v(-46.14, 17.8) * mm, v(-44.03, 21.48) * mm, v(-44.03, 25.44) * mm]});
            skLineSegment(sketch, "E2743", {"start": v(-47.03, 57.74) * mm, "end": v(-42.03, 57.74) * mm});
            skFitSpline(sketch, "E2744", {"points": [v(-34.13, 25.44) * mm, v(-34.13, 26.88) * mm, v(-34.89, 28.2) * mm, v(-36.13, 28.91) * mm]});
            skFitSpline(sketch, "E2745", {"points": [v(-36.13, 28.91) * mm, v(-37.37, 29.63) * mm, v(-38.9, 29.63) * mm, v(-40.13, 28.91) * mm]});
            skFitSpline(sketch, "E2746", {"points": [v(-40.13, 28.91) * mm, v(-41.37, 28.2) * mm, v(-42.13, 26.88) * mm, v(-42.13, 25.44) * mm]});
            skFitSpline(sketch, "E2747", {"points": [v(-42.13, 25.44) * mm, v(-42.13, 24.01) * mm, v(-41.37, 22.69) * mm, v(-40.13, 21.97) * mm]});
            skFitSpline(sketch, "E2748", {"points": [v(-40.13, 21.97) * mm, v(-38.9, 21.26) * mm, v(-37.37, 21.26) * mm, v(-36.13, 21.97) * mm]});
            skFitSpline(sketch, "E2749", {"points": [v(-36.13, 21.97) * mm, v(-34.89, 22.69) * mm, v(-34.13, 24.01) * mm, v(-34.13, 25.44) * mm]});
            skLineSegment(sketch, "E2750", {"start": v(-41.53, 57.24) * mm, "end": v(-41.53, 55.6) * mm});
            skFitSpline(sketch, "E2751", {"points": [v(-31.4, 37.24) * mm, v(-31.57, 37.24) * mm, v(-31.74, 37.15) * mm, v(-31.83, 37) * mm]});
            skFitSpline(sketch, "E2752", {"points": [v(-32.5, 37.68) * mm, v(-32.7, 37.57) * mm, v(-32.79, 37.36) * mm, v(-32.75, 37.16) * mm]});
            skFitSpline(sketch, "E2753", {"points": [v(-32.75, 37.16) * mm, v(-32.72, 36.95) * mm, v(-32.55, 36.79) * mm, v(-32.35, 36.75) * mm]});
            skFitSpline(sketch, "E2754", {"points": [v(-32.35, 36.75) * mm, v(-32.14, 36.72) * mm, v(-31.93, 36.81) * mm, v(-31.83, 37) * mm]});
            skFitSpline(sketch, "E2755", {"points": [v(-32.5, 37.68) * mm, v(-32.36, 37.77) * mm, v(-32.26, 37.93) * mm, v(-32.26, 38.11) * mm]});
            skLineSegment(sketch, "E2756", {"start": v(-40.66, 54.74) * mm, "end": v(-25.13, 54.74) * mm});
            skFitSpline(sketch, "E2757", {"points": [v(-32.26, 42.58) * mm, v(-32.26, 42.76) * mm, v(-32.36, 42.92) * mm, v(-32.5, 43.01) * mm]});
            skFitSpline(sketch, "E2758", {"points": [v(-31.83, 43.7) * mm, v(-31.93, 43.88) * mm, v(-32.14, 43.97) * mm, v(-32.35, 43.94) * mm]});
            skFitSpline(sketch, "E2759", {"points": [v(-32.35, 43.94) * mm, v(-32.55, 43.9) * mm, v(-32.72, 43.74) * mm, v(-32.75, 43.53) * mm]});
            skFitSpline(sketch, "E2760", {"points": [v(-32.75, 43.53) * mm, v(-32.79, 43.32) * mm, v(-32.7, 43.12) * mm, v(-32.5, 43.01) * mm]});
            skFitSpline(sketch, "E2761", {"points": [v(-31.83, 43.7) * mm, v(-31.74, 43.54) * mm, v(-31.57, 43.44) * mm, v(-31.4, 43.44) * mm]});
            skFitSpline(sketch, "E2762", {"points": [v(-29.83, 43.44) * mm, v(-29.65, 43.44) * mm, v(-29.48, 43.54) * mm, v(-29.4, 43.7) * mm]});
            skFitSpline(sketch, "E2763", {"points": [v(-28.7, 43.01) * mm, v(-28.53, 43.12) * mm, v(-28.43, 43.32) * mm, v(-28.47, 43.53) * mm]});
            skFitSpline(sketch, "E2764", {"points": [v(-28.47, 43.53) * mm, v(-28.5, 43.74) * mm, v(-28.67, 43.9) * mm, v(-28.87, 43.94) * mm]});
            skFitSpline(sketch, "E2765", {"points": [v(-28.87, 43.94) * mm, v(-29.08, 43.97) * mm, v(-29.29, 43.88) * mm, v(-29.4, 43.7) * mm]});
            skFitSpline(sketch, "E2766", {"points": [v(-28.7, 43.01) * mm, v(-28.86, 42.92) * mm, v(-28.96, 42.76) * mm, v(-28.96, 42.58) * mm]});
            skFitSpline(sketch, "E2767", {"points": [v(-28.96, 38.11) * mm, v(-28.96, 37.93) * mm, v(-28.86, 37.77) * mm, v(-28.7, 37.68) * mm]});
            skFitSpline(sketch, "E2768", {"points": [v(-29.4, 37) * mm, v(-29.29, 36.81) * mm, v(-29.08, 36.72) * mm, v(-28.87, 36.75) * mm]});
            skFitSpline(sketch, "E2769", {"points": [v(-28.87, 36.75) * mm, v(-28.67, 36.79) * mm, v(-28.5, 36.95) * mm, v(-28.47, 37.16) * mm]});
            skFitSpline(sketch, "E2770", {"points": [v(-28.47, 37.16) * mm, v(-28.43, 37.36) * mm, v(-28.53, 37.57) * mm, v(-28.7, 37.68) * mm]});
            skFitSpline(sketch, "E2771", {"points": [v(-29.4, 37) * mm, v(-29.48, 37.15) * mm, v(-29.65, 37.24) * mm, v(-29.83, 37.24) * mm]});
            skLineSegment(sketch, "E2772", {"start": v(-32.26, 38.11) * mm, "end": v(-32.26, 42.58) * mm});
            skFitSpline(sketch, "E2773", {"points": [v(-31.4, 16.04) * mm, v(-31.57, 16.04) * mm, v(-31.74, 15.95) * mm, v(-31.83, 15.8) * mm]});
            skFitSpline(sketch, "E2774", {"points": [v(-32.5, 16.48) * mm, v(-32.7, 16.37) * mm, v(-32.79, 16.16) * mm, v(-32.75, 15.96) * mm]});
            skFitSpline(sketch, "E2775", {"points": [v(-32.75, 15.96) * mm, v(-32.72, 15.75) * mm, v(-32.55, 15.59) * mm, v(-32.35, 15.55) * mm]});
            skFitSpline(sketch, "E2776", {"points": [v(-32.35, 15.55) * mm, v(-32.14, 15.52) * mm, v(-31.93, 15.61) * mm, v(-31.83, 15.8) * mm]});
            skFitSpline(sketch, "E2777", {"points": [v(-32.5, 16.48) * mm, v(-32.36, 16.57) * mm, v(-32.26, 16.73) * mm, v(-32.26, 16.91) * mm]});
            skLineSegment(sketch, "E2778", {"start": v(-31.4, 43.44) * mm, "end": v(-29.83, 43.44) * mm});
            skFitSpline(sketch, "E2779", {"points": [v(-32.26, 21.38) * mm, v(-32.26, 21.56) * mm, v(-32.36, 21.72) * mm, v(-32.5, 21.81) * mm]});
            skFitSpline(sketch, "E2780", {"points": [v(-31.83, 22.5) * mm, v(-31.93, 22.68) * mm, v(-32.14, 22.77) * mm, v(-32.35, 22.74) * mm]});
            skFitSpline(sketch, "E2781", {"points": [v(-32.35, 22.74) * mm, v(-32.55, 22.7) * mm, v(-32.72, 22.54) * mm, v(-32.75, 22.33) * mm]});
            skFitSpline(sketch, "E2782", {"points": [v(-32.75, 22.33) * mm, v(-32.79, 22.12) * mm, v(-32.7, 21.92) * mm, v(-32.5, 21.81) * mm]});
            skFitSpline(sketch, "E2783", {"points": [v(-31.83, 22.5) * mm, v(-31.74, 22.34) * mm, v(-31.57, 22.24) * mm, v(-31.4, 22.24) * mm]});
            skLineSegment(sketch, "E2784", {"start": v(-28.96, 42.58) * mm, "end": v(-28.96, 38.11) * mm});
            skFitSpline(sketch, "E2785", {"points": [v(-29.83, 22.24) * mm, v(-29.65, 22.24) * mm, v(-29.48, 22.34) * mm, v(-29.4, 22.5) * mm]});
            skFitSpline(sketch, "E2786", {"points": [v(-28.7, 21.81) * mm, v(-28.53, 21.92) * mm, v(-28.43, 22.12) * mm, v(-28.47, 22.33) * mm]});
            skFitSpline(sketch, "E2787", {"points": [v(-28.47, 22.33) * mm, v(-28.5, 22.54) * mm, v(-28.67, 22.7) * mm, v(-28.87, 22.74) * mm]});
            skFitSpline(sketch, "E2788", {"points": [v(-28.87, 22.74) * mm, v(-29.08, 22.77) * mm, v(-29.29, 22.68) * mm, v(-29.4, 22.5) * mm]});
            skFitSpline(sketch, "E2789", {"points": [v(-28.7, 21.81) * mm, v(-28.86, 21.72) * mm, v(-28.96, 21.56) * mm, v(-28.96, 21.38) * mm]});
            skLineSegment(sketch, "E2790", {"start": v(-29.83, 37.24) * mm, "end": v(-31.4, 37.24) * mm});
            skFitSpline(sketch, "E2791", {"points": [v(-28.96, 16.91) * mm, v(-28.96, 16.73) * mm, v(-28.86, 16.57) * mm, v(-28.7, 16.48) * mm]});
            skFitSpline(sketch, "E2792", {"points": [v(-29.4, 15.8) * mm, v(-29.29, 15.61) * mm, v(-29.08, 15.52) * mm, v(-28.87, 15.55) * mm]});
            skFitSpline(sketch, "E2793", {"points": [v(-28.87, 15.55) * mm, v(-28.67, 15.59) * mm, v(-28.5, 15.75) * mm, v(-28.47, 15.96) * mm]});
            skFitSpline(sketch, "E2794", {"points": [v(-28.47, 15.96) * mm, v(-28.43, 16.16) * mm, v(-28.53, 16.37) * mm, v(-28.7, 16.48) * mm]});
            skFitSpline(sketch, "E2795", {"points": [v(-29.4, 15.8) * mm, v(-29.48, 15.95) * mm, v(-29.65, 16.04) * mm, v(-29.83, 16.04) * mm]});
            skLineSegment(sketch, "E2796", {"start": v(-32.26, 16.91) * mm, "end": v(-32.26, 21.38) * mm});
            skFitSpline(sketch, "E2797", {"points": [v(-80.43, 37.24) * mm, v(-80.61, 37.24) * mm, v(-80.78, 37.15) * mm, v(-80.87, 37) * mm]});
            skFitSpline(sketch, "E2798", {"points": [v(-81.55, 37.68) * mm, v(-81.73, 37.57) * mm, v(-81.83, 37.36) * mm, v(-81.8, 37.16) * mm]});
            skFitSpline(sketch, "E2799", {"points": [v(-81.8, 37.16) * mm, v(-81.76, 36.95) * mm, v(-81.6, 36.79) * mm, v(-81.39, 36.75) * mm]});
            skFitSpline(sketch, "E2800", {"points": [v(-81.39, 36.75) * mm, v(-81.18, 36.72) * mm, v(-80.97, 36.81) * mm, v(-80.87, 37) * mm]});
            skFitSpline(sketch, "E2801", {"points": [v(-81.55, 37.68) * mm, v(-81.4, 37.77) * mm, v(-81.3, 37.93) * mm, v(-81.3, 38.11) * mm]});
            skLineSegment(sketch, "E2802", {"start": v(-31.4, 22.24) * mm, "end": v(-29.83, 22.24) * mm});
            skFitSpline(sketch, "E2803", {"points": [v(-81.3, 42.58) * mm, v(-81.3, 42.76) * mm, v(-81.4, 42.92) * mm, v(-81.55, 43.01) * mm]});
            skFitSpline(sketch, "E2804", {"points": [v(-80.87, 43.7) * mm, v(-80.97, 43.88) * mm, v(-81.18, 43.97) * mm, v(-81.39, 43.94) * mm]});
            skFitSpline(sketch, "E2805", {"points": [v(-81.39, 43.94) * mm, v(-81.6, 43.9) * mm, v(-81.76, 43.74) * mm, v(-81.8, 43.53) * mm]});
            skFitSpline(sketch, "E2806", {"points": [v(-81.8, 43.53) * mm, v(-81.83, 43.32) * mm, v(-81.73, 43.12) * mm, v(-81.55, 43.01) * mm]});
            skFitSpline(sketch, "E2807", {"points": [v(-80.87, 43.7) * mm, v(-80.78, 43.54) * mm, v(-80.61, 43.44) * mm, v(-80.43, 43.44) * mm]});
            skLineSegment(sketch, "E2808", {"start": v(-28.96, 21.38) * mm, "end": v(-28.96, 16.91) * mm});
            skFitSpline(sketch, "E2809", {"points": [v(-78.87, 43.44) * mm, v(-78.69, 43.44) * mm, v(-78.52, 43.54) * mm, v(-78.43, 43.7) * mm]});
            skFitSpline(sketch, "E2810", {"points": [v(-77.75, 43.01) * mm, v(-77.57, 43.12) * mm, v(-77.47, 43.32) * mm, v(-77.5, 43.53) * mm]});
            skFitSpline(sketch, "E2811", {"points": [v(-77.5, 43.53) * mm, v(-77.54, 43.74) * mm, v(-77.7, 43.9) * mm, v(-77.91, 43.94) * mm]});
            skFitSpline(sketch, "E2812", {"points": [v(-77.91, 43.94) * mm, v(-78.12, 43.97) * mm, v(-78.33, 43.88) * mm, v(-78.43, 43.7) * mm]});
            skFitSpline(sketch, "E2813", {"points": [v(-77.75, 43.01) * mm, v(-77.9, 42.92) * mm, v(-78, 42.76) * mm, v(-78, 42.58) * mm]});
            skLineSegment(sketch, "E2814", {"start": v(-29.83, 16.04) * mm, "end": v(-31.4, 16.04) * mm});
            skFitSpline(sketch, "E2815", {"points": [v(-78, 38.11) * mm, v(-78, 37.93) * mm, v(-77.9, 37.77) * mm, v(-77.75, 37.68) * mm]});
            skFitSpline(sketch, "E2816", {"points": [v(-78.43, 37) * mm, v(-78.33, 36.81) * mm, v(-78.12, 36.72) * mm, v(-77.91, 36.75) * mm]});
            skFitSpline(sketch, "E2817", {"points": [v(-77.91, 36.75) * mm, v(-77.7, 36.79) * mm, v(-77.54, 36.95) * mm, v(-77.5, 37.16) * mm]});
            skFitSpline(sketch, "E2818", {"points": [v(-77.5, 37.16) * mm, v(-77.47, 37.36) * mm, v(-77.57, 37.57) * mm, v(-77.75, 37.68) * mm]});
            skFitSpline(sketch, "E2819", {"points": [v(-78.43, 37) * mm, v(-78.52, 37.15) * mm, v(-78.69, 37.24) * mm, v(-78.87, 37.24) * mm]});
            skLineSegment(sketch, "E2820", {"start": v(-81.3, 38.11) * mm, "end": v(-81.3, 42.58) * mm});
            skFitSpline(sketch, "E2821", {"points": [v(-80.43, 16.04) * mm, v(-80.61, 16.04) * mm, v(-80.78, 15.95) * mm, v(-80.87, 15.8) * mm]});
            skFitSpline(sketch, "E2822", {"points": [v(-81.55, 16.48) * mm, v(-81.73, 16.37) * mm, v(-81.83, 16.16) * mm, v(-81.8, 15.96) * mm]});
            skFitSpline(sketch, "E2823", {"points": [v(-81.8, 15.96) * mm, v(-81.76, 15.75) * mm, v(-81.6, 15.59) * mm, v(-81.39, 15.55) * mm]});
            skFitSpline(sketch, "E2824", {"points": [v(-81.39, 15.55) * mm, v(-81.18, 15.52) * mm, v(-80.97, 15.61) * mm, v(-80.87, 15.8) * mm]});
            skFitSpline(sketch, "E2825", {"points": [v(-81.55, 16.48) * mm, v(-81.4, 16.57) * mm, v(-81.3, 16.73) * mm, v(-81.3, 16.91) * mm]});
            skLineSegment(sketch, "E2826", {"start": v(-80.43, 43.44) * mm, "end": v(-78.87, 43.44) * mm});
            skFitSpline(sketch, "E2827", {"points": [v(-81.3, 21.38) * mm, v(-81.3, 21.56) * mm, v(-81.4, 21.72) * mm, v(-81.55, 21.81) * mm]});
            skFitSpline(sketch, "E2828", {"points": [v(-80.87, 22.5) * mm, v(-80.97, 22.68) * mm, v(-81.18, 22.77) * mm, v(-81.39, 22.74) * mm]});
            skFitSpline(sketch, "E2829", {"points": [v(-81.39, 22.74) * mm, v(-81.6, 22.7) * mm, v(-81.76, 22.54) * mm, v(-81.8, 22.33) * mm]});
            skFitSpline(sketch, "E2830", {"points": [v(-81.8, 22.33) * mm, v(-81.83, 22.12) * mm, v(-81.73, 21.92) * mm, v(-81.55, 21.81) * mm]});
            skFitSpline(sketch, "E2831", {"points": [v(-80.87, 22.5) * mm, v(-80.78, 22.34) * mm, v(-80.61, 22.24) * mm, v(-80.43, 22.24) * mm]});
            skLineSegment(sketch, "E2832", {"start": v(-78, 42.58) * mm, "end": v(-78, 38.11) * mm});
            skFitSpline(sketch, "E2833", {"points": [v(-78.87, 22.24) * mm, v(-78.69, 22.24) * mm, v(-78.52, 22.34) * mm, v(-78.43, 22.5) * mm]});
            skFitSpline(sketch, "E2834", {"points": [v(-77.75, 21.81) * mm, v(-77.57, 21.92) * mm, v(-77.47, 22.12) * mm, v(-77.5, 22.33) * mm]});
            skFitSpline(sketch, "E2835", {"points": [v(-77.5, 22.33) * mm, v(-77.54, 22.54) * mm, v(-77.7, 22.7) * mm, v(-77.91, 22.74) * mm]});
            skFitSpline(sketch, "E2836", {"points": [v(-77.91, 22.74) * mm, v(-78.12, 22.77) * mm, v(-78.33, 22.68) * mm, v(-78.43, 22.5) * mm]});
            skFitSpline(sketch, "E2837", {"points": [v(-77.75, 21.81) * mm, v(-77.9, 21.72) * mm, v(-78, 21.56) * mm, v(-78, 21.38) * mm]});
            skLineSegment(sketch, "E2838", {"start": v(-78.87, 37.24) * mm, "end": v(-80.43, 37.24) * mm});
            skFitSpline(sketch, "E2839", {"points": [v(-78, 16.91) * mm, v(-78, 16.73) * mm, v(-77.9, 16.57) * mm, v(-77.75, 16.48) * mm]});
            skFitSpline(sketch, "E2840", {"points": [v(-78.43, 15.8) * mm, v(-78.33, 15.61) * mm, v(-78.12, 15.52) * mm, v(-77.91, 15.55) * mm]});
            skFitSpline(sketch, "E2841", {"points": [v(-77.91, 15.55) * mm, v(-77.7, 15.59) * mm, v(-77.54, 15.75) * mm, v(-77.5, 15.96) * mm]});
            skFitSpline(sketch, "E2842", {"points": [v(-77.5, 15.96) * mm, v(-77.47, 16.16) * mm, v(-77.57, 16.37) * mm, v(-77.75, 16.48) * mm]});
            skFitSpline(sketch, "E2843", {"points": [v(-78.43, 15.8) * mm, v(-78.52, 15.95) * mm, v(-78.69, 16.04) * mm, v(-78.87, 16.04) * mm]});
            skLineSegment(sketch, "E2844", {"start": v(-81.3, 16.91) * mm, "end": v(-81.3, 21.38) * mm});
            skFitSpline(sketch, "E2845", {"points": [v(-29, 29.74) * mm, v(-29, 30.32) * mm, v(-29.31, 30.85) * mm, v(-29.8, 31.13) * mm]});
            skFitSpline(sketch, "E2846", {"points": [v(-29.8, 31.13) * mm, v(-30.3, 31.42) * mm, v(-30.92, 31.42) * mm, v(-31.41, 31.13) * mm]});
            skFitSpline(sketch, "E2847", {"points": [v(-31.41, 31.13) * mm, v(-31.9, 30.85) * mm, v(-32.21, 30.32) * mm, v(-32.2, 29.74) * mm]});
            skFitSpline(sketch, "E2848", {"points": [v(-32.2, 29.74) * mm, v(-32.21, 29.17) * mm, v(-31.9, 28.64) * mm, v(-31.41, 28.35) * mm]});
            skFitSpline(sketch, "E2849", {"points": [v(-31.41, 28.35) * mm, v(-30.92, 28.07) * mm, v(-30.3, 28.07) * mm, v(-29.8, 28.35) * mm]});
            skFitSpline(sketch, "E2850", {"points": [v(-29.8, 28.35) * mm, v(-29.31, 28.64) * mm, v(-29, 29.17) * mm, v(-29, 29.74) * mm]});
            skLineSegment(sketch, "E2851", {"start": v(-80.43, 22.24) * mm, "end": v(-78.87, 22.24) * mm});
            skFitSpline(sketch, "E2852", {"points": [v(-38.03, 40.94) * mm, v(-38.03, 41.52) * mm, v(-38.33, 42.04) * mm, v(-38.83, 42.33) * mm]});
            skFitSpline(sketch, "E2853", {"points": [v(-38.83, 42.33) * mm, v(-39.32, 42.62) * mm, v(-39.93, 42.62) * mm, v(-40.43, 42.33) * mm]});
            skFitSpline(sketch, "E2854", {"points": [v(-40.43, 42.33) * mm, v(-40.92, 42.04) * mm, v(-41.23, 41.52) * mm, v(-41.23, 40.94) * mm]});
            skFitSpline(sketch, "E2855", {"points": [v(-41.23, 40.94) * mm, v(-41.23, 40.06) * mm, v(-40.51, 39.34) * mm, v(-39.63, 39.34) * mm]});
            skFitSpline(sketch, "E2856", {"points": [v(-39.63, 39.34) * mm, v(-38.75, 39.34) * mm, v(-38.03, 40.06) * mm, v(-38.03, 40.94) * mm]});
            skLineSegment(sketch, "E2857", {"start": v(-78, 21.38) * mm, "end": v(-78, 16.91) * mm});
            skFitSpline(sketch, "E2858", {"points": [v(-38.03, 9.94) * mm, v(-38.03, 10.52) * mm, v(-38.33, 11.04) * mm, v(-38.83, 11.33) * mm]});
            skFitSpline(sketch, "E2859", {"points": [v(-38.83, 11.33) * mm, v(-39.32, 11.62) * mm, v(-39.93, 11.62) * mm, v(-40.43, 11.33) * mm]});
            skFitSpline(sketch, "E2860", {"points": [v(-40.43, 11.33) * mm, v(-40.92, 11.04) * mm, v(-41.23, 10.52) * mm, v(-41.23, 9.94) * mm]});
            skFitSpline(sketch, "E2861", {"points": [v(-41.23, 9.94) * mm, v(-41.23, 9.06) * mm, v(-40.51, 8.34) * mm, v(-39.63, 8.34) * mm]});
            skFitSpline(sketch, "E2862", {"points": [v(-39.63, 8.34) * mm, v(-38.75, 8.34) * mm, v(-38.03, 9.06) * mm, v(-38.03, 9.94) * mm]});
            skLineSegment(sketch, "E2863", {"start": v(-78.87, 16.04) * mm, "end": v(-80.43, 16.04) * mm});
            skFitSpline(sketch, "E2864", {"points": [v(-69.03, 40.94) * mm, v(-69.03, 41.52) * mm, v(-69.33, 42.04) * mm, v(-69.83, 42.33) * mm]});
            skFitSpline(sketch, "E2865", {"points": [v(-69.83, 42.33) * mm, v(-70.32, 42.62) * mm, v(-70.93, 42.62) * mm, v(-71.43, 42.33) * mm]});
            skFitSpline(sketch, "E2866", {"points": [v(-71.43, 42.33) * mm, v(-71.92, 42.04) * mm, v(-72.23, 41.52) * mm, v(-72.23, 40.94) * mm]});
            skFitSpline(sketch, "E2867", {"points": [v(-72.23, 40.94) * mm, v(-72.23, 40.06) * mm, v(-71.51, 39.34) * mm, v(-70.63, 39.34) * mm]});
            skFitSpline(sketch, "E2868", {"points": [v(-70.63, 39.34) * mm, v(-69.75, 39.34) * mm, v(-69.03, 40.06) * mm, v(-69.03, 40.94) * mm]});
            skFitSpline(sketch, "E2869", {"points": [v(-69.03, 9.94) * mm, v(-69.03, 10.52) * mm, v(-69.33, 11.04) * mm, v(-69.83, 11.33) * mm]});
            skFitSpline(sketch, "E2870", {"points": [v(-69.83, 11.33) * mm, v(-70.32, 11.62) * mm, v(-70.93, 11.62) * mm, v(-71.43, 11.33) * mm]});
            skFitSpline(sketch, "E2871", {"points": [v(-71.43, 11.33) * mm, v(-71.92, 11.04) * mm, v(-72.23, 10.52) * mm, v(-72.23, 9.94) * mm]});
            skFitSpline(sketch, "E2872", {"points": [v(-72.23, 9.94) * mm, v(-72.23, 9.06) * mm, v(-71.51, 8.34) * mm, v(-70.63, 8.34) * mm]});
            skFitSpline(sketch, "E2873", {"points": [v(-70.63, 8.34) * mm, v(-69.75, 8.34) * mm, v(-69.03, 9.06) * mm, v(-69.03, 9.94) * mm]});
            skFitSpline(sketch, "E2874", {"points": [v(-78.05, 29.74) * mm, v(-78.05, 30.32) * mm, v(-78.35, 30.84) * mm, v(-78.85, 31.13) * mm]});
            skFitSpline(sketch, "E2875", {"points": [v(-78.85, 31.13) * mm, v(-79.34, 31.42) * mm, v(-79.95, 31.42) * mm, v(-80.45, 31.13) * mm]});
            skFitSpline(sketch, "E2876", {"points": [v(-80.45, 31.13) * mm, v(-80.94, 30.84) * mm, v(-81.25, 30.32) * mm, v(-81.25, 29.74) * mm]});
            skFitSpline(sketch, "E2877", {"points": [v(-81.25, 29.74) * mm, v(-81.25, 28.86) * mm, v(-80.53, 28.14) * mm, v(-79.65, 28.14) * mm]});
            skFitSpline(sketch, "E2878", {"points": [v(-79.65, 28.14) * mm, v(-78.77, 28.14) * mm, v(-78.05, 28.86) * mm, v(-78.05, 29.74) * mm]});
            skFitSpline(sketch, "E2879", {"points": [v(-30.13, -53.06) * mm, v(-28.8, -53.06) * mm, v(-27.53, -52.54) * mm, v(-26.6, -51.6) * mm]});
            skFitSpline(sketch, "E2880", {"points": [v(-26.6, -51.6) * mm, v(-25.66, -50.66) * mm, v(-25.13, -49.39) * mm, v(-25.13, -48.06) * mm]});
            skFitSpline(sketch, "E2881", {"points": [v(-85.13, -48.06) * mm, v(-85.13, -50.82) * mm, v(-82.9, -53.06) * mm, v(-80.13, -53.06) * mm]});
            skFitSpline(sketch, "E2882", {"points": [v(-69.16, -3.31) * mm, v(-69.25, -3.16) * mm, v(-69.42, -3.06) * mm, v(-69.6, -3.06) * mm]});
            skFitSpline(sketch, "E2883", {"points": [v(-69.16, -3.31) * mm, v(-69.06, -3.5) * mm, v(-68.85, -3.6) * mm, v(-68.64, -3.56) * mm]});
            skFitSpline(sketch, "E2884", {"points": [v(-68.64, -3.56) * mm, v(-68.44, -3.52) * mm, v(-68.27, -3.36) * mm, v(-68.24, -3.15) * mm]});
            skFitSpline(sketch, "E2885", {"points": [v(-68.24, -3.15) * mm, v(-68.2, -2.94) * mm, v(-68.3, -2.73) * mm, v(-68.48, -2.63) * mm]});
            skFitSpline(sketch, "E2886", {"points": [v(-68.73, -2.2) * mm, v(-68.73, -2.38) * mm, v(-68.63, -2.54) * mm, v(-68.48, -2.63) * mm]});
            skLineSegment(sketch, "E2887", {"start": v(-25.13, -3.06) * mm, "end": v(-25.13, -48.06) * mm});
            skFitSpline(sketch, "E2888", {"points": [v(-68.23, -0.06) * mm, v(-68.36, -0.06) * mm, v(-68.49, -0.12) * mm, v(-68.58, -0.2) * mm]});
            skFitSpline(sketch, "E2889", {"points": [v(-68.58, -0.2) * mm, v(-68.68, -0.3) * mm, v(-68.73, -0.43) * mm, v(-68.73, -0.56) * mm]});
            skLineSegment(sketch, "E2890", {"start": v(-30.13, -53.06) * mm, "end": v(-80.13, -53.06) * mm});
            skFitSpline(sketch, "E2891", {"points": [v(-62.73, -0.56) * mm, v(-62.73, -0.29) * mm, v(-62.95, -0.06) * mm, v(-63.23, -0.06) * mm]});
            skLineSegment(sketch, "E2892", {"start": v(-85.13, -48.06) * mm, "end": v(-85.13, -3.06) * mm});
            skLineSegment(sketch, "E2893", {"start": v(-85.13, -3.06) * mm, "end": v(-69.6, -3.06) * mm});
            skFitSpline(sketch, "E2894", {"points": [v(-62.98, -2.63) * mm, v(-62.82, -2.54) * mm, v(-62.73, -2.38) * mm, v(-62.73, -2.2) * mm]});
            skFitSpline(sketch, "E2895", {"points": [v(-62.98, -2.63) * mm, v(-63.16, -2.73) * mm, v(-63.26, -2.94) * mm, v(-63.22, -3.15) * mm]});
            skFitSpline(sketch, "E2896", {"points": [v(-63.22, -3.15) * mm, v(-63.19, -3.36) * mm, v(-63.02, -3.52) * mm, v(-62.82, -3.56) * mm]});
            skFitSpline(sketch, "E2897", {"points": [v(-62.82, -3.56) * mm, v(-62.6, -3.6) * mm, v(-62.4, -3.5) * mm, v(-62.3, -3.31) * mm]});
            skFitSpline(sketch, "E2898", {"points": [v(-61.86, -3.06) * mm, v(-62.04, -3.06) * mm, v(-62.2, -3.16) * mm, v(-62.3, -3.31) * mm]});
            skLineSegment(sketch, "E2899", {"start": v(-68.73, -2.2) * mm, "end": v(-68.73, -0.56) * mm});
            skFitSpline(sketch, "E2900", {"points": [v(-47.96, -3.31) * mm, v(-48.05, -3.16) * mm, v(-48.22, -3.06) * mm, v(-48.4, -3.06) * mm]});
            skFitSpline(sketch, "E2901", {"points": [v(-47.96, -3.31) * mm, v(-47.86, -3.5) * mm, v(-47.65, -3.6) * mm, v(-47.44, -3.56) * mm]});
            skFitSpline(sketch, "E2902", {"points": [v(-47.44, -3.56) * mm, v(-47.24, -3.52) * mm, v(-47.07, -3.36) * mm, v(-47.04, -3.15) * mm]});
            skFitSpline(sketch, "E2903", {"points": [v(-47.04, -3.15) * mm, v(-47, -2.94) * mm, v(-47.1, -2.73) * mm, v(-47.28, -2.63) * mm]});
            skFitSpline(sketch, "E2904", {"points": [v(-47.53, -2.2) * mm, v(-47.53, -2.38) * mm, v(-47.43, -2.54) * mm, v(-47.28, -2.63) * mm]});
            skLineSegment(sketch, "E2905", {"start": v(-68.23, -0.06) * mm, "end": v(-63.23, -0.06) * mm});
            skFitSpline(sketch, "E2906", {"points": [v(-47.03, -0.06) * mm, v(-47.16, -0.06) * mm, v(-47.29, -0.12) * mm, v(-47.38, -0.2) * mm]});
            skFitSpline(sketch, "E2907", {"points": [v(-47.38, -0.2) * mm, v(-47.48, -0.3) * mm, v(-47.53, -0.43) * mm, v(-47.53, -0.56) * mm]});
            skLineSegment(sketch, "E2908", {"start": v(-62.73, -0.56) * mm, "end": v(-62.73, -2.2) * mm});
            skFitSpline(sketch, "E2909", {"points": [v(-41.53, -0.56) * mm, v(-41.53, -0.43) * mm, v(-41.58, -0.3) * mm, v(-41.68, -0.2) * mm]});
            skFitSpline(sketch, "E2910", {"points": [v(-41.68, -0.2) * mm, v(-41.77, -0.12) * mm, v(-41.9, -0.06) * mm, v(-42.03, -0.06) * mm]});
            skLineSegment(sketch, "E2911", {"start": v(-61.86, -3.06) * mm, "end": v(-56.73, -3.06) * mm});
            skLineSegment(sketch, "E2912", {"start": v(-56.73, -3.06) * mm, "end": v(-56.73, -6.06) * mm});
            skLineSegment(sketch, "E2913", {"start": v(-56.73, -6.06) * mm, "end": v(-58, -6.06) * mm});
            skLineSegment(sketch, "E2914", {"start": v(-58, -6.06) * mm, "end": v(-58, -10.06) * mm});
            skLineSegment(sketch, "E2915", {"start": v(-58, -10.06) * mm, "end": v(-56.73, -10.06) * mm});
            skLineSegment(sketch, "E2916", {"start": v(-56.73, -10.06) * mm, "end": v(-56.73, -13.06) * mm});
            skLineSegment(sketch, "E2917", {"start": v(-56.73, -13.06) * mm, "end": v(-53.53, -13.06) * mm});
            skLineSegment(sketch, "E2918", {"start": v(-53.53, -13.06) * mm, "end": v(-53.53, -10.06) * mm});
            skLineSegment(sketch, "E2919", {"start": v(-53.53, -10.06) * mm, "end": v(-52.25, -10.06) * mm});
            skLineSegment(sketch, "E2920", {"start": v(-52.25, -10.06) * mm, "end": v(-52.25, -6.06) * mm});
            skLineSegment(sketch, "E2921", {"start": v(-52.25, -6.06) * mm, "end": v(-53.53, -6.06) * mm});
            skLineSegment(sketch, "E2922", {"start": v(-53.53, -6.06) * mm, "end": v(-53.53, -3.06) * mm});
            skLineSegment(sketch, "E2923", {"start": v(-53.53, -3.06) * mm, "end": v(-48.4, -3.06) * mm});
            skFitSpline(sketch, "E2924", {"points": [v(-41.78, -2.63) * mm, v(-41.63, -2.54) * mm, v(-41.53, -2.38) * mm, v(-41.53, -2.2) * mm]});
            skFitSpline(sketch, "E2925", {"points": [v(-41.78, -2.63) * mm, v(-41.96, -2.73) * mm, v(-42.06, -2.94) * mm, v(-42.02, -3.15) * mm]});
            skFitSpline(sketch, "E2926", {"points": [v(-42.02, -3.15) * mm, v(-41.99, -3.36) * mm, v(-41.82, -3.52) * mm, v(-41.62, -3.56) * mm]});
            skFitSpline(sketch, "E2927", {"points": [v(-41.62, -3.56) * mm, v(-41.4, -3.6) * mm, v(-41.2, -3.5) * mm, v(-41.1, -3.31) * mm]});
            skFitSpline(sketch, "E2928", {"points": [v(-40.66, -3.06) * mm, v(-40.84, -3.06) * mm, v(-41, -3.16) * mm, v(-41.1, -3.31) * mm]});
            skLineSegment(sketch, "E2929", {"start": v(-47.53, -2.2) * mm, "end": v(-47.53, -0.56) * mm});
            skFitSpline(sketch, "E2930", {"points": [v(-44.03, -32.36) * mm, v(-44.03, -28.4) * mm, v(-46.14, -24.73) * mm, v(-49.58, -22.74) * mm]});
            skFitSpline(sketch, "E2931", {"points": [v(-49.58, -22.74) * mm, v(-53.01, -20.76) * mm, v(-57.25, -20.76) * mm, v(-60.68, -22.74) * mm]});
            skFitSpline(sketch, "E2932", {"points": [v(-60.68, -22.74) * mm, v(-64.12, -24.73) * mm, v(-66.23, -28.4) * mm, v(-66.23, -32.36) * mm]});
            skFitSpline(sketch, "E2933", {"points": [v(-66.23, -32.36) * mm, v(-66.23, -36.33) * mm, v(-64.12, -40) * mm, v(-60.68, -41.98) * mm]});
            skFitSpline(sketch, "E2934", {"points": [v(-60.68, -41.98) * mm, v(-57.25, -43.97) * mm, v(-53.01, -43.97) * mm, v(-49.58, -41.98) * mm]});
            skFitSpline(sketch, "E2935", {"points": [v(-49.58, -41.98) * mm, v(-46.14, -40) * mm, v(-44.03, -36.33) * mm, v(-44.03, -32.36) * mm]});
            skLineSegment(sketch, "E2936", {"start": v(-47.03, -0.06) * mm, "end": v(-42.03, -0.06) * mm});
            skFitSpline(sketch, "E2937", {"points": [v(-34.13, -32.36) * mm, v(-34.13, -30.93) * mm, v(-34.89, -29.6) * mm, v(-36.13, -28.9) * mm]});
            skFitSpline(sketch, "E2938", {"points": [v(-36.13, -28.9) * mm, v(-37.37, -28.18) * mm, v(-38.9, -28.18) * mm, v(-40.13, -28.9) * mm]});
            skFitSpline(sketch, "E2939", {"points": [v(-40.13, -28.9) * mm, v(-41.37, -29.6) * mm, v(-42.13, -30.93) * mm, v(-42.13, -32.36) * mm]});
            skFitSpline(sketch, "E2940", {"points": [v(-42.13, -32.36) * mm, v(-42.13, -33.8) * mm, v(-41.37, -35.12) * mm, v(-40.13, -35.83) * mm]});
            skFitSpline(sketch, "E2941", {"points": [v(-40.13, -35.83) * mm, v(-38.9, -36.55) * mm, v(-37.37, -36.55) * mm, v(-36.13, -35.83) * mm]});
            skFitSpline(sketch, "E2942", {"points": [v(-36.13, -35.83) * mm, v(-34.89, -35.12) * mm, v(-34.13, -33.8) * mm, v(-34.13, -32.36) * mm]});
            skLineSegment(sketch, "E2943", {"start": v(-41.53, -0.56) * mm, "end": v(-41.53, -2.2) * mm});
            skFitSpline(sketch, "E2944", {"points": [v(-31.4, -20.56) * mm, v(-31.57, -20.56) * mm, v(-31.74, -20.66) * mm, v(-31.83, -20.81) * mm]});
            skFitSpline(sketch, "E2945", {"points": [v(-32.5, -20.13) * mm, v(-32.7, -20.23) * mm, v(-32.79, -20.44) * mm, v(-32.75, -20.65) * mm]});
            skFitSpline(sketch, "E2946", {"points": [v(-32.75, -20.65) * mm, v(-32.72, -20.86) * mm, v(-32.55, -21.02) * mm, v(-32.35, -21.06) * mm]});
            skFitSpline(sketch, "E2947", {"points": [v(-32.35, -21.06) * mm, v(-32.14, -21.1) * mm, v(-31.93, -21) * mm, v(-31.83, -20.81) * mm]});
            skFitSpline(sketch, "E2948", {"points": [v(-32.5, -20.13) * mm, v(-32.36, -20.04) * mm, v(-32.26, -19.88) * mm, v(-32.26, -19.7) * mm]});
            skLineSegment(sketch, "E2949", {"start": v(-40.66, -3.06) * mm, "end": v(-25.13, -3.06) * mm});
            skFitSpline(sketch, "E2950", {"points": [v(-32.26, -15.23) * mm, v(-32.26, -15.05) * mm, v(-32.36, -14.89) * mm, v(-32.5, -14.8) * mm]});
            skFitSpline(sketch, "E2951", {"points": [v(-31.83, -14.11) * mm, v(-31.93, -13.93) * mm, v(-32.14, -13.83) * mm, v(-32.35, -13.87) * mm]});
            skFitSpline(sketch, "E2952", {"points": [v(-32.35, -13.87) * mm, v(-32.55, -13.9) * mm, v(-32.72, -14.07) * mm, v(-32.75, -14.28) * mm]});
            skFitSpline(sketch, "E2953", {"points": [v(-32.75, -14.28) * mm, v(-32.79, -14.48) * mm, v(-32.7, -14.7) * mm, v(-32.5, -14.8) * mm]});
            skFitSpline(sketch, "E2954", {"points": [v(-31.83, -14.11) * mm, v(-31.74, -14.27) * mm, v(-31.57, -14.36) * mm, v(-31.4, -14.36) * mm]});
            skFitSpline(sketch, "E2955", {"points": [v(-29.83, -14.36) * mm, v(-29.65, -14.36) * mm, v(-29.48, -14.27) * mm, v(-29.4, -14.11) * mm]});
            skFitSpline(sketch, "E2956", {"points": [v(-28.7, -14.8) * mm, v(-28.53, -14.7) * mm, v(-28.43, -14.48) * mm, v(-28.47, -14.28) * mm]});
            skFitSpline(sketch, "E2957", {"points": [v(-28.47, -14.28) * mm, v(-28.5, -14.07) * mm, v(-28.67, -13.9) * mm, v(-28.87, -13.87) * mm]});
            skFitSpline(sketch, "E2958", {"points": [v(-28.87, -13.87) * mm, v(-29.08, -13.83) * mm, v(-29.29, -13.93) * mm, v(-29.4, -14.11) * mm]});
            skFitSpline(sketch, "E2959", {"points": [v(-28.7, -14.8) * mm, v(-28.86, -14.89) * mm, v(-28.96, -15.05) * mm, v(-28.96, -15.23) * mm]});
            skFitSpline(sketch, "E2960", {"points": [v(-28.96, -19.7) * mm, v(-28.96, -19.88) * mm, v(-28.86, -20.04) * mm, v(-28.7, -20.13) * mm]});
            skFitSpline(sketch, "E2961", {"points": [v(-29.4, -20.81) * mm, v(-29.29, -21) * mm, v(-29.08, -21.1) * mm, v(-28.87, -21.06) * mm]});
            skFitSpline(sketch, "E2962", {"points": [v(-28.87, -21.06) * mm, v(-28.67, -21.02) * mm, v(-28.5, -20.86) * mm, v(-28.47, -20.65) * mm]});
            skFitSpline(sketch, "E2963", {"points": [v(-28.47, -20.65) * mm, v(-28.43, -20.44) * mm, v(-28.53, -20.23) * mm, v(-28.7, -20.13) * mm]});
            skFitSpline(sketch, "E2964", {"points": [v(-29.4, -20.81) * mm, v(-29.48, -20.66) * mm, v(-29.65, -20.56) * mm, v(-29.83, -20.56) * mm]});
            skLineSegment(sketch, "E2965", {"start": v(-32.26, -19.7) * mm, "end": v(-32.26, -15.23) * mm});
            skFitSpline(sketch, "E2966", {"points": [v(-31.4, -41.76) * mm, v(-31.57, -41.76) * mm, v(-31.74, -41.86) * mm, v(-31.83, -42.01) * mm]});
            skFitSpline(sketch, "E2967", {"points": [v(-32.5, -41.33) * mm, v(-32.7, -41.43) * mm, v(-32.79, -41.64) * mm, v(-32.75, -41.85) * mm]});
            skFitSpline(sketch, "E2968", {"points": [v(-32.75, -41.85) * mm, v(-32.72, -42.06) * mm, v(-32.55, -42.22) * mm, v(-32.35, -42.25) * mm]});
            skFitSpline(sketch, "E2969", {"points": [v(-32.35, -42.25) * mm, v(-32.14, -42.3) * mm, v(-31.93, -42.2) * mm, v(-31.83, -42.01) * mm]});
            skFitSpline(sketch, "E2970", {"points": [v(-32.5, -41.33) * mm, v(-32.36, -41.24) * mm, v(-32.26, -41.08) * mm, v(-32.26, -40.9) * mm]});
            skLineSegment(sketch, "E2971", {"start": v(-31.4, -14.36) * mm, "end": v(-29.83, -14.36) * mm});
            skFitSpline(sketch, "E2972", {"points": [v(-32.26, -36.43) * mm, v(-32.26, -36.25) * mm, v(-32.36, -36.08) * mm, v(-32.5, -36) * mm]});
            skFitSpline(sketch, "E2973", {"points": [v(-31.83, -35.31) * mm, v(-31.93, -35.13) * mm, v(-32.14, -35.03) * mm, v(-32.35, -35.07) * mm]});
            skFitSpline(sketch, "E2974", {"points": [v(-32.35, -35.07) * mm, v(-32.55, -35.1) * mm, v(-32.72, -35.27) * mm, v(-32.75, -35.48) * mm]});
            skFitSpline(sketch, "E2975", {"points": [v(-32.75, -35.48) * mm, v(-32.79, -35.68) * mm, v(-32.7, -35.9) * mm, v(-32.5, -36) * mm]});
            skFitSpline(sketch, "E2976", {"points": [v(-31.83, -35.31) * mm, v(-31.74, -35.47) * mm, v(-31.57, -35.56) * mm, v(-31.4, -35.56) * mm]});
            skLineSegment(sketch, "E2977", {"start": v(-28.96, -15.23) * mm, "end": v(-28.96, -19.7) * mm});
            skFitSpline(sketch, "E2978", {"points": [v(-29.83, -35.56) * mm, v(-29.65, -35.56) * mm, v(-29.48, -35.47) * mm, v(-29.4, -35.31) * mm]});
            skFitSpline(sketch, "E2979", {"points": [v(-28.7, -36) * mm, v(-28.53, -35.9) * mm, v(-28.43, -35.68) * mm, v(-28.47, -35.48) * mm]});
            skFitSpline(sketch, "E2980", {"points": [v(-28.47, -35.48) * mm, v(-28.5, -35.27) * mm, v(-28.67, -35.1) * mm, v(-28.87, -35.07) * mm]});
            skFitSpline(sketch, "E2981", {"points": [v(-28.87, -35.07) * mm, v(-29.08, -35.03) * mm, v(-29.29, -35.13) * mm, v(-29.4, -35.31) * mm]});
            skFitSpline(sketch, "E2982", {"points": [v(-28.7, -36) * mm, v(-28.86, -36.08) * mm, v(-28.96, -36.25) * mm, v(-28.96, -36.43) * mm]});
            skLineSegment(sketch, "E2983", {"start": v(-29.83, -20.56) * mm, "end": v(-31.4, -20.56) * mm});
            skFitSpline(sketch, "E2984", {"points": [v(-28.96, -40.9) * mm, v(-28.96, -41.08) * mm, v(-28.86, -41.24) * mm, v(-28.7, -41.33) * mm]});
            skFitSpline(sketch, "E2985", {"points": [v(-29.4, -42.01) * mm, v(-29.29, -42.2) * mm, v(-29.08, -42.3) * mm, v(-28.87, -42.25) * mm]});
            skFitSpline(sketch, "E2986", {"points": [v(-28.87, -42.25) * mm, v(-28.67, -42.22) * mm, v(-28.5, -42.06) * mm, v(-28.47, -41.85) * mm]});
            skFitSpline(sketch, "E2987", {"points": [v(-28.47, -41.85) * mm, v(-28.43, -41.64) * mm, v(-28.53, -41.43) * mm, v(-28.7, -41.33) * mm]});
            skFitSpline(sketch, "E2988", {"points": [v(-29.4, -42.01) * mm, v(-29.48, -41.86) * mm, v(-29.65, -41.76) * mm, v(-29.83, -41.76) * mm]});
            skLineSegment(sketch, "E2989", {"start": v(-32.26, -40.9) * mm, "end": v(-32.26, -36.43) * mm});
            skFitSpline(sketch, "E2990", {"points": [v(-80.43, -20.56) * mm, v(-80.61, -20.56) * mm, v(-80.78, -20.66) * mm, v(-80.87, -20.81) * mm]});
            skFitSpline(sketch, "E2991", {"points": [v(-81.55, -20.13) * mm, v(-81.73, -20.23) * mm, v(-81.83, -20.44) * mm, v(-81.8, -20.65) * mm]});
            skFitSpline(sketch, "E2992", {"points": [v(-81.8, -20.65) * mm, v(-81.76, -20.86) * mm, v(-81.6, -21.02) * mm, v(-81.39, -21.06) * mm]});
            skFitSpline(sketch, "E2993", {"points": [v(-81.39, -21.06) * mm, v(-81.18, -21.1) * mm, v(-80.97, -21) * mm, v(-80.87, -20.81) * mm]});
            skFitSpline(sketch, "E2994", {"points": [v(-81.55, -20.13) * mm, v(-81.4, -20.04) * mm, v(-81.3, -19.88) * mm, v(-81.3, -19.7) * mm]});
            skLineSegment(sketch, "E2995", {"start": v(-31.4, -35.56) * mm, "end": v(-29.83, -35.56) * mm});
            skFitSpline(sketch, "E2996", {"points": [v(-81.3, -15.23) * mm, v(-81.3, -15.05) * mm, v(-81.4, -14.89) * mm, v(-81.55, -14.8) * mm]});
            skFitSpline(sketch, "E2997", {"points": [v(-80.87, -14.11) * mm, v(-80.97, -13.93) * mm, v(-81.18, -13.83) * mm, v(-81.39, -13.87) * mm]});
            skFitSpline(sketch, "E2998", {"points": [v(-81.39, -13.87) * mm, v(-81.6, -13.9) * mm, v(-81.76, -14.07) * mm, v(-81.8, -14.28) * mm]});
            skFitSpline(sketch, "E2999", {"points": [v(-81.8, -14.28) * mm, v(-81.83, -14.48) * mm, v(-81.73, -14.7) * mm, v(-81.55, -14.8) * mm]});
            skFitSpline(sketch, "E3000", {"points": [v(-80.87, -14.11) * mm, v(-80.78, -14.27) * mm, v(-80.61, -14.36) * mm, v(-80.43, -14.36) * mm]});
            skLineSegment(sketch, "E3001", {"start": v(-28.96, -36.43) * mm, "end": v(-28.96, -40.9) * mm});
            skFitSpline(sketch, "E3002", {"points": [v(-78.87, -14.36) * mm, v(-78.69, -14.36) * mm, v(-78.52, -14.27) * mm, v(-78.43, -14.11) * mm]});
            skFitSpline(sketch, "E3003", {"points": [v(-77.75, -14.8) * mm, v(-77.57, -14.7) * mm, v(-77.47, -14.48) * mm, v(-77.5, -14.28) * mm]});
            skFitSpline(sketch, "E3004", {"points": [v(-77.5, -14.28) * mm, v(-77.54, -14.07) * mm, v(-77.7, -13.9) * mm, v(-77.91, -13.87) * mm]});
            skFitSpline(sketch, "E3005", {"points": [v(-77.91, -13.87) * mm, v(-78.12, -13.83) * mm, v(-78.33, -13.93) * mm, v(-78.43, -14.11) * mm]});
            skFitSpline(sketch, "E3006", {"points": [v(-77.75, -14.8) * mm, v(-77.9, -14.89) * mm, v(-78, -15.05) * mm, v(-78, -15.23) * mm]});
            skLineSegment(sketch, "E3007", {"start": v(-29.83, -41.76) * mm, "end": v(-31.4, -41.76) * mm});
            skFitSpline(sketch, "E3008", {"points": [v(-78, -19.7) * mm, v(-78, -19.88) * mm, v(-77.9, -20.04) * mm, v(-77.75, -20.13) * mm]});
            skFitSpline(sketch, "E3009", {"points": [v(-78.43, -20.81) * mm, v(-78.33, -21) * mm, v(-78.12, -21.1) * mm, v(-77.91, -21.06) * mm]});
            skFitSpline(sketch, "E3010", {"points": [v(-77.91, -21.06) * mm, v(-77.7, -21.02) * mm, v(-77.54, -20.86) * mm, v(-77.5, -20.65) * mm]});
            skFitSpline(sketch, "E3011", {"points": [v(-77.5, -20.65) * mm, v(-77.47, -20.44) * mm, v(-77.57, -20.23) * mm, v(-77.75, -20.13) * mm]});
            skFitSpline(sketch, "E3012", {"points": [v(-78.43, -20.81) * mm, v(-78.52, -20.66) * mm, v(-78.69, -20.56) * mm, v(-78.87, -20.56) * mm]});
            skLineSegment(sketch, "E3013", {"start": v(-81.3, -19.7) * mm, "end": v(-81.3, -15.23) * mm});
            skFitSpline(sketch, "E3014", {"points": [v(-80.43, -41.76) * mm, v(-80.61, -41.76) * mm, v(-80.78, -41.86) * mm, v(-80.87, -42.01) * mm]});
            skFitSpline(sketch, "E3015", {"points": [v(-81.55, -41.33) * mm, v(-81.73, -41.43) * mm, v(-81.83, -41.64) * mm, v(-81.8, -41.85) * mm]});
            skFitSpline(sketch, "E3016", {"points": [v(-81.8, -41.85) * mm, v(-81.76, -42.06) * mm, v(-81.6, -42.22) * mm, v(-81.39, -42.25) * mm]});
            skFitSpline(sketch, "E3017", {"points": [v(-81.39, -42.25) * mm, v(-81.18, -42.3) * mm, v(-80.97, -42.2) * mm, v(-80.87, -42.01) * mm]});
            skFitSpline(sketch, "E3018", {"points": [v(-81.55, -41.33) * mm, v(-81.4, -41.24) * mm, v(-81.3, -41.08) * mm, v(-81.3, -40.9) * mm]});
            skLineSegment(sketch, "E3019", {"start": v(-80.43, -14.36) * mm, "end": v(-78.87, -14.36) * mm});
            skFitSpline(sketch, "E3020", {"points": [v(-81.3, -36.43) * mm, v(-81.3, -36.25) * mm, v(-81.4, -36.08) * mm, v(-81.55, -36) * mm]});
            skFitSpline(sketch, "E3021", {"points": [v(-80.87, -35.31) * mm, v(-80.97, -35.13) * mm, v(-81.18, -35.03) * mm, v(-81.39, -35.07) * mm]});
            skFitSpline(sketch, "E3022", {"points": [v(-81.39, -35.07) * mm, v(-81.6, -35.1) * mm, v(-81.76, -35.27) * mm, v(-81.8, -35.48) * mm]});
            skFitSpline(sketch, "E3023", {"points": [v(-81.8, -35.48) * mm, v(-81.83, -35.68) * mm, v(-81.73, -35.9) * mm, v(-81.55, -36) * mm]});
            skFitSpline(sketch, "E3024", {"points": [v(-80.87, -35.31) * mm, v(-80.78, -35.47) * mm, v(-80.61, -35.56) * mm, v(-80.43, -35.56) * mm]});
            skLineSegment(sketch, "E3025", {"start": v(-78, -15.23) * mm, "end": v(-78, -19.7) * mm});
            skFitSpline(sketch, "E3026", {"points": [v(-78.87, -35.56) * mm, v(-78.69, -35.56) * mm, v(-78.52, -35.47) * mm, v(-78.43, -35.31) * mm]});
            skFitSpline(sketch, "E3027", {"points": [v(-77.75, -36) * mm, v(-77.57, -35.9) * mm, v(-77.47, -35.68) * mm, v(-77.5, -35.48) * mm]});
            skFitSpline(sketch, "E3028", {"points": [v(-77.5, -35.48) * mm, v(-77.54, -35.27) * mm, v(-77.7, -35.1) * mm, v(-77.91, -35.07) * mm]});
            skFitSpline(sketch, "E3029", {"points": [v(-77.91, -35.07) * mm, v(-78.12, -35.03) * mm, v(-78.33, -35.13) * mm, v(-78.43, -35.31) * mm]});
            skFitSpline(sketch, "E3030", {"points": [v(-77.75, -36) * mm, v(-77.9, -36.08) * mm, v(-78, -36.25) * mm, v(-78, -36.43) * mm]});
            skLineSegment(sketch, "E3031", {"start": v(-78.87, -20.56) * mm, "end": v(-80.43, -20.56) * mm});
            skFitSpline(sketch, "E3032", {"points": [v(-78, -40.9) * mm, v(-78, -41.08) * mm, v(-77.9, -41.24) * mm, v(-77.75, -41.33) * mm]});
            skFitSpline(sketch, "E3033", {"points": [v(-78.43, -42.01) * mm, v(-78.33, -42.2) * mm, v(-78.12, -42.3) * mm, v(-77.91, -42.25) * mm]});
            skFitSpline(sketch, "E3034", {"points": [v(-77.91, -42.25) * mm, v(-77.7, -42.22) * mm, v(-77.54, -42.06) * mm, v(-77.5, -41.85) * mm]});
            skFitSpline(sketch, "E3035", {"points": [v(-77.5, -41.85) * mm, v(-77.47, -41.64) * mm, v(-77.57, -41.43) * mm, v(-77.75, -41.33) * mm]});
            skFitSpline(sketch, "E3036", {"points": [v(-78.43, -42.01) * mm, v(-78.52, -41.86) * mm, v(-78.69, -41.76) * mm, v(-78.87, -41.76) * mm]});
            skLineSegment(sketch, "E3037", {"start": v(-81.3, -40.9) * mm, "end": v(-81.3, -36.43) * mm});
            skFitSpline(sketch, "E3038", {"points": [v(-29, -28.06) * mm, v(-29, -27.49) * mm, v(-29.31, -26.96) * mm, v(-29.8, -26.67) * mm]});
            skFitSpline(sketch, "E3039", {"points": [v(-29.8, -26.67) * mm, v(-30.3, -26.38) * mm, v(-30.92, -26.38) * mm, v(-31.41, -26.67) * mm]});
            skFitSpline(sketch, "E3040", {"points": [v(-31.41, -26.67) * mm, v(-31.9, -26.96) * mm, v(-32.21, -27.49) * mm, v(-32.2, -28.06) * mm]});
            skFitSpline(sketch, "E3041", {"points": [v(-32.2, -28.06) * mm, v(-32.21, -28.64) * mm, v(-31.9, -29.17) * mm, v(-31.41, -29.45) * mm]});
            skFitSpline(sketch, "E3042", {"points": [v(-31.41, -29.45) * mm, v(-30.92, -29.74) * mm, v(-30.3, -29.74) * mm, v(-29.8, -29.45) * mm]});
            skFitSpline(sketch, "E3043", {"points": [v(-29.8, -29.45) * mm, v(-29.31, -29.17) * mm, v(-29, -28.64) * mm, v(-29, -28.06) * mm]});
            skLineSegment(sketch, "E3044", {"start": v(-80.43, -35.56) * mm, "end": v(-78.87, -35.56) * mm});
            skFitSpline(sketch, "E3045", {"points": [v(-38.03, -16.86) * mm, v(-38.03, -16.3) * mm, v(-38.33, -15.76) * mm, v(-38.83, -15.48) * mm]});
            skFitSpline(sketch, "E3046", {"points": [v(-38.83, -15.48) * mm, v(-39.32, -15.2) * mm, v(-39.93, -15.2) * mm, v(-40.43, -15.48) * mm]});
            skFitSpline(sketch, "E3047", {"points": [v(-40.43, -15.48) * mm, v(-40.92, -15.76) * mm, v(-41.23, -16.3) * mm, v(-41.23, -16.86) * mm]});
            skFitSpline(sketch, "E3048", {"points": [v(-41.23, -16.86) * mm, v(-41.23, -17.75) * mm, v(-40.51, -18.46) * mm, v(-39.63, -18.46) * mm]});
            skFitSpline(sketch, "E3049", {"points": [v(-39.63, -18.46) * mm, v(-38.75, -18.46) * mm, v(-38.03, -17.75) * mm, v(-38.03, -16.86) * mm]});
            skLineSegment(sketch, "E3050", {"start": v(-78, -36.43) * mm, "end": v(-78, -40.9) * mm});
            skFitSpline(sketch, "E3051", {"points": [v(-38.03, -47.86) * mm, v(-38.03, -47.3) * mm, v(-38.33, -46.76) * mm, v(-38.83, -46.48) * mm]});
            skFitSpline(sketch, "E3052", {"points": [v(-38.83, -46.48) * mm, v(-39.32, -46.2) * mm, v(-39.93, -46.2) * mm, v(-40.43, -46.48) * mm]});
            skFitSpline(sketch, "E3053", {"points": [v(-40.43, -46.48) * mm, v(-40.92, -46.76) * mm, v(-41.23, -47.3) * mm, v(-41.23, -47.86) * mm]});
            skFitSpline(sketch, "E3054", {"points": [v(-41.23, -47.86) * mm, v(-41.23, -48.75) * mm, v(-40.51, -49.46) * mm, v(-39.63, -49.46) * mm]});
            skFitSpline(sketch, "E3055", {"points": [v(-39.63, -49.46) * mm, v(-38.75, -49.46) * mm, v(-38.03, -48.75) * mm, v(-38.03, -47.86) * mm]});
            skLineSegment(sketch, "E3056", {"start": v(-78.87, -41.76) * mm, "end": v(-80.43, -41.76) * mm});
            skFitSpline(sketch, "E3057", {"points": [v(-69.03, -16.86) * mm, v(-69.03, -16.3) * mm, v(-69.33, -15.76) * mm, v(-69.83, -15.48) * mm]});
            skFitSpline(sketch, "E3058", {"points": [v(-69.83, -15.48) * mm, v(-70.32, -15.2) * mm, v(-70.93, -15.2) * mm, v(-71.43, -15.48) * mm]});
            skFitSpline(sketch, "E3059", {"points": [v(-71.43, -15.48) * mm, v(-71.92, -15.76) * mm, v(-72.23, -16.3) * mm, v(-72.23, -16.86) * mm]});
            skFitSpline(sketch, "E3060", {"points": [v(-72.23, -16.86) * mm, v(-72.23, -17.75) * mm, v(-71.51, -18.46) * mm, v(-70.63, -18.46) * mm]});
            skFitSpline(sketch, "E3061", {"points": [v(-70.63, -18.46) * mm, v(-69.75, -18.46) * mm, v(-69.03, -17.75) * mm, v(-69.03, -16.86) * mm]});
            skFitSpline(sketch, "E3062", {"points": [v(-69.03, -47.86) * mm, v(-69.03, -47.3) * mm, v(-69.33, -46.76) * mm, v(-69.83, -46.48) * mm]});
            skFitSpline(sketch, "E3063", {"points": [v(-69.83, -46.48) * mm, v(-70.32, -46.2) * mm, v(-70.93, -46.2) * mm, v(-71.43, -46.48) * mm]});
            skFitSpline(sketch, "E3064", {"points": [v(-71.43, -46.48) * mm, v(-71.92, -46.76) * mm, v(-72.23, -47.3) * mm, v(-72.23, -47.86) * mm]});
            skFitSpline(sketch, "E3065", {"points": [v(-72.23, -47.86) * mm, v(-72.23, -48.75) * mm, v(-71.51, -49.46) * mm, v(-70.63, -49.46) * mm]});
            skFitSpline(sketch, "E3066", {"points": [v(-70.63, -49.46) * mm, v(-69.75, -49.46) * mm, v(-69.03, -48.75) * mm, v(-69.03, -47.86) * mm]});
            skFitSpline(sketch, "E3067", {"points": [v(-78.05, -28.06) * mm, v(-78.05, -27.5) * mm, v(-78.35, -26.96) * mm, v(-78.85, -26.68) * mm]});
            skFitSpline(sketch, "E3068", {"points": [v(-78.85, -26.68) * mm, v(-79.34, -26.4) * mm, v(-79.95, -26.4) * mm, v(-80.45, -26.68) * mm]});
            skFitSpline(sketch, "E3069", {"points": [v(-80.45, -26.68) * mm, v(-80.94, -26.96) * mm, v(-81.25, -27.5) * mm, v(-81.25, -28.06) * mm]});
            skFitSpline(sketch, "E3070", {"points": [v(-81.25, -28.06) * mm, v(-81.25, -28.95) * mm, v(-80.53, -29.66) * mm, v(-79.65, -29.66) * mm]});
            skFitSpline(sketch, "E3071", {"points": [v(-79.65, -29.66) * mm, v(-78.77, -29.66) * mm, v(-78.05, -28.95) * mm, v(-78.05, -28.06) * mm]});
            skFitSpline(sketch, "E3072", {"points": [v(-335.74, 173.5) * mm, v(-340.82, 171.99) * mm, v(-344.3, 167.31) * mm, v(-344.3, 162) * mm]});
            skFitSpline(sketch, "E3073", {"points": [v(-335.17, 158.77) * mm, v(-334.99, 158.77) * mm, v(-334.82, 158.87) * mm, v(-334.73, 159.02) * mm]});
            skFitSpline(sketch, "E3074", {"points": [v(-334.05, 158.34) * mm, v(-333.87, 158.44) * mm, v(-333.77, 158.65) * mm, v(-333.8, 158.86) * mm]});
            skFitSpline(sketch, "E3075", {"points": [v(-333.8, 158.86) * mm, v(-333.84, 159.06) * mm, v(-334, 159.23) * mm, v(-334.21, 159.26) * mm]});
            skFitSpline(sketch, "E3076", {"points": [v(-334.21, 159.26) * mm, v(-334.42, 159.3) * mm, v(-334.63, 159.2) * mm, v(-334.73, 159.02) * mm]});
            skFitSpline(sketch, "E3077", {"points": [v(-334.05, 158.34) * mm, v(-334.2, 158.25) * mm, v(-334.3, 158.08) * mm, v(-334.3, 157.9) * mm]});
            skFitSpline(sketch, "E3078", {"points": [v(-334.3, 156.34) * mm, v(-334.3, 156.16) * mm, v(-334.2, 156) * mm, v(-334.05, 155.9) * mm]});
            skFitSpline(sketch, "E3079", {"points": [v(-334.73, 155.22) * mm, v(-334.63, 155.04) * mm, v(-334.42, 154.94) * mm, v(-334.22, 154.98) * mm]});
            skFitSpline(sketch, "E3080", {"points": [v(-334.22, 154.98) * mm, v(-334, 155.01) * mm, v(-333.85, 155.18) * mm, v(-333.8, 155.38) * mm]});
            skFitSpline(sketch, "E3081", {"points": [v(-333.8, 155.38) * mm, v(-333.77, 155.59) * mm, v(-333.87, 155.8) * mm, v(-334.05, 155.9) * mm]});
            skFitSpline(sketch, "E3082", {"points": [v(-334.73, 155.22) * mm, v(-334.82, 155.37) * mm, v(-334.99, 155.47) * mm, v(-335.17, 155.47) * mm]});
            skFitSpline(sketch, "E3083", {"points": [v(-344.3, 124.95) * mm, v(-344.3, 118.32) * mm, v(-338.93, 112.95) * mm, v(-332.3, 112.95) * mm]});
            skLineSegment(sketch, "E3084", {"start": v(-344.3, 162) * mm, "end": v(-344.3, 158.77) * mm});
            skLineSegment(sketch, "E3085", {"start": v(-344.3, 158.77) * mm, "end": v(-335.17, 158.77) * mm});
            skFitSpline(sketch, "E3086", {"points": [v(-310.7, 112.95) * mm, v(-306.16, 112.94) * mm, v(-302.02, 115.5) * mm, v(-299.98, 119.55) * mm]});
            skFitSpline(sketch, "E3087", {"points": [v(-309.6, 126.32) * mm, v(-309.6, 128.1) * mm, v(-310.55, 129.75) * mm, v(-312.1, 130.65) * mm]});
            skFitSpline(sketch, "E3088", {"points": [v(-312.1, 130.65) * mm, v(-313.65, 131.54) * mm, v(-315.55, 131.54) * mm, v(-317.1, 130.65) * mm]});
            skFitSpline(sketch, "E3089", {"points": [v(-317.1, 130.65) * mm, v(-318.65, 129.75) * mm, v(-319.6, 128.1) * mm, v(-319.6, 126.32) * mm]});
            skFitSpline(sketch, "E3090", {"points": [v(-319.6, 126.32) * mm, v(-319.6, 124.53) * mm, v(-318.65, 122.88) * mm, v(-317.1, 121.99) * mm]});
            skFitSpline(sketch, "E3091", {"points": [v(-317.1, 121.99) * mm, v(-315.55, 121.1) * mm, v(-313.65, 121.1) * mm, v(-312.1, 121.99) * mm]});
            skFitSpline(sketch, "E3092", {"points": [v(-312.1, 121.99) * mm, v(-310.55, 122.88) * mm, v(-309.6, 124.53) * mm, v(-309.6, 126.32) * mm]});
            skLineSegment(sketch, "E3093", {"start": v(-334.3, 157.9) * mm, "end": v(-334.3, 156.34) * mm});
            skFitSpline(sketch, "E3094", {"points": [v(-327.6, 126.32) * mm, v(-327.6, 127.75) * mm, v(-328.36, 129.07) * mm, v(-329.6, 129.78) * mm]});
            skFitSpline(sketch, "E3095", {"points": [v(-329.6, 129.78) * mm, v(-330.84, 130.5) * mm, v(-332.36, 130.5) * mm, v(-333.6, 129.78) * mm]});
            skFitSpline(sketch, "E3096", {"points": [v(-333.6, 129.78) * mm, v(-334.84, 129.07) * mm, v(-335.6, 127.75) * mm, v(-335.6, 126.32) * mm]});
            skFitSpline(sketch, "E3097", {"points": [v(-335.6, 126.32) * mm, v(-335.6, 124.9) * mm, v(-334.84, 123.57) * mm, v(-333.6, 122.86) * mm]});
            skFitSpline(sketch, "E3098", {"points": [v(-333.6, 122.86) * mm, v(-332.36, 122.14) * mm, v(-330.84, 122.14) * mm, v(-329.6, 122.86) * mm]});
            skFitSpline(sketch, "E3099", {"points": [v(-329.6, 122.86) * mm, v(-328.36, 123.57) * mm, v(-327.6, 124.9) * mm, v(-327.6, 126.32) * mm]});
            skLineSegment(sketch, "E3100", {"start": v(-335.17, 155.47) * mm, "end": v(-344.3, 155.47) * mm});
            skLineSegment(sketch, "E3101", {"start": v(-344.3, 155.47) * mm, "end": v(-344.3, 124.95) * mm});
            skFitSpline(sketch, "E3102", {"points": [v(-306.88, 157.12) * mm, v(-306.87, 157.7) * mm, v(-307.18, 158.22) * mm, v(-307.67, 158.51) * mm]});
            skFitSpline(sketch, "E3103", {"points": [v(-307.67, 158.51) * mm, v(-308.17, 158.8) * mm, v(-308.78, 158.8) * mm, v(-309.28, 158.51) * mm]});
            skFitSpline(sketch, "E3104", {"points": [v(-309.28, 158.51) * mm, v(-309.77, 158.22) * mm, v(-310.08, 157.7) * mm, v(-310.08, 157.12) * mm]});
            skFitSpline(sketch, "E3105", {"points": [v(-310.08, 157.12) * mm, v(-310.08, 156.55) * mm, v(-309.77, 156.02) * mm, v(-309.28, 155.73) * mm]});
            skFitSpline(sketch, "E3106", {"points": [v(-309.28, 155.73) * mm, v(-308.78, 155.44) * mm, v(-308.17, 155.44) * mm, v(-307.67, 155.73) * mm]});
            skFitSpline(sketch, "E3107", {"points": [v(-307.67, 155.73) * mm, v(-307.18, 156.02) * mm, v(-306.87, 156.55) * mm, v(-306.88, 157.12) * mm]});
            skLineSegment(sketch, "E3108", {"start": v(-332.3, 112.95) * mm, "end": v(-310.7, 112.95) * mm});
            skFitSpline(sketch, "E3109", {"points": [v(-256.3, 168.28) * mm, v(-256.3, 170.03) * mm, v(-256.69, 171.77) * mm, v(-257.43, 173.36) * mm]});
            skFitSpline(sketch, "E3110", {"points": [v(-282.65, 157.95) * mm, v(-282.65, 158.13) * mm, v(-282.75, 158.3) * mm, v(-282.9, 158.38) * mm]});
            skFitSpline(sketch, "E3111", {"points": [v(-282.22, 159.06) * mm, v(-282.32, 159.25) * mm, v(-282.53, 159.34) * mm, v(-282.74, 159.3) * mm]});
            skFitSpline(sketch, "E3112", {"points": [v(-282.74, 159.3) * mm, v(-282.95, 159.27) * mm, v(-283.1, 159.1) * mm, v(-283.14, 158.9) * mm]});
            skFitSpline(sketch, "E3113", {"points": [v(-283.14, 158.9) * mm, v(-283.18, 158.7) * mm, v(-283.08, 158.49) * mm, v(-282.9, 158.38) * mm]});
            skFitSpline(sketch, "E3114", {"points": [v(-282.22, 159.06) * mm, v(-282.13, 158.9) * mm, v(-281.96, 158.81) * mm, v(-281.79, 158.81) * mm]});
            skLineSegment(sketch, "E3115", {"start": v(-267.83, 158.81) * mm, "end": v(-256.3, 158.81) * mm});
            skLineSegment(sketch, "E3116", {"start": v(-256.3, 158.81) * mm, "end": v(-256.3, 168.28) * mm});
            skFitSpline(sketch, "E3117", {"points": [v(-271.13, 168.6) * mm, v(-271.13, 168.78) * mm, v(-271.22, 168.94) * mm, v(-271.38, 169.03) * mm]});
            skFitSpline(sketch, "E3118", {"points": [v(-270.7, 169.71) * mm, v(-270.8, 169.9) * mm, v(-271, 170) * mm, v(-271.21, 169.96) * mm]});
            skFitSpline(sketch, "E3119", {"points": [v(-271.21, 169.96) * mm, v(-271.42, 169.92) * mm, v(-271.58, 169.76) * mm, v(-271.62, 169.55) * mm]});
            skFitSpline(sketch, "E3120", {"points": [v(-271.62, 169.55) * mm, v(-271.66, 169.34) * mm, v(-271.56, 169.14) * mm, v(-271.38, 169.03) * mm]});
            skFitSpline(sketch, "E3121", {"points": [v(-270.7, 169.71) * mm, v(-270.6, 169.56) * mm, v(-270.44, 169.46) * mm, v(-270.26, 169.46) * mm]});
            skLineSegment(sketch, "E3122", {"start": v(-257.43, 173.36) * mm, "end": v(-267.83, 189.81) * mm});
            skLineSegment(sketch, "E3123", {"start": v(-267.83, 189.81) * mm, "end": v(-270.92, 189.81) * mm});
            skFitSpline(sketch, "E3124", {"points": [v(-268.7, 169.46) * mm, v(-268.51, 169.46) * mm, v(-268.35, 169.56) * mm, v(-268.26, 169.71) * mm]});
            skFitSpline(sketch, "E3125", {"points": [v(-267.58, 169.03) * mm, v(-267.4, 169.13) * mm, v(-267.3, 169.34) * mm, v(-267.33, 169.55) * mm]});
            skFitSpline(sketch, "E3126", {"points": [v(-267.33, 169.55) * mm, v(-267.37, 169.76) * mm, v(-267.53, 169.92) * mm, v(-267.74, 169.95) * mm]});
            skFitSpline(sketch, "E3127", {"points": [v(-267.74, 169.95) * mm, v(-267.95, 170) * mm, v(-268.15, 169.9) * mm, v(-268.26, 169.71) * mm]});
            skFitSpline(sketch, "E3128", {"points": [v(-267.58, 169.03) * mm, v(-267.73, 168.94) * mm, v(-267.83, 168.77) * mm, v(-267.83, 168.6) * mm]});
            skLineSegment(sketch, "E3129", {"start": v(-282.65, 155.46) * mm, "end": v(-282.65, 157.95) * mm});
            skFitSpline(sketch, "E3130", {"points": [v(-267.88, 179.46) * mm, v(-267.88, 180.04) * mm, v(-268.18, 180.56) * mm, v(-268.68, 180.85) * mm]});
            skFitSpline(sketch, "E3131", {"points": [v(-268.68, 180.85) * mm, v(-269.17, 181.14) * mm, v(-269.78, 181.14) * mm, v(-270.28, 180.85) * mm]});
            skFitSpline(sketch, "E3132", {"points": [v(-270.28, 180.85) * mm, v(-270.77, 180.56) * mm, v(-271.08, 180.04) * mm, v(-271.08, 179.46) * mm]});
            skFitSpline(sketch, "E3133", {"points": [v(-271.08, 179.46) * mm, v(-271.08, 178.9) * mm, v(-270.77, 178.36) * mm, v(-270.28, 178.08) * mm]});
            skFitSpline(sketch, "E3134", {"points": [v(-270.28, 178.08) * mm, v(-269.78, 177.8) * mm, v(-269.17, 177.8) * mm, v(-268.68, 178.08) * mm]});
            skFitSpline(sketch, "E3135", {"points": [v(-268.68, 178.08) * mm, v(-268.18, 178.36) * mm, v(-267.88, 178.9) * mm, v(-267.88, 179.46) * mm]});
            skLineSegment(sketch, "E3136", {"start": v(-281.79, 158.81) * mm, "end": v(-271.13, 158.81) * mm});
            skLineSegment(sketch, "E3137", {"start": v(-271.13, 158.81) * mm, "end": v(-271.13, 168.6) * mm});
            skLineSegment(sketch, "E3138", {"start": v(-270.26, 169.46) * mm, "end": v(-268.7, 169.46) * mm});
            skLineSegment(sketch, "E3139", {"start": v(-267.83, 168.6) * mm, "end": v(-267.83, 158.81) * mm});
            skFitSpline(sketch, "E3140", {"points": [v(-38.13, -172.63) * mm, v(-33.05, -171.1) * mm, v(-29.57, -166.43) * mm, v(-29.57, -161.13) * mm]});
            skFitSpline(sketch, "E3141", {"points": [v(-38.7, -157.9) * mm, v(-38.88, -157.9) * mm, v(-39.04, -157.99) * mm, v(-39.13, -158.14) * mm]});
            skFitSpline(sketch, "E3142", {"points": [v(-39.82, -157.46) * mm, v(-40, -157.56) * mm, v(-40.1, -157.77) * mm, v(-40.06, -157.98) * mm]});
            skFitSpline(sketch, "E3143", {"points": [v(-40.06, -157.98) * mm, v(-40.02, -158.19) * mm, v(-39.86, -158.35) * mm, v(-39.65, -158.38) * mm]});
            skFitSpline(sketch, "E3144", {"points": [v(-39.65, -158.38) * mm, v(-39.45, -158.42) * mm, v(-39.24, -158.32) * mm, v(-39.13, -158.14) * mm]});
            skFitSpline(sketch, "E3145", {"points": [v(-39.82, -157.46) * mm, v(-39.66, -157.37) * mm, v(-39.57, -157.2) * mm, v(-39.57, -157.03) * mm]});
            skLineSegment(sketch, "E3146", {"start": v(-270.92, 189.81) * mm, "end": v(-335.74, 173.5) * mm});
            skFitSpline(sketch, "E3147", {"points": [v(-39.57, -155.46) * mm, v(-39.57, -155.28) * mm, v(-39.66, -155.11) * mm, v(-39.82, -155.02) * mm]});
            skFitSpline(sketch, "E3148", {"points": [v(-39.13, -154.34) * mm, v(-39.24, -154.16) * mm, v(-39.45, -154.06) * mm, v(-39.65, -154.1) * mm]});
            skFitSpline(sketch, "E3149", {"points": [v(-39.65, -154.1) * mm, v(-39.86, -154.14) * mm, v(-40.02, -154.3) * mm, v(-40.06, -154.5) * mm]});
            skFitSpline(sketch, "E3150", {"points": [v(-40.06, -154.5) * mm, v(-40.1, -154.71) * mm, v(-40, -154.92) * mm, v(-39.82, -155.02) * mm]});
            skFitSpline(sketch, "E3151", {"points": [v(-39.13, -154.34) * mm, v(-39.04, -154.5) * mm, v(-38.88, -154.6) * mm, v(-38.7, -154.6) * mm]});
            skLineSegment(sketch, "E3152", {"start": v(-299.98, 119.55) * mm, "end": v(-282.65, 155.46) * mm});
            skFitSpline(sketch, "E3153", {"points": [v(-29.57, -124.07) * mm, v(-29.57, -117.44) * mm, v(-34.94, -112.07) * mm, v(-41.57, -112.07) * mm]});
            skLineSegment(sketch, "E3154", {"start": v(-29.57, -161.13) * mm, "end": v(-29.57, -157.9) * mm});
            skLineSegment(sketch, "E3155", {"start": v(-29.57, -157.9) * mm, "end": v(-38.7, -157.9) * mm});
            skFitSpline(sketch, "E3156", {"points": [v(-63.17, -112.07) * mm, v(-67.7, -112.07) * mm, v(-71.85, -114.62) * mm, v(-73.9, -118.67) * mm]});
            skFitSpline(sketch, "E3157", {"points": [v(-54.27, -125.44) * mm, v(-54.27, -123.65) * mm, v(-55.22, -122) * mm, v(-56.77, -121.1) * mm]});
            skFitSpline(sketch, "E3158", {"points": [v(-56.77, -121.1) * mm, v(-58.31, -120.21) * mm, v(-60.22, -120.21) * mm, v(-61.77, -121.1) * mm]});
            skFitSpline(sketch, "E3159", {"points": [v(-61.77, -121.1) * mm, v(-63.31, -122) * mm, v(-64.27, -123.65) * mm, v(-64.27, -125.44) * mm]});
            skFitSpline(sketch, "E3160", {"points": [v(-64.27, -125.44) * mm, v(-64.27, -127.22) * mm, v(-63.31, -128.87) * mm, v(-61.77, -129.77) * mm]});
            skFitSpline(sketch, "E3161", {"points": [v(-61.77, -129.77) * mm, v(-60.22, -130.66) * mm, v(-58.31, -130.66) * mm, v(-56.77, -129.77) * mm]});
            skFitSpline(sketch, "E3162", {"points": [v(-56.77, -129.77) * mm, v(-55.22, -128.87) * mm, v(-54.27, -127.22) * mm, v(-54.27, -125.44) * mm]});
            skLineSegment(sketch, "E3163", {"start": v(-39.57, -157.03) * mm, "end": v(-39.57, -155.46) * mm});
            skFitSpline(sketch, "E3164", {"points": [v(-38.27, -125.44) * mm, v(-38.27, -124.01) * mm, v(-39.03, -122.7) * mm, v(-40.27, -121.98) * mm]});
            skFitSpline(sketch, "E3165", {"points": [v(-40.27, -121.98) * mm, v(-41.5, -121.26) * mm, v(-43.03, -121.26) * mm, v(-44.27, -121.98) * mm]});
            skFitSpline(sketch, "E3166", {"points": [v(-44.27, -121.98) * mm, v(-45.5, -122.7) * mm, v(-46.27, -124.01) * mm, v(-46.27, -125.44) * mm]});
            skFitSpline(sketch, "E3167", {"points": [v(-46.27, -125.44) * mm, v(-46.27, -126.87) * mm, v(-45.5, -128.2) * mm, v(-44.27, -128.9) * mm]});
            skFitSpline(sketch, "E3168", {"points": [v(-44.27, -128.9) * mm, v(-43.03, -129.62) * mm, v(-41.5, -129.62) * mm, v(-40.27, -128.9) * mm]});
            skFitSpline(sketch, "E3169", {"points": [v(-40.27, -128.9) * mm, v(-39.03, -128.2) * mm, v(-38.27, -126.87) * mm, v(-38.27, -125.44) * mm]});
            skLineSegment(sketch, "E3170", {"start": v(-38.7, -154.6) * mm, "end": v(-29.57, -154.6) * mm});
            skLineSegment(sketch, "E3171", {"start": v(-29.57, -154.6) * mm, "end": v(-29.57, -124.07) * mm});
            skFitSpline(sketch, "E3172", {"points": [v(-63.8, -156.24) * mm, v(-63.8, -155.67) * mm, v(-64.1, -155.14) * mm, v(-64.6, -154.86) * mm]});
            skFitSpline(sketch, "E3173", {"points": [v(-64.6, -154.86) * mm, v(-65.09, -154.57) * mm, v(-65.7, -154.57) * mm, v(-66.2, -154.86) * mm]});
            skFitSpline(sketch, "E3174", {"points": [v(-66.2, -154.86) * mm, v(-66.69, -155.14) * mm, v(-67, -155.67) * mm, v(-67, -156.24) * mm]});
            skFitSpline(sketch, "E3175", {"points": [v(-67, -156.24) * mm, v(-67, -156.81) * mm, v(-66.69, -157.34) * mm, v(-66.2, -157.63) * mm]});
            skFitSpline(sketch, "E3176", {"points": [v(-66.2, -157.63) * mm, v(-65.7, -157.91) * mm, v(-65.09, -157.91) * mm, v(-64.6, -157.63) * mm]});
            skFitSpline(sketch, "E3177", {"points": [v(-64.6, -157.63) * mm, v(-64.1, -157.34) * mm, v(-63.8, -156.81) * mm, v(-63.8, -156.24) * mm]});
            skLineSegment(sketch, "E3178", {"start": v(-41.57, -112.07) * mm, "end": v(-63.17, -112.07) * mm});
            skFitSpline(sketch, "E3179", {"points": [v(-117.57, -167.4) * mm, v(-117.57, -169.16) * mm, v(-117.18, -170.89) * mm, v(-116.44, -172.48) * mm]});
            skFitSpline(sketch, "E3180", {"points": [v(-91.21, -157.07) * mm, v(-91.22, -157.25) * mm, v(-91.12, -157.41) * mm, v(-90.97, -157.5) * mm]});
            skFitSpline(sketch, "E3181", {"points": [v(-91.65, -158.19) * mm, v(-91.54, -158.37) * mm, v(-91.34, -158.46) * mm, v(-91.13, -158.43) * mm]});
            skFitSpline(sketch, "E3182", {"points": [v(-91.13, -158.43) * mm, v(-90.92, -158.4) * mm, v(-90.76, -158.23) * mm, v(-90.72, -158.02) * mm]});
            skFitSpline(sketch, "E3183", {"points": [v(-90.72, -158.02) * mm, v(-90.69, -157.82) * mm, v(-90.78, -157.6) * mm, v(-90.97, -157.5) * mm]});
            skFitSpline(sketch, "E3184", {"points": [v(-91.65, -158.19) * mm, v(-91.74, -158.03) * mm, v(-91.9, -157.94) * mm, v(-92.08, -157.94) * mm]});
            skLineSegment(sketch, "E3185", {"start": v(-106.04, -157.94) * mm, "end": v(-117.57, -157.93) * mm});
            skLineSegment(sketch, "E3186", {"start": v(-117.57, -157.93) * mm, "end": v(-117.57, -167.4) * mm});
            skFitSpline(sketch, "E3187", {"points": [v(-102.74, -167.72) * mm, v(-102.74, -167.9) * mm, v(-102.65, -168.06) * mm, v(-102.5, -168.15) * mm]});
            skFitSpline(sketch, "E3188", {"points": [v(-103.17, -168.83) * mm, v(-103.07, -169.02) * mm, v(-102.86, -169.11) * mm, v(-102.65, -169.08) * mm]});
            skFitSpline(sketch, "E3189", {"points": [v(-102.65, -169.08) * mm, v(-102.45, -169.04) * mm, v(-102.29, -168.88) * mm, v(-102.25, -168.67) * mm]});
            skFitSpline(sketch, "E3190", {"points": [v(-102.25, -168.67) * mm, v(-102.21, -168.46) * mm, v(-102.3, -168.26) * mm, v(-102.5, -168.15) * mm]});
            skFitSpline(sketch, "E3191", {"points": [v(-103.17, -168.83) * mm, v(-103.26, -168.68) * mm, v(-103.43, -168.58) * mm, v(-103.6, -168.58) * mm]});
            skLineSegment(sketch, "E3192", {"start": v(-116.44, -172.48) * mm, "end": v(-106.04, -188.94) * mm});
            skLineSegment(sketch, "E3193", {"start": v(-106.04, -188.94) * mm, "end": v(-102.95, -188.94) * mm});
            skFitSpline(sketch, "E3194", {"points": [v(-105.17, -168.58) * mm, v(-105.35, -168.58) * mm, v(-105.52, -168.68) * mm, v(-105.6, -168.83) * mm]});
            skFitSpline(sketch, "E3195", {"points": [v(-106.3, -168.15) * mm, v(-106.47, -168.26) * mm, v(-106.57, -168.46) * mm, v(-106.53, -168.67) * mm]});
            skFitSpline(sketch, "E3196", {"points": [v(-106.53, -168.67) * mm, v(-106.5, -168.88) * mm, v(-106.34, -169.04) * mm, v(-106.13, -169.08) * mm]});
            skFitSpline(sketch, "E3197", {"points": [v(-106.13, -169.08) * mm, v(-105.92, -169.11) * mm, v(-105.71, -169.02) * mm, v(-105.6, -168.83) * mm]});
            skFitSpline(sketch, "E3198", {"points": [v(-106.3, -168.15) * mm, v(-106.14, -168.06) * mm, v(-106.04, -167.9) * mm, v(-106.04, -167.72) * mm]});
            skLineSegment(sketch, "E3199", {"start": v(-91.21, -154.58) * mm, "end": v(-91.21, -157.07) * mm});
            skFitSpline(sketch, "E3200", {"points": [v(-102.8, -178.59) * mm, v(-102.8, -178.01) * mm, v(-103.1, -177.49) * mm, v(-103.6, -177.2) * mm]});
            skFitSpline(sketch, "E3201", {"points": [v(-103.6, -177.2) * mm, v(-104.09, -176.91) * mm, v(-104.7, -176.91) * mm, v(-105.2, -177.2) * mm]});
            skFitSpline(sketch, "E3202", {"points": [v(-105.2, -177.2) * mm, v(-105.69, -177.49) * mm, v(-106, -178.01) * mm, v(-106, -178.59) * mm]});
            skFitSpline(sketch, "E3203", {"points": [v(-106, -178.59) * mm, v(-106, -179.16) * mm, v(-105.69, -179.69) * mm, v(-105.2, -179.97) * mm]});
            skFitSpline(sketch, "E3204", {"points": [v(-105.2, -179.97) * mm, v(-104.7, -180.26) * mm, v(-104.09, -180.26) * mm, v(-103.6, -179.97) * mm]});
            skFitSpline(sketch, "E3205", {"points": [v(-103.6, -179.97) * mm, v(-103.1, -179.69) * mm, v(-102.8, -179.16) * mm, v(-102.8, -178.59) * mm]});
            skLineSegment(sketch, "E3206", {"start": v(-92.08, -157.94) * mm, "end": v(-102.74, -157.94) * mm});
            skLineSegment(sketch, "E3207", {"start": v(-102.74, -157.94) * mm, "end": v(-102.74, -167.72) * mm});
            skLineSegment(sketch, "E3208", {"start": v(-103.6, -168.58) * mm, "end": v(-105.18, -168.58) * mm});
            skLineSegment(sketch, "E3209", {"start": v(-106.04, -167.72) * mm, "end": v(-106.04, -157.94) * mm});
            skFitSpline(sketch, "E3210", {"points": [v(169.87, -25.87) * mm, v(170.07, -25.67) * mm, v(170.17, -25.41) * mm, v(170.17, -25.14) * mm]});
            skFitSpline(sketch, "E3211", {"points": [v(170.15, 23.5) * mm, v(170.15, 23.75) * mm, v(170.04, 24) * mm, v(169.86, 24.18) * mm]});
            skLineSegment(sketch, "E3212", {"start": v(-102.95, -188.94) * mm, "end": v(-38.13, -172.63) * mm});
            skLineSegment(sketch, "E3213", {"start": v(-73.9, -118.67) * mm, "end": v(-91.21, -154.58) * mm});
            skFitSpline(sketch, "E3214", {"points": [v(162.25, -33.14) * mm, v(162.42, -33.19) * mm, v(162.6, -33.14) * mm, v(162.73, -33.01) * mm]});
            skFitSpline(sketch, "E3215", {"points": [v(162.25, -33.14) * mm, v(162.04, -33.09) * mm, v(161.83, -33.17) * mm, v(161.7, -33.34) * mm]});
            skFitSpline(sketch, "E3216", {"points": [v(161.7, -33.34) * mm, v(161.59, -33.51) * mm, v(161.59, -33.74) * mm, v(161.7, -33.91) * mm]});
            skFitSpline(sketch, "E3217", {"points": [v(161.7, -33.91) * mm, v(161.83, -34.09) * mm, v(162.04, -34.16) * mm, v(162.25, -34.1) * mm]});
            skFitSpline(sketch, "E3218", {"points": [v(162.73, -34.24) * mm, v(162.6, -34.11) * mm, v(162.42, -34.06) * mm, v(162.25, -34.1) * mm]});
            skLineSegment(sketch, "E3219", {"start": v(170.15, 23.5) * mm, "end": v(170.17, -25.14) * mm});
            skFitSpline(sketch, "E3220", {"points": [v(163.88, -36.1) * mm, v(163.98, -36) * mm, v(164.03, -35.88) * mm, v(164.03, -35.75) * mm]});
            skFitSpline(sketch, "E3221", {"points": [v(164.03, -35.75) * mm, v(164.03, -35.61) * mm, v(163.98, -35.49) * mm, v(163.88, -35.4) * mm]});
            skLineSegment(sketch, "E3222", {"start": v(133.37, 51.7) * mm, "end": v(133.4, -53.36) * mm});
            skFitSpline(sketch, "E3223", {"points": [v(159.64, -39.64) * mm, v(159.74, -39.73) * mm, v(159.86, -39.78) * mm, v(160, -39.78) * mm]});
            skFitSpline(sketch, "E3224", {"points": [v(160, -39.78) * mm, v(160.13, -39.78) * mm, v(160.26, -39.73) * mm, v(160.35, -39.64) * mm]});
            skLineSegment(sketch, "E3225", {"start": v(169.87, -25.87) * mm, "end": v(162.73, -33.01) * mm});
            skFitSpline(sketch, "E3226", {"points": [v(158.36, -38) * mm, v(158.31, -38.17) * mm, v(158.36, -38.35) * mm, v(158.49, -38.48) * mm]});
            skFitSpline(sketch, "E3227", {"points": [v(158.36, -38) * mm, v(158.41, -37.8) * mm, v(158.33, -37.58) * mm, v(158.16, -37.46) * mm]});
            skFitSpline(sketch, "E3228", {"points": [v(158.16, -37.46) * mm, v(157.99, -37.34) * mm, v(157.76, -37.34) * mm, v(157.59, -37.46) * mm]});
            skFitSpline(sketch, "E3229", {"points": [v(157.59, -37.46) * mm, v(157.41, -37.58) * mm, v(157.34, -37.8) * mm, v(157.4, -38) * mm]});
            skFitSpline(sketch, "E3230", {"points": [v(157.26, -38.48) * mm, v(157.39, -38.35) * mm, v(157.44, -38.17) * mm, v(157.4, -38) * mm]});
            skLineSegment(sketch, "E3231", {"start": v(162.73, -34.24) * mm, "end": v(163.88, -35.4) * mm});
            skLineSegment(sketch, "E3232", {"start": v(163.88, -36.1) * mm, "end": v(160.35, -39.64) * mm});
            skFitSpline(sketch, "E3233", {"points": [v(147.26, -48.13) * mm, v(147.43, -48.18) * mm, v(147.61, -48.13) * mm, v(147.74, -48) * mm]});
            skFitSpline(sketch, "E3234", {"points": [v(147.26, -48.13) * mm, v(147.05, -48.08) * mm, v(146.84, -48.16) * mm, v(146.72, -48.33) * mm]});
            skFitSpline(sketch, "E3235", {"points": [v(146.72, -48.33) * mm, v(146.6, -48.5) * mm, v(146.6, -48.73) * mm, v(146.72, -48.9) * mm]});
            skFitSpline(sketch, "E3236", {"points": [v(146.72, -48.9) * mm, v(146.84, -49.08) * mm, v(147.05, -49.15) * mm, v(147.26, -49.1) * mm]});
            skFitSpline(sketch, "E3237", {"points": [v(147.74, -49.23) * mm, v(147.61, -49.1) * mm, v(147.43, -49.05) * mm, v(147.26, -49.1) * mm]});
            skLineSegment(sketch, "E3238", {"start": v(159.64, -39.64) * mm, "end": v(158.49, -38.48) * mm});
            skFitSpline(sketch, "E3239", {"points": [v(148.9, -51.1) * mm, v(149.09, -50.9) * mm, v(149.09, -50.58) * mm, v(148.9, -50.38) * mm]});
            skLineSegment(sketch, "E3240", {"start": v(157.26, -38.48) * mm, "end": v(153.63, -42.11) * mm});
            skLineSegment(sketch, "E3241", {"start": v(153.63, -42.11) * mm, "end": v(151.51, -40) * mm});
            skLineSegment(sketch, "E3242", {"start": v(151.51, -40) * mm, "end": v(152.41, -39.09) * mm});
            skFitSpline(sketch, "E3243", {"points": [v(144.65, -54.63) * mm, v(144.75, -54.72) * mm, v(144.87, -54.77) * mm, v(145, -54.77) * mm]});
            skFitSpline(sketch, "E3244", {"points": [v(145, -54.77) * mm, v(145.14, -54.77) * mm, v(145.26, -54.72) * mm, v(145.36, -54.63) * mm]});
            skLineSegment(sketch, "E3245", {"start": v(148.35, -43.15) * mm, "end": v(149.25, -42.25) * mm});
            skLineSegment(sketch, "E3246", {"start": v(149.25, -42.25) * mm, "end": v(151.37, -44.37) * mm});
            skLineSegment(sketch, "E3247", {"start": v(151.37, -44.37) * mm, "end": v(147.74, -48) * mm});
            skFitSpline(sketch, "E3248", {"points": [v(143.37, -52.99) * mm, v(143.32, -53.16) * mm, v(143.37, -53.35) * mm, v(143.5, -53.47) * mm]});
            skFitSpline(sketch, "E3249", {"points": [v(143.37, -52.99) * mm, v(143.42, -52.79) * mm, v(143.34, -52.57) * mm, v(143.17, -52.45) * mm]});
            skFitSpline(sketch, "E3250", {"points": [v(143.17, -52.45) * mm, v(143, -52.33) * mm, v(142.77, -52.33) * mm, v(142.6, -52.45) * mm]});
            skFitSpline(sketch, "E3251", {"points": [v(142.6, -52.45) * mm, v(142.42, -52.57) * mm, v(142.35, -52.79) * mm, v(142.4, -52.99) * mm]});
            skFitSpline(sketch, "E3252", {"points": [v(142.27, -53.47) * mm, v(142.4, -53.35) * mm, v(142.45, -53.16) * mm, v(142.4, -52.99) * mm]});
            skLineSegment(sketch, "E3253", {"start": v(147.74, -49.23) * mm, "end": v(148.9, -50.38) * mm});
            skLineSegment(sketch, "E3254", {"start": v(148.9, -51.1) * mm, "end": v(145.36, -54.63) * mm});
            skFitSpline(sketch, "E3255", {"points": [v(133.4, -53.36) * mm, v(133.4, -55.49) * mm, v(134.25, -57.52) * mm, v(135.75, -59.02) * mm]});
            skFitSpline(sketch, "E3256", {"points": [v(135.72, 57.35) * mm, v(134.22, 55.85) * mm, v(133.37, 53.82) * mm, v(133.37, 51.7) * mm]});
            skLineSegment(sketch, "E3257", {"start": v(144.65, -54.63) * mm, "end": v(143.5, -53.47) * mm});
            skFitSpline(sketch, "E3258", {"points": [v(142.37, 51.32) * mm, v(142.41, 51.5) * mm, v(142.36, 51.68) * mm, v(142.24, 51.8) * mm]});
            skFitSpline(sketch, "E3259", {"points": [v(142.37, 51.32) * mm, v(142.31, 51.12) * mm, v(142.39, 50.9) * mm, v(142.56, 50.78) * mm]});
            skFitSpline(sketch, "E3260", {"points": [v(142.56, 50.78) * mm, v(142.73, 50.66) * mm, v(142.96, 50.66) * mm, v(143.13, 50.78) * mm]});
            skFitSpline(sketch, "E3261", {"points": [v(143.13, 50.78) * mm, v(143.3, 50.9) * mm, v(143.39, 51.12) * mm, v(143.33, 51.32) * mm]});
            skFitSpline(sketch, "E3262", {"points": [v(143.46, 51.8) * mm, v(143.33, 51.68) * mm, v(143.28, 51.5) * mm, v(143.33, 51.32) * mm]});
            skLineSegment(sketch, "E3263", {"start": v(142.27, -53.47) * mm, "end": v(136.24, -59.5) * mm});
            skLineSegment(sketch, "E3264", {"start": v(136.24, -59.5) * mm, "end": v(135.75, -59.02) * mm});
            skFitSpline(sketch, "E3265", {"points": [v(145.32, 52.96) * mm, v(145.23, 53.05) * mm, v(145.1, 53.1) * mm, v(144.97, 53.1) * mm]});
            skFitSpline(sketch, "E3266", {"points": [v(144.97, 53.1) * mm, v(144.84, 53.1) * mm, v(144.7, 53.05) * mm, v(144.62, 52.96) * mm]});
            skLineSegment(sketch, "E3267", {"start": v(152.41, -39.09) * mm, "end": v(149.58, -36.26) * mm});
            skLineSegment(sketch, "E3268", {"start": v(149.58, -36.26) * mm, "end": v(148.68, -37.16) * mm});
            skLineSegment(sketch, "E3269", {"start": v(148.68, -37.16) * mm, "end": v(146.56, -35.04) * mm});
            skLineSegment(sketch, "E3270", {"start": v(146.56, -35.04) * mm, "end": v(144.3, -37.3) * mm});
            skLineSegment(sketch, "E3271", {"start": v(144.3, -37.3) * mm, "end": v(146.42, -39.42) * mm});
            skLineSegment(sketch, "E3272", {"start": v(146.42, -39.42) * mm, "end": v(145.52, -40.33) * mm});
            skLineSegment(sketch, "E3273", {"start": v(145.52, -40.33) * mm, "end": v(148.35, -43.15) * mm});
            skFitSpline(sketch, "E3274", {"points": [v(148.86, 48.72) * mm, v(148.95, 48.8) * mm, v(149, 48.94) * mm, v(149, 49.07) * mm]});
            skFitSpline(sketch, "E3275", {"points": [v(149, 49.07) * mm, v(149, 49.2) * mm, v(148.95, 49.33) * mm, v(148.86, 49.42) * mm]});
            skLineSegment(sketch, "E3276", {"start": v(135.72, 57.35) * mm, "end": v(136.2, 57.84) * mm});
            skLineSegment(sketch, "E3277", {"start": v(136.2, 57.84) * mm, "end": v(142.24, 51.8) * mm});
            skFitSpline(sketch, "E3278", {"points": [v(147.22, 47.43) * mm, v(147.4, 47.38) * mm, v(147.58, 47.43) * mm, v(147.7, 47.56) * mm]});
            skFitSpline(sketch, "E3279", {"points": [v(147.22, 47.43) * mm, v(147.02, 47.49) * mm, v(146.8, 47.4) * mm, v(146.68, 47.23) * mm]});
            skFitSpline(sketch, "E3280", {"points": [v(146.68, 47.23) * mm, v(146.56, 47.06) * mm, v(146.56, 46.83) * mm, v(146.68, 46.66) * mm]});
            skFitSpline(sketch, "E3281", {"points": [v(146.68, 46.66) * mm, v(146.8, 46.49) * mm, v(147.02, 46.41) * mm, v(147.22, 46.46) * mm]});
            skFitSpline(sketch, "E3282", {"points": [v(147.7, 46.34) * mm, v(147.58, 46.46) * mm, v(147.4, 46.51) * mm, v(147.22, 46.46) * mm]});
            skLineSegment(sketch, "E3283", {"start": v(143.46, 51.8) * mm, "end": v(144.62, 52.96) * mm});
            skFitSpline(sketch, "E3284", {"points": [v(157.36, 36.33) * mm, v(157.4, 36.5) * mm, v(157.35, 36.69) * mm, v(157.23, 36.81) * mm]});
            skFitSpline(sketch, "E3285", {"points": [v(157.36, 36.33) * mm, v(157.3, 36.13) * mm, v(157.38, 35.91) * mm, v(157.55, 35.8) * mm]});
            skFitSpline(sketch, "E3286", {"points": [v(157.55, 35.8) * mm, v(157.72, 35.67) * mm, v(157.95, 35.67) * mm, v(158.13, 35.8) * mm]});
            skFitSpline(sketch, "E3287", {"points": [v(158.13, 35.8) * mm, v(158.3, 35.91) * mm, v(158.38, 36.13) * mm, v(158.32, 36.33) * mm]});
            skFitSpline(sketch, "E3288", {"points": [v(158.45, 36.81) * mm, v(158.32, 36.69) * mm, v(158.28, 36.5) * mm, v(158.32, 36.33) * mm]});
            skLineSegment(sketch, "E3289", {"start": v(145.32, 52.96) * mm, "end": v(148.86, 49.42) * mm});
            skFitSpline(sketch, "E3290", {"points": [v(160.31, 37.97) * mm, v(160.22, 38.06) * mm, v(160.1, 38.11) * mm, v(159.96, 38.11) * mm]});
            skFitSpline(sketch, "E3291", {"points": [v(159.96, 38.11) * mm, v(159.83, 38.11) * mm, v(159.7, 38.06) * mm, v(159.6, 37.97) * mm]});
            skLineSegment(sketch, "E3292", {"start": v(148.86, 48.72) * mm, "end": v(147.7, 47.56) * mm});
            skFitSpline(sketch, "E3293", {"points": [v(163.85, 33.73) * mm, v(163.94, 33.82) * mm, v(164, 33.95) * mm, v(164, 34.08) * mm]});
            skFitSpline(sketch, "E3294", {"points": [v(164, 34.08) * mm, v(164, 34.21) * mm, v(163.94, 34.34) * mm, v(163.85, 34.43) * mm]});
            skLineSegment(sketch, "E3295", {"start": v(147.7, 46.34) * mm, "end": v(151.33, 42.7) * mm});
            skLineSegment(sketch, "E3296", {"start": v(151.33, 42.7) * mm, "end": v(149.21, 40.58) * mm});
            skLineSegment(sketch, "E3297", {"start": v(149.21, 40.58) * mm, "end": v(148.31, 41.49) * mm});
            skLineSegment(sketch, "E3298", {"start": v(148.31, 41.49) * mm, "end": v(145.48, 38.66) * mm});
            skLineSegment(sketch, "E3299", {"start": v(145.48, 38.66) * mm, "end": v(146.38, 37.76) * mm});
            skLineSegment(sketch, "E3300", {"start": v(146.38, 37.76) * mm, "end": v(144.26, 35.63) * mm});
            skLineSegment(sketch, "E3301", {"start": v(144.26, 35.63) * mm, "end": v(146.52, 33.37) * mm});
            skLineSegment(sketch, "E3302", {"start": v(146.52, 33.37) * mm, "end": v(148.65, 35.5) * mm});
            skLineSegment(sketch, "E3303", {"start": v(148.65, 35.5) * mm, "end": v(149.55, 34.6) * mm});
            skLineSegment(sketch, "E3304", {"start": v(149.55, 34.6) * mm, "end": v(152.38, 37.42) * mm});
            skLineSegment(sketch, "E3305", {"start": v(152.38, 37.42) * mm, "end": v(151.47, 38.32) * mm});
            skLineSegment(sketch, "E3306", {"start": v(151.47, 38.32) * mm, "end": v(153.6, 40.44) * mm});
            skLineSegment(sketch, "E3307", {"start": v(153.6, 40.44) * mm, "end": v(157.23, 36.81) * mm});
            skFitSpline(sketch, "E3308", {"points": [v(162.21, 32.44) * mm, v(162.38, 32.4) * mm, v(162.57, 32.44) * mm, v(162.7, 32.57) * mm]});
            skFitSpline(sketch, "E3309", {"points": [v(162.21, 32.44) * mm, v(162, 32.5) * mm, v(161.8, 32.42) * mm, v(161.67, 32.24) * mm]});
            skFitSpline(sketch, "E3310", {"points": [v(161.67, 32.24) * mm, v(161.55, 32.07) * mm, v(161.55, 31.84) * mm, v(161.67, 31.67) * mm]});
            skFitSpline(sketch, "E3311", {"points": [v(161.67, 31.67) * mm, v(161.8, 31.5) * mm, v(162, 31.42) * mm, v(162.21, 31.47) * mm]});
            skFitSpline(sketch, "E3312", {"points": [v(162.7, 31.35) * mm, v(162.57, 31.47) * mm, v(162.38, 31.52) * mm, v(162.21, 31.47) * mm]});
            skLineSegment(sketch, "E3313", {"start": v(158.45, 36.81) * mm, "end": v(159.6, 37.97) * mm});
            skFitSpline(sketch, "E3314", {"points": [v(239.45, 23.58) * mm, v(239.25, 23.38) * mm, v(239.15, 23.12) * mm, v(239.15, 22.85) * mm]});
            skFitSpline(sketch, "E3315", {"points": [v(239.17, -25.79) * mm, v(239.17, -26.04) * mm, v(239.28, -26.29) * mm, v(239.46, -26.47) * mm]});
            skLineSegment(sketch, "E3316", {"start": v(160.31, 37.97) * mm, "end": v(163.85, 34.43) * mm});
            skLineSegment(sketch, "E3317", {"start": v(163.85, 33.73) * mm, "end": v(162.7, 32.57) * mm});
            skLineSegment(sketch, "E3318", {"start": v(162.7, 31.35) * mm, "end": v(169.86, 24.18) * mm});
            skFitSpline(sketch, "E3319", {"points": [v(247.07, 30.85) * mm, v(246.9, 30.9) * mm, v(246.72, 30.85) * mm, v(246.6, 30.72) * mm]});
            skFitSpline(sketch, "E3320", {"points": [v(247.07, 30.85) * mm, v(247.28, 30.8) * mm, v(247.5, 30.88) * mm, v(247.61, 31.05) * mm]});
            skFitSpline(sketch, "E3321", {"points": [v(247.61, 31.05) * mm, v(247.73, 31.22) * mm, v(247.73, 31.45) * mm, v(247.61, 31.62) * mm]});
            skFitSpline(sketch, "E3322", {"points": [v(247.61, 31.62) * mm, v(247.5, 31.8) * mm, v(247.28, 31.87) * mm, v(247.07, 31.82) * mm]});
            skFitSpline(sketch, "E3323", {"points": [v(246.6, 31.95) * mm, v(246.72, 31.82) * mm, v(246.9, 31.77) * mm, v(247.07, 31.82) * mm]});
            skLineSegment(sketch, "E3324", {"start": v(239.17, -25.79) * mm, "end": v(239.15, 22.85) * mm});
            skFitSpline(sketch, "E3325", {"points": [v(245.44, 33.8) * mm, v(245.34, 33.72) * mm, v(245.29, 33.59) * mm, v(245.29, 33.46) * mm]});
            skFitSpline(sketch, "E3326", {"points": [v(245.29, 33.46) * mm, v(245.29, 33.32) * mm, v(245.34, 33.2) * mm, v(245.44, 33.1) * mm]});
            skLineSegment(sketch, "E3327", {"start": v(275.95, -53.99) * mm, "end": v(275.91, 51.07) * mm});
            skFitSpline(sketch, "E3328", {"points": [v(249.68, 37.34) * mm, v(249.58, 37.44) * mm, v(249.46, 37.5) * mm, v(249.33, 37.5) * mm]});
            skFitSpline(sketch, "E3329", {"points": [v(249.33, 37.5) * mm, v(249.2, 37.5) * mm, v(249.07, 37.44) * mm, v(248.97, 37.34) * mm]});
            skLineSegment(sketch, "E3330", {"start": v(239.45, 23.58) * mm, "end": v(246.6, 30.72) * mm});
            skFitSpline(sketch, "E3331", {"points": [v(250.96, 35.7) * mm, v(251, 35.88) * mm, v(250.96, 36.06) * mm, v(250.83, 36.19) * mm]});
            skFitSpline(sketch, "E3332", {"points": [v(250.96, 35.7) * mm, v(250.9, 35.5) * mm, v(250.99, 35.29) * mm, v(251.16, 35.17) * mm]});
            skFitSpline(sketch, "E3333", {"points": [v(251.16, 35.17) * mm, v(251.33, 35.05) * mm, v(251.56, 35.05) * mm, v(251.73, 35.17) * mm]});
            skFitSpline(sketch, "E3334", {"points": [v(251.73, 35.17) * mm, v(251.9, 35.29) * mm, v(251.98, 35.5) * mm, v(251.93, 35.7) * mm]});
            skFitSpline(sketch, "E3335", {"points": [v(252.06, 36.19) * mm, v(251.93, 36.06) * mm, v(251.88, 35.88) * mm, v(251.93, 35.7) * mm]});
            skLineSegment(sketch, "E3336", {"start": v(246.6, 31.95) * mm, "end": v(245.44, 33.1) * mm});
            skLineSegment(sketch, "E3337", {"start": v(245.44, 33.8) * mm, "end": v(248.97, 37.34) * mm});
            skFitSpline(sketch, "E3338", {"points": [v(262.07, 45.84) * mm, v(261.9, 45.89) * mm, v(261.7, 45.84) * mm, v(261.58, 45.71) * mm]});
            skFitSpline(sketch, "E3339", {"points": [v(262.07, 45.84) * mm, v(262.27, 45.79) * mm, v(262.48, 45.87) * mm, v(262.6, 46.04) * mm]});
            skFitSpline(sketch, "E3340", {"points": [v(262.6, 46.04) * mm, v(262.72, 46.21) * mm, v(262.72, 46.44) * mm, v(262.6, 46.61) * mm]});
            skFitSpline(sketch, "E3341", {"points": [v(262.6, 46.61) * mm, v(262.48, 46.78) * mm, v(262.27, 46.86) * mm, v(262.07, 46.8) * mm]});
            skFitSpline(sketch, "E3342", {"points": [v(261.58, 46.94) * mm, v(261.7, 46.81) * mm, v(261.9, 46.76) * mm, v(262.07, 46.8) * mm]});
            skLineSegment(sketch, "E3343", {"start": v(249.68, 37.34) * mm, "end": v(250.83, 36.19) * mm});
            skFitSpline(sketch, "E3344", {"points": [v(260.43, 48.8) * mm, v(260.33, 48.7) * mm, v(260.28, 48.58) * mm, v(260.28, 48.45) * mm]});
            skFitSpline(sketch, "E3345", {"points": [v(260.28, 48.45) * mm, v(260.28, 48.31) * mm, v(260.33, 48.19) * mm, v(260.43, 48.1) * mm]});
            skLineSegment(sketch, "E3346", {"start": v(252.06, 36.19) * mm, "end": v(255.69, 39.82) * mm});
            skLineSegment(sketch, "E3347", {"start": v(255.69, 39.82) * mm, "end": v(257.81, 37.7) * mm});
            skLineSegment(sketch, "E3348", {"start": v(257.81, 37.7) * mm, "end": v(256.9, 36.8) * mm});
            skFitSpline(sketch, "E3349", {"points": [v(264.67, 52.34) * mm, v(264.58, 52.43) * mm, v(264.45, 52.48) * mm, v(264.32, 52.48) * mm]});
            skFitSpline(sketch, "E3350", {"points": [v(264.32, 52.48) * mm, v(264.18, 52.48) * mm, v(264.06, 52.43) * mm, v(263.96, 52.34) * mm]});
            skLineSegment(sketch, "E3351", {"start": v(260.97, 40.86) * mm, "end": v(260.07, 39.96) * mm});
            skLineSegment(sketch, "E3352", {"start": v(260.07, 39.96) * mm, "end": v(257.95, 42.08) * mm});
            skLineSegment(sketch, "E3353", {"start": v(257.95, 42.08) * mm, "end": v(261.58, 45.71) * mm});
            skFitSpline(sketch, "E3354", {"points": [v(265.95, 50.7) * mm, v(266, 50.87) * mm, v(265.95, 51.05) * mm, v(265.82, 51.18) * mm]});
            skFitSpline(sketch, "E3355", {"points": [v(265.95, 50.7) * mm, v(265.9, 50.5) * mm, v(265.98, 50.28) * mm, v(266.15, 50.16) * mm]});
            skFitSpline(sketch, "E3356", {"points": [v(266.15, 50.16) * mm, v(266.32, 50.04) * mm, v(266.55, 50.04) * mm, v(266.72, 50.16) * mm]});
            skFitSpline(sketch, "E3357", {"points": [v(266.72, 50.16) * mm, v(266.9, 50.28) * mm, v(266.97, 50.5) * mm, v(266.92, 50.7) * mm]});
            skFitSpline(sketch, "E3358", {"points": [v(267.05, 51.18) * mm, v(266.92, 51.05) * mm, v(266.87, 50.87) * mm, v(266.92, 50.7) * mm]});
            skLineSegment(sketch, "E3359", {"start": v(261.58, 46.94) * mm, "end": v(260.43, 48.1) * mm});
            skLineSegment(sketch, "E3360", {"start": v(260.43, 48.8) * mm, "end": v(263.96, 52.34) * mm});
            skFitSpline(sketch, "E3361", {"points": [v(275.91, 51.07) * mm, v(275.91, 53.2) * mm, v(275.07, 55.23) * mm, v(273.57, 56.73) * mm]});
            skFitSpline(sketch, "E3362", {"points": [v(273.6, -59.64) * mm, v(275.1, -58.14) * mm, v(275.95, -56.1) * mm, v(275.95, -53.99) * mm]});
            skLineSegment(sketch, "E3363", {"start": v(264.67, 52.34) * mm, "end": v(265.82, 51.18) * mm});
            skFitSpline(sketch, "E3364", {"points": [v(266.96, -53.61) * mm, v(266.9, -53.78) * mm, v(266.96, -53.97) * mm, v(267.08, -54.1) * mm]});
            skFitSpline(sketch, "E3365", {"points": [v(266.96, -53.61) * mm, v(267, -53.4) * mm, v(266.93, -53.2) * mm, v(266.76, -53.07) * mm]});
            skFitSpline(sketch, "E3366", {"points": [v(266.76, -53.07) * mm, v(266.59, -52.95) * mm, v(266.36, -52.95) * mm, v(266.19, -53.07) * mm]});
            skFitSpline(sketch, "E3367", {"points": [v(266.19, -53.07) * mm, v(266.01, -53.2) * mm, v(265.94, -53.4) * mm, v(265.99, -53.61) * mm]});
            skFitSpline(sketch, "E3368", {"points": [v(265.86, -54.1) * mm, v(265.99, -53.97) * mm, v(266.04, -53.78) * mm, v(265.99, -53.61) * mm]});
            skLineSegment(sketch, "E3369", {"start": v(267.05, 51.18) * mm, "end": v(273.08, 57.21) * mm});
            skLineSegment(sketch, "E3370", {"start": v(273.08, 57.21) * mm, "end": v(273.57, 56.73) * mm});
            skFitSpline(sketch, "E3371", {"points": [v(264, -55.25) * mm, v(264.1, -55.34) * mm, v(264.22, -55.4) * mm, v(264.35, -55.4) * mm]});
            skFitSpline(sketch, "E3372", {"points": [v(264.35, -55.4) * mm, v(264.48, -55.4) * mm, v(264.61, -55.34) * mm, v(264.7, -55.25) * mm]});
            skLineSegment(sketch, "E3373", {"start": v(256.9, 36.8) * mm, "end": v(259.74, 33.97) * mm});
            skLineSegment(sketch, "E3374", {"start": v(259.74, 33.97) * mm, "end": v(260.64, 34.87) * mm});
            skLineSegment(sketch, "E3375", {"start": v(260.64, 34.87) * mm, "end": v(262.76, 32.75) * mm});
            skLineSegment(sketch, "E3376", {"start": v(262.76, 32.75) * mm, "end": v(265.02, 35.01) * mm});
            skLineSegment(sketch, "E3377", {"start": v(265.02, 35.01) * mm, "end": v(262.9, 37.13) * mm});
            skLineSegment(sketch, "E3378", {"start": v(262.9, 37.13) * mm, "end": v(263.8, 38.03) * mm});
            skLineSegment(sketch, "E3379", {"start": v(263.8, 38.03) * mm, "end": v(260.97, 40.86) * mm});
            skFitSpline(sketch, "E3380", {"points": [v(260.46, -51) * mm, v(260.37, -51.1) * mm, v(260.32, -51.23) * mm, v(260.32, -51.36) * mm]});
            skFitSpline(sketch, "E3381", {"points": [v(260.32, -51.36) * mm, v(260.32, -51.5) * mm, v(260.37, -51.62) * mm, v(260.46, -51.71) * mm]});
            skLineSegment(sketch, "E3382", {"start": v(273.6, -59.64) * mm, "end": v(273.12, -60.13) * mm});
            skLineSegment(sketch, "E3383", {"start": v(273.12, -60.13) * mm, "end": v(267.08, -54.1) * mm});
            skFitSpline(sketch, "E3384", {"points": [v(262.1, -49.72) * mm, v(261.93, -49.68) * mm, v(261.74, -49.73) * mm, v(261.62, -49.85) * mm]});
            skFitSpline(sketch, "E3385", {"points": [v(262.1, -49.72) * mm, v(262.3, -49.78) * mm, v(262.52, -49.7) * mm, v(262.64, -49.53) * mm]});
            skFitSpline(sketch, "E3386", {"points": [v(262.64, -49.53) * mm, v(262.76, -49.35) * mm, v(262.76, -49.12) * mm, v(262.64, -48.95) * mm]});
            skFitSpline(sketch, "E3387", {"points": [v(262.64, -48.95) * mm, v(262.52, -48.78) * mm, v(262.3, -48.7) * mm, v(262.1, -48.76) * mm]});
            skFitSpline(sketch, "E3388", {"points": [v(261.62, -48.63) * mm, v(261.74, -48.75) * mm, v(261.93, -48.8) * mm, v(262.1, -48.76) * mm]});
            skLineSegment(sketch, "E3389", {"start": v(265.86, -54.1) * mm, "end": v(264.7, -55.25) * mm});
            skFitSpline(sketch, "E3390", {"points": [v(251.96, -38.62) * mm, v(251.92, -38.8) * mm, v(251.97, -38.98) * mm, v(252.1, -39.1) * mm]});
            skFitSpline(sketch, "E3391", {"points": [v(251.96, -38.62) * mm, v(252.02, -38.42) * mm, v(251.94, -38.2) * mm, v(251.77, -38.08) * mm]});
            skFitSpline(sketch, "E3392", {"points": [v(251.77, -38.08) * mm, v(251.6, -37.96) * mm, v(251.37, -37.96) * mm, v(251.2, -38.08) * mm]});
            skFitSpline(sketch, "E3393", {"points": [v(251.2, -38.08) * mm, v(251.02, -38.2) * mm, v(250.94, -38.42) * mm, v(251, -38.62) * mm]});
            skFitSpline(sketch, "E3394", {"points": [v(250.87, -39.1) * mm, v(251, -38.98) * mm, v(251.05, -38.8) * mm, v(251, -38.62) * mm]});
            skLineSegment(sketch, "E3395", {"start": v(264, -55.25) * mm, "end": v(260.46, -51.71) * mm});
            skFitSpline(sketch, "E3396", {"points": [v(249, -40.26) * mm, v(249.1, -40.35) * mm, v(249.23, -40.4) * mm, v(249.36, -40.4) * mm]});
            skFitSpline(sketch, "E3397", {"points": [v(249.36, -40.4) * mm, v(249.5, -40.4) * mm, v(249.62, -40.35) * mm, v(249.71, -40.26) * mm]});
            skLineSegment(sketch, "E3398", {"start": v(260.46, -51) * mm, "end": v(261.62, -49.85) * mm});
            skFitSpline(sketch, "E3399", {"points": [v(245.47, -36.02) * mm, v(245.28, -36.21) * mm, v(245.28, -36.53) * mm, v(245.47, -36.72) * mm]});
            skLineSegment(sketch, "E3400", {"start": v(261.62, -48.63) * mm, "end": v(257.99, -45) * mm});
            skLineSegment(sketch, "E3401", {"start": v(257.99, -45) * mm, "end": v(260.1, -42.88) * mm});
            skLineSegment(sketch, "E3402", {"start": v(260.1, -42.88) * mm, "end": v(261.01, -43.78) * mm});
            skLineSegment(sketch, "E3403", {"start": v(261.01, -43.78) * mm, "end": v(263.84, -40.95) * mm});
            skLineSegment(sketch, "E3404", {"start": v(263.84, -40.95) * mm, "end": v(262.94, -40.05) * mm});
            skLineSegment(sketch, "E3405", {"start": v(262.94, -40.05) * mm, "end": v(265.06, -37.93) * mm});
            skLineSegment(sketch, "E3406", {"start": v(265.06, -37.93) * mm, "end": v(262.8, -35.66) * mm});
            skLineSegment(sketch, "E3407", {"start": v(262.8, -35.66) * mm, "end": v(260.67, -37.78) * mm});
            skLineSegment(sketch, "E3408", {"start": v(260.67, -37.78) * mm, "end": v(259.77, -36.88) * mm});
            skLineSegment(sketch, "E3409", {"start": v(259.77, -36.88) * mm, "end": v(256.94, -39.71) * mm});
            skLineSegment(sketch, "E3410", {"start": v(256.94, -39.71) * mm, "end": v(257.85, -40.61) * mm});
            skLineSegment(sketch, "E3411", {"start": v(257.85, -40.61) * mm, "end": v(255.72, -42.73) * mm});
            skLineSegment(sketch, "E3412", {"start": v(255.72, -42.73) * mm, "end": v(252.1, -39.1) * mm});
            skFitSpline(sketch, "E3413", {"points": [v(247.1, -34.73) * mm, v(246.94, -34.69) * mm, v(246.75, -34.74) * mm, v(246.63, -34.86) * mm]});
            skFitSpline(sketch, "E3414", {"points": [v(247.1, -34.73) * mm, v(247.31, -34.79) * mm, v(247.53, -34.7) * mm, v(247.65, -34.54) * mm]});
            skFitSpline(sketch, "E3415", {"points": [v(247.65, -34.54) * mm, v(247.77, -34.36) * mm, v(247.77, -34.13) * mm, v(247.65, -33.96) * mm]});
            skFitSpline(sketch, "E3416", {"points": [v(247.65, -33.96) * mm, v(247.53, -33.8) * mm, v(247.31, -33.71) * mm, v(247.1, -33.77) * mm]});
            skFitSpline(sketch, "E3417", {"points": [v(246.63, -33.64) * mm, v(246.75, -33.76) * mm, v(246.94, -33.81) * mm, v(247.1, -33.77) * mm]});
            skLineSegment(sketch, "E3418", {"start": v(250.87, -39.1) * mm, "end": v(249.71, -40.26) * mm});
            skLineSegment(sketch, "E3419", {"start": v(249, -40.26) * mm, "end": v(245.47, -36.72) * mm});
            skFitSpline(sketch, "E3420", {"points": [v(-134.18, -154.84) * mm, v(-134.18, -154.67) * mm, v(-134.27, -154.5) * mm, v(-134.43, -154.41) * mm]});
            skFitSpline(sketch, "E3421", {"points": [v(-133.74, -153.73) * mm, v(-133.85, -153.55) * mm, v(-134.06, -153.45) * mm, v(-134.26, -153.49) * mm]});
            skFitSpline(sketch, "E3422", {"points": [v(-134.26, -153.49) * mm, v(-134.47, -153.52) * mm, v(-134.63, -153.68) * mm, v(-134.67, -153.9) * mm]});
            skFitSpline(sketch, "E3423", {"points": [v(-134.67, -153.9) * mm, v(-134.7, -154.1) * mm, v(-134.6, -154.3) * mm, v(-134.43, -154.41) * mm]});
            skFitSpline(sketch, "E3424", {"points": [v(-133.74, -153.73) * mm, v(-133.65, -153.88) * mm, v(-133.49, -153.98) * mm, v(-133.31, -153.98) * mm]});
            skLineSegment(sketch, "E3425", {"start": v(245.47, -36.02) * mm, "end": v(246.63, -34.86) * mm});
            skFitSpline(sketch, "E3426", {"points": [v(-131.68, -153.98) * mm, v(-131.54, -153.98) * mm, v(-131.42, -153.93) * mm, v(-131.32, -153.83) * mm]});
            skFitSpline(sketch, "E3427", {"points": [v(-131.32, -153.83) * mm, v(-131.23, -153.74) * mm, v(-131.18, -153.61) * mm, v(-131.18, -153.48) * mm]});
            skLineSegment(sketch, "E3428", {"start": v(246.63, -33.64) * mm, "end": v(239.46, -26.47) * mm});
            skFitSpline(sketch, "E3429", {"points": [v(-131.18, -148.48) * mm, v(-131.18, -148.35) * mm, v(-131.23, -148.22) * mm, v(-131.32, -148.12) * mm]});
            skFitSpline(sketch, "E3430", {"points": [v(-131.32, -148.12) * mm, v(-131.42, -148.03) * mm, v(-131.54, -147.98) * mm, v(-131.68, -147.98) * mm]});
            skLineSegment(sketch, "E3431", {"start": v(-144.18, -163.18) * mm, "end": v(-144.18, -159.98) * mm});
            skLineSegment(sketch, "E3432", {"start": v(-144.18, -159.98) * mm, "end": v(-141.18, -159.98) * mm});
            skLineSegment(sketch, "E3433", {"start": v(-141.18, -159.98) * mm, "end": v(-141.18, -158.7) * mm});
            skLineSegment(sketch, "E3434", {"start": v(-141.18, -158.7) * mm, "end": v(-137.18, -158.7) * mm});
            skLineSegment(sketch, "E3435", {"start": v(-137.18, -158.7) * mm, "end": v(-137.18, -159.98) * mm});
            skLineSegment(sketch, "E3436", {"start": v(-137.18, -159.98) * mm, "end": v(-134.18, -159.98) * mm});
            skLineSegment(sketch, "E3437", {"start": v(-134.18, -159.98) * mm, "end": v(-134.18, -154.84) * mm});
            skFitSpline(sketch, "E3438", {"points": [v(-133.31, -147.98) * mm, v(-133.49, -147.98) * mm, v(-133.65, -148.07) * mm, v(-133.74, -148.23) * mm]});
            skFitSpline(sketch, "E3439", {"points": [v(-134.43, -147.54) * mm, v(-134.6, -147.65) * mm, v(-134.7, -147.86) * mm, v(-134.67, -148.06) * mm]});
            skFitSpline(sketch, "E3440", {"points": [v(-134.67, -148.06) * mm, v(-134.63, -148.27) * mm, v(-134.47, -148.43) * mm, v(-134.26, -148.47) * mm]});
            skFitSpline(sketch, "E3441", {"points": [v(-134.26, -148.47) * mm, v(-134.06, -148.5) * mm, v(-133.85, -148.41) * mm, v(-133.74, -148.23) * mm]});
            skFitSpline(sketch, "E3442", {"points": [v(-134.43, -147.54) * mm, v(-134.27, -147.46) * mm, v(-134.18, -147.3) * mm, v(-134.18, -147.11) * mm]});
            skLineSegment(sketch, "E3443", {"start": v(-133.31, -153.98) * mm, "end": v(-131.68, -153.98) * mm});
            skLineSegment(sketch, "E3444", {"start": v(-131.18, -153.48) * mm, "end": v(-131.18, -148.48) * mm});
            skFitSpline(sketch, "E3445", {"points": [v(-180.18, -147.58) * mm, v(-180.7, -147.58) * mm, v(-181.22, -147.79) * mm, v(-181.6, -148.16) * mm]});
            skFitSpline(sketch, "E3446", {"points": [v(-181.6, -148.16) * mm, v(-181.97, -148.54) * mm, v(-182.18, -149.05) * mm, v(-182.18, -149.58) * mm]});
            skLineSegment(sketch, "E3447", {"start": v(-131.68, -147.98) * mm, "end": v(-133.31, -147.98) * mm});
            skFitSpline(sketch, "E3448", {"points": [v(-182.18, -183.58) * mm, v(-182.18, -184.1) * mm, v(-181.97, -184.62) * mm, v(-181.6, -185) * mm]});
            skFitSpline(sketch, "E3449", {"points": [v(-181.6, -185) * mm, v(-181.22, -185.37) * mm, v(-180.7, -185.58) * mm, v(-180.18, -185.58) * mm]});
            skLineSegment(sketch, "E3450", {"start": v(-134.18, -147.11) * mm, "end": v(-134.18, -142.58) * mm});
            skLineSegment(sketch, "E3451", {"start": v(-134.18, -142.58) * mm, "end": v(-139.38, -142.58) * mm});
            skFitSpline(sketch, "E3452", {"points": [v(-134.18, -176.04) * mm, v(-134.18, -175.87) * mm, v(-134.27, -175.7) * mm, v(-134.43, -175.61) * mm]});
            skFitSpline(sketch, "E3453", {"points": [v(-133.74, -174.93) * mm, v(-133.85, -174.75) * mm, v(-134.06, -174.65) * mm, v(-134.26, -174.69) * mm]});
            skFitSpline(sketch, "E3454", {"points": [v(-134.26, -174.69) * mm, v(-134.47, -174.72) * mm, v(-134.63, -174.88) * mm, v(-134.67, -175.1) * mm]});
            skFitSpline(sketch, "E3455", {"points": [v(-134.67, -175.1) * mm, v(-134.7, -175.3) * mm, v(-134.6, -175.5) * mm, v(-134.43, -175.61) * mm]});
            skFitSpline(sketch, "E3456", {"points": [v(-133.74, -174.93) * mm, v(-133.65, -175.08) * mm, v(-133.49, -175.18) * mm, v(-133.31, -175.18) * mm]});
            skLineSegment(sketch, "E3457", {"start": v(-148.69, -147.58) * mm, "end": v(-180.18, -147.58) * mm});
            skFitSpline(sketch, "E3458", {"points": [v(-131.68, -175.18) * mm, v(-131.54, -175.18) * mm, v(-131.42, -175.13) * mm, v(-131.32, -175.03) * mm]});
            skFitSpline(sketch, "E3459", {"points": [v(-131.32, -175.03) * mm, v(-131.23, -174.94) * mm, v(-131.18, -174.81) * mm, v(-131.18, -174.68) * mm]});
            skLineSegment(sketch, "E3460", {"start": v(-182.18, -149.58) * mm, "end": v(-182.18, -183.58) * mm});
            skFitSpline(sketch, "E3461", {"points": [v(-131.18, -169.68) * mm, v(-131.18, -169.55) * mm, v(-131.23, -169.42) * mm, v(-131.32, -169.32) * mm]});
            skFitSpline(sketch, "E3462", {"points": [v(-131.32, -169.32) * mm, v(-131.42, -169.23) * mm, v(-131.54, -169.18) * mm, v(-131.68, -169.18) * mm]});
            skLineSegment(sketch, "E3463", {"start": v(-180.18, -185.58) * mm, "end": v(-143.15, -185.58) * mm});
            skFitSpline(sketch, "E3464", {"points": [v(-133.31, -169.18) * mm, v(-133.49, -169.18) * mm, v(-133.65, -169.27) * mm, v(-133.74, -169.43) * mm]});
            skFitSpline(sketch, "E3465", {"points": [v(-134.43, -168.74) * mm, v(-134.6, -168.85) * mm, v(-134.7, -169.06) * mm, v(-134.67, -169.26) * mm]});
            skFitSpline(sketch, "E3466", {"points": [v(-134.67, -169.26) * mm, v(-134.63, -169.47) * mm, v(-134.47, -169.63) * mm, v(-134.26, -169.67) * mm]});
            skFitSpline(sketch, "E3467", {"points": [v(-134.26, -169.67) * mm, v(-134.06, -169.7) * mm, v(-133.85, -169.6) * mm, v(-133.74, -169.43) * mm]});
            skFitSpline(sketch, "E3468", {"points": [v(-134.43, -168.74) * mm, v(-134.27, -168.66) * mm, v(-134.18, -168.5) * mm, v(-134.18, -168.31) * mm]});
            skLineSegment(sketch, "E3469", {"start": v(-133.31, -175.18) * mm, "end": v(-131.68, -175.18) * mm});
            skFitSpline(sketch, "E3470", {"points": [v(-150.86, -166.58) * mm, v(-150.86, -162.61) * mm, v(-152.97, -158.94) * mm, v(-156.4, -156.96) * mm]});
            skFitSpline(sketch, "E3471", {"points": [v(-156.4, -156.96) * mm, v(-159.84, -154.97) * mm, v(-164.08, -154.97) * mm, v(-167.51, -156.96) * mm]});
            skFitSpline(sketch, "E3472", {"points": [v(-167.51, -156.96) * mm, v(-170.95, -158.94) * mm, v(-173.06, -162.61) * mm, v(-173.06, -166.58) * mm]});
            skFitSpline(sketch, "E3473", {"points": [v(-173.06, -166.58) * mm, v(-173.06, -170.55) * mm, v(-170.95, -174.21) * mm, v(-167.51, -176.2) * mm]});
            skFitSpline(sketch, "E3474", {"points": [v(-167.51, -176.2) * mm, v(-164.08, -178.18) * mm, v(-159.84, -178.18) * mm, v(-156.4, -176.2) * mm]});
            skFitSpline(sketch, "E3475", {"points": [v(-156.4, -176.2) * mm, v(-152.97, -174.21) * mm, v(-150.86, -170.55) * mm, v(-150.86, -166.58) * mm]});
            skLineSegment(sketch, "E3476", {"start": v(-131.18, -174.68) * mm, "end": v(-131.18, -169.68) * mm});
            skFitSpline(sketch, "E3477", {"points": [v(-144.86, -182.08) * mm, v(-144.86, -181.5) * mm, v(-145.17, -180.98) * mm, v(-145.66, -180.7) * mm]});
            skFitSpline(sketch, "E3478", {"points": [v(-145.66, -180.7) * mm, v(-146.16, -180.4) * mm, v(-146.77, -180.4) * mm, v(-147.26, -180.7) * mm]});
            skFitSpline(sketch, "E3479", {"points": [v(-147.26, -180.7) * mm, v(-147.76, -180.98) * mm, v(-148.06, -181.5) * mm, v(-148.06, -182.08) * mm]});
            skFitSpline(sketch, "E3480", {"points": [v(-148.06, -182.08) * mm, v(-148.06, -182.65) * mm, v(-147.76, -183.18) * mm, v(-147.26, -183.46) * mm]});
            skFitSpline(sketch, "E3481", {"points": [v(-147.26, -183.46) * mm, v(-146.77, -183.75) * mm, v(-146.16, -183.75) * mm, v(-145.66, -183.46) * mm]});
            skFitSpline(sketch, "E3482", {"points": [v(-145.66, -183.46) * mm, v(-145.17, -183.18) * mm, v(-144.86, -182.65) * mm, v(-144.86, -182.08) * mm]});
            skLineSegment(sketch, "E3483", {"start": v(-131.68, -169.18) * mm, "end": v(-133.31, -169.18) * mm});
            skFitSpline(sketch, "E3484", {"points": [v(-175.86, -182.08) * mm, v(-175.86, -181.5) * mm, v(-176.17, -180.98) * mm, v(-176.66, -180.7) * mm]});
            skFitSpline(sketch, "E3485", {"points": [v(-176.66, -180.7) * mm, v(-177.16, -180.4) * mm, v(-177.77, -180.4) * mm, v(-178.26, -180.7) * mm]});
            skFitSpline(sketch, "E3486", {"points": [v(-178.26, -180.7) * mm, v(-178.76, -180.98) * mm, v(-179.06, -181.5) * mm, v(-179.06, -182.08) * mm]});
            skFitSpline(sketch, "E3487", {"points": [v(-179.06, -182.08) * mm, v(-179.06, -182.65) * mm, v(-178.76, -183.18) * mm, v(-178.26, -183.46) * mm]});
            skFitSpline(sketch, "E3488", {"points": [v(-178.26, -183.46) * mm, v(-177.77, -183.75) * mm, v(-177.16, -183.75) * mm, v(-176.66, -183.46) * mm]});
            skFitSpline(sketch, "E3489", {"points": [v(-176.66, -183.46) * mm, v(-176.17, -183.18) * mm, v(-175.86, -182.65) * mm, v(-175.86, -182.08) * mm]});
            skLineSegment(sketch, "E3490", {"start": v(-134.18, -168.31) * mm, "end": v(-134.18, -163.18) * mm});
            skLineSegment(sketch, "E3491", {"start": v(-134.18, -163.18) * mm, "end": v(-137.18, -163.18) * mm});
            skLineSegment(sketch, "E3492", {"start": v(-137.18, -163.18) * mm, "end": v(-137.18, -164.45) * mm});
            skLineSegment(sketch, "E3493", {"start": v(-137.18, -164.45) * mm, "end": v(-141.18, -164.45) * mm});
            skLineSegment(sketch, "E3494", {"start": v(-141.18, -164.45) * mm, "end": v(-141.18, -163.18) * mm});
            skLineSegment(sketch, "E3495", {"start": v(-141.18, -163.18) * mm, "end": v(-144.18, -163.18) * mm});
            skFitSpline(sketch, "E3496", {"points": [v(-144.86, -151.08) * mm, v(-144.86, -150.5) * mm, v(-145.17, -149.98) * mm, v(-145.66, -149.7) * mm]});
            skFitSpline(sketch, "E3497", {"points": [v(-145.66, -149.7) * mm, v(-146.16, -149.4) * mm, v(-146.77, -149.4) * mm, v(-147.26, -149.7) * mm]});
            skFitSpline(sketch, "E3498", {"points": [v(-147.26, -149.7) * mm, v(-147.76, -149.98) * mm, v(-148.06, -150.5) * mm, v(-148.06, -151.08) * mm]});
            skFitSpline(sketch, "E3499", {"points": [v(-148.06, -151.08) * mm, v(-148.06, -151.65) * mm, v(-147.76, -152.18) * mm, v(-147.26, -152.46) * mm]});
            skFitSpline(sketch, "E3500", {"points": [v(-147.26, -152.46) * mm, v(-146.77, -152.75) * mm, v(-146.16, -152.75) * mm, v(-145.66, -152.46) * mm]});
            skFitSpline(sketch, "E3501", {"points": [v(-145.66, -152.46) * mm, v(-145.17, -152.18) * mm, v(-144.86, -151.65) * mm, v(-144.86, -151.08) * mm]});
            skFitSpline(sketch, "E3502", {"points": [v(-175.86, -151.08) * mm, v(-175.86, -150.5) * mm, v(-176.17, -149.98) * mm, v(-176.66, -149.7) * mm]});
            skFitSpline(sketch, "E3503", {"points": [v(-176.66, -149.7) * mm, v(-177.16, -149.4) * mm, v(-177.77, -149.4) * mm, v(-178.26, -149.7) * mm]});
            skFitSpline(sketch, "E3504", {"points": [v(-178.26, -149.7) * mm, v(-178.76, -149.98) * mm, v(-179.06, -150.5) * mm, v(-179.06, -151.08) * mm]});
            skFitSpline(sketch, "E3505", {"points": [v(-179.06, -151.08) * mm, v(-179.06, -151.65) * mm, v(-178.76, -152.18) * mm, v(-178.26, -152.46) * mm]});
            skFitSpline(sketch, "E3506", {"points": [v(-178.26, -152.46) * mm, v(-177.77, -152.75) * mm, v(-177.16, -152.75) * mm, v(-176.66, -152.46) * mm]});
            skFitSpline(sketch, "E3507", {"points": [v(-176.66, -152.46) * mm, v(-176.17, -152.18) * mm, v(-175.86, -151.65) * mm, v(-175.86, -151.08) * mm]});
            skFitSpline(sketch, "E3508", {"points": [v(-384.91, 192.94) * mm, v(-385.19, 192.94) * mm, v(-385.41, 192.72) * mm, v(-385.41, 192.44) * mm]});
            skLineSegment(sketch, "E3509", {"start": v(-134.18, -180.58) * mm, "end": v(-134.18, -176.04) * mm});
            skFitSpline(sketch, "E3510", {"points": [v(-379.41, 192.44) * mm, v(-379.41, 192.72) * mm, v(-379.64, 192.94) * mm, v(-379.91, 192.94) * mm]});
            skLineSegment(sketch, "E3511", {"start": v(-358.21, 192.41) * mm, "end": v(-358.21, 188.43) * mm});
            skLineSegment(sketch, "E3512", {"start": v(-358.21, 188.43) * mm, "end": v(-358.21, -63.18) * mm});
            skFitSpline(sketch, "E3513", {"points": [v(-379.66, 190.38) * mm, v(-379.5, 190.47) * mm, v(-379.41, 190.63) * mm, v(-379.41, 190.8) * mm]});
            skFitSpline(sketch, "E3514", {"points": [v(-379.66, 190.38) * mm, v(-379.85, 190.27) * mm, v(-379.94, 190.06) * mm, v(-379.9, 189.86) * mm]});
            skFitSpline(sketch, "E3515", {"points": [v(-379.9, 189.86) * mm, v(-379.87, 189.65) * mm, v(-379.7, 189.49) * mm, v(-379.5, 189.45) * mm]});
            skFitSpline(sketch, "E3516", {"points": [v(-379.5, 189.45) * mm, v(-379.3, 189.41) * mm, v(-379.09, 189.51) * mm, v(-378.98, 189.7) * mm]});
            skFitSpline(sketch, "E3517", {"points": [v(-378.55, 189.94) * mm, v(-378.73, 189.94) * mm, v(-378.9, 189.85) * mm, v(-378.98, 189.7) * mm]});
            skLineSegment(sketch, "E3518", {"start": v(-358.21, 192.44) * mm, "end": v(-358.21, 192.41) * mm});
            skFitSpline(sketch, "E3519", {"points": [v(-364.65, 189.7) * mm, v(-364.74, 189.85) * mm, v(-364.9, 189.94) * mm, v(-365.08, 189.94) * mm]});
            skFitSpline(sketch, "E3520", {"points": [v(-364.65, 189.7) * mm, v(-364.54, 189.51) * mm, v(-364.33, 189.41) * mm, v(-364.13, 189.45) * mm]});
            skFitSpline(sketch, "E3521", {"points": [v(-364.13, 189.45) * mm, v(-363.92, 189.49) * mm, v(-363.76, 189.65) * mm, v(-363.72, 189.86) * mm]});
            skFitSpline(sketch, "E3522", {"points": [v(-363.72, 189.86) * mm, v(-363.68, 190.06) * mm, v(-363.78, 190.27) * mm, v(-363.96, 190.38) * mm]});
            skFitSpline(sketch, "E3523", {"points": [v(-364.21, 190.8) * mm, v(-364.21, 190.63) * mm, v(-364.12, 190.47) * mm, v(-363.96, 190.38) * mm]});
            skLineSegment(sketch, "E3524", {"start": v(-384.91, 192.94) * mm, "end": v(-379.91, 192.94) * mm});
            skFitSpline(sketch, "E3525", {"points": [v(-363.71, 192.94) * mm, v(-363.99, 192.94) * mm, v(-364.21, 192.72) * mm, v(-364.21, 192.44) * mm]});
            skLineSegment(sketch, "E3526", {"start": v(-379.41, 192.44) * mm, "end": v(-379.41, 190.8) * mm});
            skFitSpline(sketch, "E3527", {"points": [v(-358.21, 192.44) * mm, v(-358.21, 192.72) * mm, v(-358.44, 192.94) * mm, v(-358.71, 192.94) * mm]});
            skFitSpline(sketch, "E3528", {"points": [v(-370.21, 138.94) * mm, v(-370.21, 139.52) * mm, v(-370.52, 140.04) * mm, v(-371.01, 140.33) * mm]});
            skFitSpline(sketch, "E3529", {"points": [v(-371.01, 140.33) * mm, v(-371.5, 140.62) * mm, v(-372.12, 140.62) * mm, v(-372.61, 140.33) * mm]});
            skFitSpline(sketch, "E3530", {"points": [v(-372.61, 140.33) * mm, v(-373.1, 140.04) * mm, v(-373.41, 139.52) * mm, v(-373.41, 138.94) * mm]});
            skFitSpline(sketch, "E3531", {"points": [v(-373.41, 138.94) * mm, v(-373.41, 138.37) * mm, v(-373.1, 137.84) * mm, v(-372.61, 137.56) * mm]});
            skFitSpline(sketch, "E3532", {"points": [v(-372.61, 137.56) * mm, v(-372.12, 137.27) * mm, v(-371.5, 137.27) * mm, v(-371.01, 137.56) * mm]});
            skFitSpline(sketch, "E3533", {"points": [v(-371.01, 137.56) * mm, v(-370.52, 137.84) * mm, v(-370.21, 138.37) * mm, v(-370.21, 138.94) * mm]});
            skLineSegment(sketch, "E3534", {"start": v(-378.55, 189.94) * mm, "end": v(-373.41, 189.94) * mm});
            skLineSegment(sketch, "E3535", {"start": v(-373.41, 189.94) * mm, "end": v(-373.41, 186.94) * mm});
            skLineSegment(sketch, "E3536", {"start": v(-373.41, 186.94) * mm, "end": v(-374.69, 186.94) * mm});
            skLineSegment(sketch, "E3537", {"start": v(-374.69, 186.94) * mm, "end": v(-374.69, 182.94) * mm});
            skLineSegment(sketch, "E3538", {"start": v(-374.69, 182.94) * mm, "end": v(-373.41, 182.94) * mm});
            skLineSegment(sketch, "E3539", {"start": v(-373.41, 182.94) * mm, "end": v(-373.41, 179.94) * mm});
            skLineSegment(sketch, "E3540", {"start": v(-373.41, 179.94) * mm, "end": v(-370.21, 179.94) * mm});
            skLineSegment(sketch, "E3541", {"start": v(-370.21, 179.94) * mm, "end": v(-370.21, 182.94) * mm});
            skLineSegment(sketch, "E3542", {"start": v(-370.21, 182.94) * mm, "end": v(-368.94, 182.94) * mm});
            skLineSegment(sketch, "E3543", {"start": v(-368.94, 182.94) * mm, "end": v(-368.94, 186.94) * mm});
            skLineSegment(sketch, "E3544", {"start": v(-368.94, 186.94) * mm, "end": v(-370.21, 186.94) * mm});
            skLineSegment(sketch, "E3545", {"start": v(-370.21, 186.94) * mm, "end": v(-370.21, 189.94) * mm});
            skLineSegment(sketch, "E3546", {"start": v(-370.21, 189.94) * mm, "end": v(-365.08, 189.94) * mm});
            skLineSegment(sketch, "E3547", {"start": v(-364.21, 190.8) * mm, "end": v(-364.21, 192.44) * mm});
            skFitSpline(sketch, "E3548", {"points": [v(325.91, 163.65) * mm, v(326.54, 163.65) * mm, v(327.11, 163.98) * mm, v(327.43, 164.52) * mm]});
            skFitSpline(sketch, "E3549", {"points": [v(327.43, 164.52) * mm, v(327.74, 165.06) * mm, v(327.74, 165.73) * mm, v(327.43, 166.27) * mm]});
            skFitSpline(sketch, "E3550", {"points": [v(327.43, 166.27) * mm, v(327.11, 166.81) * mm, v(326.54, 167.15) * mm, v(325.91, 167.15) * mm]});
            skFitSpline(sketch, "E3551", {"points": [v(325.91, 167.15) * mm, v(325.29, 167.15) * mm, v(324.7, 166.81) * mm, v(324.4, 166.27) * mm]});
            skFitSpline(sketch, "E3552", {"points": [v(324.4, 166.27) * mm, v(324.08, 165.73) * mm, v(324.08, 165.06) * mm, v(324.4, 164.52) * mm]});
            skFitSpline(sketch, "E3553", {"points": [v(324.4, 164.52) * mm, v(324.7, 163.98) * mm, v(325.29, 163.65) * mm, v(325.91, 163.65) * mm]});
            skLineSegment(sketch, "E3554", {"start": v(-363.71, 192.94) * mm, "end": v(-358.71, 192.94) * mm});
            skFitSpline(sketch, "E3555", {"points": [v(225.91, 163.65) * mm, v(226.54, 163.65) * mm, v(227.12, 163.98) * mm, v(227.43, 164.52) * mm]});
            skFitSpline(sketch, "E3556", {"points": [v(227.43, 164.52) * mm, v(227.74, 165.06) * mm, v(227.74, 165.73) * mm, v(227.43, 166.27) * mm]});
            skFitSpline(sketch, "E3557", {"points": [v(227.43, 166.27) * mm, v(227.12, 166.81) * mm, v(226.54, 167.15) * mm, v(225.91, 167.15) * mm]});
            skFitSpline(sketch, "E3558", {"points": [v(225.91, 167.15) * mm, v(225.29, 167.15) * mm, v(224.7, 166.81) * mm, v(224.4, 166.27) * mm]});
            skFitSpline(sketch, "E3559", {"points": [v(224.4, 166.27) * mm, v(224.08, 165.73) * mm, v(224.08, 165.06) * mm, v(224.4, 164.52) * mm]});
            skFitSpline(sketch, "E3560", {"points": [v(224.4, 164.52) * mm, v(224.7, 163.98) * mm, v(225.29, 163.65) * mm, v(225.91, 163.65) * mm]});
            skFitSpline(sketch, "E3561", {"points": [v(7.71, -192.95) * mm, v(7.85, -192.95) * mm, v(7.97, -192.9) * mm, v(8.07, -192.8) * mm]});
            skFitSpline(sketch, "E3562", {"points": [v(8.07, -192.8) * mm, v(8.16, -192.7) * mm, v(8.21, -192.58) * mm, v(8.21, -192.45) * mm]});
            skLineSegment(sketch, "E3563", {"start": v(-18.99, -192.45) * mm, "end": v(-18.99, -188.46) * mm});
            skLineSegment(sketch, "E3564", {"start": v(-18.99, -188.46) * mm, "end": v(-18.96, 63.18) * mm});
            skFitSpline(sketch, "E3565", {"points": [v(2.21, -192.45) * mm, v(2.21, -192.72) * mm, v(2.44, -192.95) * mm, v(2.71, -192.95) * mm]});
            skFitSpline(sketch, "E3566", {"points": [v(2.46, -190.38) * mm, v(2.3, -190.47) * mm, v(2.21, -190.64) * mm, v(2.21, -190.81) * mm]});
            skFitSpline(sketch, "E3567", {"points": [v(2.46, -190.38) * mm, v(2.65, -190.28) * mm, v(2.74, -190.07) * mm, v(2.7, -189.86) * mm]});
            skFitSpline(sketch, "E3568", {"points": [v(2.7, -189.86) * mm, v(2.67, -189.65) * mm, v(2.5, -189.5) * mm, v(2.3, -189.46) * mm]});
            skFitSpline(sketch, "E3569", {"points": [v(2.3, -189.46) * mm, v(2.1, -189.42) * mm, v(1.89, -189.52) * mm, v(1.78, -189.7) * mm]});
            skFitSpline(sketch, "E3570", {"points": [v(1.35, -189.95) * mm, v(1.53, -189.95) * mm, v(1.7, -189.85) * mm, v(1.78, -189.7) * mm]});
            skFitSpline(sketch, "E3571", {"points": [v(-12.55, -189.7) * mm, v(-12.46, -189.85) * mm, v(-12.3, -189.95) * mm, v(-12.12, -189.95) * mm]});
            skFitSpline(sketch, "E3572", {"points": [v(-12.55, -189.7) * mm, v(-12.66, -189.52) * mm, v(-12.87, -189.42) * mm, v(-13.07, -189.46) * mm]});
            skFitSpline(sketch, "E3573", {"points": [v(-13.07, -189.46) * mm, v(-13.28, -189.5) * mm, v(-13.44, -189.65) * mm, v(-13.48, -189.86) * mm]});
            skFitSpline(sketch, "E3574", {"points": [v(-13.48, -189.86) * mm, v(-13.52, -190.07) * mm, v(-13.42, -190.28) * mm, v(-13.24, -190.38) * mm]});
            skFitSpline(sketch, "E3575", {"points": [v(-12.99, -190.81) * mm, v(-12.99, -190.64) * mm, v(-13.08, -190.47) * mm, v(-13.24, -190.38) * mm]});
            skLineSegment(sketch, "E3576", {"start": v(7.71, -192.95) * mm, "end": v(2.71, -192.95) * mm});
            skFitSpline(sketch, "E3577", {"points": [v(-13.49, -192.95) * mm, v(-13.21, -192.95) * mm, v(-12.99, -192.72) * mm, v(-12.99, -192.45) * mm]});
            skLineSegment(sketch, "E3578", {"start": v(2.21, -192.45) * mm, "end": v(2.21, -190.81) * mm});
            skFitSpline(sketch, "E3579", {"points": [v(-18.99, -192.45) * mm, v(-18.99, -192.72) * mm, v(-18.76, -192.95) * mm, v(-18.49, -192.95) * mm]});
            skFitSpline(sketch, "E3580", {"points": [v(-3.86, -138.95) * mm, v(-3.86, -138.38) * mm, v(-4.16, -137.85) * mm, v(-4.66, -137.56) * mm]});
            skFitSpline(sketch, "E3581", {"points": [v(-4.66, -137.56) * mm, v(-5.15, -137.28) * mm, v(-5.76, -137.28) * mm, v(-6.26, -137.56) * mm]});
            skFitSpline(sketch, "E3582", {"points": [v(-6.26, -137.56) * mm, v(-6.75, -137.85) * mm, v(-7.06, -138.38) * mm, v(-7.06, -138.95) * mm]});
            skFitSpline(sketch, "E3583", {"points": [v(-7.06, -138.95) * mm, v(-7.06, -139.52) * mm, v(-6.75, -140.05) * mm, v(-6.26, -140.33) * mm]});
            skFitSpline(sketch, "E3584", {"points": [v(-6.26, -140.33) * mm, v(-5.76, -140.62) * mm, v(-5.15, -140.62) * mm, v(-4.66, -140.33) * mm]});
            skFitSpline(sketch, "E3585", {"points": [v(-4.66, -140.33) * mm, v(-4.16, -140.05) * mm, v(-3.86, -139.52) * mm, v(-3.86, -138.95) * mm]});
            skLineSegment(sketch, "E3586", {"start": v(1.35, -189.95) * mm, "end": v(-3.79, -189.95) * mm});
            skLineSegment(sketch, "E3587", {"start": v(-3.79, -189.95) * mm, "end": v(-3.79, -186.95) * mm});
            skLineSegment(sketch, "E3588", {"start": v(-3.79, -186.95) * mm, "end": v(-2.51, -186.95) * mm});
            skLineSegment(sketch, "E3589", {"start": v(-2.51, -186.95) * mm, "end": v(-2.51, -182.95) * mm});
            skLineSegment(sketch, "E3590", {"start": v(-2.51, -182.95) * mm, "end": v(-3.79, -182.95) * mm});
            skLineSegment(sketch, "E3591", {"start": v(-3.79, -182.95) * mm, "end": v(-3.79, -179.95) * mm});
            skLineSegment(sketch, "E3592", {"start": v(-3.79, -179.95) * mm, "end": v(-6.99, -179.95) * mm});
            skLineSegment(sketch, "E3593", {"start": v(-6.99, -179.95) * mm, "end": v(-6.99, -182.95) * mm});
            skLineSegment(sketch, "E3594", {"start": v(-6.99, -182.95) * mm, "end": v(-8.26, -182.95) * mm});
            skLineSegment(sketch, "E3595", {"start": v(-8.26, -182.95) * mm, "end": v(-8.26, -186.95) * mm});
            skLineSegment(sketch, "E3596", {"start": v(-8.26, -186.95) * mm, "end": v(-6.99, -186.95) * mm});
            skLineSegment(sketch, "E3597", {"start": v(-6.99, -186.95) * mm, "end": v(-6.99, -189.95) * mm});
            skLineSegment(sketch, "E3598", {"start": v(-6.99, -189.95) * mm, "end": v(-12.12, -189.95) * mm});
            skLineSegment(sketch, "E3599", {"start": v(-12.99, -190.81) * mm, "end": v(-12.99, -192.45) * mm});
            skLineSegment(sketch, "E3600", {"start": v(-13.49, -192.95) * mm, "end": v(-18.49, -192.95) * mm});
            skFitSpline(sketch, "E3601", {"points": [v(125.91, 163.65) * mm, v(126.54, 163.65) * mm, v(127.12, 163.98) * mm, v(127.43, 164.52) * mm]});
            skFitSpline(sketch, "E3602", {"points": [v(127.43, 164.52) * mm, v(127.74, 165.06) * mm, v(127.74, 165.73) * mm, v(127.43, 166.27) * mm]});
            skFitSpline(sketch, "E3603", {"points": [v(127.43, 166.27) * mm, v(127.12, 166.81) * mm, v(126.54, 167.15) * mm, v(125.91, 167.15) * mm]});
            skFitSpline(sketch, "E3604", {"points": [v(125.91, 167.15) * mm, v(125.29, 167.15) * mm, v(124.71, 166.81) * mm, v(124.4, 166.27) * mm]});
            skFitSpline(sketch, "E3605", {"points": [v(124.4, 166.27) * mm, v(124.09, 165.73) * mm, v(124.09, 165.06) * mm, v(124.4, 164.52) * mm]});
            skFitSpline(sketch, "E3606", {"points": [v(124.4, 164.52) * mm, v(124.71, 163.98) * mm, v(125.29, 163.65) * mm, v(125.91, 163.65) * mm]});
            skFitSpline(sketch, "E3607", {"points": [v(50.91, 163.65) * mm, v(51.54, 163.65) * mm, v(52.12, 163.98) * mm, v(52.43, 164.52) * mm]});
            skFitSpline(sketch, "E3608", {"points": [v(52.43, 164.52) * mm, v(52.74, 165.06) * mm, v(52.74, 165.73) * mm, v(52.43, 166.27) * mm]});
            skFitSpline(sketch, "E3609", {"points": [v(52.43, 166.27) * mm, v(52.12, 166.81) * mm, v(51.54, 167.15) * mm, v(50.91, 167.15) * mm]});
            skFitSpline(sketch, "E3610", {"points": [v(50.91, 167.15) * mm, v(50.29, 167.15) * mm, v(49.71, 166.81) * mm, v(49.4, 166.27) * mm]});
            skFitSpline(sketch, "E3611", {"points": [v(49.4, 166.27) * mm, v(49.09, 165.73) * mm, v(49.09, 165.06) * mm, v(49.4, 164.52) * mm]});
            skFitSpline(sketch, "E3612", {"points": [v(49.4, 164.52) * mm, v(49.71, 163.98) * mm, v(50.29, 163.65) * mm, v(50.91, 163.65) * mm]});
            skFitSpline(sketch, "E3613", {"points": [v(325.91, -166.94) * mm, v(326.88, -166.94) * mm, v(327.66, -166.16) * mm, v(327.66, -165.2) * mm]});
            skFitSpline(sketch, "E3614", {"points": [v(327.66, -165.2) * mm, v(327.66, -164.23) * mm, v(326.88, -163.44) * mm, v(325.91, -163.44) * mm]});
            skFitSpline(sketch, "E3615", {"points": [v(325.91, -163.44) * mm, v(325.29, -163.44) * mm, v(324.7, -163.78) * mm, v(324.4, -164.32) * mm]});
            skFitSpline(sketch, "E3616", {"points": [v(324.4, -164.32) * mm, v(324.08, -164.86) * mm, v(324.08, -165.53) * mm, v(324.4, -166.07) * mm]});
            skFitSpline(sketch, "E3617", {"points": [v(324.4, -166.07) * mm, v(324.7, -166.61) * mm, v(325.29, -166.94) * mm, v(325.91, -166.94) * mm]});
            skFitSpline(sketch, "E3618", {"points": [v(225.91, -166.94) * mm, v(226.88, -166.94) * mm, v(227.66, -166.16) * mm, v(227.66, -165.2) * mm]});
            skFitSpline(sketch, "E3619", {"points": [v(227.66, -165.2) * mm, v(227.66, -164.23) * mm, v(226.88, -163.44) * mm, v(225.91, -163.44) * mm]});
            skFitSpline(sketch, "E3620", {"points": [v(225.91, -163.44) * mm, v(225.29, -163.44) * mm, v(224.7, -163.78) * mm, v(224.4, -164.32) * mm]});
            skFitSpline(sketch, "E3621", {"points": [v(224.4, -164.32) * mm, v(224.08, -164.86) * mm, v(224.08, -165.53) * mm, v(224.4, -166.07) * mm]});
            skFitSpline(sketch, "E3622", {"points": [v(224.4, -166.07) * mm, v(224.7, -166.61) * mm, v(225.29, -166.94) * mm, v(225.91, -166.94) * mm]});
            skFitSpline(sketch, "E3623", {"points": [v(125.91, -166.94) * mm, v(126.88, -166.94) * mm, v(127.66, -166.16) * mm, v(127.66, -165.2) * mm]});
            skFitSpline(sketch, "E3624", {"points": [v(127.66, -165.2) * mm, v(127.66, -164.23) * mm, v(126.88, -163.44) * mm, v(125.91, -163.44) * mm]});
            skFitSpline(sketch, "E3625", {"points": [v(125.91, -163.44) * mm, v(125.29, -163.44) * mm, v(124.7, -163.78) * mm, v(124.4, -164.32) * mm]});
            skFitSpline(sketch, "E3626", {"points": [v(124.4, -164.32) * mm, v(124.08, -164.86) * mm, v(124.08, -165.53) * mm, v(124.4, -166.07) * mm]});
            skFitSpline(sketch, "E3627", {"points": [v(124.4, -166.07) * mm, v(124.7, -166.61) * mm, v(125.29, -166.94) * mm, v(125.91, -166.94) * mm]});
            skFitSpline(sketch, "E3628", {"points": [v(50.91, -166.94) * mm, v(51.88, -166.94) * mm, v(52.66, -166.16) * mm, v(52.66, -165.2) * mm]});
            skFitSpline(sketch, "E3629", {"points": [v(52.66, -165.2) * mm, v(52.66, -164.23) * mm, v(51.88, -163.44) * mm, v(50.91, -163.44) * mm]});
            skFitSpline(sketch, "E3630", {"points": [v(50.91, -163.44) * mm, v(50.29, -163.44) * mm, v(49.71, -163.78) * mm, v(49.4, -164.32) * mm]});
            skFitSpline(sketch, "E3631", {"points": [v(49.4, -164.32) * mm, v(49.08, -164.86) * mm, v(49.08, -165.53) * mm, v(49.4, -166.07) * mm]});
            skFitSpline(sketch, "E3632", {"points": [v(49.4, -166.07) * mm, v(49.71, -166.61) * mm, v(50.29, -166.94) * mm, v(50.91, -166.94) * mm]});
            skFitSpline(sketch, "E3633", {"points": [v(-142.83, -45.08) * mm, v(-142.83, -44.74) * mm, v(-143.01, -44.42) * mm, v(-143.31, -44.24) * mm]});
            skFitSpline(sketch, "E3634", {"points": [v(-142, -42.93) * mm, v(-142.2, -42.58) * mm, v(-142.6, -42.39) * mm, v(-143, -42.46) * mm]});
            skFitSpline(sketch, "E3635", {"points": [v(-143, -42.46) * mm, v(-143.4, -42.53) * mm, v(-143.7, -42.84) * mm, v(-143.78, -43.24) * mm]});
            skFitSpline(sketch, "E3636", {"points": [v(-143.78, -43.24) * mm, v(-143.85, -43.64) * mm, v(-143.66, -44.04) * mm, v(-143.31, -44.24) * mm]});
            skFitSpline(sketch, "E3637", {"points": [v(-142, -42.93) * mm, v(-141.82, -43.23) * mm, v(-141.5, -43.4) * mm, v(-141.16, -43.4) * mm]});
            skFitSpline(sketch, "E3638", {"points": [v(-132.53, -43.4) * mm, v(-132.19, -43.4) * mm, v(-131.87, -43.23) * mm, v(-131.7, -42.93) * mm]});
            skFitSpline(sketch, "E3639", {"points": [v(-130.38, -44.24) * mm, v(-130.03, -44.04) * mm, v(-129.84, -43.64) * mm, v(-129.91, -43.24) * mm]});
            skFitSpline(sketch, "E3640", {"points": [v(-129.91, -43.24) * mm, v(-129.98, -42.84) * mm, v(-130.3, -42.53) * mm, v(-130.7, -42.46) * mm]});
            skFitSpline(sketch, "E3641", {"points": [v(-130.7, -42.46) * mm, v(-131.1, -42.39) * mm, v(-131.5, -42.58) * mm, v(-131.7, -42.93) * mm]});
            skFitSpline(sketch, "E3642", {"points": [v(-130.38, -44.24) * mm, v(-130.68, -44.42) * mm, v(-130.86, -44.74) * mm, v(-130.86, -45.08) * mm]});
            skFitSpline(sketch, "E3643", {"points": [v(-130.86, -49.83) * mm, v(-130.86, -50.18) * mm, v(-130.68, -50.5) * mm, v(-130.38, -50.67) * mm]});
            skFitSpline(sketch, "E3644", {"points": [v(-131.7, -51.98) * mm, v(-131.5, -52.34) * mm, v(-131.1, -52.52) * mm, v(-130.7, -52.45) * mm]});
            skFitSpline(sketch, "E3645", {"points": [v(-130.7, -52.45) * mm, v(-130.3, -52.38) * mm, v(-129.98, -52.07) * mm, v(-129.91, -51.67) * mm]});
            skFitSpline(sketch, "E3646", {"points": [v(-129.91, -51.67) * mm, v(-129.84, -51.27) * mm, v(-130.03, -50.87) * mm, v(-130.38, -50.67) * mm]});
            skFitSpline(sketch, "E3647", {"points": [v(-131.7, -51.98) * mm, v(-131.87, -51.69) * mm, v(-132.19, -51.5) * mm, v(-132.53, -51.5) * mm]});
            skFitSpline(sketch, "E3648", {"points": [v(-141.16, -51.5) * mm, v(-141.5, -51.5) * mm, v(-141.82, -51.69) * mm, v(-142, -51.98) * mm]});
            skFitSpline(sketch, "E3649", {"points": [v(-143.31, -50.67) * mm, v(-143.66, -50.87) * mm, v(-143.85, -51.27) * mm, v(-143.78, -51.67) * mm]});
            skFitSpline(sketch, "E3650", {"points": [v(-143.78, -51.67) * mm, v(-143.7, -52.07) * mm, v(-143.4, -52.38) * mm, v(-143, -52.45) * mm]});
            skFitSpline(sketch, "E3651", {"points": [v(-143, -52.45) * mm, v(-142.6, -52.52) * mm, v(-142.2, -52.34) * mm, v(-142, -51.98) * mm]});
            skFitSpline(sketch, "E3652", {"points": [v(-143.31, -50.67) * mm, v(-143.01, -50.5) * mm, v(-142.83, -50.18) * mm, v(-142.83, -49.83) * mm]});
            skLineSegment(sketch, "E3653", {"start": v(-141.16, -43.4) * mm, "end": v(-132.53, -43.4) * mm});
            skFitSpline(sketch, "E3654", {"points": [v(-312.63, -44.4) * mm, v(-312.63, -44.06) * mm, v(-312.81, -43.74) * mm, v(-313.1, -43.57) * mm]});
            skFitSpline(sketch, "E3655", {"points": [v(-311.8, -42.25) * mm, v(-312, -41.9) * mm, v(-312.4, -41.71) * mm, v(-312.8, -41.78) * mm]});
            skFitSpline(sketch, "E3656", {"points": [v(-312.8, -41.78) * mm, v(-313.2, -41.85) * mm, v(-313.5, -42.17) * mm, v(-313.58, -42.57) * mm]});
            skFitSpline(sketch, "E3657", {"points": [v(-313.58, -42.57) * mm, v(-313.65, -42.97) * mm, v(-313.46, -43.37) * mm, v(-313.1, -43.57) * mm]});
            skFitSpline(sketch, "E3658", {"points": [v(-311.8, -42.25) * mm, v(-311.62, -42.55) * mm, v(-311.3, -42.73) * mm, v(-310.96, -42.73) * mm]});
            skLineSegment(sketch, "E3659", {"start": v(-130.86, -45.08) * mm, "end": v(-130.86, -49.83) * mm});
            skFitSpline(sketch, "E3660", {"points": [v(-302.33, -42.73) * mm, v(-301.99, -42.73) * mm, v(-301.67, -42.55) * mm, v(-301.5, -42.25) * mm]});
            skFitSpline(sketch, "E3661", {"points": [v(-300.18, -43.57) * mm, v(-299.83, -43.37) * mm, v(-299.64, -42.97) * mm, v(-299.71, -42.57) * mm]});
            skFitSpline(sketch, "E3662", {"points": [v(-299.71, -42.57) * mm, v(-299.78, -42.17) * mm, v(-300.1, -41.85) * mm, v(-300.5, -41.78) * mm]});
            skFitSpline(sketch, "E3663", {"points": [v(-300.5, -41.78) * mm, v(-300.9, -41.71) * mm, v(-301.3, -41.9) * mm, v(-301.5, -42.25) * mm]});
            skFitSpline(sketch, "E3664", {"points": [v(-300.18, -43.57) * mm, v(-300.48, -43.74) * mm, v(-300.66, -44.06) * mm, v(-300.66, -44.4) * mm]});
            skLineSegment(sketch, "E3665", {"start": v(-132.53, -51.5) * mm, "end": v(-141.16, -51.5) * mm});
            skFitSpline(sketch, "E3666", {"points": [v(-300.66, -47.43) * mm, v(-300.66, -47.78) * mm, v(-300.48, -48.1) * mm, v(-300.18, -48.27) * mm]});
            skFitSpline(sketch, "E3667", {"points": [v(-301.5, -49.58) * mm, v(-301.3, -49.94) * mm, v(-300.9, -50.12) * mm, v(-300.5, -50.05) * mm]});
            skFitSpline(sketch, "E3668", {"points": [v(-300.5, -50.05) * mm, v(-300.1, -49.98) * mm, v(-299.78, -49.67) * mm, v(-299.71, -49.27) * mm]});
            skFitSpline(sketch, "E3669", {"points": [v(-299.71, -49.27) * mm, v(-299.64, -48.87) * mm, v(-299.83, -48.47) * mm, v(-300.18, -48.27) * mm]});
            skFitSpline(sketch, "E3670", {"points": [v(-301.5, -49.58) * mm, v(-301.67, -49.29) * mm, v(-301.99, -49.1) * mm, v(-302.33, -49.1) * mm]});
            skLineSegment(sketch, "E3671", {"start": v(-142.83, -49.83) * mm, "end": v(-142.83, -45.08) * mm});
            skFitSpline(sketch, "E3672", {"points": [v(-310.96, -49.1) * mm, v(-311.3, -49.1) * mm, v(-311.62, -49.29) * mm, v(-311.8, -49.58) * mm]});
            skFitSpline(sketch, "E3673", {"points": [v(-313.1, -48.27) * mm, v(-313.46, -48.47) * mm, v(-313.65, -48.87) * mm, v(-313.58, -49.27) * mm]});
            skFitSpline(sketch, "E3674", {"points": [v(-313.58, -49.27) * mm, v(-313.5, -49.67) * mm, v(-313.2, -49.98) * mm, v(-312.8, -50.05) * mm]});
            skFitSpline(sketch, "E3675", {"points": [v(-312.8, -50.05) * mm, v(-312.4, -50.12) * mm, v(-312, -49.94) * mm, v(-311.8, -49.58) * mm]});
            skFitSpline(sketch, "E3676", {"points": [v(-313.1, -48.27) * mm, v(-312.81, -48.1) * mm, v(-312.63, -47.78) * mm, v(-312.63, -47.43) * mm]});
            skLineSegment(sketch, "E3677", {"start": v(-310.96, -42.73) * mm, "end": v(-302.33, -42.73) * mm});
            skFitSpline(sketch, "E3678", {"points": [v(299.45, -5.78) * mm, v(293.92, -5.78) * mm, v(289.45, -10.26) * mm, v(289.45, -15.78) * mm]});
            skLineSegment(sketch, "E3679", {"start": v(-300.66, -44.4) * mm, "end": v(-300.66, -47.43) * mm});
            skFitSpline(sketch, "E3680", {"points": [v(143.2, -92.6) * mm, v(142.08, -91.46) * mm, v(140.55, -90.83) * mm, v(138.96, -90.83) * mm]});
            skLineSegment(sketch, "E3681", {"start": v(-302.33, -49.1) * mm, "end": v(-310.96, -49.1) * mm});
            skFitSpline(sketch, "E3682", {"points": [v(123.93, -90.83) * mm, v(122.34, -90.83) * mm, v(120.81, -91.46) * mm, v(119.69, -92.6) * mm]});
            skLineSegment(sketch, "E3683", {"start": v(-312.63, -47.43) * mm, "end": v(-312.63, -44.4) * mm});
            skFitSpline(sketch, "E3684", {"points": [v(96.45, -101.83) * mm, v(94.51, -103.77) * mm, v(94.52, -106.9) * mm, v(96.45, -108.83) * mm]});
            skFitSpline(sketch, "E3685", {"points": [v(96.45, -108.83) * mm, v(98.38, -110.76) * mm, v(101.51, -110.77) * mm, v(103.45, -108.83) * mm]});
            skLineSegment(sketch, "E3686", {"start": v(289.45, -76.35) * mm, "end": v(289.45, -15.78) * mm});
            skFitSpline(sketch, "E3687", {"points": [v(117.69, -80.6) * mm, v(118.81, -79.46) * mm, v(119.45, -77.94) * mm, v(119.45, -76.35) * mm]});
            skLineSegment(sketch, "E3688", {"start": v(157.69, -107.08) * mm, "end": v(143.2, -92.6) * mm});
            skFitSpline(sketch, "E3689", {"points": [v(119.45, 74.68) * mm, v(119.45, 76.27) * mm, v(118.81, 77.8) * mm, v(117.69, 78.92) * mm]});
            skLineSegment(sketch, "E3690", {"start": v(138.96, -90.83) * mm, "end": v(123.93, -90.83) * mm});
            skFitSpline(sketch, "E3691", {"points": [v(103.45, 107.17) * mm, v(101.51, 109.1) * mm, v(98.38, 109.1) * mm, v(96.45, 107.16) * mm]});
            skFitSpline(sketch, "E3692", {"points": [v(96.45, 107.16) * mm, v(94.52, 105.23) * mm, v(94.51, 102.1) * mm, v(96.45, 100.17) * mm]});
            skLineSegment(sketch, "E3693", {"start": v(119.69, -92.6) * mm, "end": v(103.45, -108.83) * mm});
            skLineSegment(sketch, "E3694", {"start": v(96.45, -101.83) * mm, "end": v(117.69, -80.6) * mm});
            skFitSpline(sketch, "E3695", {"points": [v(312.45, 100.17) * mm, v(314.38, 102.1) * mm, v(314.38, 105.23) * mm, v(312.44, 107.16) * mm]});
            skFitSpline(sketch, "E3696", {"points": [v(312.44, 107.16) * mm, v(310.51, 109.1) * mm, v(307.38, 109.1) * mm, v(305.45, 107.17) * mm]});
            skLineSegment(sketch, "E3697", {"start": v(119.45, -76.35) * mm, "end": v(119.45, 74.68) * mm});
            skFitSpline(sketch, "E3698", {"points": [v(291.2, 78.92) * mm, v(290.08, 77.8) * mm, v(289.45, 76.27) * mm, v(289.45, 74.68) * mm]});
            skLineSegment(sketch, "E3699", {"start": v(117.69, 78.92) * mm, "end": v(96.45, 100.17) * mm});
            skFitSpline(sketch, "E3700", {"points": [v(289.45, -76.35) * mm, v(289.45, -77.94) * mm, v(290.08, -79.46) * mm, v(291.2, -80.6) * mm]});
            skLineSegment(sketch, "E3701", {"start": v(103.45, 107.17) * mm, "end": v(119.69, 90.92) * mm});
            skFitSpline(sketch, "E3702", {"points": [v(305.45, -108.83) * mm, v(307.38, -110.77) * mm, v(310.51, -110.77) * mm, v(312.45, -108.83) * mm]});
            skFitSpline(sketch, "E3703", {"points": [v(312.45, -108.83) * mm, v(314.38, -106.9) * mm, v(314.38, -103.77) * mm, v(312.45, -101.83) * mm]});
            skLineSegment(sketch, "E3704", {"start": v(289.2, 90.92) * mm, "end": v(305.45, 107.17) * mm});
            skFitSpline(sketch, "E3705", {"points": [v(289.2, -92.6) * mm, v(288.08, -91.46) * mm, v(286.55, -90.83) * mm, v(284.96, -90.83) * mm]});
            skLineSegment(sketch, "E3706", {"start": v(312.45, 100.17) * mm, "end": v(291.2, 78.92) * mm});
            skFitSpline(sketch, "E3707", {"points": [v(269.93, -90.83) * mm, v(268.34, -90.83) * mm, v(266.81, -91.46) * mm, v(265.69, -92.6) * mm]});
            skLineSegment(sketch, "E3708", {"start": v(289.45, 74.68) * mm, "end": v(289.45, 14.12) * mm});
            skFitSpline(sketch, "E3709", {"points": [v(246.96, -108.83) * mm, v(248.55, -108.83) * mm, v(250.08, -108.2) * mm, v(251.2, -107.08) * mm]});
            skLineSegment(sketch, "E3710", {"start": v(291.2, -80.6) * mm, "end": v(312.45, -101.83) * mm});
            skFitSpline(sketch, "E3711", {"points": [v(225.69, -107.08) * mm, v(226.81, -108.2) * mm, v(228.34, -108.83) * mm, v(229.93, -108.83) * mm]});
            skLineSegment(sketch, "E3712", {"start": v(305.45, -108.83) * mm, "end": v(289.2, -92.6) * mm});
            skFitSpline(sketch, "E3713", {"points": [v(211.2, -92.6) * mm, v(210.08, -91.46) * mm, v(208.55, -90.83) * mm, v(206.96, -90.83) * mm]});
            skLineSegment(sketch, "E3714", {"start": v(284.96, -90.83) * mm, "end": v(269.93, -90.83) * mm});
            skFitSpline(sketch, "E3715", {"points": [v(201.93, -90.83) * mm, v(200.34, -90.83) * mm, v(198.81, -91.46) * mm, v(197.69, -92.6) * mm]});
            skLineSegment(sketch, "E3716", {"start": v(265.69, -92.6) * mm, "end": v(251.2, -107.08) * mm});
            skFitSpline(sketch, "E3717", {"points": [v(178.96, -108.83) * mm, v(180.55, -108.83) * mm, v(182.08, -108.2) * mm, v(183.2, -107.08) * mm]});
            skLineSegment(sketch, "E3718", {"start": v(246.96, -108.83) * mm, "end": v(229.93, -108.83) * mm});
            skFitSpline(sketch, "E3719", {"points": [v(157.69, -107.08) * mm, v(158.81, -108.2) * mm, v(160.34, -108.83) * mm, v(161.93, -108.83) * mm]});
            skLineSegment(sketch, "E3720", {"start": v(225.69, -107.08) * mm, "end": v(211.2, -92.6) * mm});
            skFitSpline(sketch, "E3721", {"points": [v(279.45, 58.03) * mm, v(279.45, 60.7) * mm, v(277.84, 63.1) * mm, v(275.37, 64.13) * mm]});
            skFitSpline(sketch, "E3722", {"points": [v(275.37, 64.13) * mm, v(272.9, 65.15) * mm, v(270.07, 64.59) * mm, v(268.18, 62.7) * mm]});
            skLineSegment(sketch, "E3723", {"start": v(206.96, -90.83) * mm, "end": v(201.93, -90.83) * mm});
            skFitSpline(sketch, "E3724", {"points": [v(268.18, -64.37) * mm, v(270.07, -66.25) * mm, v(272.9, -66.82) * mm, v(275.37, -65.8) * mm]});
            skFitSpline(sketch, "E3725", {"points": [v(275.37, -65.8) * mm, v(277.84, -64.78) * mm, v(279.45, -62.37) * mm, v(279.45, -59.7) * mm]});
            skLineSegment(sketch, "E3726", {"start": v(197.69, -92.6) * mm, "end": v(183.2, -107.08) * mm});
            skFitSpline(sketch, "E3727", {"points": [v(235.45, -28.9) * mm, v(235.45, -30.65) * mm, v(236.14, -32.33) * mm, v(237.38, -33.57) * mm]});
            skLineSegment(sketch, "E3728", {"start": v(178.96, -108.83) * mm, "end": v(161.93, -108.83) * mm});
            skFitSpline(sketch, "E3729", {"points": [v(237.38, 31.9) * mm, v(236.14, 30.66) * mm, v(235.45, 28.98) * mm, v(235.45, 27.23) * mm]});
            skLineSegment(sketch, "E3730", {"start": v(237.38, 31.9) * mm, "end": v(268.18, 62.7) * mm});
            skFitSpline(sketch, "E3731", {"points": [v(179.45, -58.35) * mm, v(179.45, -59.94) * mm, v(180.08, -61.47) * mm, v(181.2, -62.6) * mm]});
            skLineSegment(sketch, "E3732", {"start": v(279.45, 58.03) * mm, "end": v(279.45, -59.7) * mm});
            skFitSpline(sketch, "E3733", {"points": [v(181.2, -39.08) * mm, v(180.08, -40.2) * mm, v(179.45, -41.73) * mm, v(179.45, -43.32) * mm]});
            skLineSegment(sketch, "E3734", {"start": v(268.18, -64.37) * mm, "end": v(237.38, -33.57) * mm});
            skFitSpline(sketch, "E3735", {"points": [v(201.93, -20.83) * mm, v(200.34, -20.83) * mm, v(198.81, -21.47) * mm, v(197.69, -22.6) * mm]});
            skLineSegment(sketch, "E3736", {"start": v(235.45, -28.9) * mm, "end": v(235.45, 27.23) * mm});
            skFitSpline(sketch, "E3737", {"points": [v(211.2, -22.6) * mm, v(210.08, -21.47) * mm, v(208.55, -20.83) * mm, v(206.96, -20.83) * mm]});
            skLineSegment(sketch, "E3738", {"start": v(197.69, -79.08) * mm, "end": v(181.2, -62.6) * mm});
            skFitSpline(sketch, "E3739", {"points": [v(229.45, -43.32) * mm, v(229.45, -41.73) * mm, v(228.81, -40.2) * mm, v(227.69, -39.08) * mm]});
            skLineSegment(sketch, "E3740", {"start": v(179.45, -58.35) * mm, "end": v(179.45, -43.32) * mm});
            skFitSpline(sketch, "E3741", {"points": [v(227.69, -62.6) * mm, v(228.81, -61.47) * mm, v(229.45, -59.94) * mm, v(229.45, -58.35) * mm]});
            skLineSegment(sketch, "E3742", {"start": v(181.2, -39.08) * mm, "end": v(197.69, -22.6) * mm});
            skFitSpline(sketch, "E3743", {"points": [v(206.96, -80.83) * mm, v(208.55, -80.83) * mm, v(210.08, -80.2) * mm, v(211.2, -79.08) * mm]});
            skLineSegment(sketch, "E3744", {"start": v(201.93, -20.83) * mm, "end": v(206.96, -20.83) * mm});
            skFitSpline(sketch, "E3745", {"points": [v(197.69, -79.08) * mm, v(198.81, -80.2) * mm, v(200.34, -80.83) * mm, v(201.93, -80.83) * mm]});
            skLineSegment(sketch, "E3746", {"start": v(211.2, -22.6) * mm, "end": v(227.69, -39.08) * mm});
            skFitSpline(sketch, "E3747", {"points": [v(206.96, 19.17) * mm, v(208.55, 19.17) * mm, v(210.08, 19.8) * mm, v(211.2, 20.92) * mm]});
            skLineSegment(sketch, "E3748", {"start": v(229.45, -43.32) * mm, "end": v(229.45, -58.35) * mm});
            skFitSpline(sketch, "E3749", {"points": [v(197.69, 20.92) * mm, v(198.81, 19.8) * mm, v(200.34, 19.17) * mm, v(201.93, 19.17) * mm]});
            skLineSegment(sketch, "E3750", {"start": v(227.69, -62.6) * mm, "end": v(211.2, -79.08) * mm});
            skFitSpline(sketch, "E3751", {"points": [v(179.45, 41.65) * mm, v(179.45, 40.06) * mm, v(180.08, 38.53) * mm, v(181.2, 37.4) * mm]});
            skFitSpline(sketch, "E3752", {"points": [v(227.69, 37.4) * mm, v(228.81, 38.53) * mm, v(229.45, 40.06) * mm, v(229.45, 41.65) * mm]});
            skLineSegment(sketch, "E3753", {"start": v(206.96, -80.83) * mm, "end": v(201.93, -80.83) * mm});
            skLineSegment(sketch, "E3754", {"start": v(227.69, 37.4) * mm, "end": v(211.2, 20.92) * mm});
            skFitSpline(sketch, "E3755", {"points": [v(181.06, -90.58) * mm, v(180.97, -90.43) * mm, v(180.8, -90.33) * mm, v(180.63, -90.33) * mm]});
            skFitSpline(sketch, "E3756", {"points": [v(181.06, -90.58) * mm, v(181.17, -90.76) * mm, v(181.38, -90.86) * mm, v(181.58, -90.83) * mm]});
            skFitSpline(sketch, "E3757", {"points": [v(181.58, -90.83) * mm, v(181.8, -90.79) * mm, v(181.95, -90.63) * mm, v(181.99, -90.42) * mm]});
            skFitSpline(sketch, "E3758", {"points": [v(181.99, -90.42) * mm, v(182.03, -90.21) * mm, v(181.93, -90) * mm, v(181.75, -89.9) * mm]});
            skFitSpline(sketch, "E3759", {"points": [v(181.5, -89.47) * mm, v(181.5, -89.65) * mm, v(181.6, -89.81) * mm, v(181.75, -89.9) * mm]});
            skLineSegment(sketch, "E3760", {"start": v(206.96, 19.17) * mm, "end": v(201.93, 19.17) * mm});
            skFitSpline(sketch, "E3761", {"points": [v(181.75, -81.77) * mm, v(181.6, -81.86) * mm, v(181.5, -82.02) * mm, v(181.5, -82.2) * mm]});
            skFitSpline(sketch, "E3762", {"points": [v(181.75, -81.77) * mm, v(181.93, -81.66) * mm, v(182.03, -81.45) * mm, v(181.99, -81.25) * mm]});
            skFitSpline(sketch, "E3763", {"points": [v(181.99, -81.25) * mm, v(181.95, -81.04) * mm, v(181.8, -80.88) * mm, v(181.58, -80.84) * mm]});
            skFitSpline(sketch, "E3764", {"points": [v(181.58, -80.84) * mm, v(181.38, -80.8) * mm, v(181.17, -80.9) * mm, v(181.06, -81.08) * mm]});
            skFitSpline(sketch, "E3765", {"points": [v(180.63, -81.33) * mm, v(180.8, -81.33) * mm, v(180.97, -81.24) * mm, v(181.06, -81.08) * mm]});
            skLineSegment(sketch, "E3766", {"start": v(197.69, 20.92) * mm, "end": v(181.2, 37.4) * mm});
            skFitSpline(sketch, "E3767", {"points": [v(157.83, -81.08) * mm, v(157.92, -81.24) * mm, v(158.08, -81.33) * mm, v(158.26, -81.33) * mm]});
            skFitSpline(sketch, "E3768", {"points": [v(157.83, -81.08) * mm, v(157.72, -80.9) * mm, v(157.52, -80.8) * mm, v(157.3, -80.84) * mm]});
            skFitSpline(sketch, "E3769", {"points": [v(157.3, -80.84) * mm, v(157.1, -80.88) * mm, v(156.94, -81.04) * mm, v(156.9, -81.25) * mm]});
            skFitSpline(sketch, "E3770", {"points": [v(156.9, -81.25) * mm, v(156.87, -81.45) * mm, v(156.96, -81.66) * mm, v(157.15, -81.77) * mm]});
            skFitSpline(sketch, "E3771", {"points": [v(157.4, -82.2) * mm, v(157.4, -82.02) * mm, v(157.3, -81.86) * mm, v(157.15, -81.77) * mm]});
            skLineSegment(sketch, "E3772", {"start": v(251.5, -89.47) * mm, "end": v(251.5, -82.2) * mm});
            skFitSpline(sketch, "E3773", {"points": [v(157.15, -89.9) * mm, v(157.3, -89.81) * mm, v(157.4, -89.65) * mm, v(157.4, -89.47) * mm]});
            skFitSpline(sketch, "E3774", {"points": [v(157.15, -89.9) * mm, v(156.96, -90) * mm, v(156.87, -90.21) * mm, v(156.9, -90.42) * mm]});
            skFitSpline(sketch, "E3775", {"points": [v(156.9, -90.42) * mm, v(156.94, -90.63) * mm, v(157.1, -90.79) * mm, v(157.3, -90.83) * mm]});
            skFitSpline(sketch, "E3776", {"points": [v(157.3, -90.83) * mm, v(157.52, -90.86) * mm, v(157.72, -90.76) * mm, v(157.83, -90.58) * mm]});
            skFitSpline(sketch, "E3777", {"points": [v(158.26, -90.33) * mm, v(158.08, -90.33) * mm, v(157.92, -90.43) * mm, v(157.83, -90.58) * mm]});
            skFitSpline(sketch, "E3778", {"points": [v(310.55, -105.33) * mm, v(310.55, -104.76) * mm, v(310.24, -104.23) * mm, v(309.75, -103.95) * mm]});
            skFitSpline(sketch, "E3779", {"points": [v(309.75, -103.95) * mm, v(309.25, -103.66) * mm, v(308.64, -103.66) * mm, v(308.15, -103.95) * mm]});
            skFitSpline(sketch, "E3780", {"points": [v(308.15, -103.95) * mm, v(307.65, -104.23) * mm, v(307.35, -104.76) * mm, v(307.35, -105.33) * mm]});
            skFitSpline(sketch, "E3781", {"points": [v(307.35, -105.33) * mm, v(307.35, -105.9) * mm, v(307.65, -106.43) * mm, v(308.15, -106.72) * mm]});
            skFitSpline(sketch, "E3782", {"points": [v(308.15, -106.72) * mm, v(308.64, -107) * mm, v(309.25, -107) * mm, v(309.75, -106.72) * mm]});
            skFitSpline(sketch, "E3783", {"points": [v(309.75, -106.72) * mm, v(310.24, -106.43) * mm, v(310.55, -105.9) * mm, v(310.55, -105.33) * mm]});
            skLineSegment(sketch, "E3784", {"start": v(158.26, -90.33) * mm, "end": v(180.63, -90.33) * mm});
            skFitSpline(sketch, "E3785", {"points": [v(101.55, -105.33) * mm, v(101.55, -104.76) * mm, v(101.24, -104.23) * mm, v(100.75, -103.95) * mm]});
            skFitSpline(sketch, "E3786", {"points": [v(100.75, -103.95) * mm, v(100.25, -103.66) * mm, v(99.64, -103.66) * mm, v(99.15, -103.95) * mm]});
            skFitSpline(sketch, "E3787", {"points": [v(99.15, -103.95) * mm, v(98.65, -104.23) * mm, v(98.35, -104.76) * mm, v(98.35, -105.33) * mm]});
            skFitSpline(sketch, "E3788", {"points": [v(98.35, -105.33) * mm, v(98.35, -105.9) * mm, v(98.65, -106.43) * mm, v(99.15, -106.72) * mm]});
            skFitSpline(sketch, "E3789", {"points": [v(99.15, -106.72) * mm, v(99.64, -107) * mm, v(100.25, -107) * mm, v(100.75, -106.72) * mm]});
            skFitSpline(sketch, "E3790", {"points": [v(100.75, -106.72) * mm, v(101.24, -106.43) * mm, v(101.55, -105.9) * mm, v(101.55, -105.33) * mm]});
            skLineSegment(sketch, "E3791", {"start": v(181.5, -89.47) * mm, "end": v(181.5, -82.2) * mm});
            skFitSpline(sketch, "E3792", {"points": [v(241.05, -100.83) * mm, v(241.05, -100.26) * mm, v(240.74, -99.73) * mm, v(240.25, -99.45) * mm]});
            skFitSpline(sketch, "E3793", {"points": [v(240.25, -99.45) * mm, v(239.75, -99.16) * mm, v(239.14, -99.16) * mm, v(238.65, -99.45) * mm]});
            skFitSpline(sketch, "E3794", {"points": [v(238.65, -99.45) * mm, v(238.15, -99.73) * mm, v(237.85, -100.26) * mm, v(237.85, -100.83) * mm]});
            skFitSpline(sketch, "E3795", {"points": [v(237.85, -100.83) * mm, v(237.85, -101.4) * mm, v(238.15, -101.93) * mm, v(238.65, -102.22) * mm]});
            skFitSpline(sketch, "E3796", {"points": [v(238.65, -102.22) * mm, v(239.14, -102.5) * mm, v(239.75, -102.5) * mm, v(240.25, -102.22) * mm]});
            skFitSpline(sketch, "E3797", {"points": [v(240.25, -102.22) * mm, v(240.74, -101.93) * mm, v(241.05, -101.4) * mm, v(241.05, -100.83) * mm]});
            skLineSegment(sketch, "E3798", {"start": v(180.63, -81.33) * mm, "end": v(158.26, -81.33) * mm});
            skFitSpline(sketch, "E3799", {"points": [v(171.05, -100.83) * mm, v(171.05, -100.26) * mm, v(170.74, -99.73) * mm, v(170.25, -99.45) * mm]});
            skFitSpline(sketch, "E3800", {"points": [v(170.25, -99.45) * mm, v(169.75, -99.16) * mm, v(169.14, -99.16) * mm, v(168.65, -99.45) * mm]});
            skFitSpline(sketch, "E3801", {"points": [v(168.65, -99.45) * mm, v(168.15, -99.73) * mm, v(167.85, -100.26) * mm, v(167.85, -100.83) * mm]});
            skFitSpline(sketch, "E3802", {"points": [v(167.85, -100.83) * mm, v(167.85, -101.4) * mm, v(168.15, -101.93) * mm, v(168.65, -102.22) * mm]});
            skFitSpline(sketch, "E3803", {"points": [v(168.65, -102.22) * mm, v(169.14, -102.5) * mm, v(169.75, -102.5) * mm, v(170.25, -102.22) * mm]});
            skFitSpline(sketch, "E3804", {"points": [v(170.25, -102.22) * mm, v(170.74, -101.93) * mm, v(171.05, -101.4) * mm, v(171.05, -100.83) * mm]});
            skLineSegment(sketch, "E3805", {"start": v(157.4, -82.2) * mm, "end": v(157.4, -89.47) * mm});
            skFitSpline(sketch, "E3806", {"points": [v(241.05, -70.83) * mm, v(241.05, -70.26) * mm, v(240.74, -69.73) * mm, v(240.25, -69.45) * mm]});
            skFitSpline(sketch, "E3807", {"points": [v(240.25, -69.45) * mm, v(239.75, -69.16) * mm, v(239.14, -69.16) * mm, v(238.65, -69.45) * mm]});
            skFitSpline(sketch, "E3808", {"points": [v(238.65, -69.45) * mm, v(238.15, -69.73) * mm, v(237.85, -70.26) * mm, v(237.85, -70.83) * mm]});
            skFitSpline(sketch, "E3809", {"points": [v(237.85, -70.83) * mm, v(237.85, -71.4) * mm, v(238.15, -71.93) * mm, v(238.65, -72.22) * mm]});
            skFitSpline(sketch, "E3810", {"points": [v(238.65, -72.22) * mm, v(239.14, -72.5) * mm, v(239.75, -72.5) * mm, v(240.25, -72.22) * mm]});
            skFitSpline(sketch, "E3811", {"points": [v(240.25, -72.22) * mm, v(240.74, -71.93) * mm, v(241.05, -71.4) * mm, v(241.05, -70.83) * mm]});
            skLineSegment(sketch, "E3812", {"start": v(310.55, -105.33) * mm, "end": v(310.55, -105.33) * mm});
            skFitSpline(sketch, "E3813", {"points": [v(171.05, -70.83) * mm, v(171.05, -70.26) * mm, v(170.74, -69.73) * mm, v(170.25, -69.45) * mm]});
            skFitSpline(sketch, "E3814", {"points": [v(170.25, -69.45) * mm, v(169.75, -69.16) * mm, v(169.14, -69.16) * mm, v(168.65, -69.45) * mm]});
            skFitSpline(sketch, "E3815", {"points": [v(168.65, -69.45) * mm, v(168.15, -69.73) * mm, v(167.85, -70.26) * mm, v(167.85, -70.83) * mm]});
            skFitSpline(sketch, "E3816", {"points": [v(167.85, -70.83) * mm, v(167.85, -71.4) * mm, v(168.15, -71.93) * mm, v(168.65, -72.22) * mm]});
            skFitSpline(sketch, "E3817", {"points": [v(168.65, -72.22) * mm, v(169.14, -72.5) * mm, v(169.75, -72.5) * mm, v(170.25, -72.22) * mm]});
            skFitSpline(sketch, "E3818", {"points": [v(170.25, -72.22) * mm, v(170.74, -71.93) * mm, v(171.05, -71.4) * mm, v(171.05, -70.83) * mm]});
            skFitSpline(sketch, "E3819", {"points": [v(223.55, -12.83) * mm, v(223.55, -12.26) * mm, v(223.24, -11.73) * mm, v(222.75, -11.45) * mm]});
            skFitSpline(sketch, "E3820", {"points": [v(222.75, -11.45) * mm, v(222.25, -11.16) * mm, v(221.64, -11.16) * mm, v(221.15, -11.45) * mm]});
            skFitSpline(sketch, "E3821", {"points": [v(221.15, -11.45) * mm, v(220.65, -11.73) * mm, v(220.35, -12.26) * mm, v(220.35, -12.83) * mm]});
            skFitSpline(sketch, "E3822", {"points": [v(220.35, -12.83) * mm, v(220.35, -13.4) * mm, v(220.65, -13.93) * mm, v(221.15, -14.22) * mm]});
            skFitSpline(sketch, "E3823", {"points": [v(221.15, -14.22) * mm, v(221.64, -14.5) * mm, v(222.25, -14.5) * mm, v(222.75, -14.22) * mm]});
            skFitSpline(sketch, "E3824", {"points": [v(222.75, -14.22) * mm, v(223.24, -13.93) * mm, v(223.55, -13.4) * mm, v(223.55, -12.83) * mm]});
            skFitSpline(sketch, "E3825", {"points": [v(188.55, -0.83) * mm, v(188.55, -0.26) * mm, v(188.24, 0.27) * mm, v(187.75, 0.55) * mm]});
            skFitSpline(sketch, "E3826", {"points": [v(187.75, 0.55) * mm, v(187.25, 0.84) * mm, v(186.64, 0.84) * mm, v(186.15, 0.55) * mm]});
            skFitSpline(sketch, "E3827", {"points": [v(186.15, 0.55) * mm, v(185.65, 0.27) * mm, v(185.35, -0.26) * mm, v(185.35, -0.83) * mm]});
            skFitSpline(sketch, "E3828", {"points": [v(185.35, -0.83) * mm, v(185.35, -1.4) * mm, v(185.65, -1.93) * mm, v(186.15, -2.22) * mm]});
            skFitSpline(sketch, "E3829", {"points": [v(186.15, -2.22) * mm, v(186.64, -2.5) * mm, v(187.25, -2.5) * mm, v(187.75, -2.22) * mm]});
            skFitSpline(sketch, "E3830", {"points": [v(187.75, -2.22) * mm, v(188.24, -1.93) * mm, v(188.55, -1.4) * mm, v(188.55, -0.83) * mm]});
            skFitSpline(sketch, "E3831", {"points": [v(223.55, 11.17) * mm, v(223.55, 11.74) * mm, v(223.24, 12.27) * mm, v(222.75, 12.55) * mm]});
            skFitSpline(sketch, "E3832", {"points": [v(222.75, 12.55) * mm, v(222.25, 12.84) * mm, v(221.64, 12.84) * mm, v(221.15, 12.55) * mm]});
            skFitSpline(sketch, "E3833", {"points": [v(221.15, 12.55) * mm, v(220.65, 12.27) * mm, v(220.35, 11.74) * mm, v(220.35, 11.17) * mm]});
            skFitSpline(sketch, "E3834", {"points": [v(220.35, 11.17) * mm, v(220.35, 10.6) * mm, v(220.65, 10.07) * mm, v(221.15, 9.78) * mm]});
            skFitSpline(sketch, "E3835", {"points": [v(221.15, 9.78) * mm, v(221.64, 9.5) * mm, v(222.25, 9.5) * mm, v(222.75, 9.78) * mm]});
            skFitSpline(sketch, "E3836", {"points": [v(222.75, 9.78) * mm, v(223.24, 10.07) * mm, v(223.55, 10.6) * mm, v(223.55, 11.17) * mm]});
            skFitSpline(sketch, "E3837", {"points": [v(310.55, 103.67) * mm, v(310.55, 104.24) * mm, v(310.24, 104.77) * mm, v(309.75, 105.05) * mm]});
            skFitSpline(sketch, "E3838", {"points": [v(309.75, 105.05) * mm, v(309.25, 105.34) * mm, v(308.64, 105.34) * mm, v(308.15, 105.05) * mm]});
            skFitSpline(sketch, "E3839", {"points": [v(308.15, 105.05) * mm, v(307.65, 104.77) * mm, v(307.35, 104.24) * mm, v(307.35, 103.67) * mm]});
            skFitSpline(sketch, "E3840", {"points": [v(307.35, 103.67) * mm, v(307.35, 103.1) * mm, v(307.65, 102.57) * mm, v(308.15, 102.28) * mm]});
            skFitSpline(sketch, "E3841", {"points": [v(308.15, 102.28) * mm, v(308.64, 102) * mm, v(309.25, 102) * mm, v(309.75, 102.28) * mm]});
            skFitSpline(sketch, "E3842", {"points": [v(309.75, 102.28) * mm, v(310.24, 102.57) * mm, v(310.55, 103.1) * mm, v(310.55, 103.67) * mm]});
            skFitSpline(sketch, "E3843", {"points": [v(101.55, 103.67) * mm, v(101.55, 104.24) * mm, v(101.24, 104.77) * mm, v(100.75, 105.05) * mm]});
            skFitSpline(sketch, "E3844", {"points": [v(100.75, 105.05) * mm, v(100.25, 105.34) * mm, v(99.64, 105.34) * mm, v(99.15, 105.05) * mm]});
            skFitSpline(sketch, "E3845", {"points": [v(99.15, 105.05) * mm, v(98.65, 104.77) * mm, v(98.35, 104.24) * mm, v(98.35, 103.67) * mm]});
            skFitSpline(sketch, "E3846", {"points": [v(98.35, 103.67) * mm, v(98.35, 103.1) * mm, v(98.65, 102.57) * mm, v(99.15, 102.28) * mm]});
            skFitSpline(sketch, "E3847", {"points": [v(99.15, 102.28) * mm, v(99.64, 102) * mm, v(100.25, 102) * mm, v(100.75, 102.28) * mm]});
            skFitSpline(sketch, "E3848", {"points": [v(100.75, 102.28) * mm, v(101.24, 102.57) * mm, v(101.55, 103.1) * mm, v(101.55, 103.67) * mm]});
            skFitSpline(sketch, "E3849", {"points": [v(251.06, -90.58) * mm, v(250.97, -90.43) * mm, v(250.8, -90.33) * mm, v(250.63, -90.33) * mm]});
            skFitSpline(sketch, "E3850", {"points": [v(251.06, -90.58) * mm, v(251.17, -90.76) * mm, v(251.38, -90.86) * mm, v(251.58, -90.83) * mm]});
            skFitSpline(sketch, "E3851", {"points": [v(251.58, -90.83) * mm, v(251.79, -90.79) * mm, v(251.95, -90.63) * mm, v(251.99, -90.42) * mm]});
            skFitSpline(sketch, "E3852", {"points": [v(251.99, -90.42) * mm, v(252.02, -90.21) * mm, v(251.93, -90) * mm, v(251.75, -89.9) * mm]});
            skFitSpline(sketch, "E3853", {"points": [v(251.5, -89.47) * mm, v(251.5, -89.65) * mm, v(251.6, -89.81) * mm, v(251.75, -89.9) * mm]});
            skFitSpline(sketch, "E3854", {"points": [v(251.75, -81.77) * mm, v(251.6, -81.86) * mm, v(251.5, -82.02) * mm, v(251.5, -82.2) * mm]});
            skFitSpline(sketch, "E3855", {"points": [v(251.75, -81.77) * mm, v(251.93, -81.66) * mm, v(252.02, -81.45) * mm, v(251.99, -81.25) * mm]});
            skFitSpline(sketch, "E3856", {"points": [v(251.99, -81.25) * mm, v(251.95, -81.04) * mm, v(251.79, -80.88) * mm, v(251.58, -80.84) * mm]});
            skFitSpline(sketch, "E3857", {"points": [v(251.58, -80.84) * mm, v(251.38, -80.8) * mm, v(251.17, -80.9) * mm, v(251.06, -81.08) * mm]});
            skFitSpline(sketch, "E3858", {"points": [v(250.63, -81.33) * mm, v(250.8, -81.33) * mm, v(250.97, -81.24) * mm, v(251.06, -81.08) * mm]});
            skFitSpline(sketch, "E3859", {"points": [v(227.83, -81.08) * mm, v(227.92, -81.24) * mm, v(228.08, -81.33) * mm, v(228.26, -81.33) * mm]});
            skFitSpline(sketch, "E3860", {"points": [v(227.83, -81.08) * mm, v(227.72, -80.9) * mm, v(227.52, -80.8) * mm, v(227.3, -80.84) * mm]});
            skFitSpline(sketch, "E3861", {"points": [v(227.3, -80.84) * mm, v(227.1, -80.88) * mm, v(226.94, -81.04) * mm, v(226.9, -81.25) * mm]});
            skFitSpline(sketch, "E3862", {"points": [v(226.9, -81.25) * mm, v(226.87, -81.45) * mm, v(226.96, -81.66) * mm, v(227.15, -81.77) * mm]});
            skFitSpline(sketch, "E3863", {"points": [v(227.4, -82.2) * mm, v(227.4, -82.02) * mm, v(227.3, -81.86) * mm, v(227.15, -81.77) * mm]});
            skLineSegment(sketch, "E3864", {"start": v(310.55, 103.67) * mm, "end": v(310.55, 103.67) * mm});
            skFitSpline(sketch, "E3865", {"points": [v(227.15, -89.9) * mm, v(227.3, -89.81) * mm, v(227.4, -89.65) * mm, v(227.4, -89.47) * mm]});
            skFitSpline(sketch, "E3866", {"points": [v(227.15, -89.9) * mm, v(226.96, -90) * mm, v(226.87, -90.21) * mm, v(226.9, -90.42) * mm]});
            skFitSpline(sketch, "E3867", {"points": [v(226.9, -90.42) * mm, v(226.94, -90.63) * mm, v(227.1, -90.79) * mm, v(227.3, -90.83) * mm]});
            skFitSpline(sketch, "E3868", {"points": [v(227.3, -90.83) * mm, v(227.52, -90.86) * mm, v(227.72, -90.76) * mm, v(227.83, -90.58) * mm]});
            skFitSpline(sketch, "E3869", {"points": [v(228.26, -90.33) * mm, v(228.08, -90.33) * mm, v(227.92, -90.43) * mm, v(227.83, -90.58) * mm]});
            skFitSpline(sketch, "E3870", {"points": [v(206.05, -12.83) * mm, v(206.05, -12.26) * mm, v(205.74, -11.73) * mm, v(205.25, -11.45) * mm]});
            skFitSpline(sketch, "E3871", {"points": [v(205.25, -11.45) * mm, v(204.75, -11.16) * mm, v(204.14, -11.16) * mm, v(203.65, -11.45) * mm]});
            skFitSpline(sketch, "E3872", {"points": [v(203.65, -11.45) * mm, v(203.15, -11.73) * mm, v(202.85, -12.26) * mm, v(202.85, -12.83) * mm]});
            skFitSpline(sketch, "E3873", {"points": [v(202.85, -12.83) * mm, v(202.85, -13.4) * mm, v(203.15, -13.93) * mm, v(203.65, -14.22) * mm]});
            skFitSpline(sketch, "E3874", {"points": [v(203.65, -14.22) * mm, v(204.14, -14.5) * mm, v(204.75, -14.5) * mm, v(205.25, -14.22) * mm]});
            skFitSpline(sketch, "E3875", {"points": [v(205.25, -14.22) * mm, v(205.74, -13.93) * mm, v(206.05, -13.4) * mm, v(206.05, -12.83) * mm]});
            skFitSpline(sketch, "E3876", {"points": [v(206.05, 11.17) * mm, v(206.05, 11.74) * mm, v(205.74, 12.27) * mm, v(205.25, 12.55) * mm]});
            skFitSpline(sketch, "E3877", {"points": [v(205.25, 12.55) * mm, v(204.75, 12.84) * mm, v(204.14, 12.84) * mm, v(203.65, 12.55) * mm]});
            skFitSpline(sketch, "E3878", {"points": [v(203.65, 12.55) * mm, v(203.15, 12.27) * mm, v(202.85, 11.74) * mm, v(202.85, 11.17) * mm]});
            skFitSpline(sketch, "E3879", {"points": [v(202.85, 11.17) * mm, v(202.85, 10.6) * mm, v(203.15, 10.07) * mm, v(203.65, 9.78) * mm]});
            skFitSpline(sketch, "E3880", {"points": [v(203.65, 9.78) * mm, v(204.14, 9.5) * mm, v(204.75, 9.5) * mm, v(205.25, 9.78) * mm]});
            skFitSpline(sketch, "E3881", {"points": [v(205.25, 9.78) * mm, v(205.74, 10.07) * mm, v(206.05, 10.6) * mm, v(206.05, 11.17) * mm]});
            skLineSegment(sketch, "E3882", {"start": v(228.26, -90.33) * mm, "end": v(250.63, -90.33) * mm});
            skFitSpline(sketch, "E3883", {"points": [v(173.45, 27.23) * mm, v(173.45, 28.98) * mm, v(172.75, 30.66) * mm, v(171.51, 31.9) * mm]});
            skLineSegment(sketch, "E3884", {"start": v(250.63, -81.33) * mm, "end": v(228.26, -81.33) * mm});
            skFitSpline(sketch, "E3885", {"points": [v(171.51, -33.57) * mm, v(172.75, -32.33) * mm, v(173.45, -30.65) * mm, v(173.45, -28.9) * mm]});
            skFitSpline(sketch, "E3886", {"points": [v(140.71, 62.7) * mm, v(138.83, 64.59) * mm, v(135.99, 65.15) * mm, v(133.52, 64.13) * mm]});
            skFitSpline(sketch, "E3887", {"points": [v(133.52, 64.13) * mm, v(131.06, 63.1) * mm, v(129.45, 60.7) * mm, v(129.45, 58.03) * mm]});
            skFitSpline(sketch, "E3888", {"points": [v(129.45, -59.7) * mm, v(129.45, -62.37) * mm, v(131.06, -64.78) * mm, v(133.52, -65.8) * mm]});
            skFitSpline(sketch, "E3889", {"points": [v(133.52, -65.8) * mm, v(135.99, -66.82) * mm, v(138.83, -66.25) * mm, v(140.71, -64.37) * mm]});
            skLineSegment(sketch, "E3890", {"start": v(227.4, -82.2) * mm, "end": v(227.4, -89.47) * mm});
            skLineSegment(sketch, "E3891", {"start": v(173.45, 27.23) * mm, "end": v(173.45, -28.9) * mm});
            skFitSpline(sketch, "E3892", {"points": [v(138.96, 89.17) * mm, v(140.55, 89.17) * mm, v(142.08, 89.8) * mm, v(143.2, 90.92) * mm]});
            skFitSpline(sketch, "E3893", {"points": [v(265.69, 90.92) * mm, v(266.81, 89.8) * mm, v(268.34, 89.17) * mm, v(269.93, 89.17) * mm]});
            skLineSegment(sketch, "E3894", {"start": v(171.51, -33.57) * mm, "end": v(140.71, -64.37) * mm});
            skFitSpline(sketch, "E3895", {"points": [v(251.2, 105.4) * mm, v(250.08, 106.53) * mm, v(248.55, 107.17) * mm, v(246.96, 107.17) * mm]});
            skLineSegment(sketch, "E3896", {"start": v(140.71, 62.7) * mm, "end": v(171.51, 31.9) * mm});
            skFitSpline(sketch, "E3897", {"points": [v(229.93, 107.17) * mm, v(228.34, 107.17) * mm, v(226.81, 106.53) * mm, v(225.69, 105.4) * mm]});
            skLineSegment(sketch, "E3898", {"start": v(129.45, -59.7) * mm, "end": v(129.45, 58.03) * mm});
            skFitSpline(sketch, "E3899", {"points": [v(206.96, 89.17) * mm, v(208.55, 89.17) * mm, v(210.08, 89.8) * mm, v(211.2, 90.92) * mm]});
            skLineSegment(sketch, "E3900", {"start": v(157.69, 105.4) * mm, "end": v(143.2, 90.92) * mm});
            skFitSpline(sketch, "E3901", {"points": [v(197.69, 90.92) * mm, v(198.81, 89.8) * mm, v(200.34, 89.17) * mm, v(201.93, 89.17) * mm]});
            skLineSegment(sketch, "E3902", {"start": v(265.69, 90.92) * mm, "end": v(251.2, 105.4) * mm});
            skFitSpline(sketch, "E3903", {"points": [v(183.2, 105.4) * mm, v(182.08, 106.53) * mm, v(180.55, 107.17) * mm, v(178.96, 107.17) * mm]});
            skLineSegment(sketch, "E3904", {"start": v(246.96, 107.17) * mm, "end": v(229.93, 107.17) * mm});
            skFitSpline(sketch, "E3905", {"points": [v(161.93, 107.17) * mm, v(160.34, 107.17) * mm, v(158.81, 106.53) * mm, v(157.69, 105.4) * mm]});
            skFitSpline(sketch, "E3906", {"points": [v(211.2, 77.4) * mm, v(210.08, 78.53) * mm, v(208.55, 79.17) * mm, v(206.96, 79.17) * mm]});
            skLineSegment(sketch, "E3907", {"start": v(225.69, 105.4) * mm, "end": v(211.2, 90.92) * mm});
            skFitSpline(sketch, "E3908", {"points": [v(201.93, 79.17) * mm, v(200.34, 79.17) * mm, v(198.81, 78.53) * mm, v(197.69, 77.4) * mm]});
            skLineSegment(sketch, "E3909", {"start": v(206.96, 89.17) * mm, "end": v(201.93, 89.17) * mm});
            skLineSegment(sketch, "E3910", {"start": v(197.69, 90.92) * mm, "end": v(183.2, 105.4) * mm});
            skFitSpline(sketch, "E3911", {"points": [v(180.63, 88.67) * mm, v(180.8, 88.67) * mm, v(180.97, 88.76) * mm, v(181.06, 88.92) * mm]});
            skFitSpline(sketch, "E3912", {"points": [v(181.75, 88.23) * mm, v(181.93, 88.34) * mm, v(182.03, 88.55) * mm, v(181.99, 88.75) * mm]});
            skFitSpline(sketch, "E3913", {"points": [v(181.99, 88.75) * mm, v(181.95, 88.96) * mm, v(181.8, 89.12) * mm, v(181.58, 89.16) * mm]});
            skFitSpline(sketch, "E3914", {"points": [v(181.58, 89.16) * mm, v(181.38, 89.2) * mm, v(181.17, 89.1) * mm, v(181.06, 88.92) * mm]});
            skFitSpline(sketch, "E3915", {"points": [v(181.75, 88.23) * mm, v(181.6, 88.14) * mm, v(181.5, 87.98) * mm, v(181.5, 87.8) * mm]});
            skLineSegment(sketch, "E3916", {"start": v(178.96, 107.17) * mm, "end": v(161.93, 107.17) * mm});
            skFitSpline(sketch, "E3917", {"points": [v(181.5, 80.53) * mm, v(181.5, 80.35) * mm, v(181.6, 80.19) * mm, v(181.75, 80.1) * mm]});
            skFitSpline(sketch, "E3918", {"points": [v(181.06, 79.42) * mm, v(181.17, 79.23) * mm, v(181.38, 79.14) * mm, v(181.58, 79.17) * mm]});
            skFitSpline(sketch, "E3919", {"points": [v(181.58, 79.17) * mm, v(181.8, 79.2) * mm, v(181.95, 79.37) * mm, v(181.99, 79.58) * mm]});
            skFitSpline(sketch, "E3920", {"points": [v(181.99, 79.58) * mm, v(182.03, 79.79) * mm, v(181.93, 80) * mm, v(181.75, 80.1) * mm]});
            skFitSpline(sketch, "E3921", {"points": [v(181.06, 79.42) * mm, v(180.97, 79.57) * mm, v(180.8, 79.67) * mm, v(180.63, 79.67) * mm]});
            skLineSegment(sketch, "E3922", {"start": v(206.96, 79.17) * mm, "end": v(201.93, 79.17) * mm});
            skFitSpline(sketch, "E3923", {"points": [v(158.26, 79.67) * mm, v(158.08, 79.67) * mm, v(157.92, 79.57) * mm, v(157.83, 79.42) * mm]});
            skFitSpline(sketch, "E3924", {"points": [v(157.15, 80.1) * mm, v(156.96, 80) * mm, v(156.87, 79.79) * mm, v(156.9, 79.58) * mm]});
            skFitSpline(sketch, "E3925", {"points": [v(156.9, 79.58) * mm, v(156.94, 79.37) * mm, v(157.1, 79.2) * mm, v(157.3, 79.17) * mm]});
            skFitSpline(sketch, "E3926", {"points": [v(157.3, 79.17) * mm, v(157.52, 79.14) * mm, v(157.72, 79.23) * mm, v(157.83, 79.42) * mm]});
            skFitSpline(sketch, "E3927", {"points": [v(157.15, 80.1) * mm, v(157.3, 80.19) * mm, v(157.4, 80.35) * mm, v(157.4, 80.53) * mm]});
            skLineSegment(sketch, "E3928", {"start": v(251.5, 87.8) * mm, "end": v(251.5, 80.53) * mm});
            skFitSpline(sketch, "E3929", {"points": [v(157.4, 87.8) * mm, v(157.4, 87.98) * mm, v(157.3, 88.14) * mm, v(157.15, 88.23) * mm]});
            skFitSpline(sketch, "E3930", {"points": [v(157.83, 88.92) * mm, v(157.72, 89.1) * mm, v(157.52, 89.2) * mm, v(157.3, 89.16) * mm]});
            skFitSpline(sketch, "E3931", {"points": [v(157.3, 89.16) * mm, v(157.1, 89.12) * mm, v(156.94, 88.96) * mm, v(156.9, 88.75) * mm]});
            skFitSpline(sketch, "E3932", {"points": [v(156.9, 88.75) * mm, v(156.87, 88.55) * mm, v(156.96, 88.34) * mm, v(157.15, 88.23) * mm]});
            skFitSpline(sketch, "E3933", {"points": [v(157.83, 88.92) * mm, v(157.92, 88.76) * mm, v(158.08, 88.67) * mm, v(158.26, 88.67) * mm]});
            skFitSpline(sketch, "E3934", {"points": [v(241.05, 99.17) * mm, v(241.05, 99.74) * mm, v(240.74, 100.27) * mm, v(240.25, 100.55) * mm]});
            skFitSpline(sketch, "E3935", {"points": [v(240.25, 100.55) * mm, v(239.75, 100.84) * mm, v(239.14, 100.84) * mm, v(238.65, 100.55) * mm]});
            skFitSpline(sketch, "E3936", {"points": [v(238.65, 100.55) * mm, v(238.15, 100.27) * mm, v(237.85, 99.74) * mm, v(237.85, 99.17) * mm]});
            skFitSpline(sketch, "E3937", {"points": [v(237.85, 99.17) * mm, v(237.85, 98.6) * mm, v(238.15, 98.07) * mm, v(238.65, 97.78) * mm]});
            skFitSpline(sketch, "E3938", {"points": [v(238.65, 97.78) * mm, v(239.14, 97.5) * mm, v(239.75, 97.5) * mm, v(240.25, 97.78) * mm]});
            skFitSpline(sketch, "E3939", {"points": [v(240.25, 97.78) * mm, v(240.74, 98.07) * mm, v(241.05, 98.6) * mm, v(241.05, 99.17) * mm]});
            skLineSegment(sketch, "E3940", {"start": v(158.26, 88.67) * mm, "end": v(180.63, 88.67) * mm});
            skFitSpline(sketch, "E3941", {"points": [v(171.05, 99.17) * mm, v(171.05, 99.74) * mm, v(170.74, 100.27) * mm, v(170.25, 100.55) * mm]});
            skFitSpline(sketch, "E3942", {"points": [v(170.25, 100.55) * mm, v(169.75, 100.84) * mm, v(169.14, 100.84) * mm, v(168.65, 100.55) * mm]});
            skFitSpline(sketch, "E3943", {"points": [v(168.65, 100.55) * mm, v(168.15, 100.27) * mm, v(167.85, 99.74) * mm, v(167.85, 99.17) * mm]});
            skFitSpline(sketch, "E3944", {"points": [v(167.85, 99.17) * mm, v(167.85, 98.6) * mm, v(168.15, 98.07) * mm, v(168.65, 97.78) * mm]});
            skFitSpline(sketch, "E3945", {"points": [v(168.65, 97.78) * mm, v(169.14, 97.5) * mm, v(169.75, 97.5) * mm, v(170.25, 97.78) * mm]});
            skFitSpline(sketch, "E3946", {"points": [v(170.25, 97.78) * mm, v(170.74, 98.07) * mm, v(171.05, 98.6) * mm, v(171.05, 99.17) * mm]});
            skLineSegment(sketch, "E3947", {"start": v(181.5, 87.8) * mm, "end": v(181.5, 80.53) * mm});
            skLineSegment(sketch, "E3948", {"start": v(180.63, 79.67) * mm, "end": v(158.26, 79.67) * mm});
            skFitSpline(sketch, "E3949", {"points": [v(250.63, 88.67) * mm, v(250.8, 88.67) * mm, v(250.97, 88.76) * mm, v(251.06, 88.92) * mm]});
            skFitSpline(sketch, "E3950", {"points": [v(251.75, 88.23) * mm, v(251.93, 88.34) * mm, v(252.02, 88.55) * mm, v(251.99, 88.75) * mm]});
            skFitSpline(sketch, "E3951", {"points": [v(251.99, 88.75) * mm, v(251.95, 88.96) * mm, v(251.79, 89.12) * mm, v(251.58, 89.16) * mm]});
            skFitSpline(sketch, "E3952", {"points": [v(251.58, 89.16) * mm, v(251.38, 89.2) * mm, v(251.17, 89.1) * mm, v(251.06, 88.92) * mm]});
            skFitSpline(sketch, "E3953", {"points": [v(251.75, 88.23) * mm, v(251.6, 88.14) * mm, v(251.5, 87.98) * mm, v(251.5, 87.8) * mm]});
            skFitSpline(sketch, "E3954", {"points": [v(251.5, 80.53) * mm, v(251.5, 80.35) * mm, v(251.6, 80.19) * mm, v(251.75, 80.1) * mm]});
            skFitSpline(sketch, "E3955", {"points": [v(251.06, 79.42) * mm, v(251.17, 79.23) * mm, v(251.38, 79.14) * mm, v(251.58, 79.17) * mm]});
            skFitSpline(sketch, "E3956", {"points": [v(251.58, 79.17) * mm, v(251.79, 79.2) * mm, v(251.95, 79.37) * mm, v(251.99, 79.58) * mm]});
            skFitSpline(sketch, "E3957", {"points": [v(251.99, 79.58) * mm, v(252.02, 79.79) * mm, v(251.93, 80) * mm, v(251.75, 80.1) * mm]});
            skFitSpline(sketch, "E3958", {"points": [v(251.06, 79.42) * mm, v(250.97, 79.57) * mm, v(250.8, 79.67) * mm, v(250.63, 79.67) * mm]});
            skLineSegment(sketch, "E3959", {"start": v(157.4, 80.53) * mm, "end": v(157.4, 87.8) * mm});
            skFitSpline(sketch, "E3960", {"points": [v(228.26, 79.67) * mm, v(228.08, 79.67) * mm, v(227.92, 79.57) * mm, v(227.83, 79.42) * mm]});
            skFitSpline(sketch, "E3961", {"points": [v(227.15, 80.1) * mm, v(226.96, 80) * mm, v(226.87, 79.79) * mm, v(226.9, 79.58) * mm]});
            skFitSpline(sketch, "E3962", {"points": [v(226.9, 79.58) * mm, v(226.94, 79.37) * mm, v(227.1, 79.2) * mm, v(227.3, 79.17) * mm]});
            skFitSpline(sketch, "E3963", {"points": [v(227.3, 79.17) * mm, v(227.52, 79.14) * mm, v(227.72, 79.23) * mm, v(227.83, 79.42) * mm]});
            skFitSpline(sketch, "E3964", {"points": [v(227.15, 80.1) * mm, v(227.3, 80.19) * mm, v(227.4, 80.35) * mm, v(227.4, 80.53) * mm]});
            skFitSpline(sketch, "E3965", {"points": [v(227.4, 87.8) * mm, v(227.4, 87.98) * mm, v(227.3, 88.14) * mm, v(227.15, 88.23) * mm]});
            skFitSpline(sketch, "E3966", {"points": [v(227.83, 88.92) * mm, v(227.72, 89.1) * mm, v(227.52, 89.2) * mm, v(227.3, 89.16) * mm]});
            skFitSpline(sketch, "E3967", {"points": [v(227.3, 89.16) * mm, v(227.1, 89.12) * mm, v(226.94, 88.96) * mm, v(226.9, 88.75) * mm]});
            skFitSpline(sketch, "E3968", {"points": [v(226.9, 88.75) * mm, v(226.87, 88.55) * mm, v(226.96, 88.34) * mm, v(227.15, 88.23) * mm]});
            skFitSpline(sketch, "E3969", {"points": [v(227.83, 88.92) * mm, v(227.92, 88.76) * mm, v(228.08, 88.67) * mm, v(228.26, 88.67) * mm]});
            skFitSpline(sketch, "E3970", {"points": [v(181.2, 60.92) * mm, v(180.08, 59.8) * mm, v(179.45, 58.27) * mm, v(179.45, 56.68) * mm]});
            skFitSpline(sketch, "E3971", {"points": [v(229.45, 56.68) * mm, v(229.45, 58.27) * mm, v(228.81, 59.8) * mm, v(227.69, 60.92) * mm]});
            skLineSegment(sketch, "E3972", {"start": v(228.26, 88.67) * mm, "end": v(250.63, 88.67) * mm});
            skFitSpline(sketch, "E3973", {"points": [v(241.05, 69.17) * mm, v(241.05, 69.74) * mm, v(240.74, 70.27) * mm, v(240.25, 70.55) * mm]});
            skFitSpline(sketch, "E3974", {"points": [v(240.25, 70.55) * mm, v(239.75, 70.84) * mm, v(239.14, 70.84) * mm, v(238.65, 70.55) * mm]});
            skFitSpline(sketch, "E3975", {"points": [v(238.65, 70.55) * mm, v(238.15, 70.27) * mm, v(237.85, 69.74) * mm, v(237.85, 69.17) * mm]});
            skFitSpline(sketch, "E3976", {"points": [v(237.85, 69.17) * mm, v(237.85, 68.6) * mm, v(238.15, 68.07) * mm, v(238.65, 67.78) * mm]});
            skFitSpline(sketch, "E3977", {"points": [v(238.65, 67.78) * mm, v(239.14, 67.5) * mm, v(239.75, 67.5) * mm, v(240.25, 67.78) * mm]});
            skFitSpline(sketch, "E3978", {"points": [v(240.25, 67.78) * mm, v(240.74, 68.07) * mm, v(241.05, 68.6) * mm, v(241.05, 69.17) * mm]});
            skLineSegment(sketch, "E3979", {"start": v(250.63, 79.67) * mm, "end": v(228.26, 79.67) * mm});
            skFitSpline(sketch, "E3980", {"points": [v(171.05, 69.17) * mm, v(171.05, 69.74) * mm, v(170.74, 70.27) * mm, v(170.25, 70.55) * mm]});
            skFitSpline(sketch, "E3981", {"points": [v(170.25, 70.55) * mm, v(169.75, 70.84) * mm, v(169.14, 70.84) * mm, v(168.65, 70.55) * mm]});
            skFitSpline(sketch, "E3982", {"points": [v(168.65, 70.55) * mm, v(168.15, 70.27) * mm, v(167.85, 69.74) * mm, v(167.85, 69.17) * mm]});
            skFitSpline(sketch, "E3983", {"points": [v(167.85, 69.17) * mm, v(167.85, 68.6) * mm, v(168.15, 68.07) * mm, v(168.65, 67.78) * mm]});
            skFitSpline(sketch, "E3984", {"points": [v(168.65, 67.78) * mm, v(169.14, 67.5) * mm, v(169.75, 67.5) * mm, v(170.25, 67.78) * mm]});
            skFitSpline(sketch, "E3985", {"points": [v(170.25, 67.78) * mm, v(170.74, 68.07) * mm, v(171.05, 68.6) * mm, v(171.05, 69.17) * mm]});
            skLineSegment(sketch, "E3986", {"start": v(227.4, 80.53) * mm, "end": v(227.4, 87.8) * mm});
            skLineSegment(sketch, "E3987", {"start": v(197.69, 77.4) * mm, "end": v(181.2, 60.92) * mm});
            skLineSegment(sketch, "E3988", {"start": v(227.69, 60.92) * mm, "end": v(211.2, 77.4) * mm});
            skFitSpline(sketch, "E3989", {"points": [v(284.96, 89.17) * mm, v(286.55, 89.17) * mm, v(288.08, 89.8) * mm, v(289.2, 90.92) * mm]});
            skFitSpline(sketch, "E3990", {"points": [v(119.69, 90.92) * mm, v(120.81, 89.8) * mm, v(122.34, 89.17) * mm, v(123.93, 89.17) * mm]});
            skFitSpline(sketch, "E3991", {"points": [v(318.95, -5.78) * mm, v(321.68, -5.78) * mm, v(323.9, -3.57) * mm, v(323.9, -0.83) * mm]});
            skFitSpline(sketch, "E3992", {"points": [v(323.9, -0.83) * mm, v(323.9, 1.9) * mm, v(321.68, 4.12) * mm, v(318.95, 4.12) * mm]});
            skFitSpline(sketch, "E3993", {"points": [v(320.55, -0.83) * mm, v(320.55, -0.26) * mm, v(320.24, 0.27) * mm, v(319.75, 0.55) * mm]});
            skFitSpline(sketch, "E3994", {"points": [v(319.75, 0.55) * mm, v(319.25, 0.84) * mm, v(318.64, 0.84) * mm, v(318.15, 0.55) * mm]});
            skFitSpline(sketch, "E3995", {"points": [v(318.15, 0.55) * mm, v(317.65, 0.27) * mm, v(317.35, -0.26) * mm, v(317.35, -0.83) * mm]});
            skFitSpline(sketch, "E3996", {"points": [v(317.35, -0.83) * mm, v(317.35, -1.4) * mm, v(317.65, -1.93) * mm, v(318.15, -2.22) * mm]});
            skFitSpline(sketch, "E3997", {"points": [v(318.15, -2.22) * mm, v(318.64, -2.5) * mm, v(319.25, -2.5) * mm, v(319.75, -2.22) * mm]});
            skFitSpline(sketch, "E3998", {"points": [v(319.75, -2.22) * mm, v(320.24, -1.93) * mm, v(320.55, -1.4) * mm, v(320.55, -0.83) * mm]});
            skLineSegment(sketch, "E3999", {"start": v(179.45, 56.68) * mm, "end": v(179.45, 41.65) * mm});
            skLineSegment(sketch, "E4000", {"start": v(229.45, 41.65) * mm, "end": v(229.45, 56.68) * mm});
            skLineSegment(sketch, "E4001", {"start": v(138.96, 89.17) * mm, "end": v(123.93, 89.17) * mm});
            skFitSpline(sketch, "E4002", {"points": [v(289.45, 14.12) * mm, v(289.45, 11.46) * mm, v(290.5, 8.92) * mm, v(292.37, 7.05) * mm]});
            skFitSpline(sketch, "E4003", {"points": [v(292.37, 7.05) * mm, v(294.25, 5.17) * mm, v(296.8, 4.12) * mm, v(299.45, 4.12) * mm]});
            skLineSegment(sketch, "E4004", {"start": v(284.96, 89.17) * mm, "end": v(269.93, 89.17) * mm});
            skFitSpline(sketch, "E4005", {"points": [v(160.55, 75.67) * mm, v(160.02, 75.67) * mm, v(159.52, 75.39) * mm, v(159.25, 74.92) * mm]});
            skFitSpline(sketch, "E4006", {"points": [v(159.25, 74.92) * mm, v(158.98, 74.46) * mm, v(158.98, 73.88) * mm, v(159.25, 73.42) * mm]});
            skFitSpline(sketch, "E4007", {"points": [v(159.25, 73.42) * mm, v(159.52, 72.95) * mm, v(160.02, 72.67) * mm, v(160.55, 72.67) * mm]});
            skFitSpline(sketch, "E4008", {"points": [v(160.55, 72.67) * mm, v(161.1, 72.67) * mm, v(161.59, 72.95) * mm, v(161.86, 73.42) * mm]});
            skFitSpline(sketch, "E4009", {"points": [v(161.86, 73.42) * mm, v(162.12, 73.88) * mm, v(162.12, 74.46) * mm, v(161.86, 74.92) * mm]});
            skFitSpline(sketch, "E4010", {"points": [v(161.86, 74.92) * mm, v(161.59, 75.39) * mm, v(161.1, 75.67) * mm, v(160.55, 75.67) * mm]});
            skFitSpline(sketch, "E4011", {"points": [v(160.55, 95.67) * mm, v(160.02, 95.67) * mm, v(159.52, 95.38) * mm, v(159.25, 94.92) * mm]});
            skFitSpline(sketch, "E4012", {"points": [v(159.25, 94.92) * mm, v(158.98, 94.46) * mm, v(158.98, 93.88) * mm, v(159.25, 93.42) * mm]});
            skFitSpline(sketch, "E4013", {"points": [v(159.25, 93.42) * mm, v(159.52, 92.95) * mm, v(160.02, 92.67) * mm, v(160.55, 92.67) * mm]});
            skFitSpline(sketch, "E4014", {"points": [v(160.55, 92.67) * mm, v(161.1, 92.67) * mm, v(161.59, 92.95) * mm, v(161.86, 93.42) * mm]});
            skFitSpline(sketch, "E4015", {"points": [v(161.86, 93.42) * mm, v(162.12, 93.88) * mm, v(162.12, 94.46) * mm, v(161.86, 94.92) * mm]});
            skFitSpline(sketch, "E4016", {"points": [v(161.86, 94.92) * mm, v(161.59, 95.38) * mm, v(161.1, 95.67) * mm, v(160.55, 95.67) * mm]});
            skFitSpline(sketch, "E4017", {"points": [v(175.55, 75.67) * mm, v(175.02, 75.67) * mm, v(174.52, 75.39) * mm, v(174.25, 74.92) * mm]});
            skFitSpline(sketch, "E4018", {"points": [v(174.25, 74.92) * mm, v(173.98, 74.46) * mm, v(173.98, 73.88) * mm, v(174.25, 73.42) * mm]});
            skFitSpline(sketch, "E4019", {"points": [v(174.25, 73.42) * mm, v(174.52, 72.95) * mm, v(175.02, 72.67) * mm, v(175.55, 72.67) * mm]});
            skFitSpline(sketch, "E4020", {"points": [v(175.55, 72.67) * mm, v(176.1, 72.67) * mm, v(176.59, 72.95) * mm, v(176.86, 73.42) * mm]});
            skFitSpline(sketch, "E4021", {"points": [v(176.86, 73.42) * mm, v(177.12, 73.88) * mm, v(177.12, 74.46) * mm, v(176.86, 74.92) * mm]});
            skFitSpline(sketch, "E4022", {"points": [v(176.86, 74.92) * mm, v(176.59, 75.39) * mm, v(176.1, 75.67) * mm, v(175.55, 75.67) * mm]});
            skLineSegment(sketch, "E4023", {"start": v(299.45, 4.12) * mm, "end": v(318.95, 4.12) * mm});
            skFitSpline(sketch, "E4024", {"points": [v(175.55, 95.67) * mm, v(175.02, 95.67) * mm, v(174.52, 95.38) * mm, v(174.25, 94.92) * mm]});
            skFitSpline(sketch, "E4025", {"points": [v(174.25, 94.92) * mm, v(173.98, 94.46) * mm, v(173.98, 93.88) * mm, v(174.25, 93.42) * mm]});
            skFitSpline(sketch, "E4026", {"points": [v(174.25, 93.42) * mm, v(174.52, 92.95) * mm, v(175.02, 92.67) * mm, v(175.55, 92.67) * mm]});
            skFitSpline(sketch, "E4027", {"points": [v(175.55, 92.67) * mm, v(176.1, 92.67) * mm, v(176.59, 92.95) * mm, v(176.86, 93.42) * mm]});
            skFitSpline(sketch, "E4028", {"points": [v(176.86, 93.42) * mm, v(177.12, 93.88) * mm, v(177.12, 94.46) * mm, v(176.86, 94.92) * mm]});
            skFitSpline(sketch, "E4029", {"points": [v(176.86, 94.92) * mm, v(176.59, 95.38) * mm, v(176.1, 95.67) * mm, v(175.55, 95.67) * mm]});
            skLineSegment(sketch, "E4030", {"start": v(318.95, -5.78) * mm, "end": v(299.45, -5.78) * mm});
            skFitSpline(sketch, "E4031", {"points": [v(233.74, 75.67) * mm, v(233.2, 75.67) * mm, v(232.7, 75.39) * mm, v(232.44, 74.92) * mm]});
            skFitSpline(sketch, "E4032", {"points": [v(232.44, 74.92) * mm, v(232.17, 74.46) * mm, v(232.17, 73.88) * mm, v(232.44, 73.42) * mm]});
            skFitSpline(sketch, "E4033", {"points": [v(232.44, 73.42) * mm, v(232.7, 72.95) * mm, v(233.2, 72.67) * mm, v(233.74, 72.67) * mm]});
            skFitSpline(sketch, "E4034", {"points": [v(233.74, 72.67) * mm, v(234.28, 72.67) * mm, v(234.78, 72.95) * mm, v(235.04, 73.42) * mm]});
            skFitSpline(sketch, "E4035", {"points": [v(235.04, 73.42) * mm, v(235.31, 73.88) * mm, v(235.31, 74.46) * mm, v(235.04, 74.92) * mm]});
            skFitSpline(sketch, "E4036", {"points": [v(235.04, 74.92) * mm, v(234.78, 75.39) * mm, v(234.28, 75.67) * mm, v(233.74, 75.67) * mm]});
            skFitSpline(sketch, "E4037", {"points": [v(233.74, 95.67) * mm, v(233.2, 95.67) * mm, v(232.7, 95.38) * mm, v(232.44, 94.92) * mm]});
            skFitSpline(sketch, "E4038", {"points": [v(232.44, 94.92) * mm, v(232.17, 94.46) * mm, v(232.17, 93.88) * mm, v(232.44, 93.42) * mm]});
            skFitSpline(sketch, "E4039", {"points": [v(232.44, 93.42) * mm, v(232.7, 92.95) * mm, v(233.2, 92.67) * mm, v(233.74, 92.67) * mm]});
            skFitSpline(sketch, "E4040", {"points": [v(233.74, 92.67) * mm, v(234.28, 92.67) * mm, v(234.78, 92.95) * mm, v(235.04, 93.42) * mm]});
            skFitSpline(sketch, "E4041", {"points": [v(235.04, 93.42) * mm, v(235.31, 93.88) * mm, v(235.31, 94.46) * mm, v(235.04, 94.92) * mm]});
            skFitSpline(sketch, "E4042", {"points": [v(235.04, 94.92) * mm, v(234.78, 95.38) * mm, v(234.28, 95.67) * mm, v(233.74, 95.67) * mm]});
            skFitSpline(sketch, "E4043", {"points": [v(248.74, 75.67) * mm, v(248.2, 75.67) * mm, v(247.7, 75.39) * mm, v(247.44, 74.92) * mm]});
            skFitSpline(sketch, "E4044", {"points": [v(247.44, 74.92) * mm, v(247.17, 74.46) * mm, v(247.17, 73.88) * mm, v(247.44, 73.42) * mm]});
            skFitSpline(sketch, "E4045", {"points": [v(247.44, 73.42) * mm, v(247.7, 72.95) * mm, v(248.2, 72.67) * mm, v(248.74, 72.67) * mm]});
            skFitSpline(sketch, "E4046", {"points": [v(248.74, 72.67) * mm, v(249.28, 72.67) * mm, v(249.78, 72.95) * mm, v(250.04, 73.42) * mm]});
            skFitSpline(sketch, "E4047", {"points": [v(250.04, 73.42) * mm, v(250.31, 73.88) * mm, v(250.31, 74.46) * mm, v(250.04, 74.92) * mm]});
            skFitSpline(sketch, "E4048", {"points": [v(250.04, 74.92) * mm, v(249.78, 75.39) * mm, v(249.28, 75.67) * mm, v(248.74, 75.67) * mm]});
            skFitSpline(sketch, "E4049", {"points": [v(248.74, 95.67) * mm, v(248.2, 95.67) * mm, v(247.7, 95.38) * mm, v(247.44, 94.92) * mm]});
            skFitSpline(sketch, "E4050", {"points": [v(247.44, 94.92) * mm, v(247.17, 94.46) * mm, v(247.17, 93.88) * mm, v(247.44, 93.42) * mm]});
            skFitSpline(sketch, "E4051", {"points": [v(247.44, 93.42) * mm, v(247.7, 92.95) * mm, v(248.2, 92.67) * mm, v(248.74, 92.67) * mm]});
            skFitSpline(sketch, "E4052", {"points": [v(248.74, 92.67) * mm, v(249.28, 92.67) * mm, v(249.78, 92.95) * mm, v(250.04, 93.42) * mm]});
            skFitSpline(sketch, "E4053", {"points": [v(250.04, 93.42) * mm, v(250.31, 93.88) * mm, v(250.31, 94.46) * mm, v(250.04, 94.92) * mm]});
            skFitSpline(sketch, "E4054", {"points": [v(250.04, 94.92) * mm, v(249.78, 95.38) * mm, v(249.28, 95.67) * mm, v(248.74, 95.67) * mm]});
            skFitSpline(sketch, "E4055", {"points": [v(233.74, -94.34) * mm, v(233.2, -94.34) * mm, v(232.71, -94.62) * mm, v(232.44, -95.09) * mm]});
            skFitSpline(sketch, "E4056", {"points": [v(232.44, -95.09) * mm, v(232.17, -95.55) * mm, v(232.17, -96.12) * mm, v(232.44, -96.59) * mm]});
            skFitSpline(sketch, "E4057", {"points": [v(232.44, -96.59) * mm, v(232.71, -97.05) * mm, v(233.2, -97.34) * mm, v(233.74, -97.34) * mm]});
            skFitSpline(sketch, "E4058", {"points": [v(233.74, -97.34) * mm, v(234.28, -97.34) * mm, v(234.77, -97.05) * mm, v(235.04, -96.59) * mm]});
            skFitSpline(sketch, "E4059", {"points": [v(235.04, -96.59) * mm, v(235.31, -96.12) * mm, v(235.31, -95.55) * mm, v(235.04, -95.09) * mm]});
            skFitSpline(sketch, "E4060", {"points": [v(235.04, -95.09) * mm, v(234.77, -94.62) * mm, v(234.28, -94.34) * mm, v(233.74, -94.34) * mm]});
            skFitSpline(sketch, "E4061", {"points": [v(233.74, -74.34) * mm, v(233.2, -74.34) * mm, v(232.71, -74.62) * mm, v(232.44, -75.09) * mm]});
            skFitSpline(sketch, "E4062", {"points": [v(232.44, -75.09) * mm, v(232.17, -75.55) * mm, v(232.17, -76.12) * mm, v(232.44, -76.59) * mm]});
            skFitSpline(sketch, "E4063", {"points": [v(232.44, -76.59) * mm, v(232.71, -77.05) * mm, v(233.2, -77.34) * mm, v(233.74, -77.34) * mm]});
            skFitSpline(sketch, "E4064", {"points": [v(233.74, -77.34) * mm, v(234.28, -77.34) * mm, v(234.77, -77.05) * mm, v(235.04, -76.59) * mm]});
            skFitSpline(sketch, "E4065", {"points": [v(235.04, -76.59) * mm, v(235.31, -76.12) * mm, v(235.31, -75.55) * mm, v(235.04, -75.09) * mm]});
            skFitSpline(sketch, "E4066", {"points": [v(235.04, -75.09) * mm, v(234.77, -74.62) * mm, v(234.28, -74.34) * mm, v(233.74, -74.34) * mm]});
            skFitSpline(sketch, "E4067", {"points": [v(248.74, -94.34) * mm, v(248.2, -94.34) * mm, v(247.71, -94.62) * mm, v(247.44, -95.09) * mm]});
            skFitSpline(sketch, "E4068", {"points": [v(247.44, -95.09) * mm, v(247.17, -95.55) * mm, v(247.17, -96.12) * mm, v(247.44, -96.59) * mm]});
            skFitSpline(sketch, "E4069", {"points": [v(247.44, -96.59) * mm, v(247.71, -97.05) * mm, v(248.2, -97.34) * mm, v(248.74, -97.34) * mm]});
            skFitSpline(sketch, "E4070", {"points": [v(248.74, -97.34) * mm, v(249.28, -97.34) * mm, v(249.77, -97.05) * mm, v(250.04, -96.59) * mm]});
            skFitSpline(sketch, "E4071", {"points": [v(250.04, -96.59) * mm, v(250.31, -96.12) * mm, v(250.31, -95.55) * mm, v(250.04, -95.09) * mm]});
            skFitSpline(sketch, "E4072", {"points": [v(250.04, -95.09) * mm, v(249.77, -94.62) * mm, v(249.28, -94.34) * mm, v(248.74, -94.34) * mm]});
            skFitSpline(sketch, "E4073", {"points": [v(248.74, -74.34) * mm, v(248.2, -74.34) * mm, v(247.71, -74.62) * mm, v(247.44, -75.09) * mm]});
            skFitSpline(sketch, "E4074", {"points": [v(247.44, -75.09) * mm, v(247.17, -75.55) * mm, v(247.17, -76.12) * mm, v(247.44, -76.59) * mm]});
            skFitSpline(sketch, "E4075", {"points": [v(247.44, -76.59) * mm, v(247.71, -77.05) * mm, v(248.2, -77.34) * mm, v(248.74, -77.34) * mm]});
            skFitSpline(sketch, "E4076", {"points": [v(248.74, -77.34) * mm, v(249.28, -77.34) * mm, v(249.77, -77.05) * mm, v(250.04, -76.59) * mm]});
            skFitSpline(sketch, "E4077", {"points": [v(250.04, -76.59) * mm, v(250.31, -76.12) * mm, v(250.31, -75.55) * mm, v(250.04, -75.09) * mm]});
            skFitSpline(sketch, "E4078", {"points": [v(250.04, -75.09) * mm, v(249.77, -74.62) * mm, v(249.28, -74.34) * mm, v(248.74, -74.34) * mm]});
            skFitSpline(sketch, "E4079", {"points": [v(160.55, -94.34) * mm, v(160.02, -94.34) * mm, v(159.52, -94.62) * mm, v(159.25, -95.09) * mm]});
            skFitSpline(sketch, "E4080", {"points": [v(159.25, -95.09) * mm, v(158.99, -95.55) * mm, v(158.99, -96.12) * mm, v(159.25, -96.59) * mm]});
            skFitSpline(sketch, "E4081", {"points": [v(159.25, -96.59) * mm, v(159.52, -97.05) * mm, v(160.02, -97.34) * mm, v(160.55, -97.34) * mm]});
            skFitSpline(sketch, "E4082", {"points": [v(160.55, -97.34) * mm, v(161.1, -97.34) * mm, v(161.59, -97.05) * mm, v(161.85, -96.59) * mm]});
            skFitSpline(sketch, "E4083", {"points": [v(161.85, -96.59) * mm, v(162.12, -96.12) * mm, v(162.12, -95.55) * mm, v(161.85, -95.09) * mm]});
            skFitSpline(sketch, "E4084", {"points": [v(161.85, -95.09) * mm, v(161.59, -94.62) * mm, v(161.1, -94.34) * mm, v(160.55, -94.34) * mm]});
            skFitSpline(sketch, "E4085", {"points": [v(160.55, -74.34) * mm, v(160.02, -74.34) * mm, v(159.52, -74.62) * mm, v(159.25, -75.09) * mm]});
            skFitSpline(sketch, "E4086", {"points": [v(159.25, -75.09) * mm, v(158.99, -75.55) * mm, v(158.99, -76.12) * mm, v(159.25, -76.59) * mm]});
            skFitSpline(sketch, "E4087", {"points": [v(159.25, -76.59) * mm, v(159.52, -77.05) * mm, v(160.02, -77.34) * mm, v(160.55, -77.34) * mm]});
            skFitSpline(sketch, "E4088", {"points": [v(160.55, -77.34) * mm, v(161.1, -77.34) * mm, v(161.59, -77.05) * mm, v(161.85, -76.59) * mm]});
            skFitSpline(sketch, "E4089", {"points": [v(161.85, -76.59) * mm, v(162.12, -76.12) * mm, v(162.12, -75.55) * mm, v(161.85, -75.09) * mm]});
            skFitSpline(sketch, "E4090", {"points": [v(161.85, -75.09) * mm, v(161.59, -74.62) * mm, v(161.1, -74.34) * mm, v(160.55, -74.34) * mm]});
            skFitSpline(sketch, "E4091", {"points": [v(175.55, -94.34) * mm, v(175.02, -94.34) * mm, v(174.52, -94.62) * mm, v(174.25, -95.09) * mm]});
            skFitSpline(sketch, "E4092", {"points": [v(174.25, -95.09) * mm, v(173.99, -95.55) * mm, v(173.99, -96.12) * mm, v(174.25, -96.59) * mm]});
            skFitSpline(sketch, "E4093", {"points": [v(174.25, -96.59) * mm, v(174.52, -97.05) * mm, v(175.02, -97.34) * mm, v(175.55, -97.34) * mm]});
            skFitSpline(sketch, "E4094", {"points": [v(175.55, -97.34) * mm, v(176.09, -97.34) * mm, v(176.59, -97.05) * mm, v(176.85, -96.59) * mm]});
            skFitSpline(sketch, "E4095", {"points": [v(176.85, -96.59) * mm, v(177.12, -96.12) * mm, v(177.12, -95.55) * mm, v(176.85, -95.09) * mm]});
            skFitSpline(sketch, "E4096", {"points": [v(176.85, -95.09) * mm, v(176.59, -94.62) * mm, v(176.09, -94.34) * mm, v(175.55, -94.34) * mm]});
            skFitSpline(sketch, "E4097", {"points": [v(175.55, -74.34) * mm, v(175.02, -74.34) * mm, v(174.52, -74.62) * mm, v(174.25, -75.09) * mm]});
            skFitSpline(sketch, "E4098", {"points": [v(174.25, -75.09) * mm, v(173.99, -75.55) * mm, v(173.99, -76.12) * mm, v(174.25, -76.59) * mm]});
            skFitSpline(sketch, "E4099", {"points": [v(174.25, -76.59) * mm, v(174.52, -77.05) * mm, v(175.02, -77.34) * mm, v(175.55, -77.34) * mm]});
            skFitSpline(sketch, "E4100", {"points": [v(175.55, -77.34) * mm, v(176.09, -77.34) * mm, v(176.59, -77.05) * mm, v(176.85, -76.59) * mm]});
            skFitSpline(sketch, "E4101", {"points": [v(176.85, -76.59) * mm, v(177.12, -76.12) * mm, v(177.12, -75.55) * mm, v(176.85, -75.09) * mm]});
            skFitSpline(sketch, "E4102", {"points": [v(176.85, -75.09) * mm, v(176.59, -74.62) * mm, v(176.09, -74.34) * mm, v(175.55, -74.34) * mm]});
            skSolve(sketch);
        }
        {
            var Q0;
            Q0=makeQuery(id+"F0.imprint","IMPRINT",FACE,{"disambiguationData":[TD([[makeQuery(id+"F0.imprint","IMPRINT",EDGE,{"derivedFrom":sQuery(id+"F0.wireOp",EDGE,"E15")}),-1.0]])]});
            var Q1;
            Q1=makeQuery(id+"F0.imprint","IMPRINT",FACE,{"disambiguationData":[TD([[makeQuery(id+"F0.imprint","IMPRINT",EDGE,{"derivedFrom":sQuery(id+"F0.wireOp",EDGE,"E20")}),-1.0]])]});
            var Q2;
            Q2=makeQuery(id+"F0.imprint","IMPRINT",FACE,{"disambiguationData":[TD([[makeQuery(id+"F0.imprint","IMPRINT",EDGE,{"derivedFrom":sQuery(id+"F0.wireOp",EDGE,"E2373")}),1.0]])]});
            var Q3;
            Q3=makeQuery(id+"F0.imprint","IMPRINT",FACE,{"disambiguationData":[TD([[makeQuery(id+"F0.imprint","IMPRINT",EDGE,{"derivedFrom":sQuery(id+"F0.wireOp",EDGE,"E2059")}),1.0]])]});
            var Q4;
            Q4=makeQuery(id+"F0.imprint","IMPRINT",FACE,{"disambiguationData":[TD([[makeQuery(id+"F0.imprint","IMPRINT",EDGE,{"derivedFrom":sQuery(id+"F0.wireOp",EDGE,"E2879")}),1.0]])]});
            var Q5;
            Q5=makeQuery(id+"F0.imprint","IMPRINT",FACE,{"disambiguationData":[TD([[makeQuery(id+"F0.imprint","IMPRINT",EDGE,{"derivedFrom":sQuery(id+"F0.wireOp",EDGE,"E22")}),1.0]])]});
            var Q6;
            Q6=makeQuery(id+"F0.imprint","IMPRINT",FACE,{"disambiguationData":[TD([[makeQuery(id+"F0.imprint","IMPRINT",EDGE,{"derivedFrom":sQuery(id+"F0.wireOp",EDGE,"E3678")}),-1.0]])]});
            extrude(context, id + "F1", {"entities" : qUnion([Q0, Q1, Q2, Q3, Q4, Q5, Q6]), "depth" : 3 * mm, "offsetDistance" : 25 * mm});
        }
    });
